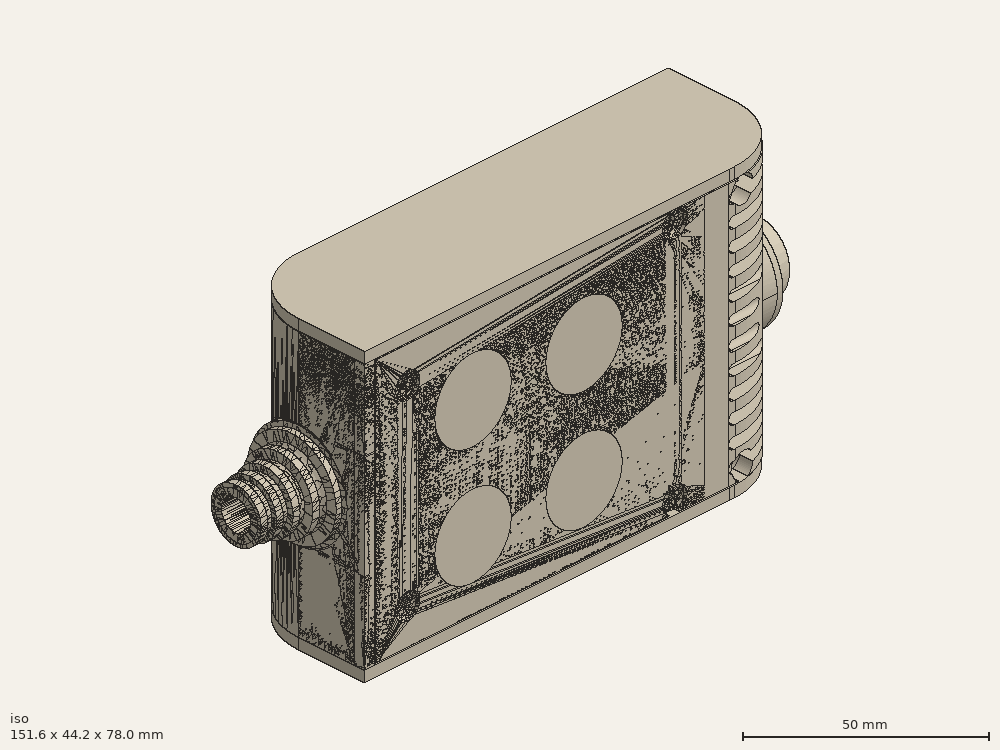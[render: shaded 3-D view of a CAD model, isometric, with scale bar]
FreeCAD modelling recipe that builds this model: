
FCSTD DOCUMENT  (FreeCAD 0.19R0.19.2)
Label: enclosure_198FCStd
License: All rights reserved
LicenseURL: http://en.wikipedia.org/wiki/All_rights_reserved
objects: Part::Revolution×152, Part::MultiFuse×146, Part::Feature×146, Sketcher::SketchObject×84, Part::Cut×70, Part::Cylinder×70, Part::Extrusion×67, Part::Fillet×58, Part::Box×36, App::MeasureDistance×4, PartDesign::Body×2, Image::ImagePlane×1
note: 831 computed .brp shape members not serialized (recipe doc carries the construction recipe); baked Part::Feature solids carry a one-line shape summary decoded from their .brp

FEATURE [Sketcher::SketchObject] Sketch  label="topSketch"
  FullyConstrained = true
  sketch-geometry (20):
    g0: LineSegment StartX=5.21097e-06 StartY=3 StartZ=0 EndX=5.21097e-06 EndY=19 EndZ=0
    g1: ArcOfCircle CenterX=19 CenterY=19 CenterZ=0 NormalX=0 NormalY=0 NormalZ=1 AngleXU=0 Radius=19 StartAngle=1.5708 EndAngle=3.14159
    g2: ArcOfCircle CenterX=19 CenterY=19 CenterZ=0 NormalX=0 NormalY=0 NormalZ=1 AngleXU=0 Radius=16 StartAngle=1.5708 EndAngle=3.14159
    g3: LineSegment StartX=114 StartY=35 StartZ=0 EndX=19 EndY=35 EndZ=0
    g4: LineSegment StartX=5.21097e-06 StartY=3 StartZ=0 EndX=5.21097e-06 EndY=0 EndZ=0
    g5: LineSegment StartX=3 StartY=0 StartZ=0 EndX=5.21097e-06 EndY=0 EndZ=0
    g6: LineSegment StartX=3 StartY=19 StartZ=0 EndX=3 EndY=0 EndZ=0
    g7: LineSegment StartX=19 StartY=38 StartZ=0 EndX=124 EndY=38 EndZ=0
    g8: Circle CenterX=119 CenterY=35 CenterZ=0 NormalX=0 NormalY=0 NormalZ=1 AngleXU=0 Radius=1
    g9: Circle CenterX=121 CenterY=35 CenterZ=0 NormalX=0 NormalY=0 NormalZ=1 AngleXU=0 Radius=1
    g10: Circle CenterX=121 CenterY=33 CenterZ=0 NormalX=0 NormalY=0 NormalZ=1 AngleXU=0 Radius=1
    g11: BSplineCurve PolesCount=3 KnotsCount=2 Degree=2 IsPeriodic=0
    g12: GeomPoint X=119 Y=35 Z=0
    g13: GeomPoint X=121 Y=33 Z=0
    g14: LineSegment StartX=119 StartY=35 StartZ=0 EndX=114 EndY=35 EndZ=0
    g15: ArcOfCircle CenterX=105 CenterY=19 CenterZ=0 NormalX=0 NormalY=0 NormalZ=1 AngleXU=0 Radius=19 StartAngle=5.7297 EndAngle=6.28319
    g16: ArcOfCircle CenterX=105 CenterY=19 CenterZ=0 NormalX=0 NormalY=0 NormalZ=1 AngleXU=0 Radius=16 StartAngle=5.60905 EndAngle=6.28319
    g17: LineSegment StartX=121 StartY=33 StartZ=0 EndX=121 EndY=19 EndZ=0
    g18: LineSegment StartX=124 StartY=38 StartZ=0 EndX=124 EndY=19 EndZ=0
    g19: LineSegment StartX=117.5 StartY=9.01251 StartZ=0 EndX=121.163 EndY=9.0125 EndZ=0
  constraints (46):
    c: Vertical(g0)
    c: Block(g0)
    c: Coincident(g1,g0)
    c: Block(g1)
    c: Coincident(g2,g1)
    c: Block(g2)
    c: Coincident(g3,g2)
    c: Horizontal(g3)
    c: Tangent(g3,g2)
    c: Coincident(g4,g0)
    c: Distance(g4) = 3
    c: Vertical(g4)
    c: Coincident(g5,g4)
    c: Horizontal(g5)
    c: Coincident(g6,g2)
    c: Coincident(g6,g5)
    c: Vertical(g6)
    c: Horizontal(g7)
    c: Distance(g7) = 105
    c: Coincident(g7,g1)
    c: Block(g3)
    c: Weight(g8) = 1
    c: Equal(g8,g9)
    c: Equal(g8,g10)
    c: InternalAlignment(g8,g11)
    c: InternalAlignment(g9,g11)
    c: InternalAlignment(g10,g11)
    c: InternalAlignment(g12,g11)
    c: InternalAlignment(g13,g11)
    c: Block(g11)
    c: Coincident(g14,g11)
    c: Coincident(g14,g3)
    c: Horizontal(g14)
    c: Block(g15)
    c: Coincident(g16,g15)
    c: Block(g16)
    c: Coincident(g17,g11)
    c: Coincident(g17,g16)
    c: Vertical(g17)
    c: Distance(g17) = 14
    c: Coincident(g18,g7)
    c: Coincident(g18,g15)
    c: Vertical(g18)
    c: Distance(g18) = 19
    c: Coincident(g19,g16)
    c: Coincident(g19,g15)
FEATURE [Sketcher::SketchObject] Sketch001  label="bottomSketch"
  FullyConstrained = true
  sketch-geometry (32):
    g0: LineSegment StartX=3.3 StartY=-6.03275e-07 StartZ=0 EndX=98 EndY=-6.03275e-07 EndZ=0
    g1: ArcOfCircle CenterX=98 CenterY=19 CenterZ=0 NormalX=0 NormalY=0 NormalZ=1 AngleXU=0 Radius=19 StartAngle=4.71239 EndAngle=5.71103
    g2: LineSegment StartX=6.3 StartY=8 StartZ=0 EndX=3.3 EndY=8 EndZ=0
    g3: LineSegment StartX=3.3 StartY=8 StartZ=0 EndX=3.3 EndY=-6.03275e-07 EndZ=0
    g4: ArcOfCircle CenterX=8.3 CenterY=5 CenterZ=0 NormalX=0 NormalY=0 NormalZ=1 AngleXU=0 Radius=2 StartAngle=3.14159 EndAngle=4.71239
    g5: LineSegment StartX=6.3 StartY=8 StartZ=0 EndX=6.3 EndY=5 EndZ=0
    g6: ArcOfCircle CenterX=98 CenterY=19 CenterZ=0 NormalX=0 NormalY=0 NormalZ=1 AngleXU=0 Radius=12.7 StartAngle=4.71239 EndAngle=6.28319
    g7: LineSegment StartX=94.7 StartY=3 StartZ=0 EndX=8.3 EndY=3 EndZ=0
    g8-g12: Circle x5 (B-spline internal-alignment scaffolding for g13; pole/knot coordinates omitted)
    g13: BSplineCurve PolesCount=5 KnotsCount=3 Degree=3 IsPeriodic=0
    g14: GeomPoint X=98 Y=6.3 Z=0
    g15: GeomPoint X=96.3938 Y=4.71946 Z=0
    g16: GeomPoint X=94.7 Y=3 Z=0
    g17-g23: Circle x7 (B-spline internal-alignment scaffolding for g24; pole/knot coordinates omitted)
    g24: BSplineCurve PolesCount=7 KnotsCount=5 Degree=3 IsPeriodic=0
    g25-g29: GeomPoint x5 (B-spline internal-alignment scaffolding for g24; pole/knot coordinates omitted)
    g30: ArcOfCircle CenterX=98 CenterY=19 CenterZ=0 NormalX=0 NormalY=0 NormalZ=1 AngleXU=0 Radius=15.7 StartAngle=5.81226 EndAngle=6.28319
    g31: LineSegment StartX=110.7 StartY=19 StartZ=0 EndX=113.7 EndY=19 EndZ=0
  constraints (41):
    c: Horizontal(g0)
    c: Coincident(g1,g0)
    c: Block(g1)
    c: Horizontal(g2)
    c: Distance(g2) = 3
    c: Coincident(g3,g2)
    c: Vertical(g3)
    c: Coincident(g3,g0)
    c: Block(g4)
    c: Block(g2)
    c: Coincident(g5,g2)
    c: Coincident(g5,g4)
    c: Vertical(g5)
    c: Coincident(g6,g1)
    c: Block(g6)
    c: Coincident(g7,g4)
    c: Horizontal(g7)
    c: Block(g0)
    c: Block(g7)
    c: Block(g3)
    c: Coincident(g13,g6)
    c: Weight(g8) = 1
    c: Equal(g8, g9-g12) x4
    c: Coincident(g13,g7)
    c: InternalAlignment(g8-g12 -> g13) x5
    c: InternalAlignment(g14,g13)
    c: InternalAlignment(g15,g13)
    c: InternalAlignment(g16,g13)
    c: Block(g13)
    c: Weight(g17) = 1
    c: Equal(g17, g18-g23) x6
    c: Coincident(g24,g1)
    c: InternalAlignment(g17-g23 -> g24) x7
    c: InternalAlignment(g25-g29 -> g24) x5
    c: Block(g24)
    c: Coincident(g30,g24)
    c: Coincident(g31,g6)
    c: Coincident(g31,g30)
    c: Horizontal(g31)
    c: Block(g31)
    c: Block(g30)
FEATURE [Part::Extrusion] Extrude  label="top"
  Base = -> Sketch
  Dir = (0,0,1)
  DirMode = 2
  FaceMakerClass = Part::FaceMakerBullseye
  LengthFwd = 72
  LengthRev = 0
  Solid = true
  Symmetric = false
FEATURE [Part::Extrusion] Extrude001  label="bottom"
  Base = -> Sketch001
  Dir = (0,0,1)
  DirMode = 2
  FaceMakerClass = Part::FaceMakerBullseye
  LengthFwd = 71.4
  LengthRev = 0
  Placement = pos=(0,0,0.3) rot=(0,0,1;0rad)
  Solid = true
  Symmetric = false
FEATURE [Sketcher::SketchObject] Sketch002  label="topSketch001"
  FullyConstrained = true
  sketch-geometry (8):
    g0: ArcOfCircle CenterX=19 CenterY=19.0975 CenterZ=0 NormalX=0 NormalY=0 NormalZ=1 AngleXU=0 Radius=18.9025 StartAngle=1.5708 EndAngle=3.14674
    g1: LineSegment StartX=0.0977805 StartY=19.0003 StartZ=0 EndX=0.0977805 EndY=0.000251602 EndZ=0
    g2: LineSegment StartX=19 StartY=38 StartZ=0 EndX=124 EndY=38 EndZ=0
    g3: LineSegment StartX=0.0977805 StartY=0.000251602 StartZ=0 EndX=105.098 EndY=0.000251602 EndZ=0
    g4: LineSegment StartX=124 StartY=38 StartZ=0 EndX=125.616 EndY=38 EndZ=0
    g5: LineSegment StartX=105.098 StartY=0.000251602 StartZ=0 EndX=106.713 EndY=0.000251602 EndZ=0
    g6: ArcOfCircle CenterX=106.616 CenterY=19 CenterZ=0 NormalX=0 NormalY=0 NormalZ=1 AngleXU=0 Radius=19 StartAngle=4.71754 EndAngle=6.28319
    g7: LineSegment StartX=125.616 StartY=38 StartZ=0 EndX=125.616 EndY=19 EndZ=0
  constraints (21):
    c: Block(g0)
    c: Coincident(g1,g0)
    c: Vertical(g1)
    c: Horizontal(g2)
    c: Distance(g2) = 105
    c: Coincident(g2,g0)
    c: Distance(g1) = 19
    c: Coincident(g3,g1)
    c: Horizontal(g3)
    c: Distance(g3) = 105
    c: Coincident(g4,g2)
    c: Horizontal(g4)
    c: Distance(g4) = 1.61553
    c: Horizontal(g5)
    c: Equal(g4,g5) = 1.61553
    c: Coincident(g5,g3)
    c: Block(g6)
    c: Coincident(g6,g5)
    c: Coincident(g7,g4)
    c: Coincident(g7,g6)
    c: Vertical(g7)
FEATURE [Part::Extrusion] Extrude002  label="sideA"
  Base = -> Sketch002
  Dir = (0,0,1)
  DirMode = 2
  FaceMakerClass = Part::FaceMakerBullseye
  LengthFwd = 3
  LengthRev = 0
  Placement = pos=(0,0,-3) rot=(0,0,1;0rad)
  Solid = true
  Symmetric = false
FEATURE [Sketcher::SketchObject] Sketch003  label="topSketch002"
  FullyConstrained = true
  sketch-geometry (6):
    g0: LineSegment StartX=19 StartY=38 StartZ=0 EndX=117 EndY=38 EndZ=0
    g1: ArcOfCircle CenterX=19 CenterY=19 CenterZ=0 NormalX=0 NormalY=0 NormalZ=1 AngleXU=0 Radius=19 StartAngle=1.5708 EndAngle=3.14159
    g2: LineSegment StartX=117 StartY=38 StartZ=0 EndX=117 EndY=19 EndZ=0
    g3: LineSegment StartX=98 StartY=1.0161e-12 StartZ=0 EndX=5.22862e-06 EndY=1.0161e-12 EndZ=0
    g4: LineSegment StartX=5.22862e-06 StartY=19 StartZ=0 EndX=5.22862e-06 EndY=1.0161e-12 EndZ=0
    g5: ArcOfCircle CenterX=98 CenterY=19 CenterZ=0 NormalX=0 NormalY=0 NormalZ=1 AngleXU=0 Radius=19 StartAngle=4.71239 EndAngle=6.28319
  constraints (16):
    c: Horizontal(g0)
    c: Distance(g0) = 98
    c: Coincident(g1,g0)
    c: Block(g1)
    c: Coincident(g2,g0)
    c: Vertical(g2)
    c: Distance(g2) = 19
    c: Horizontal(g3)
    c: Coincident(g4,g1)
    c: Vertical(g4)
    c: Coincident(g3,g4)
    c: Block(g3)
    c: Coincident(g5,g2)
    c: Coincident(g5,g3)
    c: Block(g0)
    c: Block(g5)
FEATURE [Sketcher::SketchObject] Sketch004
  FullyConstrained = true
  MapMode = 3
  Placement = pos=(0,0,0) rot=(1,0,0;1.5708rad)
  Support = -> [Extrude]
  sketch-geometry (8):
    g0: Circle CenterX=80.351 CenterY=-67.6202 CenterZ=0 NormalX=0 NormalY=0 NormalZ=1 AngleXU=0 Radius=2
    g1: Circle CenterX=80.351 CenterY=-67.6202 CenterZ=0 NormalX=0 NormalY=0 NormalZ=1 AngleXU=0 Radius=3
    g2: Circle CenterX=80.351 CenterY=-4.92017 CenterZ=0 NormalX=0 NormalY=0 NormalZ=1 AngleXU=0 Radius=2
    g3: Circle CenterX=80.351 CenterY=-4.92017 CenterZ=0 NormalX=0 NormalY=0 NormalZ=1 AngleXU=0 Radius=3
    g4: Circle CenterX=23.851 CenterY=-4.92017 CenterZ=0 NormalX=0 NormalY=0 NormalZ=1 AngleXU=0 Radius=2
    g5: Circle CenterX=23.851 CenterY=-4.92017 CenterZ=0 NormalX=0 NormalY=0 NormalZ=1 AngleXU=0 Radius=3
    g6: Circle CenterX=23.851 CenterY=-67.6202 CenterZ=0 NormalX=0 NormalY=0 NormalZ=1 AngleXU=0 Radius=2
    g7: Circle CenterX=23.851 CenterY=-67.6202 CenterZ=0 NormalX=0 NormalY=0 NormalZ=1 AngleXU=0 Radius=3
  constraints (8):
    c: Block(g3)
    c: Block(g2)
    c: Block(g1)
    c: Block(g0)
    c: Block(g6)
    c: Block(g7)
    c: Block(g4)
    c: Block(g5)
FEATURE [Part::Extrusion] Extrude004
  Base = -> Sketch004
  Dir = (0,-1,2e-16)
  DirMode = 2
  FaceMakerClass = Part::FaceMakerBullseye
  LengthFwd = 6
  LengthRev = 0
  Placement = pos=(0,9,0) rot=(0,0,1;0rad)
  Solid = true
  Symmetric = false
FEATURE [Sketcher::SketchObject] Sketch005
  FullyConstrained = true
  MapMode = 3
  Placement = pos=(0,0,0) rot=(1,0,0;1.5708rad)
  Support = -> [Extrude]
  sketch-geometry (8):
    g0: Circle CenterX=80.351 CenterY=-67.6202 CenterZ=0 NormalX=0 NormalY=0 NormalZ=1 AngleXU=0 Radius=3
    g1: Circle CenterX=80.351 CenterY=-4.92017 CenterZ=0 NormalX=0 NormalY=0 NormalZ=1 AngleXU=0 Radius=3
    g2: Circle CenterX=23.851 CenterY=-4.92017 CenterZ=0 NormalX=0 NormalY=0 NormalZ=1 AngleXU=0 Radius=3
    g3: Circle CenterX=23.851 CenterY=-67.6202 CenterZ=0 NormalX=0 NormalY=0 NormalZ=1 AngleXU=0 Radius=3
    g4: Circle CenterX=23.851 CenterY=-67.6202 CenterZ=0 NormalX=0 NormalY=0 NormalZ=1 AngleXU=0 Radius=5
    g5: Circle CenterX=80.351 CenterY=-67.6202 CenterZ=0 NormalX=0 NormalY=0 NormalZ=1 AngleXU=0 Radius=5
    g6: Circle CenterX=23.851 CenterY=-4.92017 CenterZ=0 NormalX=0 NormalY=0 NormalZ=1 AngleXU=0 Radius=5
    g7: Circle CenterX=80.351 CenterY=-4.92017 CenterZ=0 NormalX=0 NormalY=0 NormalZ=1 AngleXU=0 Radius=5
  constraints (8):
    c: Block(g1)
    c: Block(g0)
    c: Block(g3)
    c: Block(g2)
    c: Block(g5)
    c: Block(g4)
    c: Block(g6)
    c: Block(g7)
FEATURE [Part::Extrusion] Extrude005
  Base = -> Sketch005
  Dir = (0,-1,2e-16)
  DirMode = 2
  FaceMakerClass = Part::FaceMakerBullseye
  LengthFwd = 2
  LengthRev = 0
  Solid = true
  Symmetric = false
FEATURE [Sketcher::SketchObject] Sketch006
  FullyConstrained = true
  MapMode = 3
  Placement = pos=(0,0,0) rot=(1,0,0;1.5708rad)
  sketch-geometry (8):
    g0: Circle CenterX=80.351 CenterY=-67.6202 CenterZ=0 NormalX=0 NormalY=0 NormalZ=1 AngleXU=0 Radius=3
    g1: Circle CenterX=80.351 CenterY=-4.92017 CenterZ=0 NormalX=0 NormalY=0 NormalZ=1 AngleXU=0 Radius=3
    g2: Circle CenterX=23.851 CenterY=-4.92017 CenterZ=0 NormalX=0 NormalY=0 NormalZ=1 AngleXU=0 Radius=3
    g3: Circle CenterX=23.851 CenterY=-67.6202 CenterZ=0 NormalX=0 NormalY=0 NormalZ=1 AngleXU=0 Radius=3
    g4: Circle CenterX=23.851 CenterY=-67.6202 CenterZ=0 NormalX=0 NormalY=0 NormalZ=1 AngleXU=0 Radius=5
    g5: Circle CenterX=80.351 CenterY=-67.6202 CenterZ=0 NormalX=0 NormalY=0 NormalZ=1 AngleXU=0 Radius=5
    g6: Circle CenterX=23.851 CenterY=-4.92017 CenterZ=0 NormalX=0 NormalY=0 NormalZ=1 AngleXU=0 Radius=5
    g7: Circle CenterX=80.351 CenterY=-4.92017 CenterZ=0 NormalX=0 NormalY=0 NormalZ=1 AngleXU=0 Radius=5
  constraints (8):
    c: Block(g1)
    c: Block(g0)
    c: Block(g3)
    c: Block(g2)
    c: Block(g5)
    c: Block(g4)
    c: Block(g6)
    c: Block(g7)
FEATURE [Part::Extrusion] Extrude007
  Base = -> Sketch006
  Dir = (0,-1,2e-16)
  DirMode = 2
  FaceMakerClass = Part::FaceMakerBullseye
  LengthFwd = 2
  LengthRev = 0
  Solid = true
  Symmetric = false
FEATURE [Part::Fillet] Fillet
  Base = -> Extrude007
  Edges = 4 edges r=1.99: [Edge6,Edge12,Edge18,Edge24]
FEATURE [Part::Cut] Cut
  Base = -> Extrude005
  Placement = pos=(0,5,0) rot=(0,0,1;0rad)
  Tool = -> Fillet
FEATURE [Part::MultiFuse] Fusion  label="pCBScrews"
  Placement = pos=(-2.5,0,72.3) rot=(0,0,1;0rad)
  Shapes = -> [Extrude004,Cut]
FEATURE [App::MeasureDistance] Distance  label="Distance: 0.69 mm"
  Distance = 0.685967
  P1 = (24.0138,2.9647,0.3)
  P2 = (23.8901,3,-0.373787)
FEATURE [App::MeasureDistance] Distance001  label="Distance: 0.53 mm"
  Distance = 0.533607
  P1 = (80.2939,3,72.2334)
  P2 = (80.281,2.99661,71.7)
FEATURE [Part::Fillet] Fillet001
  Base = -> Extrude001
  Edges = 1 edges r=2.4: [Edge17]
FEATURE [Part::Fillet] Fillet002  label="bottom001"
  Base = -> Fillet001
  Edges = 1 edges r=2.4: [Edge36]
FEATURE [Part::Fillet] Fillet003  label="top001"
  Base = -> Extrude
  Edges = 1 edges r=2: [Edge1]
FEATURE [Sketcher::SketchObject] Sketch007
  FullyConstrained = true
  sketch-geometry (16):
    g0: LineSegment StartX=4 StartY=0 StartZ=0 EndX=4 EndY=2.4 EndZ=0
    g1: LineSegment StartX=4 StartY=2.4 StartZ=0 EndX=7 EndY=2.4 EndZ=0
    g2: LineSegment StartX=4 StartY=0 StartZ=0 EndX=5.7 EndY=0 EndZ=0
    g3: LineSegment StartX=5.7 StartY=0 StartZ=0 EndX=5.7 EndY=-5.6 EndZ=0
    g4-g8: Circle x5 (B-spline internal-alignment scaffolding for g9; pole/knot coordinates omitted)
    g9: BSplineCurve PolesCount=5 KnotsCount=3 Degree=3 IsPeriodic=0
    g10: GeomPoint X=7 Y=2.4 Z=0
    g11: GeomPoint X=10.4582 Y=-1.55472 Z=0
    g12: GeomPoint X=14 Y=-5.6 Z=0
    g13: LineSegment StartX=14 StartY=-5.6 StartZ=0 EndX=14 EndY=-14.1 EndZ=0
    g14: LineSegment StartX=14 StartY=-14.1 StartZ=0 EndX=6.5 EndY=-14.1 EndZ=0
    g15: LineSegment StartX=5.7 StartY=-5.6 StartZ=0 EndX=6.5 EndY=-14.1 EndZ=0
  constraints (28):
    c: Distance(g0) = 2.4
    c: Vertical(g0)
    c: Block(g0)
    c: Coincident(g1,g0)
    c: Horizontal(g1)
    c: Distance(g1) = 3
    c: Coincident(g2,g0)
    c: Horizontal(g2)
    c: Distance(g2) = 1.7
    c: Coincident(g3,g2)
    c: Vertical(g3)
    c: Distance(g3) = 5.6
    c: Coincident(g9,g1)
    c: Weight(g4) = 1
    c: Equal(g4, g5-g8) x4
    c: InternalAlignment(g4-g8 -> g9) x5
    c: InternalAlignment(g10,g9)
    c: InternalAlignment(g11,g9)
    c: InternalAlignment(g12,g9)
    c: Block(g9)
    c: Coincident(g13,g9)
    c: Vertical(g13)
    c: Distance(g13) = 8.5
    c: Coincident(g14,g13)
    c: Horizontal(g14)
    c: Distance(g14) = 7.5
    c: Coincident(g15,g3)
    c: Coincident(g15,g14)
FEATURE [Part::Feature] Face
  shape: bbox 10 x 16.5 x 2e-07 mm, 1 faces, 0 solids (baked)
FEATURE [Part::Revolution] Revolve  label="plugHousing"
  Angle = 360
  Axis = (0,1,0)
  Base = (0,0,0)
  FaceMakerClass = Part::FaceMakerBullseye
  Placement = pos=(0,0,36.15) rot=(0,0,1;0rad)
  Solid = false
  Source = -> Face
  Symmetric = false
FEATURE [Part::Feature] Face001
  shape: bbox 10 x 16.5 x 2e-07 mm, 1 faces, 0 solids (baked)
FEATURE [Part::Revolution] Revolve001  label="plugHousing001"
  Angle = 360
  Axis = (0,1,0)
  Base = (0,0,0)
  FaceMakerClass = Part::FaceMakerBullseye
  Placement = pos=(0,0,36.15) rot=(0,0,1;0rad)
  Solid = false
  Source = -> Face001
  Symmetric = false
FEATURE [Part::MultiFuse] Fusion001  label="plugHousing002"
  Placement = pos=(0,0,0) rot=(0,0,1;1.5708rad)
  Shapes = -> [Revolve001,Revolve]
FEATURE [Part::Feature] Face002
  shape: bbox 10 x 16.5 x 2e-07 mm, 1 faces, 0 solids (baked)
FEATURE [Part::Revolution] Revolve003  label="plugHousing005"
  Angle = 360
  Axis = (0,1,0)
  Base = (0,0,0)
  FaceMakerClass = Part::FaceMakerBullseye
  Placement = pos=(0,0,36.15) rot=(0,0,1;0rad)
  Solid = false
  Source = -> Face002
  Symmetric = false
FEATURE [Part::Feature] Face003
  shape: bbox 10 x 16.5 x 2e-07 mm, 1 faces, 0 solids (baked)
FEATURE [Part::Revolution] Revolve002  label="plugHousing003"
  Angle = 360
  Axis = (0,1,0)
  Base = (0,0,0)
  FaceMakerClass = Part::FaceMakerBullseye
  Placement = pos=(0,0,36.15) rot=(0,0,1;0rad)
  Solid = false
  Source = -> Face003
  Symmetric = false
FEATURE [Part::MultiFuse] Fusion002  label="plugHousing004"
  Placement = pos=(0,0,0) rot=(0,0,1;1.5708rad)
  Shapes = -> [Revolve002,Revolve003]
FEATURE [Part::MultiFuse] Fusion003  label="plugHousing006"
  Placement = pos=(0,19,0) rot=(0,0,1;3.14159rad)
  Shapes = -> [Fusion002,Fusion001]
FEATURE [Part::Feature] Face004
  shape: bbox 10 x 16.5 x 2e-07 mm, 1 faces, 0 solids (baked)
FEATURE [Part::Revolution] Revolve006  label="plugHousing010"
  Angle = 360
  Axis = (0,1,0)
  Base = (0,0,0)
  FaceMakerClass = Part::FaceMakerBullseye
  Placement = pos=(0,0,36.15) rot=(0,0,1;0rad)
  Solid = false
  Source = -> Face004
  Symmetric = false
FEATURE [Part::Feature] Face005
  shape: bbox 10 x 16.5 x 2e-07 mm, 1 faces, 0 solids (baked)
FEATURE [Part::Revolution] Revolve007  label="plugHousing011"
  Angle = 360
  Axis = (0,1,0)
  Base = (0,0,0)
  FaceMakerClass = Part::FaceMakerBullseye
  Placement = pos=(0,0,36.15) rot=(0,0,1;0rad)
  Solid = false
  Source = -> Face005
  Symmetric = false
FEATURE [Part::Feature] Face006
  shape: bbox 10 x 16.5 x 2e-07 mm, 1 faces, 0 solids (baked)
FEATURE [Part::Revolution] Revolve004  label="plugHousing007"
  Angle = 360
  Axis = (0,1,0)
  Base = (0,0,0)
  FaceMakerClass = Part::FaceMakerBullseye
  Placement = pos=(0,0,36.15) rot=(0,0,1;0rad)
  Solid = false
  Source = -> Face006
  Symmetric = false
FEATURE [Part::MultiFuse] Fusion004  label="plugHousing009"
  Placement = pos=(0,0,0) rot=(0,0,1;1.5708rad)
  Shapes = -> [Revolve004,Revolve007]
FEATURE [Part::Feature] Face007
  shape: bbox 10 x 16.5 x 2e-07 mm, 1 faces, 0 solids (baked)
FEATURE [Part::Revolution] Revolve005  label="plugHousing008"
  Angle = 360
  Axis = (0,1,0)
  Base = (0,0,0)
  FaceMakerClass = Part::FaceMakerBullseye
  Placement = pos=(0,0,36.15) rot=(0,0,1;0rad)
  Solid = false
  Source = -> Face007
  Symmetric = false
FEATURE [Part::MultiFuse] Fusion005  label="plugHousing012"
  Placement = pos=(0,0,0) rot=(0,0,1;1.5708rad)
  Shapes = -> [Revolve006,Revolve005]
FEATURE [Part::MultiFuse] Fusion006  label="plugHousing013"
  Placement = pos=(0,19,0) rot=(0,0,1;3.14159rad)
  Shapes = -> [Fusion005,Fusion004]
FEATURE [Part::MultiFuse] Fusion007  label="plugHousing014"
  Placement = pos=(122.621,0,-0.15) rot=(0,0,1;0rad)
  Shapes = -> [Fusion003,Fusion006]
FEATURE [Part::Cylinder] Cylinder002
  Angle = 360
  AttacherType = Attacher::AttachEngine3D
  Height = 20
  Placement = pos=(0,0,36.15) rot=(0,0,1;0rad)
  Radius = 4
FEATURE [Part::Cylinder] Cylinder003
  Angle = 360
  AttacherType = Attacher::AttachEngine3D
  Height = 10
  Placement = pos=(0,0,36.15) rot=(0,0,1;0rad)
  Radius = 4
FEATURE [Part::MultiFuse] Fusion009  label="removeToCreateHoleForPlugHousing"
  Placement = pos=(70,19,36.15) rot=(0,1,0;1.5708rad)
  Shapes = -> [Cylinder002,Cylinder003]
FEATURE [Part::Cylinder] Cylinder004
  Angle = 360
  AttacherType = Attacher::AttachEngine3D
  Height = 20
  Placement = pos=(0,0,36.15) rot=(0,0,1;0rad)
  Radius = 4
FEATURE [Part::Cylinder] Cylinder005
  Angle = 360
  AttacherType = Attacher::AttachEngine3D
  Height = 10
  Placement = pos=(0,0,36.15) rot=(0,0,1;0rad)
  Radius = 4
FEATURE [Part::MultiFuse] Fusion010  label="removeToCreateHoleForPlugHousing001"
  Placement = pos=(70,19,36.15) rot=(0,1,0;1.5708rad)
  Shapes = -> [Cylinder004,Cylinder005]
FEATURE [Part::Cut] Cut001
  Base = -> Fillet003
  Tool = -> Fusion010
FEATURE [Part::Cut] Cut002  label="Bottom"
  Base = -> Fillet002
  Tool = -> Fusion009
FEATURE [Part::Feature] Face008
  shape: bbox 10 x 16.5 x 2e-07 mm, 1 faces, 0 solids (baked)
FEATURE [Part::Revolution] Revolve011  label="plugHousing021"
  Angle = 360
  Axis = (0,1,0)
  Base = (0,0,0)
  FaceMakerClass = Part::FaceMakerBullseye
  Placement = pos=(0,0,36.15) rot=(0,0,1;0rad)
  Solid = false
  Source = -> Face008
  Symmetric = false
FEATURE [Part::Feature] Face009
  shape: bbox 10 x 16.5 x 2e-07 mm, 1 faces, 0 solids (baked)
FEATURE [Part::Revolution] Revolve012  label="plugHousing022"
  Angle = 360
  Axis = (0,1,0)
  Base = (0,0,0)
  FaceMakerClass = Part::FaceMakerBullseye
  Placement = pos=(0,0,36.15) rot=(0,0,1;0rad)
  Solid = false
  Source = -> Face009
  Symmetric = false
FEATURE [Part::Feature] Face010 .. Face013  x4 (patterned run collapsed; names and placements below)
  shape: bbox 10 x 16.5 x 2e-07 mm, 1 faces, 0 solids (baked)
FEATURE [Part::Revolution] Revolve015  label="plugHousing027"
  Angle = 360
  Axis = (0,1,0)
  Base = (0,0,0)
  FaceMakerClass = Part::FaceMakerBullseye
  Placement = pos=(0,0,36.15) rot=(0,0,1;0rad)
  Solid = false
  Source = -> Face013
  Symmetric = false
FEATURE [Part::Feature] Face014
  shape: bbox 10 x 16.5 x 2e-07 mm, 1 faces, 0 solids (baked)
FEATURE [Part::Feature] Face015
  shape: bbox 10 x 16.5 x 2e-07 mm, 1 faces, 0 solids (baked)
FEATURE [Part::Feature] Face016
  shape: bbox 10 x 16.5 x 2e-07 mm, 1 faces, 0 solids (baked)
FEATURE [Part::Revolution] Revolve019  label="plugHousing033"
  Angle = 360
  Axis = (0,1,0)
  Base = (0,0,0)
  FaceMakerClass = Part::FaceMakerBullseye
  Placement = pos=(0,0,36.15) rot=(0,0,1;0rad)
  Solid = false
  Source = -> Face016
  Symmetric = false
FEATURE [Part::Feature] Face017
  shape: bbox 10 x 16.5 x 2e-07 mm, 1 faces, 0 solids (baked)
FEATURE [Part::Revolution] Revolve020  label="plugHousing034"
  Angle = 360
  Axis = (0,1,0)
  Base = (0,0,0)
  FaceMakerClass = Part::FaceMakerBullseye
  Placement = pos=(0,0,36.15) rot=(0,0,1;0rad)
  Solid = false
  Source = -> Face017
  Symmetric = false
FEATURE [Part::Feature] Face018
  shape: bbox 10 x 16.5 x 2e-07 mm, 1 faces, 0 solids (baked)
FEATURE [Part::Revolution] Revolve016  label="plugHousing030"
  Angle = 360
  Axis = (0,1,0)
  Base = (0,0,0)
  FaceMakerClass = Part::FaceMakerBullseye
  Placement = pos=(0,0,36.15) rot=(0,0,1;0rad)
  Solid = false
  Source = -> Face018
  Symmetric = false
FEATURE [Part::MultiFuse] Fusion020  label="plugHousing038"
  Placement = pos=(0,0,0) rot=(0,0,1;1.5708rad)
  Shapes = -> [Revolve016,Revolve020]
FEATURE [Part::Feature] Face019
  shape: bbox 10 x 16.5 x 2e-07 mm, 1 faces, 0 solids (baked)
FEATURE [Part::Feature] Face020
  shape: bbox 10 x 16.5 x 2e-07 mm, 1 faces, 0 solids (baked)
FEATURE [Part::Revolution] Revolve017  label="plugHousing031"
  Angle = 360
  Axis = (0,1,0)
  Base = (0,0,0)
  FaceMakerClass = Part::FaceMakerBullseye
  Placement = pos=(0,0,36.15) rot=(0,0,1;0rad)
  Solid = false
  Source = -> Face020
  Symmetric = false
FEATURE [Part::MultiFuse] Fusion021  label="plugHousing039"
  Placement = pos=(0,0,0) rot=(0,0,1;1.5708rad)
  Shapes = -> [Revolve019,Revolve017]
FEATURE [Part::MultiFuse] Fusion023  label="plugHousing041"
  Placement = pos=(0,19,0) rot=(0,0,1;3.14159rad)
  Shapes = -> [Fusion021,Fusion020]
FEATURE [Part::Revolution] Revolve022  label="plugHousing043"
  Angle = 360
  Axis = (0,1,0)
  Base = (0,0,0)
  FaceMakerClass = Part::FaceMakerBullseye
  Placement = pos=(0,0,36.15) rot=(0,0,1;0rad)
  Solid = false
  Source = -> Face019
  Symmetric = false
FEATURE [Part::Feature] Face021
  shape: bbox 10 x 16.5 x 2e-07 mm, 1 faces, 0 solids (baked)
FEATURE [Part::Revolution] Revolve023  label="plugHousing044"
  Angle = 360
  Axis = (0,1,0)
  Base = (0,0,0)
  FaceMakerClass = Part::FaceMakerBullseye
  Placement = pos=(0,0,36.15) rot=(0,0,1;0rad)
  Solid = false
  Source = -> Face021
  Symmetric = false
FEATURE [Part::Feature] Face022
  shape: bbox 10 x 16.5 x 2e-07 mm, 1 faces, 0 solids (baked)
FEATURE [Part::Revolution] Revolve018  label="plugHousing032"
  Angle = 360
  Axis = (0,1,0)
  Base = (0,0,0)
  FaceMakerClass = Part::FaceMakerBullseye
  Placement = pos=(0,0,36.15) rot=(0,0,1;0rad)
  Solid = false
  Source = -> Face022
  Symmetric = false
FEATURE [Part::MultiFuse] Fusion022  label="plugHousing040"
  Placement = pos=(0,0,0) rot=(0,0,1;1.5708rad)
  Shapes = -> [Revolve018,Revolve023]
FEATURE [Part::Feature] Face023
  shape: bbox 10 x 16.5 x 2e-07 mm, 1 faces, 0 solids (baked)
FEATURE [Part::Revolution] Revolve021  label="plugHousing035"
  Angle = 360
  Axis = (0,1,0)
  Base = (0,0,0)
  FaceMakerClass = Part::FaceMakerBullseye
  Placement = pos=(0,0,36.15) rot=(0,0,1;0rad)
  Solid = false
  Source = -> Face023
  Symmetric = false
FEATURE [Part::MultiFuse] Fusion018  label="plugHousing036"
  Placement = pos=(0,0,0) rot=(0,0,1;1.5708rad)
  Shapes = -> [Revolve022,Revolve021]
FEATURE [Part::MultiFuse] Fusion019  label="plugHousing037"
  Placement = pos=(0,19,0) rot=(0,0,1;3.14159rad)
  Shapes = -> [Fusion018,Fusion022]
FEATURE [Part::MultiFuse] Fusion024  label="plugHousing042"
  Placement = pos=(122.621,0,-0.15) rot=(0,0,1;0rad)
  Shapes = -> [Fusion023,Fusion019]
FEATURE [Part::Cylinder] Cylinder006
  Angle = 360
  AttacherType = Attacher::AttachEngine3D
  Height = 20
  Placement = pos=(0,0,36.15) rot=(0,0,1;0rad)
  Radius = 14.3
FEATURE [Part::Cylinder] Cylinder007
  Angle = 360
  AttacherType = Attacher::AttachEngine3D
  Height = 10
  Placement = pos=(0,0,36.15) rot=(0,0,1;0rad)
  Radius = 4
FEATURE [Part::MultiFuse] Fusion026  label="removeToCreteHoleForPlugHousing"
  Placement = pos=(70,19,36) rot=(0,1,0;1.5708rad)
  Shapes = -> [Cylinder006,Cylinder007]
FEATURE [Part::Box] Box001  label="Cube001"
  AttacherType = Attacher::AttachEngine3D
  Height = 28
  Length = 3
  Placement = pos=(110.7,19,22) rot=(0,0,1;0rad)
  Width = 15.7
FEATURE [Part::Cut] Cut003  label="top002"
  Base = -> Cut001
  Tool = -> Fusion007
FEATURE [Part::Revolution] Revolve008  label="plugHousing015"
  Angle = 360
  Axis = (0,1,0)
  Base = (0,0,0)
  FaceMakerClass = Part::FaceMakerBullseye
  Placement = pos=(0,0,36.15) rot=(0,0,1;0rad)
  Solid = false
  Source = -> Face010
  Symmetric = false
FEATURE [Part::MultiFuse] Fusion013  label="plugHousing020"
  Placement = pos=(0,0,0) rot=(0,0,1;1.5708rad)
  Shapes = -> [Revolve008,Revolve012]
FEATURE [Part::Cut] Cut004  label="top003"
  Base = -> Cut003
  Placement = pos=(1,0,0) rot=(0,0,1;0rad)
  Tool = -> Fusion026
FEATURE [Part::Cylinder] Cylinder008
  Angle = 360
  AttacherType = Attacher::AttachEngine3D
  Height = 20
  Placement = pos=(0,0,36.15) rot=(0,0,1;0rad)
  Radius = 10.3
FEATURE [Part::Cylinder] Cylinder009
  Angle = 360
  AttacherType = Attacher::AttachEngine3D
  Height = 10
  Placement = pos=(0,0,36.15) rot=(0,0,1;0rad)
  Radius = 4
FEATURE [Part::MultiFuse] Fusion027  label="removeToCreteHoleForPlugHousing001"
  Placement = pos=(70,19,36) rot=(0,1,0;1.5708rad)
  Shapes = -> [Cylinder008,Cylinder009]
FEATURE [Part::Cut] Cut005  label="plugHousingTab"
  Base = -> Box001
  Tool = -> Fusion027
FEATURE [Part::MultiFuse] Fusion028  label="plugHousing045"
  Shapes = -> [Fusion024,Cut005]
FEATURE [Part::Box] Box002  label="Cube002"
  AttacherType = Attacher::AttachEngine3D
  Height = 28.8
  Length = 3
  Placement = pos=(107.3,28,21.6) rot=(0,0,1;0rad)
  Width = 7
FEATURE [Part::Box] Box003  label="Cube003"
  AttacherType = Attacher::AttachEngine3D
  Height = 3
  Length = 6.4
  Placement = pos=(107.3,28,18.6) rot=(0,0,1;0rad)
  Width = 7
FEATURE [Part::Box] Box004  label="Cube004"
  AttacherType = Attacher::AttachEngine3D
  Height = 3
  Length = 6.4
  Placement = pos=(107.3,28,50.4) rot=(0,0,1;0rad)
  Width = 7
FEATURE [Part::MultiFuse] Fusion029  label="plugHousingBracketHolder"
  Shapes = -> [Box004,Box002,Box003]
FEATURE [Part::Cylinder] Cylinder010
  Angle = 360
  AttacherType = Attacher::AttachEngine3D
  Height = 20
  Placement = pos=(0,0,36.15) rot=(0,0,1;0rad)
  Radius = 14.3
FEATURE [Part::Cylinder] Cylinder011
  Angle = 360
  AttacherType = Attacher::AttachEngine3D
  Height = 10
  Placement = pos=(0,0,36.15) rot=(0,0,1;0rad)
  Radius = 4
FEATURE [Part::MultiFuse] Fusion030  label="removeToCreteHoleForPlugHousing002"
  Placement = pos=(70,19,36) rot=(0,1,0;1.5708rad)
  Shapes = -> [Cylinder010,Cylinder011]
FEATURE [Part::Cut] Cut006  label="plugHousingBracketHolder001"
  Base = -> Fusion029
  Tool = -> Fusion030
FEATURE [Part::Cylinder] Cylinder012
  Angle = 360
  AttacherType = Attacher::AttachEngine3D
  Height = 20
  Placement = pos=(0,0,36.15) rot=(0,0,1;0rad)
  Radius = 7
FEATURE [Part::Cylinder] Cylinder013
  Angle = 360
  AttacherType = Attacher::AttachEngine3D
  Height = 10
  Placement = pos=(0,0,36.15) rot=(0,0,1;0rad)
  Radius = 4
FEATURE [Part::MultiFuse] Fusion032  label="removeToCreteHoleForPlugHousing003"
  Placement = pos=(70,19,36) rot=(0,1,0;1.5708rad)
  Shapes = -> [Cylinder012,Cylinder013]
FEATURE [Part::Cut] Cut007  label="bottom002"
  Base = -> Cut002
  Tool = -> Fusion032
FEATURE [Sketcher::SketchObject] Sketch008
  FullyConstrained = true
  sketch-geometry (54):
    g0: LineSegment StartX=-4.2 StartY=0 StartZ=0 EndX=-6.2 EndY=0 EndZ=0
    g1: LineSegment StartX=-14 StartY=-18 StartZ=0 EndX=-14 EndY=-26.5 EndZ=0
    g2: LineSegment StartX=-4.2 StartY=0 StartZ=0 EndX=-4.2 EndY=-13.4877 EndZ=0
    g3: Circle CenterX=-4.2 CenterY=-13.4877 CenterZ=0 NormalX=0 NormalY=0 NormalZ=1 AngleXU=0 Radius=1
    g4: Circle CenterX=-4.2 CenterY=-26.5 CenterZ=0 NormalX=0 NormalY=0 NormalZ=1 AngleXU=0 Radius=1
    g5: Circle CenterX=-8.2 CenterY=-26.5 CenterZ=0 NormalX=0 NormalY=0 NormalZ=1 AngleXU=0 Radius=1
    g6: BSplineCurve PolesCount=3 KnotsCount=2 Degree=2 IsPeriodic=0
    g7: GeomPoint X=-4.2 Y=-13.4877 Z=0
    g8: GeomPoint X=-8.2 Y=-26.5 Z=0
    g9: LineSegment StartX=-14 StartY=-26.5 StartZ=0 EndX=-8.2 EndY=-26.5 EndZ=0
    g10: LineSegment StartX=-10.15 StartY=-12 StartZ=0 EndX=-10.15 EndY=-14 EndZ=0
    g11: LineSegment StartX=-12.8401 StartY=-16 StartZ=0 EndX=-10.1571 EndY=-16 EndZ=0
    g12: LineSegment StartX=-10.15 StartY=-14 StartZ=0 EndX=-8.70761 EndY=-14 EndZ=0
    g13: LineSegment StartX=-12.8401 StartY=-16 StartZ=0 EndX=-12.8401 EndY=-17.6958 EndZ=0
    g14: LineSegment StartX=-10.15 StartY=-12 StartZ=0 EndX=-7.79258 EndY=-12 EndZ=0
    g15: Circle CenterX=-6.2215 CenterY=-2 CenterZ=0 NormalX=0 NormalY=0 NormalZ=1 AngleXU=0 Radius=1
    g16: Circle CenterX=-6.22762 CenterY=-2.58724 CenterZ=0 NormalX=0 NormalY=0 NormalZ=1 AngleXU=0 Radius=1
    g17: Circle CenterX=-6.32538 CenterY=-4 CenterZ=0 NormalX=0 NormalY=0 NormalZ=1 AngleXU=0 Radius=1
    g18: BSplineCurve PolesCount=3 KnotsCount=2 Degree=2 IsPeriodic=0
    g19: GeomPoint X=-6.2215 Y=-2 Z=0
    g20: GeomPoint X=-6.32538 Y=-4 Z=0
    g21: Circle CenterX=-6.48644 CenterY=-5.99526 CenterZ=0 NormalX=0 NormalY=0 NormalZ=1 AngleXU=0 Radius=1
    g22: Circle CenterX=-6.58486 CenterY=-6.99526 CenterZ=0 NormalX=0 NormalY=0 NormalZ=1 AngleXU=0 Radius=1
    g23: Circle CenterX=-6.77343 CenterY=-8 CenterZ=0 NormalX=0 NormalY=0 NormalZ=1 AngleXU=0 Radius=1
    g24: BSplineCurve PolesCount=3 KnotsCount=2 Degree=2 IsPeriodic=0
    g25: GeomPoint X=-6.48644 Y=-5.99526 Z=0
    g26: GeomPoint X=-6.77343 Y=-8 Z=0
    g27: Circle CenterX=-7.19003 CenterY=-10 CenterZ=0 NormalX=0 NormalY=0 NormalZ=1 AngleXU=0 Radius=1
    g28: Circle CenterX=-7.44407 CenterY=-11.0915 CenterZ=0 NormalX=0 NormalY=0 NormalZ=1 AngleXU=0 Radius=1
    g29: Circle CenterX=-7.79258 CenterY=-12 CenterZ=0 NormalX=0 NormalY=0 NormalZ=1 AngleXU=0 Radius=1
    g30: BSplineCurve PolesCount=3 KnotsCount=2 Degree=2 IsPeriodic=0
    g31: GeomPoint X=-7.19003 Y=-10 Z=0
    g32: GeomPoint X=-7.79258 Y=-12 Z=0
    g33: Circle CenterX=-8.70761 CenterY=-14 CenterZ=0 NormalX=0 NormalY=0 NormalZ=1 AngleXU=0 Radius=1
    g34: Circle CenterX=-9.33087 CenterY=-15.1837 CenterZ=0 NormalX=0 NormalY=0 NormalZ=1 AngleXU=0 Radius=1
    g35: Circle CenterX=-10.1571 CenterY=-16 CenterZ=0 NormalX=0 NormalY=0 NormalZ=1 AngleXU=0 Radius=1
    g36: BSplineCurve PolesCount=3 KnotsCount=2 Degree=2 IsPeriodic=0
    g37: GeomPoint X=-8.70761 Y=-14 Z=0
    g38: GeomPoint X=-10.1571 Y=-16 Z=0
    g39: Circle CenterX=-12.8401 CenterY=-17.6958 CenterZ=0 NormalX=0 NormalY=0 NormalZ=1 AngleXU=0 Radius=1
    g40: Circle CenterX=-13.3521 CenterY=-17.9027 CenterZ=0 NormalX=0 NormalY=0 NormalZ=1 AngleXU=0 Radius=1
    g41: Circle CenterX=-14 CenterY=-18 CenterZ=0 NormalX=0 NormalY=0 NormalZ=1 AngleXU=0 Radius=1
    g42: BSplineCurve PolesCount=3 KnotsCount=2 Degree=2 IsPeriodic=0
    g43: GeomPoint X=-12.8401 Y=-17.6958 Z=0
    g44: GeomPoint X=-14 Y=-18 Z=0
    g45: LineSegment StartX=-6.2 StartY=0 StartZ=0 EndX=-7.2 EndY=0 EndZ=0
    g46: LineSegment StartX=-7.2 StartY=0 StartZ=0 EndX=-7.2 EndY=-2 EndZ=0
    g47: LineSegment StartX=-7.2 StartY=-2 StartZ=0 EndX=-6.2215 EndY=-2 EndZ=0
    g48: LineSegment StartX=-6.32538 StartY=-4 StartZ=0 EndX=-7.65538 EndY=-4 EndZ=0
    g49: LineSegment StartX=-7.65538 StartY=-4 StartZ=0 EndX=-7.65538 EndY=-5.99526 EndZ=0
    g50: LineSegment StartX=-7.65538 StartY=-5.99526 StartZ=0 EndX=-6.48644 EndY=-5.99526 EndZ=0
    g51: LineSegment StartX=-6.77343 StartY=-8 StartZ=0 EndX=-8.43343 EndY=-8 EndZ=0
    g52: LineSegment StartX=-8.43343 StartY=-8 StartZ=0 EndX=-8.43343 EndY=-10 EndZ=0
    g53: LineSegment StartX=-8.43343 StartY=-10 StartZ=0 EndX=-7.19003 EndY=-10 EndZ=0
  constraints (112):
    c: Horizontal(g0)
    c: Distance(g0) = 2
    c: Block(g0)
    c: Vertical(g1)
    c: Coincident(g2,g0)
    c: Vertical(g2)
    c: Block(g2)
    c: Coincident(g6,g2)
    c: Weight(g3) = 1
    c: Equal(g3,g4)
    c: Equal(g3,g5)
    c: InternalAlignment(g3,g6)
    c: InternalAlignment(g4,g6)
    c: InternalAlignment(g5,g6)
    c: InternalAlignment(g7,g6)
    c: InternalAlignment(g8,g6)
    c: Block(g6)
    c: Coincident(g9,g1)
    c: Coincident(g9,g6)
    c: Horizontal(g9)
    c: Vertical(g10)
    c: Block(g10)
    c: Horizontal(g11)
    c: Block(g11)
    c: Coincident(g12,g10)
    c: Horizontal(g12)
    c: Block(g12)
    c: Coincident(g13,g11)
    c: Vertical(g13)
    c: Block(g13)
    c: Coincident(g14,g10)
    c: Horizontal(g14)
    c: Block(g14)
    c: Block(g9)
    c: Block(g1)
    c: Weight(g15) = 1
    c: Equal(g15,g16)
    c: Equal(g15,g17)
    c: InternalAlignment(g15,g18)
    c: InternalAlignment(g16,g18)
    c: InternalAlignment(g17,g18)
    c: InternalAlignment(g19,g18)
    c: InternalAlignment(g20,g18)
    c: Weight(g21) = 1
    c: Equal(g21,g22)
    c: Equal(g21,g23)
    c: InternalAlignment(g21,g24)
    c: InternalAlignment(g22,g24)
    c: InternalAlignment(g23,g24)
    c: InternalAlignment(g25,g24)
    c: InternalAlignment(g26,g24)
    c: Weight(g27) = 1
    c: Equal(g27,g28)
    c: Equal(g27,g29)
    c: Coincident(g30,g14)
    c: InternalAlignment(g27,g30)
    c: InternalAlignment(g28,g30)
    c: InternalAlignment(g29,g30)
    c: InternalAlignment(g31,g30)
    c: InternalAlignment(g32,g30)
    c: Coincident(g36,g12)
    c: Weight(g33) = 1
    c: Equal(g33,g34)
    c: Equal(g33,g35)
    c: Coincident(g36,g11)
    c: InternalAlignment(g33,g36)
    c: InternalAlignment(g34,g36)
    c: InternalAlignment(g35,g36)
    c: InternalAlignment(g37,g36)
    c: InternalAlignment(g38,g36)
    c: Coincident(g42,g13)
    c: Weight(g39) = 1
    c: Equal(g39,g40)
    c: Equal(g39,g41)
    c: Coincident(g42,g1)
    c: InternalAlignment(g39,g42)
    c: InternalAlignment(g40,g42)
    c: InternalAlignment(g41,g42)
    c: InternalAlignment(g43,g42)
    c: InternalAlignment(g44,g42)
    c: Block(g18)
    c: Block(g24)
    c: Block(g30)
    c: Block(g36)
    c: Block(g42)
    c: Horizontal(g45)
    c: Coincident(g45,g0)
    c: Vertical(g46)
    c: Coincident(g46,g45)
    c: Coincident(g47,g46)
    c: Coincident(g47,g18)
    c: Horizontal(g47)
    c: Block(g46)
    c: Coincident(g48,g18)
    c: Horizontal(g48)
    c: Distance(g48) = 1.33
    c: Vertical(g49)
    c: Coincident(g49,g48)
    c: Coincident(g50,g49)
    c: Coincident(g50,g24)
    c: Horizontal(g50)
    c: Tangent(g50,g22)
    c: Horizontal(g51)
    c: Coincident(g51,g24)
    c: Block(g51)
    c: Vertical(g52)
    c: Block(g52)
    c: Coincident(g52,g51)
    c: Coincident(g53,g52)
    c: Coincident(g53,g30)
    c: Horizontal(g53)
    c: Distance(g1) = 8.5
FEATURE [Part::Feature] Face024
  shape: bbox 9.8 x 26.5 x 2e-07 mm, 1 faces, 0 solids (baked)
FEATURE [Part::Revolution] Revolve024
  Angle = 360
  Axis = (0,1,0)
  Base = (0,0,0)
  FaceMakerClass = Part::FaceMakerBullseye
  Placement = pos=(0,0,0) rot=(0,0,1;1.5708rad)
  Solid = false
  Source = -> Face024
  Symmetric = false
FEATURE [Part::Feature] Face025
  shape: bbox 9.8 x 26.5 x 2e-07 mm, 1 faces, 0 solids (baked)
FEATURE [Part::Revolution] Revolve025
  Angle = 360
  Axis = (0,1,0)
  Base = (0,0,0)
  FaceMakerClass = Part::FaceMakerBullseye
  Placement = pos=(0,0,0) rot=(0,0,1;1.5708rad)
  Solid = false
  Source = -> Face025
  Symmetric = false
FEATURE [Part::MultiFuse] Fusion033
  Placement = pos=(-18,19,36) rot=(0,0,1;0rad)
  Shapes = -> [Revolve025,Revolve024]
FEATURE [Part::Cylinder] Cylinder014
  Angle = 360
  AttacherType = Attacher::AttachEngine3D
  Height = 20
  Placement = pos=(0,0,36.15) rot=(0,0,1;0rad)
  Radius = 14.3
FEATURE [Part::Cylinder] Cylinder015
  Angle = 360
  AttacherType = Attacher::AttachEngine3D
  Height = 10
  Placement = pos=(0,0,36.15) rot=(0,0,1;0rad)
  Radius = 4
FEATURE [Part::MultiFuse] Fusion034  label="removeToCreteHoleForPlugHousing004"
  Placement = pos=(-42,19,36) rot=(0,1,0;1.5708rad)
  Shapes = -> [Cylinder014,Cylinder015]
FEATURE [Part::Cut] Cut008  label="top004"
  Base = -> Cut004
  Placement = pos=(-1,0,0) rot=(0,0,1;0rad)
  Tool = -> Fusion034
FEATURE [Part::Box] Box005  label="Cube005"
  AttacherType = Attacher::AttachEngine3D
  Height = 28
  Length = 3
  Placement = pos=(110.7,19,22) rot=(0,0,1;0rad)
  Width = 15.7
FEATURE [Part::Cylinder] Cylinder016
  Angle = 360
  AttacherType = Attacher::AttachEngine3D
  Height = 10
  Placement = pos=(0,0,36.15) rot=(0,0,1;0rad)
  Radius = 4
FEATURE [Part::Cylinder] Cylinder017
  Angle = 360
  AttacherType = Attacher::AttachEngine3D
  Height = 20
  Placement = pos=(0,0,36.15) rot=(0,0,1;0rad)
  Radius = 10.3
FEATURE [Part::MultiFuse] Fusion035  label="removeToCreteHoleForPlugHousing005"
  Placement = pos=(70,19,36) rot=(0,1,0;1.5708rad)
  Shapes = -> [Cylinder017,Cylinder016]
FEATURE [Part::Cut] Cut009  label="plugHousingTab001"
  Base = -> Box005
  Placement = pos=(-107.4,-14,0) rot=(0,0,1;0rad)
  Tool = -> Fusion035
FEATURE [Part::Box] Box006  label="Cube006"
  AttacherType = Attacher::AttachEngine3D
  Height = 28
  Length = 3
  Placement = pos=(110.7,19,22) rot=(0,0,1;0rad)
  Width = 15.7
FEATURE [Part::Cylinder] Cylinder018
  Angle = 360
  AttacherType = Attacher::AttachEngine3D
  Height = 10
  Placement = pos=(0,0,36.15) rot=(0,0,1;0rad)
  Radius = 4
FEATURE [Part::Cylinder] Cylinder019
  Angle = 360
  AttacherType = Attacher::AttachEngine3D
  Height = 20
  Placement = pos=(0,0,36.15) rot=(0,0,1;0rad)
  Radius = 10.3
FEATURE [Part::MultiFuse] Fusion036  label="removeToCreteHoleForPlugHousing006"
  Placement = pos=(70,19,36) rot=(0,1,0;1.5708rad)
  Shapes = -> [Cylinder019,Cylinder018]
FEATURE [Part::Cut] Cut010  label="plugHousingTab002"
  Base = -> Box006
  Placement = pos=(-107.4,-14,0) rot=(0,0,1;0rad)
  Tool = -> Fusion036
FEATURE [Part::MultiFuse] Fusion037
  Placement = pos=(9.6,23,0) rot=(0,0,1;3.14159rad)
  Shapes = -> [Cut009,Cut010]
FEATURE [Part::Box] Box  label="Cube"
  AttacherType = Attacher::AttachEngine3D
  Height = 10
  Length = 3
  Placement = pos=(3.3,4,12) rot=(0,0,1;0rad)
  Width = 10
FEATURE [Part::Fillet] Fillet004
  Base = -> Fusion028
  Edges = 1 edges r=2: [Edge25]
FEATURE [Part::Fillet] Fillet005  label="plugHousing046"
  Base = -> Fillet004
  Edges = 1 edges r=2: [Edge8]
FEATURE [Part::Fillet] Fillet006
  Base = -> Box
  Edges = 1 edges r=2: [Edge11]
FEATURE [Part::Box] Box007  label="Cube007"
  AttacherType = Attacher::AttachEngine3D
  Height = 10
  Length = 3
  Placement = pos=(3.3,4,50) rot=(0,0,1;0rad)
  Width = 10
FEATURE [Part::Fillet] Fillet007
  Base = -> Box007
  Edges = 1 edges r=2: [Edge12]
FEATURE [Part::Box] Box008  label="Cube008"
  AttacherType = Attacher::AttachEngine3D
  Height = 28
  Length = 4
  Placement = pos=(5,0,22) rot=(0,0,1;0rad)
  Width = 10
FEATURE [Part::Fillet] Fillet008
  Base = -> Box008
  Edges = 1 edges r=1: [Edge7]
FEATURE [Part::Fillet] Fillet009
  Base = -> Fillet008
  Edges = 1 edges r=2: [Edge5]
FEATURE [Part::Fillet] Fillet010
  Base = -> Fillet009
  Edges = 1 edges r=2: [Edge2]
FEATURE [Sketcher::SketchObject] Sketch009  label="topSketch003"
  FullyConstrained = true
  sketch-geometry (4):
    g0: LineSegment StartX=16.8446 StartY=31.512 StartZ=0 EndX=16.3251 EndY=34.4666 EndZ=0
    g1: ArcOfCircle CenterX=19 CenterY=19.2524 CenterZ=0 NormalX=0 NormalY=0 NormalZ=1 AngleXU=0 Radius=15.4476 StartAngle=1.74483 EndAngle=2.72717
    g2: ArcOfCircle CenterX=19 CenterY=19.2524 CenterZ=0 NormalX=0 NormalY=0 NormalZ=1 AngleXU=0 Radius=12.4476 StartAngle=1.74483 EndAngle=2.73189
    g3: LineSegment StartX=4.86004 StartY=25.4725 StartZ=0 EndX=7.58253 EndY=24.2107 EndZ=0
  constraints (7):
    c: Block(g0)
    c: Coincident(g1,g0)
    c: Coincident(g2,g0)
    c: Coincident(g3,g1)
    c: Coincident(g3,g2)
    c: Block(g1)
    c: Block(g2)
FEATURE [Part::Extrusion] Extrude008
  Base = -> Sketch009
  Dir = (0,0,1)
  DirMode = 2
  FaceMakerClass = Part::FaceMakerBullseye
  LengthFwd = 10
  LengthRev = 0
  Placement = pos=(0,0,31) rot=(0,0,1;0rad)
  Solid = true
  Symmetric = false
FEATURE [Part::Cylinder] Cylinder020
  Angle = 360
  AttacherType = Attacher::AttachEngine3D
  Height = 20
  Placement = pos=(0,0,36.15) rot=(0,0,1;0rad)
  Radius = 8.2
FEATURE [Part::Cylinder] Cylinder021
  Angle = 360
  AttacherType = Attacher::AttachEngine3D
  Height = 10
  Placement = pos=(0,0,36.15) rot=(0,0,1;0rad)
  Radius = 4
FEATURE [Part::MultiFuse] Fusion038  label="removeToCreteHoleForPlugHousing007"
  Placement = pos=(-42,19,36) rot=(0,1,0;1.5708rad)
  Shapes = -> [Cylinder020,Cylinder021]
FEATURE [Part::Cut] Cut011
  Base = -> Extrude008
  Tool = -> Fusion038
FEATURE [Part::Fillet] Fillet011
  Base = -> Cut011
  Edges = 1 edges r=2: [Edge1]
FEATURE [Part::Fillet] Fillet012
  Base = -> Fillet011
  Edges = 1 edges r=2.5: [Edge1]
FEATURE [Part::Fillet] Fillet013
  Base = -> Fillet012
  Edges = 1 edges r=2.5: [Edge2]
FEATURE [Part::Box] Box010  label="Cube010"
  AttacherType = Attacher::AttachEngine3D
  Height = 16
  Length = 8
  Placement = pos=(12.7,31.52,28) rot=(0,0,1;0rad)
  Width = 4
FEATURE [Sketcher::SketchObject] Sketch010  label="topSketch004"
  FullyConstrained = true
  sketch-geometry (4):
    g0: LineSegment StartX=16.8446 StartY=31.512 StartZ=0 EndX=16.3251 EndY=34.4666 EndZ=0
    g1: ArcOfCircle CenterX=19 CenterY=19.2524 CenterZ=0 NormalX=0 NormalY=0 NormalZ=1 AngleXU=0 Radius=15.4476 StartAngle=1.74483 EndAngle=2.72717
    g2: ArcOfCircle CenterX=19 CenterY=19.2524 CenterZ=0 NormalX=0 NormalY=0 NormalZ=1 AngleXU=0 Radius=12.4476 StartAngle=1.74483 EndAngle=2.73189
    g3: LineSegment StartX=4.86004 StartY=25.4725 StartZ=0 EndX=7.58253 EndY=24.2107 EndZ=0
  constraints (7):
    c: Block(g0)
    c: Coincident(g1,g0)
    c: Coincident(g2,g0)
    c: Coincident(g3,g1)
    c: Coincident(g3,g2)
    c: Block(g1)
    c: Block(g2)
FEATURE [Part::Cylinder] Cylinder022
  Angle = 360
  AttacherType = Attacher::AttachEngine3D
  Height = 10
  Placement = pos=(0,0,36.15) rot=(0,0,1;0rad)
  Radius = 4
FEATURE [Sketcher::SketchObject] Sketch011  label="topSketch005"
  FullyConstrained = true
  sketch-geometry (4):
    g0: LineSegment StartX=16.8446 StartY=31.512 StartZ=0 EndX=16.3251 EndY=34.4666 EndZ=0
    g1: ArcOfCircle CenterX=19 CenterY=19.2524 CenterZ=0 NormalX=0 NormalY=0 NormalZ=1 AngleXU=0 Radius=15.4476 StartAngle=1.74483 EndAngle=2.72717
    g2: ArcOfCircle CenterX=19 CenterY=19.2524 CenterZ=0 NormalX=0 NormalY=0 NormalZ=1 AngleXU=0 Radius=12.4476 StartAngle=1.74483 EndAngle=2.73189
    g3: LineSegment StartX=4.86004 StartY=25.4725 StartZ=0 EndX=7.58253 EndY=24.2107 EndZ=0
  constraints (7):
    c: Block(g0)
    c: Coincident(g1,g0)
    c: Coincident(g2,g0)
    c: Coincident(g3,g1)
    c: Coincident(g3,g2)
    c: Block(g1)
    c: Block(g2)
FEATURE [Part::Extrusion] Extrude010
  Base = -> Sketch011
  Dir = (0,0,1)
  DirMode = 2
  FaceMakerClass = Part::FaceMakerBullseye
  LengthFwd = 10.6
  LengthRev = 0
  Placement = pos=(0,0,31) rot=(0,0,1;0rad)
  Solid = true
  Symmetric = false
FEATURE [Part::Cylinder] Cylinder023
  Angle = 360
  AttacherType = Attacher::AttachEngine3D
  Height = 20
  Placement = pos=(0,0,36.15) rot=(0,0,1;0rad)
  Radius = 8.2
FEATURE [Part::MultiFuse] Fusion039  label="removeToCreteHoleForPlugHousing008"
  Placement = pos=(-42,19,36) rot=(0,1,0;1.5708rad)
  Shapes = -> [Cylinder023,Cylinder022]
FEATURE [Part::Cut] Cut012
  Base = -> Extrude010
  Placement = pos=(0,0,-0.3) rot=(0,0,1;0rad)
  Tool = -> Fusion039
FEATURE [Part::Cut] Cut013
  Base = -> Box010
  Tool = -> Cut012
FEATURE [Part::Fillet] Fillet014
  Base = -> Cut013
  Edges = 1 edges r=0.7: [Edge13]
FEATURE [Part::Fillet] Fillet015
  Base = -> Fillet014
  Edges = 1 edges r=0.7: [Edge13]
FEATURE [Part::Fillet] Fillet016
  Base = -> Fillet015
  Edges = 1 edges r=0.7: [Edge16]
FEATURE [Part::Fillet] Fillet017
  Base = -> Fillet016
  Edges = 1 edges r=0.7: [Edge11]
FEATURE [Part::Fillet] Fillet018
  Base = -> Fillet017
  Edges = 1 edges r=0.7: [Edge10]
FEATURE [Part::Fillet] Fillet019
  Base = -> Fillet018
  Edges = 1 edges r=1.2: [Edge5]
FEATURE [Part::Fillet] Fillet020
  Base = -> Fillet019
  Edges = 1 edges r=1.2: [Edge12]
FEATURE [Part::Fillet] Fillet021
  Base = -> Fillet020
  Edges = 1 edges r=2: [Edge1]
  Placement = pos=(0.3,0,0) rot=(0,0,1;0rad)
FEATURE [Part::MultiFuse] Fusion040  label="top005"
  Shapes = -> [Cut008,Fillet021]
FEATURE [Part::MultiFuse] Fusion041  label="wireHolder"
  Shapes = -> [Fusion033,Fillet013]
FEATURE [Part::MultiFuse] Fusion042
  Shapes = -> [Fillet007,Fusion041]
FEATURE [Part::MultiFuse] Fusion043  label="wireHolder001"
  Shapes = -> [Fusion042,Fillet010]
FEATURE [Part::MultiFuse] Fusion044  label="wireHolder002"
  Shapes = -> [Fillet006,Fusion037,Fusion043]
FEATURE [Part::Feature] Face026
  shape: bbox 11 x 6 x 2e-07 mm, 1 faces, 0 solids (baked)
FEATURE [Part::Revolution] Revolve026
  Angle = 360
  Axis = (0,1,0)
  Base = (0,0,0)
  FaceMakerClass = Part::FaceMakerBullseye
  Placement = pos=(30.3,-1,19.7) rot=(0,0,1;0rad)
  Solid = false
  Source = -> Face026
  Symmetric = false
FEATURE [Sketcher::SketchObject] Sketch013  label="topSketch006"
  FullyConstrained = true
  sketch-geometry (13):
    g0: LineSegment StartX=117 StartY=19 StartZ=0 EndX=117 EndY=38 EndZ=0
    g1: ArcOfCircle CenterX=98 CenterY=19 CenterZ=0 NormalX=0 NormalY=0 NormalZ=1 AngleXU=0 Radius=19 StartAngle=5.7297 EndAngle=6.28319
    g2: LineSegment StartX=0 StartY=3 StartZ=0 EndX=0 EndY=19 EndZ=0
    g3: LineSegment StartX=19 StartY=38 StartZ=0 EndX=117 EndY=38 EndZ=0
    g4: ArcOfCircle CenterX=19 CenterY=19 CenterZ=0 NormalX=0 NormalY=0 NormalZ=1 AngleXU=0 Radius=19 StartAngle=1.5708 EndAngle=3.14159
    g5: ArcOfCircle CenterX=19 CenterY=19 CenterZ=0 NormalX=0 NormalY=0 NormalZ=1 AngleXU=0 Radius=16 StartAngle=1.5708 EndAngle=3.14159
    g6: ArcOfCircle CenterX=98 CenterY=19 CenterZ=0 NormalX=0 NormalY=0 NormalZ=1 AngleXU=0 Radius=16 StartAngle=5.60905 EndAngle=6.28319
    g7: LineSegment StartX=114 StartY=19 StartZ=0 EndX=114 EndY=35 EndZ=0
    g8: LineSegment StartX=110.5 StartY=9.01251 StartZ=0 EndX=114.163 EndY=9.01251 EndZ=0
    g9: LineSegment StartX=114 StartY=35 StartZ=0 EndX=19 EndY=35 EndZ=0
    g10: LineSegment StartX=0 StartY=3 StartZ=0 EndX=0 EndY=0 EndZ=0
    g11: LineSegment StartX=3 StartY=0 StartZ=0 EndX=0 EndY=0 EndZ=0
    g12: LineSegment StartX=3 StartY=19 StartZ=0 EndX=3 EndY=0 EndZ=0
  constraints (33):
    c: Vertical(g0)
    c: Distance(g0) = 19
    c: Block(g0)
    c: Coincident(g1,g0)
    c: Block(g1)
    c: Vertical(g2)
    c: Block(g2)
    c: Coincident(g3,g0)
    c: Horizontal(g3)
    c: Distance(g3) = 98
    c: Coincident(g4,g3)
    c: Coincident(g4,g2)
    c: Block(g4)
    c: Coincident(g5,g4)
    c: Coincident(g6,g1)
    c: Block(g6)
    c: Block(g5)
    c: Coincident(g7,g6)
    c: Vertical(g7)
    c: Coincident(g8,g6)
    c: Coincident(g8,g1)
    c: Coincident(g9,g7)
    c: Coincident(g9,g5)
    c: Horizontal(g9)
    c: Tangent(g9,g5)
    c: Coincident(g10,g2)
    c: Distance(g10) = 3
    c: Vertical(g10)
    c: Coincident(g11,g10)
    c: Horizontal(g11)
    c: Coincident(g12,g5)
    c: Coincident(g12,g11)
    c: Vertical(g12)
FEATURE [Part::Extrusion] Extrude011  label="top006"
  Base = -> Sketch013
  Dir = (0,0,1)
  DirMode = 2
  FaceMakerClass = Part::FaceMakerBullseye
  LengthFwd = 72
  LengthRev = 0
  Solid = true
  Symmetric = false
FEATURE [Sketcher::SketchObject] Sketch014
  FullyConstrained = true
  MapMode = 3
  Placement = pos=(0,0,0) rot=(1,0,0;1.5708rad)
  Support = -> [Extrude011]
  sketch-geometry (8):
    g0: Circle CenterX=80.351 CenterY=-67.6202 CenterZ=0 NormalX=0 NormalY=0 NormalZ=1 AngleXU=0 Radius=2
    g1: Circle CenterX=80.351 CenterY=-67.6202 CenterZ=0 NormalX=0 NormalY=0 NormalZ=1 AngleXU=0 Radius=3
    g2: Circle CenterX=80.351 CenterY=-4.92017 CenterZ=0 NormalX=0 NormalY=0 NormalZ=1 AngleXU=0 Radius=2
    g3: Circle CenterX=80.351 CenterY=-4.92017 CenterZ=0 NormalX=0 NormalY=0 NormalZ=1 AngleXU=0 Radius=3
    g4: Circle CenterX=23.851 CenterY=-4.92017 CenterZ=0 NormalX=0 NormalY=0 NormalZ=1 AngleXU=0 Radius=2
    g5: Circle CenterX=23.851 CenterY=-4.92017 CenterZ=0 NormalX=0 NormalY=0 NormalZ=1 AngleXU=0 Radius=3
    g6: Circle CenterX=23.851 CenterY=-67.6202 CenterZ=0 NormalX=0 NormalY=0 NormalZ=1 AngleXU=0 Radius=2
    g7: Circle CenterX=23.851 CenterY=-67.6202 CenterZ=0 NormalX=0 NormalY=0 NormalZ=1 AngleXU=0 Radius=3
  constraints (8):
    c: Block(g3)
    c: Block(g2)
    c: Block(g1)
    c: Block(g0)
    c: Block(g6)
    c: Block(g7)
    c: Block(g4)
    c: Block(g5)
FEATURE [Part::Feature] Face027
  shape: bbox 11 x 6 x 2e-07 mm, 1 faces, 0 solids (baked)
FEATURE [Part::Revolution] Revolve027
  Angle = 360
  Axis = (0,1,0)
  Base = (0,0,0)
  FaceMakerClass = Part::FaceMakerBullseye
  Placement = pos=(30.3,-1,51.7) rot=(0,0,1;0rad)
  Solid = false
  Source = -> Face027
  Symmetric = false
FEATURE [Part::Feature] Face028
  shape: bbox 11 x 6 x 2e-07 mm, 1 faces, 0 solids (baked)
FEATURE [Part::Revolution] Revolve028
  Angle = 360
  Axis = (0,1,0)
  Base = (0,0,0)
  FaceMakerClass = Part::FaceMakerBullseye
  Placement = pos=(62.3,-1,19.7) rot=(0,0,1;0rad)
  Solid = false
  Source = -> Face028
  Symmetric = false
FEATURE [Part::Feature] Face029
  shape: bbox 11 x 6 x 2e-07 mm, 1 faces, 0 solids (baked)
FEATURE [Part::Revolution] Revolve029
  Angle = 360
  Axis = (0,1,0)
  Base = (0,0,0)
  FaceMakerClass = Part::FaceMakerBullseye
  Placement = pos=(62.3,-1,51.7) rot=(0,0,1;0rad)
  Solid = false
  Source = -> Face029
  Symmetric = false
FEATURE [Part::Feature] Wire
  shape: bbox 11 x 5.2 x 2e-07 mm, 0 faces, 0 solids (baked)
FEATURE [Part::Revolution] Revolve030
  Angle = 360
  Axis = (0,1,0)
  Base = (0,0,0)
  FaceMakerClass = Part::FaceMakerBullseye
  Placement = pos=(30.3,38,19.7) rot=(0,0,1;0rad)
  Solid = true
  Source = -> Wire
  Symmetric = false
FEATURE [Part::Feature] Wire001
  shape: bbox 11 x 5.2 x 2e-07 mm, 0 faces, 0 solids (baked)
FEATURE [Part::Revolution] Revolve031
  Angle = 360
  Axis = (0,1,0)
  Base = (0,0,0)
  FaceMakerClass = Part::FaceMakerBullseye
  Placement = pos=(30.3,38,51.7) rot=(0,0,1;0rad)
  Solid = true
  Source = -> Wire001
  Symmetric = false
FEATURE [Part::Feature] Wire002
  shape: bbox 11 x 5.2 x 2e-07 mm, 0 faces, 0 solids (baked)
FEATURE [Part::Revolution] Revolve032
  Angle = 360
  Axis = (0,1,0)
  Base = (0,0,0)
  FaceMakerClass = Part::FaceMakerBullseye
  Placement = pos=(62.3,38,51.7) rot=(0,0,1;0rad)
  Solid = true
  Source = -> Wire002
  Symmetric = false
FEATURE [Part::Feature] Wire003
  shape: bbox 11 x 5.2 x 2e-07 mm, 0 faces, 0 solids (baked)
FEATURE [Part::Revolution] Revolve033
  Angle = 360
  Axis = (0,1,0)
  Base = (0,0,0)
  FaceMakerClass = Part::FaceMakerBullseye
  Placement = pos=(62.3,38,19.7) rot=(0,0,1;0rad)
  Solid = true
  Source = -> Wire003
  Symmetric = false
FEATURE [Part::MultiFuse] Fusion045  label="altRandScrewHousing"
  Shapes = -> [Revolve029,Revolve027,Revolve028,Revolve026]
FEATURE [Part::MultiFuse] Fusion046  label="fanScrewHousing"
  Shapes = -> [Revolve033,Revolve032,Revolve031,Revolve030]
FEATURE [Sketcher::SketchObject] Sketch015
  FullyConstrained = true
  sketch-geometry (17):
    g0: Circle CenterX=-3.5 CenterY=23.5 CenterZ=0 NormalX=0 NormalY=0 NormalZ=1 AngleXU=0 Radius=1
    g1: Circle CenterX=-1 CenterY=15.25 CenterZ=0 NormalX=0 NormalY=0 NormalZ=1 AngleXU=0 Radius=1
    g2: Circle CenterX=-3.5 CenterY=7 CenterZ=0 NormalX=0 NormalY=0 NormalZ=1 AngleXU=0 Radius=1
    g3: BSplineCurve PolesCount=3 KnotsCount=2 Degree=2 IsPeriodic=0
    g4: GeomPoint X=-3.5 Y=23.5 Z=0
    g5: GeomPoint X=-3.5 Y=7 Z=0
    g6: Circle CenterX=-4.8 CenterY=30.5 CenterZ=0 NormalX=0 NormalY=0 NormalZ=1 AngleXU=0 Radius=1
    g7: Circle CenterX=-3.5 CenterY=30.5 CenterZ=0 NormalX=0 NormalY=0 NormalZ=1 AngleXU=0 Radius=1
    g8: Circle CenterX=-3.5 CenterY=29.2 CenterZ=0 NormalX=0 NormalY=0 NormalZ=1 AngleXU=0 Radius=1
    g9: BSplineCurve PolesCount=3 KnotsCount=2 Degree=2 IsPeriodic=0
    g10: GeomPoint X=-4.8 Y=30.5 Z=0
    g11: GeomPoint X=-3.5 Y=29.2 Z=0
    g12: LineSegment StartX=-3.5 StartY=29.2 StartZ=0 EndX=-3.5 EndY=23.5 EndZ=0
    g13: LineSegment StartX=-4.8 StartY=30.5 StartZ=0 EndX=0 EndY=30.5 EndZ=0
    g14: LineSegment StartX=-3.5 StartY=0.3 StartZ=0 EndX=0 EndY=0.3 EndZ=0
    g15: LineSegment StartX=-3.5 StartY=0.3 StartZ=0 EndX=-3.5 EndY=7 EndZ=0
    g16: LineSegment StartX=0 StartY=0.3 StartZ=0 EndX=0 EndY=30.5 EndZ=0
  constraints (33):
    c: Weight(g0) = 1
    c: Equal(g0,g1)
    c: Equal(g0,g2)
    c: InternalAlignment(g0,g3)
    c: InternalAlignment(g1,g3)
    c: InternalAlignment(g2,g3)
    c: InternalAlignment(g4,g3)
    c: InternalAlignment(g5,g3)
    c: Block(g3)
    c: Weight(g6) = 1
    c: Equal(g6,g7)
    c: Equal(g6,g8)
    c: InternalAlignment(g6,g9)
    c: InternalAlignment(g7,g9)
    c: InternalAlignment(g8,g9)
    c: InternalAlignment(g10,g9)
    c: InternalAlignment(g11,g9)
    c: Block(g9)
    c: Coincident(g12,g9)
    c: Coincident(g12,g3)
    c: Vertical(g12)
    c: Coincident(g13,g9)
    c: Horizontal(g13)
    c: Distance(g13) = 4.8
    c: Horizontal(g14)
    c: Block(g14)
    c: Coincident(g15,g14)
    c: Coincident(g15,g3)
    c: Vertical(g15)
    c: Coincident(g16,g14)
    c: Coincident(g16,g13)
    c: Vertical(g16)
    c: Tangent(g16,g1)
FEATURE [Sketcher::SketchObject] Sketch016
  FullyConstrained = true
  sketch-geometry (16):
    g0: Circle CenterX=-3.5 CenterY=23.5 CenterZ=0 NormalX=0 NormalY=0 NormalZ=1 AngleXU=0 Radius=1
    g1: Circle CenterX=-1 CenterY=15.25 CenterZ=0 NormalX=0 NormalY=0 NormalZ=1 AngleXU=0 Radius=1
    g2: Circle CenterX=-3.5 CenterY=7 CenterZ=0 NormalX=0 NormalY=0 NormalZ=1 AngleXU=0 Radius=1
    g3: BSplineCurve PolesCount=3 KnotsCount=2 Degree=2 IsPeriodic=0
    g4: GeomPoint X=-3.5 Y=23.5 Z=0
    g5: GeomPoint X=-3.5 Y=7 Z=0
    g6: LineSegment StartX=-3.5 StartY=28.2 StartZ=0 EndX=-3.5 EndY=23.5 EndZ=0
    g7: LineSegment StartX=0 StartY=29.5 StartZ=0 EndX=0 EndY=30 EndZ=0
    g8: LineSegment StartX=-3.5 StartY=28.2 StartZ=0 EndX=-3.5 EndY=30 EndZ=0
    g9: LineSegment StartX=0 StartY=30 StartZ=0 EndX=0 EndY=30.5 EndZ=0
    g10: LineSegment StartX=0 StartY=30.5 StartZ=0 EndX=-3.5 EndY=30.5 EndZ=0
    g11: LineSegment StartX=-3.5 StartY=30.5 StartZ=0 EndX=-3.5 EndY=30 EndZ=0
    g12: LineSegment StartX=0 StartY=29.5 StartZ=0 EndX=0 EndY=5 EndZ=0
    g13: LineSegment StartX=-3.5 StartY=0.3 StartZ=0 EndX=-3.5 EndY=7 EndZ=0
    g14: LineSegment StartX=-3.5 StartY=0.3 StartZ=0 EndX=0 EndY=0.3 EndZ=0
    g15: LineSegment StartX=0 StartY=5 StartZ=0 EndX=0 EndY=0.3 EndZ=0
  constraints (39):
    c: Weight(g0) = 1
    c: Equal(g0,g1)
    c: Equal(g0,g2)
    c: InternalAlignment(g0,g3)
    c: InternalAlignment(g1,g3)
    c: InternalAlignment(g2,g3)
    c: InternalAlignment(g4,g3)
    c: InternalAlignment(g5,g3)
    c: Block(g3)
    c: Coincident(g6,g3)
    c: Vertical(g6)
    c: Vertical(g7)
    c: Distance(g7) = 0.5
    c: Coincident(g8,g6)
    c: Vertical(g8)
    c: Block(g6)
    c: Block(g7)
    c: Vertical(g9)
    c: Equal(g7,g9) = 0.5
    c: Block(g9)
    c: Coincident(g9,g7)
    c: Horizontal(g10)
    c: Coincident(g10,g9)
    c: Coincident(g11,g10)
    c: Coincident(g11,g8)
    c: Vertical(g11)
    c: Block(g11)
    c: Coincident(g12,g7)
    c: Vertical(g12)
    c: Coincident(g13,g3)
    c: Vertical(g13)
    c: Distance(g13) = 6.7
    c: Coincident(g14,g13)
    c: Horizontal(g14)
    c: Block(g14)
    c: Coincident(g15,g12)
    c: Coincident(g15,g14)
    c: Vertical(g15)
    c: Block(g15)
FEATURE [Sketcher::SketchObject] Sketch017
  FullyConstrained = true
  sketch-geometry (11):
    g0: LineSegment StartX=-3.5 StartY=1e-16 StartZ=0 EndX=-1.6 EndY=1e-16 EndZ=0
    g1: LineSegment StartX=-1.6 StartY=1e-16 StartZ=0 EndX=-1.6 EndY=1.5 EndZ=0
    g2: LineSegment StartX=-3.5 StartY=1.5 StartZ=0 EndX=-1.6 EndY=1.5 EndZ=0
    g3: LineSegment StartX=-3.5 StartY=1e-16 StartZ=0 EndX=-4.8 EndY=1e-16 EndZ=0
    g4: Circle CenterX=-3.5 CenterY=1.3 CenterZ=0 NormalX=0 NormalY=0 NormalZ=1 AngleXU=0 Radius=1
    g5: Circle CenterX=-3.5 CenterY=1e-16 CenterZ=0 NormalX=0 NormalY=0 NormalZ=1 AngleXU=0 Radius=1
    g6: Circle CenterX=-4.8 CenterY=1e-16 CenterZ=0 NormalX=0 NormalY=0 NormalZ=1 AngleXU=0 Radius=1
    g7: BSplineCurve PolesCount=3 KnotsCount=2 Degree=2 IsPeriodic=0
    g8: GeomPoint X=-3.5 Y=1.3 Z=0
    g9: GeomPoint X=-4.8 Y=1e-16 Z=0
    g10: LineSegment StartX=-3.5 StartY=1.3 StartZ=0 EndX=-3.5 EndY=1.5 EndZ=0
  constraints (24):
    c: Horizontal(g0)
    c: Distance(g0) = 1.9
    c: Block(g0)
    c: Coincident(g1,g0)
    c: Vertical(g1)
    c: Coincident(g2,g1)
    c: Horizontal(g2)
    c: Coincident(g3,g0)
    c: Horizontal(g3)
    c: Distance(g3) = 1.3
    c: Weight(g4) = 1
    c: Equal(g4,g5)
    c: Coincident(g5,g0)
    c: Equal(g4,g6)
    c: Coincident(g7,g3)
    c: InternalAlignment(g4,g7)
    c: InternalAlignment(g5,g7)
    c: InternalAlignment(g6,g7)
    c: InternalAlignment(g8,g7)
    c: InternalAlignment(g9,g7)
    c: Coincident(g10,g7)
    c: Coincident(g10,g2)
    c: Vertical(g10)
    c: Block(g10)
FEATURE [Part::Feature] Face035
  shape: bbox 3.2 x 1.5 x 2e-07 mm, 1 faces, 0 solids (baked)
FEATURE [Part::Revolution] Revolve039  label="backCaseScrewRetainer"
  Angle = 360
  Axis = (0,1,0)
  Base = (0,0,0)
  FaceMakerClass = Part::FaceMakerBullseye
  Placement = pos=(12.5,3,62) rot=(0,0,1;0rad)
  Solid = false
  Source = -> Face035
  Symmetric = false
FEATURE [Part::Feature] Face036
  shape: bbox 3.2 x 1.5 x 2e-07 mm, 1 faces, 0 solids (baked)
FEATURE [Part::Feature] Face039
  shape: bbox 4.8 x 30.2 x 2e-07 mm, 1 faces, 0 solids (baked)
FEATURE [Part::Revolution] Revolve043  label="frontCaseScrewPost002"
  Angle = 360
  Axis = (0,1,0)
  Base = (0,0,0)
  FaceMakerClass = Part::FaceMakerBullseye
  Placement = pos=(89.5,4.5,3.5) rot=(0,0,1;0rad)
  Solid = false
  Source = -> Face039
  Symmetric = false
FEATURE [Part::Feature] Face042
  shape: bbox 4.8 x 30.2 x 2e-07 mm, 1 faces, 0 solids (baked)
FEATURE [Part::Revolution] Revolve046  label="frontCaseScrewPost003"
  Angle = 360
  Axis = (0,1,0)
  Base = (0,0,0)
  FaceMakerClass = Part::FaceMakerBullseye
  Placement = pos=(89.5,4.5,68.5) rot=(0,0,1;0rad)
  Solid = false
  Source = -> Face042
  Symmetric = false
FEATURE [Part::Feature] Face043
  shape: bbox 3.2 x 1.5 x 2e-07 mm, 1 faces, 0 solids (baked)
FEATURE [Part::Revolution] Revolve047  label="frontCaseScrewRetainer002"
  Angle = 360
  Axis = (0,1,0)
  Base = (0,0,0)
  FaceMakerClass = Part::FaceMakerBullseye
  Placement = pos=(89.5,3,68.5) rot=(0,0,1;0rad)
  Solid = false
  Source = -> Face043
  Symmetric = false
FEATURE [Part::Feature] Face044
  shape: bbox 3.2 x 1.5 x 2e-07 mm, 1 faces, 0 solids (baked)
FEATURE [Part::Revolution] Revolve048  label="frontCaseScrewRetainer003"
  Angle = 360
  Axis = (0,1,0)
  Base = (0,0,0)
  FaceMakerClass = Part::FaceMakerBullseye
  Placement = pos=(89.5,3,3.5) rot=(0,0,1;0rad)
  Solid = false
  Source = -> Face044
  Symmetric = false
FEATURE [App::MeasureDistance] Distance002  label="Distance: 1.67 mm"
  Distance = 1.66921
  P1 = (99.2361,4.7524,71.7)
  P2 = (99.2347,6.42161,71.7)
FEATURE [Sketcher::SketchObject] Sketch018
  FullyConstrained = true
  sketch-geometry (7):
    g0: LineSegment StartX=0 StartY=0 StartZ=0 EndX=0 EndY=6 EndZ=0
    g1: Circle CenterX=0 CenterY=0 CenterZ=0 NormalX=0 NormalY=0 NormalZ=1 AngleXU=0 Radius=1
    g2: Circle CenterX=8 CenterY=6 CenterZ=0 NormalX=0 NormalY=0 NormalZ=1 AngleXU=0 Radius=1
    g3: BSplineCurve PolesCount=3 KnotsCount=2 Degree=2 IsPeriodic=0
    g4: GeomPoint X=0 Y=0 Z=0
    g5: GeomPoint X=8 Y=6 Z=0
    g6: LineSegment StartX=0 StartY=6 StartZ=0 EndX=8 EndY=6 EndZ=0
  constraints (14):
    c: Coincident(g0,g-1)
    c: Distance(g0) = 6
    c: Vertical(g0)
    c: Coincident(g3,g0)
    c: Weight(g1) = 1
    c: Equal(g1,g2)
    c: InternalAlignment(g1,g3)
    c: InternalAlignment(g2,g3)
    c: InternalAlignment(g4,g3)
    c: InternalAlignment(g5,g3)
    c: Block(g3)
    c: Coincident(g6,g0)
    c: Coincident(g6,g3)
    c: Horizontal(g6)
FEATURE [Part::Extrusion] Extrude012  label="caseScrewPillarBracket"
  Base = -> Sketch018
  Dir = (0,0,1)
  DirMode = 2
  FaceMakerClass = Part::FaceMakerBullseye
  LengthFwd = 2.4
  LengthRev = 0
  Placement = pos=(15.76,29,8.8) rot=(0,1,0;0rad)
  Solid = true
  Symmetric = false
FEATURE [Sketcher::SketchObject] Sketch019
  FullyConstrained = true
  sketch-geometry (7):
    g0: LineSegment StartX=0 StartY=0 StartZ=0 EndX=0 EndY=6 EndZ=0
    g1: Circle CenterX=0 CenterY=0 CenterZ=0 NormalX=0 NormalY=0 NormalZ=1 AngleXU=0 Radius=1
    g2: Circle CenterX=8 CenterY=6 CenterZ=0 NormalX=0 NormalY=0 NormalZ=1 AngleXU=0 Radius=1
    g3: BSplineCurve PolesCount=3 KnotsCount=2 Degree=2 IsPeriodic=0
    g4: GeomPoint X=0 Y=0 Z=0
    g5: GeomPoint X=8 Y=6 Z=0
    g6: LineSegment StartX=0 StartY=6 StartZ=0 EndX=8 EndY=6 EndZ=0
  constraints (14):
    c: Coincident(g0,g-1)
    c: Distance(g0) = 6
    c: Vertical(g0)
    c: Coincident(g3,g0)
    c: Weight(g1) = 1
    c: Equal(g1,g2)
    c: InternalAlignment(g1,g3)
    c: InternalAlignment(g2,g3)
    c: InternalAlignment(g4,g3)
    c: InternalAlignment(g5,g3)
    c: Block(g3)
    c: Coincident(g6,g0)
    c: Coincident(g6,g3)
    c: Horizontal(g6)
FEATURE [Part::Extrusion] Extrude013  label="caseScrewPillarBracket001"
  Base = -> Sketch019
  Dir = (0,0,1)
  DirMode = 2
  FaceMakerClass = Part::FaceMakerBullseye
  LengthFwd = 2.4
  LengthRev = 0
  Placement = pos=(15.76,29,60.8) rot=(0,0,1;0rad)
  Solid = true
  Symmetric = false
FEATURE [Sketcher::SketchObject] Sketch020
  FullyConstrained = true
  sketch-geometry (7):
    g0: LineSegment StartX=0 StartY=0 StartZ=0 EndX=0 EndY=6 EndZ=0
    g1: Circle CenterX=0 CenterY=0 CenterZ=0 NormalX=0 NormalY=0 NormalZ=1 AngleXU=0 Radius=1
    g2: Circle CenterX=8 CenterY=6 CenterZ=0 NormalX=0 NormalY=0 NormalZ=1 AngleXU=0 Radius=1
    g3: BSplineCurve PolesCount=3 KnotsCount=2 Degree=2 IsPeriodic=0
    g4: GeomPoint X=0 Y=0 Z=0
    g5: GeomPoint X=8 Y=6 Z=0
    g6: LineSegment StartX=0 StartY=6 StartZ=0 EndX=8 EndY=6 EndZ=0
  constraints (14):
    c: Coincident(g0,g-1)
    c: Distance(g0) = 6
    c: Vertical(g0)
    c: Coincident(g3,g0)
    c: Weight(g1) = 1
    c: Equal(g1,g2)
    c: InternalAlignment(g1,g3)
    c: InternalAlignment(g2,g3)
    c: InternalAlignment(g4,g3)
    c: InternalAlignment(g5,g3)
    c: Block(g3)
    c: Coincident(g6,g0)
    c: Coincident(g6,g3)
    c: Horizontal(g6)
FEATURE [Part::Extrusion] Extrude014  label="caseScrewPillarBracket002"
  Base = -> Sketch020
  Dir = (0,0,1)
  DirMode = 2
  FaceMakerClass = Part::FaceMakerBullseye
  LengthFwd = 2.4
  LengthRev = 0
  Placement = pos=(13.7,29,13.26) rot=(0,-1,0;1.5708rad)
  Solid = true
  Symmetric = false
FEATURE [Sketcher::SketchObject] Sketch021
  FullyConstrained = true
  sketch-geometry (7):
    g0: LineSegment StartX=0 StartY=0 StartZ=0 EndX=0 EndY=6 EndZ=0
    g1: Circle CenterX=0 CenterY=0 CenterZ=0 NormalX=0 NormalY=0 NormalZ=1 AngleXU=0 Radius=1
    g2: Circle CenterX=8 CenterY=6 CenterZ=0 NormalX=0 NormalY=0 NormalZ=1 AngleXU=0 Radius=1
    g3: BSplineCurve PolesCount=3 KnotsCount=2 Degree=2 IsPeriodic=0
    g4: GeomPoint X=0 Y=0 Z=0
    g5: GeomPoint X=8 Y=6 Z=0
    g6: LineSegment StartX=0 StartY=6 StartZ=0 EndX=8 EndY=6 EndZ=0
  constraints (14):
    c: Coincident(g0,g-1)
    c: Distance(g0) = 6
    c: Vertical(g0)
    c: Coincident(g3,g0)
    c: Weight(g1) = 1
    c: Equal(g1,g2)
    c: InternalAlignment(g1,g3)
    c: InternalAlignment(g2,g3)
    c: InternalAlignment(g4,g3)
    c: InternalAlignment(g5,g3)
    c: Block(g3)
    c: Coincident(g6,g0)
    c: Coincident(g6,g3)
    c: Horizontal(g6)
FEATURE [Part::Extrusion] Extrude015  label="caseScrewPillarBracket003"
  Base = -> Sketch021
  Dir = (0,0,1)
  DirMode = 2
  FaceMakerClass = Part::FaceMakerBullseye
  LengthFwd = 2.4
  LengthRev = 0
  Placement = pos=(11.3,29,58.74) rot=(0,1,0;1.5708rad)
  Solid = true
  Symmetric = false
FEATURE [Sketcher::SketchObject] Sketch022
  FullyConstrained = true
  sketch-geometry (7):
    g0: LineSegment StartX=0 StartY=0 StartZ=0 EndX=0 EndY=6 EndZ=0
    g1: Circle CenterX=0 CenterY=0 CenterZ=0 NormalX=0 NormalY=0 NormalZ=1 AngleXU=0 Radius=1
    g2: Circle CenterX=8 CenterY=6 CenterZ=0 NormalX=0 NormalY=0 NormalZ=1 AngleXU=0 Radius=1
    g3: BSplineCurve PolesCount=3 KnotsCount=2 Degree=2 IsPeriodic=0
    g4: GeomPoint X=0 Y=0 Z=0
    g5: GeomPoint X=8 Y=6 Z=0
    g6: LineSegment StartX=0 StartY=6 StartZ=0 EndX=8 EndY=6 EndZ=0
  constraints (14):
    c: Coincident(g0,g-1)
    c: Distance(g0) = 6
    c: Vertical(g0)
    c: Coincident(g3,g0)
    c: Weight(g1) = 1
    c: Equal(g1,g2)
    c: InternalAlignment(g1,g3)
    c: InternalAlignment(g2,g3)
    c: InternalAlignment(g4,g3)
    c: InternalAlignment(g5,g3)
    c: Block(g3)
    c: Coincident(g6,g0)
    c: Coincident(g6,g3)
    c: Horizontal(g6)
FEATURE [Part::Extrusion] Extrude016  label="caseScrewPillarBracket004"
  Base = -> Sketch022
  Dir = (0,0,1)
  DirMode = 2
  FaceMakerClass = Part::FaceMakerBullseye
  LengthFwd = 2.4
  LengthRev = 0
  Placement = pos=(88.3,29,65.23) rot=(0,1,0;1.5708rad)
  Solid = true
  Symmetric = false
FEATURE [Sketcher::SketchObject] Sketch023
  FullyConstrained = true
  sketch-geometry (7):
    g0: LineSegment StartX=0 StartY=0 StartZ=0 EndX=0 EndY=6 EndZ=0
    g1: Circle CenterX=0 CenterY=0 CenterZ=0 NormalX=0 NormalY=0 NormalZ=1 AngleXU=0 Radius=1
    g2: Circle CenterX=8 CenterY=6 CenterZ=0 NormalX=0 NormalY=0 NormalZ=1 AngleXU=0 Radius=1
    g3: BSplineCurve PolesCount=3 KnotsCount=2 Degree=2 IsPeriodic=0
    g4: GeomPoint X=0 Y=0 Z=0
    g5: GeomPoint X=8 Y=6 Z=0
    g6: LineSegment StartX=0 StartY=6 StartZ=0 EndX=8 EndY=6 EndZ=0
  constraints (14):
    c: Coincident(g0,g-1)
    c: Distance(g0) = 6
    c: Vertical(g0)
    c: Coincident(g3,g0)
    c: Weight(g1) = 1
    c: Equal(g1,g2)
    c: InternalAlignment(g1,g3)
    c: InternalAlignment(g2,g3)
    c: InternalAlignment(g4,g3)
    c: InternalAlignment(g5,g3)
    c: Block(g3)
    c: Coincident(g6,g0)
    c: Coincident(g6,g3)
    c: Horizontal(g6)
FEATURE [Part::Extrusion] Extrude017  label="caseScrewPillarBracket005"
  Base = -> Sketch023
  Dir = (0,0,1)
  DirMode = 2
  FaceMakerClass = Part::FaceMakerBullseye
  LengthFwd = 2.4
  LengthRev = 0
  Placement = pos=(90.7,29,6.77) rot=(0,-1,0;1.5708rad)
  Solid = true
  Symmetric = false
FEATURE [Sketcher::SketchObject] Sketch024
  FullyConstrained = true
  sketch-geometry (7):
    g0: LineSegment StartX=0 StartY=0 StartZ=0 EndX=0 EndY=6 EndZ=0
    g1: Circle CenterX=0 CenterY=0 CenterZ=0 NormalX=0 NormalY=0 NormalZ=1 AngleXU=0 Radius=1
    g2: Circle CenterX=8 CenterY=6 CenterZ=0 NormalX=0 NormalY=0 NormalZ=1 AngleXU=0 Radius=1
    g3: BSplineCurve PolesCount=3 KnotsCount=2 Degree=2 IsPeriodic=0
    g4: GeomPoint X=0 Y=0 Z=0
    g5: GeomPoint X=8 Y=6 Z=0
    g6: LineSegment StartX=0 StartY=6 StartZ=0 EndX=8 EndY=6 EndZ=0
  constraints (14):
    c: Coincident(g0,g-1)
    c: Distance(g0) = 6
    c: Vertical(g0)
    c: Coincident(g3,g0)
    c: Weight(g1) = 1
    c: Equal(g1,g2)
    c: InternalAlignment(g1,g3)
    c: InternalAlignment(g2,g3)
    c: InternalAlignment(g4,g3)
    c: InternalAlignment(g5,g3)
    c: Block(g3)
    c: Coincident(g6,g0)
    c: Coincident(g6,g3)
    c: Horizontal(g6)
FEATURE [Part::Extrusion] Extrude018  label="caseScrewPillarBracket006"
  Base = -> Sketch024
  Dir = (0,0,1)
  DirMode = 2
  FaceMakerClass = Part::FaceMakerBullseye
  LengthFwd = 2.4
  LengthRev = 0
  Placement = pos=(103.7,29,6.77) rot=(0,-1,0;1.5708rad)
  Solid = true
  Symmetric = false
FEATURE [Sketcher::SketchObject] Sketch025
  FullyConstrained = true
  sketch-geometry (7):
    g0: LineSegment StartX=0 StartY=0 StartZ=0 EndX=0 EndY=6 EndZ=0
    g1: Circle CenterX=0 CenterY=0 CenterZ=0 NormalX=0 NormalY=0 NormalZ=1 AngleXU=0 Radius=1
    g2: Circle CenterX=8 CenterY=6 CenterZ=0 NormalX=0 NormalY=0 NormalZ=1 AngleXU=0 Radius=1
    g3: BSplineCurve PolesCount=3 KnotsCount=2 Degree=2 IsPeriodic=0
    g4: GeomPoint X=0 Y=0 Z=0
    g5: GeomPoint X=8 Y=6 Z=0
    g6: LineSegment StartX=0 StartY=6 StartZ=0 EndX=8 EndY=6 EndZ=0
  constraints (14):
    c: Coincident(g0,g-1)
    c: Distance(g0) = 6
    c: Vertical(g0)
    c: Coincident(g3,g0)
    c: Weight(g1) = 1
    c: Equal(g1,g2)
    c: InternalAlignment(g1,g3)
    c: InternalAlignment(g2,g3)
    c: InternalAlignment(g4,g3)
    c: InternalAlignment(g5,g3)
    c: Block(g3)
    c: Coincident(g6,g0)
    c: Coincident(g6,g3)
    c: Horizontal(g6)
FEATURE [Part::Extrusion] Extrude019  label="caseScrewPillarBracket007"
  Base = -> Sketch025
  Dir = (0,0,1)
  DirMode = 2
  FaceMakerClass = Part::FaceMakerBullseye
  LengthFwd = 2.4
  LengthRev = 0
  Placement = pos=(101.3,29,65.23) rot=(0,1,0;1.5708rad)
  Solid = true
  Symmetric = false
FEATURE [Part::Box] Box011  label="frontCaseScrewPillarBracket"
  AttacherType = Attacher::AttachEngine3D
  Height = 2.4
  Length = 16
  Placement = pos=(87,28,2.3) rot=(0,0,1;0rad)
  Width = 7
FEATURE [Part::Box] Box012  label="frontCaseScrewPillarBracket001"
  AttacherType = Attacher::AttachEngine3D
  Height = 2.4
  Length = 16
  Placement = pos=(87,28,67.3) rot=(0,0,1;0rad)
  Width = 7
FEATURE [Sketcher::SketchObject] Sketch026
  FullyConstrained = true
  sketch-geometry (17):
    g0: Circle CenterX=-3.5 CenterY=23.5 CenterZ=0 NormalX=0 NormalY=0 NormalZ=1 AngleXU=0 Radius=1
    g1: Circle CenterX=-1 CenterY=15.25 CenterZ=0 NormalX=0 NormalY=0 NormalZ=1 AngleXU=0 Radius=1
    g2: Circle CenterX=-3.5 CenterY=7 CenterZ=0 NormalX=0 NormalY=0 NormalZ=1 AngleXU=0 Radius=1
    g3: BSplineCurve PolesCount=3 KnotsCount=2 Degree=2 IsPeriodic=0
    g4: GeomPoint X=-3.5 Y=23.5 Z=0
    g5: GeomPoint X=-3.5 Y=7 Z=0
    g6: Circle CenterX=-4.8 CenterY=30.5 CenterZ=0 NormalX=0 NormalY=0 NormalZ=1 AngleXU=0 Radius=1
    g7: Circle CenterX=-3.5 CenterY=30.5 CenterZ=0 NormalX=0 NormalY=0 NormalZ=1 AngleXU=0 Radius=1
    g8: Circle CenterX=-3.5 CenterY=29.2 CenterZ=0 NormalX=0 NormalY=0 NormalZ=1 AngleXU=0 Radius=1
    g9: BSplineCurve PolesCount=3 KnotsCount=2 Degree=2 IsPeriodic=0
    g10: GeomPoint X=-4.8 Y=30.5 Z=0
    g11: GeomPoint X=-3.5 Y=29.2 Z=0
    g12: LineSegment StartX=-3.5 StartY=29.2 StartZ=0 EndX=-3.5 EndY=23.5 EndZ=0
    g13: LineSegment StartX=-4.8 StartY=30.5 StartZ=0 EndX=0 EndY=30.5 EndZ=0
    g14: LineSegment StartX=-3.5 StartY=5 StartZ=0 EndX=-3.5 EndY=7 EndZ=0
    g15: LineSegment StartX=0 StartY=5 StartZ=0 EndX=0 EndY=30.5 EndZ=0
    g16: LineSegment StartX=-3.5 StartY=5 StartZ=0 EndX=0 EndY=5 EndZ=0
  constraints (33):
    c: Weight(g0) = 1
    c: Equal(g0,g1)
    c: Equal(g0,g2)
    c: InternalAlignment(g0,g3)
    c: InternalAlignment(g1,g3)
    c: InternalAlignment(g2,g3)
    c: InternalAlignment(g4,g3)
    c: InternalAlignment(g5,g3)
    c: Block(g3)
    c: Weight(g6) = 1
    c: Equal(g6,g7)
    c: Equal(g6,g8)
    c: InternalAlignment(g6,g9)
    c: InternalAlignment(g7,g9)
    c: InternalAlignment(g8,g9)
    c: InternalAlignment(g10,g9)
    c: InternalAlignment(g11,g9)
    c: Block(g9)
    c: Coincident(g12,g9)
    c: Coincident(g12,g3)
    c: Vertical(g12)
    c: Coincident(g13,g9)
    c: Horizontal(g13)
    c: Distance(g13) = 4.8
    c: Coincident(g14,g3)
    c: Vertical(g14)
    c: Coincident(g15,g13)
    c: Vertical(g15)
    c: Tangent(g15,g1)
    c: Distance(g14) = 2
    c: Coincident(g16,g14)
    c: Horizontal(g16)
    c: Coincident(g15,g16)
FEATURE [Part::Feature] Face050
  shape: bbox 4.8 x 25.5 x 2e-07 mm, 1 faces, 0 solids (baked)
FEATURE [Part::Revolution] Revolve054  label="moreFrontCaseScrewPost001"
  Angle = 360
  Axis = (0,1,0)
  Base = (0,0,0)
  FaceMakerClass = Part::FaceMakerBullseye
  Placement = pos=(102.5,4.5,3.5) rot=(0,0,1;0rad)
  Solid = false
  Source = -> Face050
  Symmetric = false
FEATURE [Part::Feature] Face051
  shape: bbox 4.8 x 25.5 x 2e-07 mm, 1 faces, 0 solids (baked)
FEATURE [Part::Revolution] Revolve055  label="moreFrontCaseScrewPost002"
  Angle = 360
  Axis = (0,1,0)
  Base = (0,0,0)
  FaceMakerClass = Part::FaceMakerBullseye
  Placement = pos=(102.5,4.5,68.5) rot=(0,0,1;0rad)
  Solid = false
  Source = -> Face051
  Symmetric = false
FEATURE [Sketcher::SketchObject] Sketch027
  FullyConstrained = true
  sketch-geometry (10):
    g0: LineSegment StartX=-1.6 StartY=4.7 StartZ=0 EndX=-1.6 EndY=1.7 EndZ=0
    g1: LineSegment StartX=-3.5 StartY=4.7 StartZ=0 EndX=-1.6 EndY=4.7 EndZ=0
    g2: LineSegment StartX=-1.6 StartY=1.7 StartZ=0 EndX=-1.6 EndY=1.5 EndZ=0
    g3: LineSegment StartX=-1.6 StartY=1.5 StartZ=0 EndX=-5.2 EndY=1.5 EndZ=0
    g4: Circle CenterX=-3.5 CenterY=4.7 CenterZ=0 NormalX=0 NormalY=0 NormalZ=1 AngleXU=0 Radius=1
    g5: Circle CenterX=-3.59627 CenterY=2.99743 CenterZ=0 NormalX=0 NormalY=0 NormalZ=1 AngleXU=0 Radius=1
    g6: Circle CenterX=-5.2 CenterY=1.5 CenterZ=0 NormalX=0 NormalY=0 NormalZ=1 AngleXU=0 Radius=1
    g7: BSplineCurve PolesCount=3 KnotsCount=2 Degree=2 IsPeriodic=0
    g8: GeomPoint X=-3.5 Y=4.7 Z=0
    g9: GeomPoint X=-5.2 Y=1.5 Z=0
  constraints (23):
    c: Vertical(g0)
    c: Distance(g0) = 3
    c: Coincident(g1,g0)
    c: Horizontal(g1)
    c: Block(g0)
    c: Block(g1)
    c: Coincident(g2,g0)
    c: Vertical(g2)
    c: Distance(g2) = 0.2
    c: Coincident(g3,g2)
    c: Horizontal(g3)
    c: Block(g3)
    c: Coincident(g7,g1)
    c: Weight(g4) = 1
    c: Equal(g4,g5)
    c: Equal(g4,g6)
    c: Coincident(g7,g3)
    c: InternalAlignment(g4,g7)
    c: InternalAlignment(g5,g7)
    c: InternalAlignment(g6,g7)
    c: InternalAlignment(g8,g7)
    c: InternalAlignment(g9,g7)
    c: Block(g7)
FEATURE [Sketcher::SketchObject] Sketch028
  FullyConstrained = true
  sketch-geometry (18):
    g0: LineSegment StartX=0 StartY=3e-16 StartZ=0 EndX=0 EndY=1.7 EndZ=0
    g1: LineSegment StartX=-3.5 StartY=0 StartZ=0 EndX=-3.5 EndY=0.9 EndZ=0
    g2: Circle CenterX=-2.7 CenterY=1.7 CenterZ=0 NormalX=0 NormalY=0 NormalZ=1 AngleXU=0 Radius=1
    g3: Circle CenterX=-3.5 CenterY=1.7 CenterZ=0 NormalX=0 NormalY=0 NormalZ=1 AngleXU=0 Radius=1
    g4: Circle CenterX=-3.5 CenterY=0.9 CenterZ=0 NormalX=0 NormalY=0 NormalZ=1 AngleXU=0 Radius=1
    g5: BSplineCurve PolesCount=3 KnotsCount=2 Degree=2 IsPeriodic=0
    g6: GeomPoint X=-2.7 Y=1.7 Z=0
    g7: GeomPoint X=-3.5 Y=0.9 Z=0
    g8: LineSegment StartX=-3.5 StartY=0 StartZ=0 EndX=-3.5 EndY=-7 EndZ=0
    g9: LineSegment StartX=0 StartY=3e-16 StartZ=0 EndX=0 EndY=-7 EndZ=0
    g10: LineSegment StartX=-3.5 StartY=-7 StartZ=0 EndX=0 EndY=-7 EndZ=0
    g11: LineSegment StartX=-2.7 StartY=1.7 StartZ=0 EndX=-1.6 EndY=1.7 EndZ=0
    g12: LineSegment StartX=0 StartY=1.7 StartZ=0 EndX=0 EndY=4.5 EndZ=0
    g13: LineSegment StartX=0 StartY=4.5 StartZ=0 EndX=0 EndY=10.8 EndZ=0
    g14: LineSegment StartX=0 StartY=10.8 StartZ=0 EndX=-2 EndY=10.8 EndZ=0
    g15: LineSegment StartX=-1.6 StartY=4.7 StartZ=0 EndX=-1.6 EndY=1.7 EndZ=0
    g16: LineSegment StartX=-1.6 StartY=4.7 StartZ=0 EndX=-2 EndY=4.7 EndZ=0
    g17: LineSegment StartX=-2 StartY=4.7 StartZ=0 EndX=-2 EndY=10.8 EndZ=0
  constraints (44):
    c: Vertical(g0)
    c: Vertical(g1)
    c: Distance(g1) = 0.9
    c: Block(g0)
    c: Distance(g0) = 1.7
    c: Weight(g2) = 1
    c: Equal(g2,g3)
    c: Equal(g2,g4)
    c: Coincident(g5,g1)
    c: InternalAlignment(g2,g5)
    c: InternalAlignment(g3,g5)
    c: InternalAlignment(g4,g5)
    c: InternalAlignment(g6,g5)
    c: InternalAlignment(g7,g5)
    c: Block(g5)
    c: Coincident(g8,g1)
    c: Vertical(g8)
    c: Distance(g8) = 7
    c: Vertical(g9)
    c: Equal(g8,g9) = 7
    c: Coincident(g9,g0)
    c: Coincident(g10,g8)
    c: Coincident(g10,g9)
    c: Horizontal(g10)
    c: Coincident(g11,g5)
    c: Horizontal(g11)
    c: Coincident(g12,g0)
    c: Vertical(g12)
    c: Distance(g12) = 2.8
    c: Coincident(g13,g12)
    c: Vertical(g13)
    c: Distance(g13) = 6.3
    c: Coincident(g14,g13)
    c: Horizontal(g14)
    c: Distance(g14) = 2
    c: Vertical(g15)
    c: Distance(g15) = 3
    c: Block(g11)
    c: Coincident(g15,g11)
    c: Coincident(g16,g15)
    c: Horizontal(g16)
    c: Coincident(g17,g16)
    c: Coincident(g17,g14)
    c: Vertical(g17)
FEATURE [Part::Revolution] Revolve040  label="backCaseScrewRetainer001"
  Angle = 360
  Axis = (0,1,0)
  Base = (0,0,0)
  FaceMakerClass = Part::FaceMakerBullseye
  Placement = pos=(12.5,3,10) rot=(0,0,1;0rad)
  Solid = false
  Source = -> Face036
  Symmetric = false
FEATURE [Part::Feature] Face055
  shape: bbox 3.5 x 30.2 x 2e-07 mm, 1 faces, 0 solids (baked)
FEATURE [Part::Revolution] Revolve059  label="backCaseScrewPost"
  Angle = 360
  Axis = (0,1,0)
  Base = (0,0,0)
  FaceMakerClass = Part::FaceMakerBullseye
  Placement = pos=(12.5,4.5,10) rot=(0,0,1;0rad)
  Solid = false
  Source = -> Face055
  Symmetric = false
FEATURE [Part::Feature] Face056
  shape: bbox 3.5 x 30.2 x 2e-07 mm, 1 faces, 0 solids (baked)
FEATURE [Part::Revolution] Revolve060  label="backCaseScrewPost001"
  Angle = 360
  Axis = (0,1,0)
  Base = (0,0,0)
  FaceMakerClass = Part::FaceMakerBullseye
  Placement = pos=(12.5,4.5,62) rot=(0,0,1;0rad)
  Solid = false
  Source = -> Face056
  Symmetric = false
FEATURE [Part::Feature] Face057
  shape: bbox 3.5 x 17.8 x 2e-07 mm, 1 faces, 0 solids (baked)
FEATURE [Part::Revolution] Revolve061  label="removeToCreateScrewAndThreadedInsertHole"
  Angle = 360
  Axis = (0,1,0)
  Base = (0,0,0)
  FaceMakerClass = Part::FaceMakerBullseye
  Placement = pos=(12.5,0,10) rot=(0,0,1;0rad)
  Solid = false
  Source = -> Face057
  Symmetric = false
FEATURE [Part::Feature] Face058
  shape: bbox 3.5 x 17.8 x 2e-07 mm, 1 faces, 0 solids (baked)
FEATURE [Part::Revolution] Revolve062  label="removeToCreateScrewAndThreadedInsertHole001"
  Angle = 360
  Axis = (0,1,0)
  Base = (0,0,0)
  FaceMakerClass = Part::FaceMakerBullseye
  Placement = pos=(12.5,0,62) rot=(0,0,1;0rad)
  Solid = false
  Source = -> Face058
  Symmetric = false
FEATURE [Part::Feature] Face059
  shape: bbox 3.5 x 17.8 x 2e-07 mm, 1 faces, 0 solids (baked)
FEATURE [Part::Revolution] Revolve063  label="removeToCreateScrewAndThreadedInsertHole002"
  Angle = 360
  Axis = (0,1,0)
  Base = (0,0,0)
  FaceMakerClass = Part::FaceMakerBullseye
  Placement = pos=(89.5,0,68.5) rot=(0,0,1;0rad)
  Solid = false
  Source = -> Face059
  Symmetric = false
FEATURE [Part::Feature] Face060
  shape: bbox 3.5 x 17.8 x 2e-07 mm, 1 faces, 0 solids (baked)
FEATURE [Part::Revolution] Revolve064  label="removeToCreateScrewAndThreadedInsertHole003"
  Angle = 360
  Axis = (0,1,0)
  Base = (0,0,0)
  FaceMakerClass = Part::FaceMakerBullseye
  Placement = pos=(89.5,0,3.5) rot=(0,0,1;0rad)
  Solid = false
  Source = -> Face060
  Symmetric = false
FEATURE [Part::Feature] Face061
  shape: bbox 3.5 x 17.8 x 2e-07 mm, 1 faces, 0 solids (baked)
FEATURE [Part::Revolution] Revolve065  label="removeToCreateScrewAndThreadedInsertHole004"
  Angle = 360
  Axis = (0,1,0)
  Base = (0,0,0)
  FaceMakerClass = Part::FaceMakerBullseye
  Placement = pos=(102.5,4.7,3.5) rot=(0,0,1;0rad)
  Solid = false
  Source = -> Face061
  Symmetric = false
FEATURE [Part::Feature] Face062
  shape: bbox 3.5 x 17.8 x 2e-07 mm, 1 faces, 0 solids (baked)
FEATURE [Part::Revolution] Revolve066  label="removeToCreateScrewAndThreadedInsertHole005"
  Angle = 360
  Axis = (0,1,0)
  Base = (0,0,0)
  FaceMakerClass = Part::FaceMakerBullseye
  Placement = pos=(102.5,4.7,68.5) rot=(0,0,1;0rad)
  Solid = false
  Source = -> Face062
  Symmetric = false
FEATURE [Part::MultiFuse] Fusion047  label="makeHoles"
  Shapes = -> [Revolve066,Revolve065,Revolve064,Revolve063,Revolve062,Revolve061]
FEATURE [Part::Feature] Face063
  shape: bbox 3.6 x 3.2 x 2e-07 mm, 1 faces, 0 solids (baked)
FEATURE [Part::Revolution] Revolve067  label="moreFrontCaseScrewRetainer002"
  Angle = 360
  Axis = (0,1,0)
  Base = (0,0,0)
  FaceMakerClass = Part::FaceMakerBullseye
  Placement = pos=(102.5,4.5,68.5) rot=(0,0,1;0rad)
  Solid = false
  Source = -> Face063
  Symmetric = false
FEATURE [Part::Feature] Face064
  shape: bbox 3.6 x 3.2 x 2e-07 mm, 1 faces, 0 solids (baked)
FEATURE [Part::Revolution] Revolve068  label="moreFrontCaseScrewRetainer003"
  Angle = 360
  Axis = (0,1,0)
  Base = (0,0,0)
  FaceMakerClass = Part::FaceMakerBullseye
  Placement = pos=(102.5,4.5,3.5) rot=(0,0,1;0rad)
  Solid = false
  Source = -> Face064
  Symmetric = false
FEATURE [Part::Feature] Face065
  shape: bbox 3.5 x 17.8 x 2e-07 mm, 1 faces, 0 solids (baked)
FEATURE [Part::Revolution] Revolve069  label="removeToCreateScrewAndThreadedInsertHole006"
  Angle = 360
  Axis = (0,1,0)
  Base = (0,0,0)
  FaceMakerClass = Part::FaceMakerBullseye
  Placement = pos=(12.5,0,10) rot=(0,0,1;0rad)
  Solid = false
  Source = -> Face065
  Symmetric = false
FEATURE [Part::Feature] Face066
  shape: bbox 3.5 x 17.8 x 2e-07 mm, 1 faces, 0 solids (baked)
FEATURE [Part::Revolution] Revolve070  label="removeToCreateScrewAndThreadedInsertHole007"
  Angle = 360
  Axis = (0,1,0)
  Base = (0,0,0)
  FaceMakerClass = Part::FaceMakerBullseye
  Placement = pos=(12.5,0,62) rot=(0,0,1;0rad)
  Solid = false
  Source = -> Face066
  Symmetric = false
FEATURE [Part::Feature] Face067
  shape: bbox 3.5 x 17.8 x 2e-07 mm, 1 faces, 0 solids (baked)
FEATURE [Part::Revolution] Revolve071  label="removeToCreateScrewAndThreadedInsertHole008"
  Angle = 360
  Axis = (0,1,0)
  Base = (0,0,0)
  FaceMakerClass = Part::FaceMakerBullseye
  Placement = pos=(89.5,0,68.5) rot=(0,0,1;0rad)
  Solid = false
  Source = -> Face067
  Symmetric = false
FEATURE [Part::Feature] Face068
  shape: bbox 3.5 x 17.8 x 2e-07 mm, 1 faces, 0 solids (baked)
FEATURE [Part::Revolution] Revolve072  label="removeToCreateScrewAndThreadedInsertHole009"
  Angle = 360
  Axis = (0,1,0)
  Base = (0,0,0)
  FaceMakerClass = Part::FaceMakerBullseye
  Placement = pos=(89.5,0,3.5) rot=(0,0,1;0rad)
  Solid = false
  Source = -> Face068
  Symmetric = false
FEATURE [Part::Feature] Face069
  shape: bbox 3.5 x 17.8 x 2e-07 mm, 1 faces, 0 solids (baked)
FEATURE [Part::Feature] Face070
  shape: bbox 3.5 x 17.8 x 2e-07 mm, 1 faces, 0 solids (baked)
FEATURE [Part::Revolution] Revolve073  label="removeToCreateScrewAndThreadedInsertHole010"
  Angle = 360
  Axis = (0,1,0)
  Base = (0,0,0)
  FaceMakerClass = Part::FaceMakerBullseye
  Placement = pos=(102.5,4.7,3.5) rot=(0,0,1;0rad)
  Solid = false
  Source = -> Face069
  Symmetric = false
FEATURE [Part::Revolution] Revolve074  label="removeToCreateScrewAndThreadedInsertHole011"
  Angle = 360
  Axis = (0,1,0)
  Base = (0,0,0)
  FaceMakerClass = Part::FaceMakerBullseye
  Placement = pos=(102.5,4.7,68.5) rot=(0,0,1;0rad)
  Solid = false
  Source = -> Face070
  Symmetric = false
FEATURE [Part::MultiFuse] Fusion048  label="makeHoles001"
  Shapes = -> [Revolve074,Revolve073,Revolve072,Revolve071,Revolve070,Revolve069]
FEATURE [Part::MultiFuse] Fusion049  label="caseScrewRetainers"
  Shapes = -> [Revolve067,Revolve068,Revolve048,Revolve047,Revolve039,Revolve040]
FEATURE [Part::Cut] Cut015  label="caseScrewRetainers001"
  Base = -> Fusion049
  Tool = -> Fusion048
FEATURE [Part::MultiFuse] Fusion050  label="casePillars"
  Shapes = -> [Revolve055,Revolve054,Revolve043,Revolve046,Revolve059,Revolve060]
FEATURE [Part::Feature] Face071 .. Face076  x6 (patterned run collapsed; names and placements below)
  shape: bbox 3.5 x 17.8 x 2e-07 mm, 1 faces, 0 solids (baked)
FEATURE [Part::Revolution] Revolve075  label="removeToCreateScrewAndThreadedInsertHole012"
  Angle = 360
  Axis = (0,1,0)
  Base = (0,0,0)
  FaceMakerClass = Part::FaceMakerBullseye
  Placement = pos=(12.5,0,10) rot=(0,0,1;0rad)
  Solid = false
  Source = -> Face071
  Symmetric = false
FEATURE [Part::Revolution] Revolve076  label="removeToCreateScrewAndThreadedInsertHole013"
  Angle = 360
  Axis = (0,1,0)
  Base = (0,0,0)
  FaceMakerClass = Part::FaceMakerBullseye
  Placement = pos=(12.5,0,62) rot=(0,0,1;0rad)
  Solid = false
  Source = -> Face072
  Symmetric = false
FEATURE [Part::Revolution] Revolve077  label="removeToCreateScrewAndThreadedInsertHole014"
  Angle = 360
  Axis = (0,1,0)
  Base = (0,0,0)
  FaceMakerClass = Part::FaceMakerBullseye
  Placement = pos=(89.5,0,68.5) rot=(0,0,1;0rad)
  Solid = false
  Source = -> Face073
  Symmetric = false
FEATURE [Part::Revolution] Revolve078  label="removeToCreateScrewAndThreadedInsertHole015"
  Angle = 360
  Axis = (0,1,0)
  Base = (0,0,0)
  FaceMakerClass = Part::FaceMakerBullseye
  Placement = pos=(89.5,0,3.5) rot=(0,0,1;0rad)
  Solid = false
  Source = -> Face074
  Symmetric = false
FEATURE [Part::Revolution] Revolve079  label="removeToCreateScrewAndThreadedInsertHole016"
  Angle = 360
  Axis = (0,1,0)
  Base = (0,0,0)
  FaceMakerClass = Part::FaceMakerBullseye
  Placement = pos=(102.5,4.7,3.5) rot=(0,0,1;0rad)
  Solid = false
  Source = -> Face075
  Symmetric = false
FEATURE [Part::Revolution] Revolve080  label="removeToCreateScrewAndThreadedInsertHole017"
  Angle = 360
  Axis = (0,1,0)
  Base = (0,0,0)
  FaceMakerClass = Part::FaceMakerBullseye
  Placement = pos=(102.5,4.7,68.5) rot=(0,0,1;0rad)
  Solid = false
  Source = -> Face076
  Symmetric = false
FEATURE [Part::MultiFuse] Fusion051  label="makeHoles002"
  Shapes = -> [Revolve080,Revolve079,Revolve078,Revolve077,Revolve076,Revolve075]
FEATURE [Part::Cut] Cut016  label="caesPillars"
  Base = -> Fusion050
  Tool = -> Fusion051
FEATURE [Part::Revolution] Revolve009  label="plugHousing016"
  Angle = 360
  Axis = (0,1,0)
  Base = (0,0,0)
  FaceMakerClass = Part::FaceMakerBullseye
  Placement = pos=(0,0,36.15) rot=(0,0,1;0rad)
  Solid = false
  Source = -> Face012
  Symmetric = false
FEATURE [Part::MultiFuse] Fusion014  label="plugHousing023"
  Placement = pos=(0,0,0) rot=(0,0,1;1.5708rad)
  Shapes = -> [Revolve011,Revolve009]
FEATURE [Part::Revolution] Revolve010  label="plugHousing017"
  Angle = 360
  Axis = (0,1,0)
  Base = (0,0,0)
  FaceMakerClass = Part::FaceMakerBullseye
  Placement = pos=(0,0,36.15) rot=(0,0,1;0rad)
  Solid = false
  Source = -> Face014
  Symmetric = false
FEATURE [Part::MultiFuse] Fusion015  label="plugHousing024"
  Placement = pos=(0,0,0) rot=(0,0,1;1.5708rad)
  Shapes = -> [Revolve010,Revolve015]
FEATURE [Part::Revolution] Revolve014  label="plugHousing026"
  Angle = 360
  Axis = (0,1,0)
  Base = (0,0,0)
  FaceMakerClass = Part::FaceMakerBullseye
  Placement = pos=(0,0,36.15) rot=(0,0,1;0rad)
  Solid = false
  Source = -> Face011
  Symmetric = false
FEATURE [Part::Revolution] Revolve013  label="plugHousing025"
  Angle = 360
  Axis = (0,1,0)
  Base = (0,0,0)
  FaceMakerClass = Part::FaceMakerBullseye
  Placement = pos=(0,0,36.15) rot=(0,0,1;0rad)
  Solid = false
  Source = -> Face015
  Symmetric = false
FEATURE [Part::MultiFuse] Fusion016  label="plugHousing028"
  Placement = pos=(0,19,0) rot=(0,0,1;3.14159rad)
  Shapes = -> [Fusion014,Fusion013]
FEATURE [Part::MultiFuse] Fusion011  label="plugHousing018"
  Placement = pos=(0,0,0) rot=(0,0,1;1.5708rad)
  Shapes = -> [Revolve014,Revolve013]
FEATURE [Part::MultiFuse] Fusion012  label="plugHousing019"
  Placement = pos=(0,19,0) rot=(0,0,1;3.14159rad)
  Shapes = -> [Fusion011,Fusion015]
FEATURE [Part::MultiFuse] Fusion017  label="plugHousing029"
  Placement = pos=(122.621,0,-0.15) rot=(0,0,1;0rad)
  Shapes = -> [Fusion016,Fusion012]
FEATURE [Part::MultiFuse] Fusion052  label="casePillarRetainers"
  Shapes = -> [Extrude012,Extrude013,Extrude014,Extrude015,Extrude016,Extrude017,Extrude018,Extrude019,Box011,Box012]
FEATURE [Part::Feature] Face077
  shape: bbox 3.5 x 17.8 x 2e-07 mm, 1 faces, 0 solids (baked)
FEATURE [Part::Revolution] Revolve081  label="removeToCreateScrewAndThreadedInsertHole018"
  Angle = 360
  Axis = (0,1,0)
  Base = (0,0,0)
  FaceMakerClass = Part::FaceMakerBullseye
  Placement = pos=(62.3,30.3,19.7) rot=(0,0,1;0rad)
  Solid = false
  Source = -> Face077
  Symmetric = false
FEATURE [Part::Feature] Face078
  shape: bbox 3.5 x 17.8 x 2e-07 mm, 1 faces, 0 solids (baked)
FEATURE [Part::Revolution] Revolve082  label="removeToCreateScrewAndThreadedInsertHole019"
  Angle = 360
  Axis = (0,1,0)
  Base = (0,0,0)
  FaceMakerClass = Part::FaceMakerBullseye
  Placement = pos=(62.3,30.3,51.7) rot=(0,0,1;0rad)
  Solid = false
  Source = -> Face078
  Symmetric = false
FEATURE [Part::Feature] Face079
  shape: bbox 3.5 x 17.8 x 2e-07 mm, 1 faces, 0 solids (baked)
FEATURE [Part::Revolution] Revolve083  label="removeToCreateScrewAndThreadedInsertHole020"
  Angle = 360
  Axis = (0,1,0)
  Base = (0,0,0)
  FaceMakerClass = Part::FaceMakerBullseye
  Placement = pos=(30.3,30.3,19.7) rot=(0,0,1;0rad)
  Solid = false
  Source = -> Face079
  Symmetric = false
FEATURE [Part::Feature] Face080
  shape: bbox 3.5 x 17.8 x 2e-07 mm, 1 faces, 0 solids (baked)
FEATURE [Part::Revolution] Revolve084  label="removeToCreateScrewAndThreadedInsertHole021"
  Angle = 360
  Axis = (0,1,0)
  Base = (0,0,0)
  FaceMakerClass = Part::FaceMakerBullseye
  Placement = pos=(30.3,30.3,51.7) rot=(0,0,1;0rad)
  Solid = false
  Source = -> Face080
  Symmetric = false
FEATURE [Part::MultiFuse] Fusion053  label="createThreadedInsertHolesForFan"
  Shapes = -> [Revolve081,Revolve082,Revolve083,Revolve084]
FEATURE [Part::Cut] Cut017  label="fanScrewHousing001"
  Base = -> Fusion046
  Tool = -> Fusion053
FEATURE [Part::Feature] Face081
  shape: bbox 3.5 x 17.8 x 2e-07 mm, 1 faces, 0 solids (baked)
FEATURE [Part::Revolution] Revolve085  label="removeToCreateScrewAndThreadedInsertHole022"
  Angle = 360
  Axis = (0,1,0)
  Base = (0,0,0)
  FaceMakerClass = Part::FaceMakerBullseye
  Placement = pos=(62.3,30.3,19.7) rot=(0,0,1;0rad)
  Solid = false
  Source = -> Face081
  Symmetric = false
FEATURE [Part::Feature] Face082
  shape: bbox 3.5 x 17.8 x 2e-07 mm, 1 faces, 0 solids (baked)
FEATURE [Part::Revolution] Revolve086  label="removeToCreateScrewAndThreadedInsertHole023"
  Angle = 360
  Axis = (0,1,0)
  Base = (0,0,0)
  FaceMakerClass = Part::FaceMakerBullseye
  Placement = pos=(62.3,30.3,51.7) rot=(0,0,1;0rad)
  Solid = false
  Source = -> Face082
  Symmetric = false
FEATURE [Part::Feature] Face083
  shape: bbox 3.5 x 17.8 x 2e-07 mm, 1 faces, 0 solids (baked)
FEATURE [Part::Revolution] Revolve087  label="removeToCreateScrewAndThreadedInsertHole024"
  Angle = 360
  Axis = (0,1,0)
  Base = (0,0,0)
  FaceMakerClass = Part::FaceMakerBullseye
  Placement = pos=(30.3,30.3,19.7) rot=(0,0,1;0rad)
  Solid = false
  Source = -> Face083
  Symmetric = false
FEATURE [Part::Feature] Face084
  shape: bbox 3.5 x 17.8 x 2e-07 mm, 1 faces, 0 solids (baked)
FEATURE [Part::Revolution] Revolve088  label="removeToCreateScrewAndThreadedInsertHole025"
  Angle = 360
  Axis = (0,1,0)
  Base = (0,0,0)
  FaceMakerClass = Part::FaceMakerBullseye
  Placement = pos=(30.3,30.3,51.7) rot=(0,0,1;0rad)
  Solid = false
  Source = -> Face084
  Symmetric = false
FEATURE [Part::MultiFuse] Fusion054  label="createThreadedInsertHolesForFan001"
  Shapes = -> [Revolve085,Revolve086,Revolve087,Revolve088]
FEATURE [Part::Cut] Cut018  label="top007"
  Base = -> Fusion040
  Tool = -> Fusion054
FEATURE [Sketcher::SketchObject] Sketch029
  FullyConstrained = false
  Placement = pos=(0,0,0) rot=(1,0,0;1.5708rad)
  sketch-geometry (24):
    g0: ArcOfCircle CenterX=-4 CenterY=-10.5 CenterZ=0 NormalX=0 NormalY=0 NormalZ=1 AngleXU=0 Radius=1.5 StartAngle=6e-16 EndAngle=3.14159
    g1: ArcOfCircle CenterX=-34.2 CenterY=-10.5 CenterZ=0 NormalX=0 NormalY=0 NormalZ=1 AngleXU=0 Radius=1.5 StartAngle=0 EndAngle=3.14159
    g2: ArcOfCircle CenterX=-34.2 CenterY=-27.7 CenterZ=0 NormalX=0 NormalY=0 NormalZ=1 AngleXU=0 Radius=1.5 StartAngle=3.14159 EndAngle=6.28319
    g3: ArcOfCircle CenterX=-4 CenterY=-27.7 CenterZ=0 NormalX=0 NormalY=0 NormalZ=1 AngleXU=0 Radius=1.5 StartAngle=3.1416 EndAngle=6.28319
    g4: ArcOfCircle CenterX=-10 CenterY=-4.3 CenterZ=0 NormalX=0 NormalY=0 NormalZ=1 AngleXU=0 Radius=1.5 StartAngle=2e-16 EndAngle=3.14159
    g5: ArcOfCircle CenterX=-16.1 CenterY=-1.8 CenterZ=0 NormalX=0 NormalY=0 NormalZ=1 AngleXU=0 Radius=1.5 StartAngle=5e-16 EndAngle=3.14159
    g6: ArcOfCircle CenterX=-22.1 CenterY=-1.8 CenterZ=0 NormalX=0 NormalY=0 NormalZ=1 AngleXU=0 Radius=1.5 StartAngle=5e-16 EndAngle=3.14159
    g7: ArcOfCircle CenterX=-28.2 CenterY=-4.3 CenterZ=0 NormalX=0 NormalY=0 NormalZ=1 AngleXU=0 Radius=1.5 StartAngle=2e-16 EndAngle=3.14159
    g8: ArcOfCircle CenterX=-10 CenterY=-33.9 CenterZ=0 NormalX=0 NormalY=0 NormalZ=1 AngleXU=0 Radius=1.5 StartAngle=3.14159 EndAngle=6.28319
    g9: ArcOfCircle CenterX=-16.1 CenterY=-36.4 CenterZ=0 NormalX=0 NormalY=0 NormalZ=1 AngleXU=0 Radius=1.5 StartAngle=3.14159 EndAngle=6.28319
    g10: ArcOfCircle CenterX=-22.1 CenterY=-36.4 CenterZ=0 NormalX=0 NormalY=0 NormalZ=1 AngleXU=0 Radius=1.5 StartAngle=3.14159 EndAngle=6.28319
    g11: ArcOfCircle CenterX=-28.2 CenterY=-33.9 CenterZ=0 NormalX=0 NormalY=0 NormalZ=1 AngleXU=0 Radius=1.5 StartAngle=3.14159 EndAngle=6.28319
    g12: LineSegment StartX=-35.7 StartY=-10.5 StartZ=0 EndX=-35.7 EndY=-27.7 EndZ=0
    g13: LineSegment StartX=-32.7 StartY=-10.5 StartZ=0 EndX=-32.7 EndY=-27.7 EndZ=0
    g14: LineSegment StartX=-29.7 StartY=-33.9 StartZ=0 EndX=-29.7 EndY=-4.3 EndZ=0
    g15: LineSegment StartX=-26.7 StartY=-33.9 StartZ=0 EndX=-26.7 EndY=-4.3 EndZ=0
    g16: LineSegment StartX=-2.5 StartY=-10.5 StartZ=0 EndX=-2.5 EndY=-27.7 EndZ=0
    g17: LineSegment StartX=-8.5 StartY=-4.3 StartZ=0 EndX=-8.5 EndY=-33.9 EndZ=0
    g18: LineSegment StartX=-5.5 StartY=-10.5 StartZ=0 EndX=-5.5 EndY=-27.7 EndZ=0
    g19: LineSegment StartX=-11.5 StartY=-4.3 StartZ=0 EndX=-11.5 EndY=-33.9 EndZ=0
    g20: LineSegment StartX=-14.6 StartY=-1.8 StartZ=0 EndX=-14.6 EndY=-36.4 EndZ=0
    g21: LineSegment StartX=-17.6 StartY=-1.8 StartZ=0 EndX=-17.6 EndY=-36.4 EndZ=0
    g22: LineSegment StartX=-20.6 StartY=-36.4 StartZ=0 EndX=-20.6 EndY=-1.8 EndZ=0
    g23: LineSegment StartX=-23.6 StartY=-1.8 StartZ=0 EndX=-23.6 EndY=-36.4 EndZ=0
  constraints (48):
    c: Block(g0)
    c: Block(g1)
    c: Block(g2)
    c: Block(g3)
    c: Block(g4)
    c: Block(g5)
    c: Block(g6)
    c: Block(g7)
    c: Block(g8)
    c: Block(g9)
    c: Block(g10)
    c: Block(g11)
    c: Coincident(g12,g1)
    c: Coincident(g12,g2)
    c: Vertical(g12)
    c: Coincident(g13,g1)
    c: Coincident(g13,g2)
    c: Vertical(g13)
    c: Coincident(g14,g11)
    c: Coincident(g14,g7)
    c: Vertical(g14)
    c: Coincident(g15,g11)
    c: Coincident(g15,g7)
    c: Vertical(g15)
    c: Coincident(g16,g0)
    c: Coincident(g16,g3)
    c: Vertical(g16)
    c: Coincident(g17,g4)
    c: Coincident(g17,g8)
    c: Vertical(g17)
    c: Coincident(g18,g0)
    c: Coincident(g18,g3)
    c: Vertical(g18)
    c: Coincident(g19,g4)
    c: Coincident(g19,g8)
    c: Vertical(g19)
    c: Coincident(g20,g5)
    c: Coincident(g20,g9)
    c: Vertical(g20)
    c: Coincident(g21,g5)
    c: Coincident(g21,g9)
    c: Vertical(g21)
    c: Coincident(g22,g10)
    c: Coincident(g22,g6)
    c: Vertical(g22)
    c: Coincident(g23,g6)
    c: Coincident(g23,g10)
    c: Vertical(g23)
FEATURE [Part::Extrusion] Extrude020  label="removeToCreateFanGrillHoles"
  Base = -> Sketch029
  Dir = (0,-1,6e-16)
  DirMode = 2
  FaceMakerClass = Part::FaceMakerBullseye
  LengthFwd = 10
  LengthRev = 0
  Placement = pos=(65.4,44,54.82) rot=(0,0,1;0rad)
  Solid = true
  Symmetric = false
FEATURE [Part::MultiFuse] Fusion055  label="top008"
  Shapes = -> [Cut017,Cut018]
FEATURE [Part::Cut] Cut019  label="top009"
  Base = -> Fusion055
  Tool = -> Extrude020
FEATURE [App::MeasureDistance] Distance003  label="Distance: 71.95 mm"
  Distance = 71.9513
  P1 = (117,38,72)
  P2 = (117,38,0.0487319)
FEATURE [Sketcher::SketchObject] Sketch030
  FullyConstrained = true
  Placement = pos=(117,19,0) rot=(0.57735,0.57735,0.57735;2.0944rad)
  sketch-geometry (48):
    g0: LineSegment StartX=-49.19 StartY=69.25 StartZ=0 EndX=-49.19 EndY=66.25 EndZ=0
    g1: LineSegment StartX=-49.19 StartY=63.5 StartZ=0 EndX=-49.19 EndY=60.5 EndZ=0
    g2: LineSegment StartX=-49.19 StartY=57.75 StartZ=0 EndX=-49.19 EndY=54.75 EndZ=0
    g3: LineSegment StartX=-49.19 StartY=52 StartZ=0 EndX=-49.19 EndY=49 EndZ=0
    g4: LineSegment StartX=-49.19 StartY=46.25 StartZ=0 EndX=-49.19 EndY=43.25 EndZ=0
    g5: LineSegment StartX=-49.19 StartY=40.5 StartZ=0 EndX=-49.19 EndY=37.5 EndZ=0
    g6: LineSegment StartX=-49.19 StartY=34.5 StartZ=0 EndX=-49.19 EndY=31.5 EndZ=0
    g7: LineSegment StartX=-49.19 StartY=28.75 StartZ=0 EndX=-49.19 EndY=25.75 EndZ=0
    g8: LineSegment StartX=-49.19 StartY=23 StartZ=0 EndX=-49.19 EndY=20 EndZ=0
    g9: LineSegment StartX=-49.19 StartY=17.25 StartZ=0 EndX=-49.19 EndY=14.25 EndZ=0
    g10: LineSegment StartX=-49.19 StartY=11.5 StartZ=0 EndX=-49.19 EndY=8.5 EndZ=0
    g11: LineSegment StartX=-49.19 StartY=5.75 StartZ=0 EndX=-49.19 EndY=2.75 EndZ=0
    g12: ArcOfCircle CenterX=-1.5 CenterY=67.75 CenterZ=0 NormalX=0 NormalY=0 NormalZ=1 AngleXU=0 Radius=1.5 StartAngle=4.71239 EndAngle=7.85398
    g13: ArcOfCircle CenterX=-1.5 CenterY=62 CenterZ=0 NormalX=0 NormalY=0 NormalZ=1 AngleXU=0 Radius=1.5 StartAngle=4.71239 EndAngle=7.85398
    g14: ArcOfCircle CenterX=-1.5 CenterY=56.25 CenterZ=0 NormalX=0 NormalY=0 NormalZ=1 AngleXU=0 Radius=1.5 StartAngle=4.71239 EndAngle=7.85398
    g15: ArcOfCircle CenterX=-11.49 CenterY=50.5 CenterZ=0 NormalX=0 NormalY=0 NormalZ=1 AngleXU=0 Radius=1.5 StartAngle=4.71239 EndAngle=7.85398
    g16: ArcOfCircle CenterX=-16.28 CenterY=44.75 CenterZ=0 NormalX=0 NormalY=0 NormalZ=1 AngleXU=0 Radius=1.5 StartAngle=4.71239 EndAngle=7.85398
    g17: ArcOfCircle CenterX=-18.2337 CenterY=39 CenterZ=0 NormalX=0 NormalY=0 NormalZ=1 AngleXU=0 Radius=1.5 StartAngle=4.71485 EndAngle=7.85398
    g18: ArcOfCircle CenterX=-16.2837 CenterY=27.25 CenterZ=0 NormalX=0 NormalY=0 NormalZ=1 AngleXU=0 Radius=1.5 StartAngle=4.71485 EndAngle=7.85398
    g19: ArcOfCircle CenterX=-18.2337 CenterY=33 CenterZ=0 NormalX=0 NormalY=0 NormalZ=1 AngleXU=0 Radius=1.5 StartAngle=4.71485 EndAngle=7.85398
    g20: ArcOfCircle CenterX=-11.49 CenterY=21.5 CenterZ=0 NormalX=0 NormalY=0 NormalZ=1 AngleXU=0 Radius=1.5 StartAngle=4.71239 EndAngle=7.85398
    g21: ArcOfCircle CenterX=-1.5 CenterY=4.25 CenterZ=0 NormalX=0 NormalY=0 NormalZ=1 AngleXU=0 Radius=1.5 StartAngle=4.71239 EndAngle=7.85398
    g22: ArcOfCircle CenterX=-1.5 CenterY=10 CenterZ=0 NormalX=0 NormalY=0 NormalZ=1 AngleXU=0 Radius=1.5 StartAngle=4.71239 EndAngle=7.85398
    g23: ArcOfCircle CenterX=-1.5 CenterY=15.75 CenterZ=0 NormalX=0 NormalY=0 NormalZ=1 AngleXU=0 Radius=1.5 StartAngle=4.71239 EndAngle=7.85398
    g24: LineSegment StartX=-49.19 StartY=69.25 StartZ=0 EndX=-1.5 EndY=69.25 EndZ=0
    g25: LineSegment StartX=-49.19 StartY=66.25 StartZ=0 EndX=-1.5 EndY=66.25 EndZ=0
    g26: LineSegment StartX=-49.19 StartY=63.5 StartZ=0 EndX=-1.5 EndY=63.5 EndZ=0
    g27: LineSegment StartX=-49.19 StartY=60.5 StartZ=0 EndX=-1.5 EndY=60.5 EndZ=0
    g28: LineSegment StartX=-49.19 StartY=57.75 StartZ=0 EndX=-1.5 EndY=57.75 EndZ=0
    g29: LineSegment StartX=-49.19 StartY=54.75 StartZ=0 EndX=-1.5 EndY=54.75 EndZ=0
    g30: LineSegment StartX=-49.19 StartY=52 StartZ=0 EndX=-11.49 EndY=52 EndZ=0
    g31: LineSegment StartX=-49.19 StartY=49 StartZ=0 EndX=-11.49 EndY=49 EndZ=0
    g32: LineSegment StartX=-49.19 StartY=46.25 StartZ=0 EndX=-16.28 EndY=46.25 EndZ=0
    g33: LineSegment StartX=-49.19 StartY=43.25 StartZ=0 EndX=-16.28 EndY=43.25 EndZ=0
    g34: LineSegment StartX=-49.19 StartY=40.5 StartZ=0 EndX=-18.2337 EndY=40.5 EndZ=0
    g35: LineSegment StartX=-49.19 StartY=37.5 StartZ=0 EndX=-18.23 EndY=37.5 EndZ=0
    g36: LineSegment StartX=-49.19 StartY=34.5 StartZ=0 EndX=-18.2337 EndY=34.5 EndZ=0
    g37: LineSegment StartX=-49.19 StartY=31.5 StartZ=0 EndX=-18.23 EndY=31.5 EndZ=0
    g38: LineSegment StartX=-49.19 StartY=28.75 StartZ=0 EndX=-16.2837 EndY=28.75 EndZ=0
    g39: LineSegment StartX=-49.19 StartY=25.75 StartZ=0 EndX=-16.28 EndY=25.75 EndZ=0
    g40: LineSegment StartX=-49.19 StartY=23 StartZ=0 EndX=-11.49 EndY=23 EndZ=0
    g41: LineSegment StartX=-49.19 StartY=20 StartZ=0 EndX=-11.49 EndY=20 EndZ=0
    g42: LineSegment StartX=-49.19 StartY=17.25 StartZ=0 EndX=-1.5 EndY=17.25 EndZ=0
    g43: LineSegment StartX=-49.19 StartY=14.25 StartZ=0 EndX=-1.5 EndY=14.25 EndZ=0
    g44: LineSegment StartX=-49.19 StartY=11.5 StartZ=0 EndX=-1.5 EndY=11.5 EndZ=0
    g45: LineSegment StartX=-49.19 StartY=8.5 StartZ=0 EndX=-1.5 EndY=8.5 EndZ=0
    g46: LineSegment StartX=-49.19 StartY=5.75 StartZ=0 EndX=-1.5 EndY=5.75 EndZ=0
    g47: LineSegment StartX=-49.19 StartY=2.75 StartZ=0 EndX=-1.5 EndY=2.75 EndZ=0
  constraints (120):
    c: Vertical(g0)
    c: Distance(g0) = 3
    c: Block(g0)
    c: Vertical(g1)
    c: Distance(g1) = 3
    c: Vertical(g2)
    c: Equal(g0,g2) = 3
    c: Block(g2)
    c: Vertical(g3)
    c: Equal(g1,g3) = 3
    c: Vertical(g4)
    c: Equal(g0,g4) = 3
    c: Block(g4)
    c: Vertical(g5)
    c: Equal(g1,g5) = 3
    c: Vertical(g6)
    c: Equal(g0,g6) = 3
    c: Block(g6)
    c: Vertical(g7)
    c: Equal(g1,g7) = 3
    c: Vertical(g8)
    c: Equal(g0,g8) = 3
    c: Block(g8)
    c: Vertical(g9)
    c: Equal(g1,g9) = 3
    c: Vertical(g10)
    c: Equal(g0,g10) = 3
    c: Block(g10)
    c: Vertical(g11)
    c: Equal(g1,g11) = 3
    c: Block(g12)
    c: Block(g13)
    c: Block(g14)
    c: Block(g15)
    c: Block(g16)
    c: Block(g17)
    c: Block(g18)
    c: Block(g19)
    c: Block(g20)
    c: Block(g21)
    c: Block(g22)
    c: Block(g23)
    c: Block(g11)
    c: Block(g9)
    c: Block(g7)
    c: Block(g5)
    c: Block(g3)
    c: Block(g1)
    c: Coincident(g24,g0)
    c: Coincident(g24,g12)
    c: Horizontal(g24)
    c: Coincident(g25,g0)
    c: Coincident(g25,g12)
    c: Horizontal(g25)
    c: Coincident(g26,g1)
    c: Coincident(g26,g13)
    c: Horizontal(g26)
    c: Coincident(g27,g1)
    c: Coincident(g27,g13)
    c: Horizontal(g27)
    c: Coincident(g28,g2)
    c: Coincident(g28,g14)
    c: Horizontal(g28)
    c: Coincident(g29,g2)
    c: Coincident(g29,g14)
    c: Horizontal(g29)
    c: Coincident(g30,g3)
    c: Coincident(g30,g15)
    c: Horizontal(g30)
    c: Coincident(g31,g3)
    c: Coincident(g31,g15)
    c: Horizontal(g31)
    c: Coincident(g32,g4)
    c: Coincident(g32,g16)
    c: Horizontal(g32)
    c: Coincident(g33,g4)
    c: Coincident(g33,g16)
    c: Horizontal(g33)
    c: Coincident(g34,g5)
    c: Coincident(g34,g17)
    c: Horizontal(g34)
    c: Coincident(g35,g5)
    c: Coincident(g35,g17)
    c: Horizontal(g35)
    c: Coincident(g36,g6)
    c: Coincident(g36,g19)
    c: Horizontal(g36)
    c: Coincident(g37,g6)
    c: Coincident(g37,g19)
    c: Horizontal(g37)
    c: Coincident(g38,g7)
    c: Coincident(g38,g18)
    c: Horizontal(g38)
    c: Coincident(g39,g7)
    c: Coincident(g39,g18)
    c: Horizontal(g39)
    c: Coincident(g40,g8)
    c: Coincident(g40,g20)
    c: Horizontal(g40)
    c: Coincident(g41,g8)
    c: Coincident(g41,g20)
    c: Horizontal(g41)
    c: Coincident(g42,g9)
    c: Coincident(g42,g23)
    c: Horizontal(g42)
    c: Coincident(g43,g9)
    c: Coincident(g43,g23)
    c: Horizontal(g43)
    c: Coincident(g44,g10)
    c: Coincident(g44,g22)
    c: Horizontal(g44)
    c: Coincident(g45,g10)
    c: Coincident(g45,g22)
    c: Horizontal(g45)
    c: Coincident(g46,g11)
    c: Coincident(g46,g21)
    c: Horizontal(g46)
    c: Coincident(g47,g11)
    c: Coincident(g47,g21)
    c: Horizontal(g47)
FEATURE [Sketcher::SketchObject] Sketch031
  FullyConstrained = true
  Placement = pos=(117,19,0) rot=(0.57735,0.57735,0.57735;2.0944rad)
  sketch-geometry (24):
    g0: ArcOfCircle CenterX=-49.19 CenterY=67.75 CenterZ=0 NormalX=0 NormalY=0 NormalZ=1 AngleXU=0 Radius=1.5 StartAngle=1.5708 EndAngle=4.71239
    g1: ArcOfCircle CenterX=-49.19 CenterY=62 CenterZ=0 NormalX=0 NormalY=0 NormalZ=1 AngleXU=0 Radius=1.5 StartAngle=1.5708 EndAngle=4.71239
    g2: ArcOfCircle CenterX=-49.19 CenterY=56.25 CenterZ=0 NormalX=0 NormalY=0 NormalZ=1 AngleXU=0 Radius=1.5 StartAngle=1.5708 EndAngle=4.71239
    g3: ArcOfCircle CenterX=-49.19 CenterY=50.5 CenterZ=0 NormalX=0 NormalY=0 NormalZ=1 AngleXU=0 Radius=1.5 StartAngle=1.5708 EndAngle=4.71239
    g4: ArcOfCircle CenterX=-49.19 CenterY=44.75 CenterZ=0 NormalX=0 NormalY=0 NormalZ=1 AngleXU=0 Radius=1.5 StartAngle=1.5708 EndAngle=4.71239
    g5: ArcOfCircle CenterX=-49.19 CenterY=39 CenterZ=0 NormalX=0 NormalY=0 NormalZ=1 AngleXU=0 Radius=1.5 StartAngle=1.5708 EndAngle=4.71239
    g6: ArcOfCircle CenterX=-49.19 CenterY=33 CenterZ=0 NormalX=0 NormalY=0 NormalZ=1 AngleXU=0 Radius=1.5 StartAngle=1.5708 EndAngle=4.71239
    g7: ArcOfCircle CenterX=-49.19 CenterY=27.25 CenterZ=0 NormalX=0 NormalY=0 NormalZ=1 AngleXU=0 Radius=1.5 StartAngle=1.5708 EndAngle=4.71239
    g8: ArcOfCircle CenterX=-49.19 CenterY=21.5 CenterZ=0 NormalX=0 NormalY=0 NormalZ=1 AngleXU=0 Radius=1.5 StartAngle=1.5708 EndAngle=4.71239
    g9: ArcOfCircle CenterX=-49.19 CenterY=15.75 CenterZ=0 NormalX=0 NormalY=0 NormalZ=1 AngleXU=0 Radius=1.5 StartAngle=1.5708 EndAngle=4.71239
    g10: ArcOfCircle CenterX=-49.19 CenterY=10 CenterZ=0 NormalX=0 NormalY=0 NormalZ=1 AngleXU=0 Radius=1.5 StartAngle=1.5708 EndAngle=4.71239
    g11: ArcOfCircle CenterX=-49.19 CenterY=4.25 CenterZ=0 NormalX=0 NormalY=0 NormalZ=1 AngleXU=0 Radius=1.5 StartAngle=1.5708 EndAngle=4.71239
    g12: LineSegment StartX=-49.19 StartY=69.25 StartZ=0 EndX=-49.19 EndY=66.25 EndZ=0
    g13: LineSegment StartX=-49.19 StartY=63.5 StartZ=0 EndX=-49.19 EndY=60.5 EndZ=0
    g14: LineSegment StartX=-49.19 StartY=57.75 StartZ=0 EndX=-49.19 EndY=54.75 EndZ=0
    g15: LineSegment StartX=-49.19 StartY=52 StartZ=0 EndX=-49.19 EndY=49 EndZ=0
    g16: LineSegment StartX=-49.19 StartY=46.25 StartZ=0 EndX=-49.19 EndY=43.25 EndZ=0
    g17: LineSegment StartX=-49.19 StartY=40.5 StartZ=0 EndX=-49.19 EndY=37.5 EndZ=0
    g18: LineSegment StartX=-49.19 StartY=34.5 StartZ=0 EndX=-49.19 EndY=31.5 EndZ=0
    g19: LineSegment StartX=-49.19 StartY=28.75 StartZ=0 EndX=-49.19 EndY=25.75 EndZ=0
    g20: LineSegment StartX=-49.19 StartY=23 StartZ=0 EndX=-49.19 EndY=20 EndZ=0
    g21: LineSegment StartX=-49.19 StartY=17.25 StartZ=0 EndX=-49.19 EndY=14.25 EndZ=0
    g22: LineSegment StartX=-49.19 StartY=11.5 StartZ=0 EndX=-49.19 EndY=8.5 EndZ=0
    g23: LineSegment StartX=-49.19 StartY=5.75 StartZ=0 EndX=-49.19 EndY=2.75 EndZ=0
  constraints (48):
    c: Block(g0)
    c: Block(g1)
    c: Block(g2)
    c: Block(g3)
    c: Block(g4)
    c: Block(g5)
    c: Block(g6)
    c: Block(g7)
    c: Block(g8)
    c: Block(g9)
    c: Block(g10)
    c: Block(g11)
    c: Coincident(g12,g0)
    c: Coincident(g12,g0)
    c: Vertical(g12)
    c: Vertical(g13)
    c: Coincident(g13,g1)
    c: Vertical(g14)
    c: Coincident(g14,g2)
    c: Vertical(g15)
    c: Coincident(g15,g3)
    c: Vertical(g16)
    c: Coincident(g16,g4)
    c: Vertical(g17)
    c: Coincident(g17,g5)
    c: Vertical(g18)
    c: Coincident(g18,g6)
    c: Vertical(g19)
    c: Coincident(g19,g7)
    c: Vertical(g20)
    c: Coincident(g20,g8)
    c: Vertical(g21)
    c: Coincident(g21,g9)
    c: Vertical(g22)
    c: Coincident(g22,g10)
    c: Vertical(g23)
    c: Coincident(g23,g11)
    c: Block(g23)
    c: Block(g22)
    c: Block(g21)
    c: Block(g20)
    c: Block(g13)
    c: Block(g14)
    c: Block(g15)
    c: Block(g16)
    c: Block(g17)
    c: Block(g18)
    c: Block(g19)
FEATURE [Part::Extrusion] Extrude022
  Base = -> Sketch030
  Dir = (1,-2e-16,2e-16)
  DirMode = 2
  FaceMakerClass = Part::FaceMakerBullseye
  LengthFwd = 19
  LengthRev = 0
  Placement = pos=(-19,0,0) rot=(0,0,1;0rad)
  Solid = true
  Symmetric = false
FEATURE [Part::Fillet] Fillet022
  Base = -> Extrude022
  Edges = 24 edges r=1.49: [Edge6,Edge11,Edge18,Edge23,Edge30,Edge35,Edge42,Edge47,Edge54,Edge59,Edge66,Edge71,Edge78,Edge83,Edge90,Edge95,Edge102,Edge107,Edge114,Edge119,Edge126,Edge131,Edge138,Edge143]
FEATURE [Part::Cut] Cut020  label="top010"
  Base = -> Cut019
  Tool = -> Fillet022
FEATURE [Sketcher::SketchObject] Sketch032
  FullyConstrained = true
  Placement = pos=(117,19,0) rot=(0.57735,0.57735,0.57735;2.0944rad)
  sketch-geometry (48):
    g0: LineSegment StartX=-49.19 StartY=69.25 StartZ=0 EndX=-49.19 EndY=66.25 EndZ=0
    g1: LineSegment StartX=-49.19 StartY=63.5 StartZ=0 EndX=-49.19 EndY=60.5 EndZ=0
    g2: LineSegment StartX=-49.19 StartY=57.75 StartZ=0 EndX=-49.19 EndY=54.75 EndZ=0
    g3: LineSegment StartX=-49.19 StartY=52 StartZ=0 EndX=-49.19 EndY=49 EndZ=0
    g4: LineSegment StartX=-49.19 StartY=46.25 StartZ=0 EndX=-49.19 EndY=43.25 EndZ=0
    g5: LineSegment StartX=-49.19 StartY=40.5 StartZ=0 EndX=-49.19 EndY=37.5 EndZ=0
    g6: LineSegment StartX=-49.19 StartY=34.5 StartZ=0 EndX=-49.19 EndY=31.5 EndZ=0
    g7: LineSegment StartX=-49.19 StartY=28.75 StartZ=0 EndX=-49.19 EndY=25.75 EndZ=0
    g8: LineSegment StartX=-49.19 StartY=23 StartZ=0 EndX=-49.19 EndY=20 EndZ=0
    g9: LineSegment StartX=-49.19 StartY=17.25 StartZ=0 EndX=-49.19 EndY=14.25 EndZ=0
    g10: LineSegment StartX=-49.19 StartY=11.5 StartZ=0 EndX=-49.19 EndY=8.5 EndZ=0
    g11: LineSegment StartX=-49.19 StartY=5.75 StartZ=0 EndX=-49.19 EndY=2.75 EndZ=0
    g12: ArcOfCircle CenterX=-1.5 CenterY=67.75 CenterZ=0 NormalX=0 NormalY=0 NormalZ=1 AngleXU=0 Radius=1.5 StartAngle=4.71239 EndAngle=7.85398
    g13: ArcOfCircle CenterX=-1.5 CenterY=62 CenterZ=0 NormalX=0 NormalY=0 NormalZ=1 AngleXU=0 Radius=1.5 StartAngle=4.71239 EndAngle=7.85398
    g14: ArcOfCircle CenterX=-1.5 CenterY=56.25 CenterZ=0 NormalX=0 NormalY=0 NormalZ=1 AngleXU=0 Radius=1.5 StartAngle=4.71239 EndAngle=7.85398
    g15: ArcOfCircle CenterX=-11.49 CenterY=50.5 CenterZ=0 NormalX=0 NormalY=0 NormalZ=1 AngleXU=0 Radius=1.5 StartAngle=4.71239 EndAngle=7.85398
    g16: ArcOfCircle CenterX=-16.28 CenterY=44.75 CenterZ=0 NormalX=0 NormalY=0 NormalZ=1 AngleXU=0 Radius=1.5 StartAngle=4.71239 EndAngle=7.85398
    g17: ArcOfCircle CenterX=-18.2337 CenterY=39 CenterZ=0 NormalX=0 NormalY=0 NormalZ=1 AngleXU=0 Radius=1.5 StartAngle=4.71485 EndAngle=7.85398
    g18: ArcOfCircle CenterX=-16.2837 CenterY=27.25 CenterZ=0 NormalX=0 NormalY=0 NormalZ=1 AngleXU=0 Radius=1.5 StartAngle=4.71485 EndAngle=7.85398
    g19: ArcOfCircle CenterX=-18.2337 CenterY=33 CenterZ=0 NormalX=0 NormalY=0 NormalZ=1 AngleXU=0 Radius=1.5 StartAngle=4.71485 EndAngle=7.85398
    g20: ArcOfCircle CenterX=-11.49 CenterY=21.5 CenterZ=0 NormalX=0 NormalY=0 NormalZ=1 AngleXU=0 Radius=1.5 StartAngle=4.71239 EndAngle=7.85398
    g21: ArcOfCircle CenterX=-1.5 CenterY=4.25 CenterZ=0 NormalX=0 NormalY=0 NormalZ=1 AngleXU=0 Radius=1.5 StartAngle=4.71239 EndAngle=7.85398
    g22: ArcOfCircle CenterX=-1.5 CenterY=10 CenterZ=0 NormalX=0 NormalY=0 NormalZ=1 AngleXU=0 Radius=1.5 StartAngle=4.71239 EndAngle=7.85398
    g23: ArcOfCircle CenterX=-1.5 CenterY=15.75 CenterZ=0 NormalX=0 NormalY=0 NormalZ=1 AngleXU=0 Radius=1.5 StartAngle=4.71239 EndAngle=7.85398
    g24: LineSegment StartX=-49.19 StartY=69.25 StartZ=0 EndX=-1.5 EndY=69.25 EndZ=0
    g25: LineSegment StartX=-49.19 StartY=66.25 StartZ=0 EndX=-1.5 EndY=66.25 EndZ=0
    g26: LineSegment StartX=-49.19 StartY=63.5 StartZ=0 EndX=-1.5 EndY=63.5 EndZ=0
    g27: LineSegment StartX=-49.19 StartY=60.5 StartZ=0 EndX=-1.5 EndY=60.5 EndZ=0
    g28: LineSegment StartX=-49.19 StartY=57.75 StartZ=0 EndX=-1.5 EndY=57.75 EndZ=0
    g29: LineSegment StartX=-49.19 StartY=54.75 StartZ=0 EndX=-1.5 EndY=54.75 EndZ=0
    g30: LineSegment StartX=-49.19 StartY=52 StartZ=0 EndX=-11.49 EndY=52 EndZ=0
    g31: LineSegment StartX=-49.19 StartY=49 StartZ=0 EndX=-11.49 EndY=49 EndZ=0
    g32: LineSegment StartX=-49.19 StartY=46.25 StartZ=0 EndX=-16.28 EndY=46.25 EndZ=0
    g33: LineSegment StartX=-49.19 StartY=43.25 StartZ=0 EndX=-16.28 EndY=43.25 EndZ=0
    g34: LineSegment StartX=-49.19 StartY=40.5 StartZ=0 EndX=-18.2337 EndY=40.5 EndZ=0
    g35: LineSegment StartX=-49.19 StartY=37.5 StartZ=0 EndX=-18.23 EndY=37.5 EndZ=0
    g36: LineSegment StartX=-49.19 StartY=34.5 StartZ=0 EndX=-18.2337 EndY=34.5 EndZ=0
    g37: LineSegment StartX=-49.19 StartY=31.5 StartZ=0 EndX=-18.23 EndY=31.5 EndZ=0
    g38: LineSegment StartX=-49.19 StartY=28.75 StartZ=0 EndX=-16.2837 EndY=28.75 EndZ=0
    g39: LineSegment StartX=-49.19 StartY=25.75 StartZ=0 EndX=-16.28 EndY=25.75 EndZ=0
    g40: LineSegment StartX=-49.19 StartY=23 StartZ=0 EndX=-11.49 EndY=23 EndZ=0
    g41: LineSegment StartX=-49.19 StartY=20 StartZ=0 EndX=-11.49 EndY=20 EndZ=0
    g42: LineSegment StartX=-49.19 StartY=17.25 StartZ=0 EndX=-1.5 EndY=17.25 EndZ=0
    g43: LineSegment StartX=-49.19 StartY=14.25 StartZ=0 EndX=-1.5 EndY=14.25 EndZ=0
    g44: LineSegment StartX=-49.19 StartY=11.5 StartZ=0 EndX=-1.5 EndY=11.5 EndZ=0
    g45: LineSegment StartX=-49.19 StartY=8.5 StartZ=0 EndX=-1.5 EndY=8.5 EndZ=0
    g46: LineSegment StartX=-49.19 StartY=5.75 StartZ=0 EndX=-1.5 EndY=5.75 EndZ=0
    g47: LineSegment StartX=-49.19 StartY=2.75 StartZ=0 EndX=-1.5 EndY=2.75 EndZ=0
  constraints (120):
    c: Vertical(g0)
    c: Distance(g0) = 3
    c: Block(g0)
    c: Vertical(g1)
    c: Distance(g1) = 3
    c: Vertical(g2)
    c: Equal(g0,g2) = 3
    c: Block(g2)
    c: Vertical(g3)
    c: Equal(g1,g3) = 3
    c: Vertical(g4)
    c: Equal(g0,g4) = 3
    c: Block(g4)
    c: Vertical(g5)
    c: Equal(g1,g5) = 3
    c: Vertical(g6)
    c: Equal(g0,g6) = 3
    c: Block(g6)
    c: Vertical(g7)
    c: Equal(g1,g7) = 3
    c: Vertical(g8)
    c: Equal(g0,g8) = 3
    c: Block(g8)
    c: Vertical(g9)
    c: Equal(g1,g9) = 3
    c: Vertical(g10)
    c: Equal(g0,g10) = 3
    c: Block(g10)
    c: Vertical(g11)
    c: Equal(g1,g11) = 3
    c: Block(g12)
    c: Block(g13)
    c: Block(g14)
    c: Block(g15)
    c: Block(g16)
    c: Block(g17)
    c: Block(g18)
    c: Block(g19)
    c: Block(g20)
    c: Block(g21)
    c: Block(g22)
    c: Block(g23)
    c: Block(g11)
    c: Block(g9)
    c: Block(g7)
    c: Block(g5)
    c: Block(g3)
    c: Block(g1)
    c: Coincident(g24,g0)
    c: Coincident(g24,g12)
    c: Horizontal(g24)
    c: Coincident(g25,g0)
    c: Coincident(g25,g12)
    c: Horizontal(g25)
    c: Coincident(g26,g1)
    c: Coincident(g26,g13)
    c: Horizontal(g26)
    c: Coincident(g27,g1)
    c: Coincident(g27,g13)
    c: Horizontal(g27)
    c: Coincident(g28,g2)
    c: Coincident(g28,g14)
    c: Horizontal(g28)
    c: Coincident(g29,g2)
    c: Coincident(g29,g14)
    c: Horizontal(g29)
    c: Coincident(g30,g3)
    c: Coincident(g30,g15)
    c: Horizontal(g30)
    c: Coincident(g31,g3)
    c: Coincident(g31,g15)
    c: Horizontal(g31)
    c: Coincident(g32,g4)
    c: Coincident(g32,g16)
    c: Horizontal(g32)
    c: Coincident(g33,g4)
    c: Coincident(g33,g16)
    c: Horizontal(g33)
    c: Coincident(g34,g5)
    c: Coincident(g34,g17)
    c: Horizontal(g34)
    c: Coincident(g35,g5)
    c: Coincident(g35,g17)
    c: Horizontal(g35)
    c: Coincident(g36,g6)
    c: Coincident(g36,g19)
    c: Horizontal(g36)
    c: Coincident(g37,g6)
    c: Coincident(g37,g19)
    c: Horizontal(g37)
    c: Coincident(g38,g7)
    c: Coincident(g38,g18)
    c: Horizontal(g38)
    c: Coincident(g39,g7)
    c: Coincident(g39,g18)
    c: Horizontal(g39)
    c: Coincident(g40,g8)
    c: Coincident(g40,g20)
    c: Horizontal(g40)
    c: Coincident(g41,g8)
    c: Coincident(g41,g20)
    c: Horizontal(g41)
    c: Coincident(g42,g9)
    c: Coincident(g42,g23)
    c: Horizontal(g42)
    c: Coincident(g43,g9)
    c: Coincident(g43,g23)
    c: Horizontal(g43)
    c: Coincident(g44,g10)
    c: Coincident(g44,g22)
    c: Horizontal(g44)
    c: Coincident(g45,g10)
    c: Coincident(g45,g22)
    c: Horizontal(g45)
    c: Coincident(g46,g11)
    c: Coincident(g46,g21)
    c: Horizontal(g46)
    c: Coincident(g47,g11)
    c: Coincident(g47,g21)
    c: Horizontal(g47)
FEATURE [Part::Extrusion] Extrude023
  Base = -> Sketch032
  Dir = (1,-2e-16,2e-16)
  DirMode = 2
  FaceMakerClass = Part::FaceMakerBullseye
  LengthFwd = 19
  LengthRev = 0
  Placement = pos=(-19,0,0) rot=(0,0,1;0rad)
  Solid = true
  Symmetric = false
FEATURE [Part::Fillet] Fillet023
  Base = -> Extrude023
  Edges = <same value as first occurrence — deduplicated (x6 in doc)>
  Placement = pos=(0,0.05,0) rot=(0,0,1;0rad)
FEATURE [Part::Cut] Cut014  label="bottom003"
  Base = -> Cut007
  Tool = -> Fusion047
FEATURE [Part::Cut] Cut021  label="bottom004"
  Base = -> Cut014
  Tool = -> Fillet023
FEATURE [Sketcher::SketchObject] Sketch033
  FullyConstrained = true
  Placement = pos=(117,19,0) rot=(0.57735,0.57735,0.57735;2.0944rad)
  sketch-geometry (8):
    g0: LineSegment StartX=-49.19 StartY=69.25 StartZ=0 EndX=-49.19 EndY=66.25 EndZ=0
    g1: LineSegment StartX=-49.19 StartY=5.75 StartZ=0 EndX=-49.19 EndY=2.75 EndZ=0
    g2: ArcOfCircle CenterX=-1.5 CenterY=67.75 CenterZ=0 NormalX=0 NormalY=0 NormalZ=1 AngleXU=0 Radius=1.5 StartAngle=4.71239 EndAngle=7.85398
    g3: ArcOfCircle CenterX=-1.5 CenterY=4.25 CenterZ=0 NormalX=0 NormalY=0 NormalZ=1 AngleXU=0 Radius=1.5 StartAngle=4.71239 EndAngle=7.85398
    g4: LineSegment StartX=-49.19 StartY=69.25 StartZ=0 EndX=-1.5 EndY=69.25 EndZ=0
    g5: LineSegment StartX=-49.19 StartY=66.25 StartZ=0 EndX=-1.5 EndY=66.25 EndZ=0
    g6: LineSegment StartX=-49.19 StartY=5.75 StartZ=0 EndX=-1.5 EndY=5.75 EndZ=0
    g7: LineSegment StartX=-49.19 StartY=2.75 StartZ=0 EndX=-1.5 EndY=2.75 EndZ=0
  constraints (19):
    c: Vertical(g0)
    c: Distance(g0) = 3
    c: Block(g0)
    c: Vertical(g1)
    c: Block(g2)
    c: Block(g3)
    c: Block(g1)
    c: Coincident(g4,g0)
    c: Coincident(g4,g2)
    c: Horizontal(g4)
    c: Coincident(g5,g0)
    c: Coincident(g5,g2)
    c: Horizontal(g5)
    c: Coincident(g6,g1)
    c: Coincident(g6,g3)
    c: Horizontal(g6)
    c: Coincident(g7,g1)
    c: Coincident(g7,g3)
    c: Horizontal(g7)
FEATURE [Sketcher::SketchObject] Sketch034
  FullyConstrained = true
  Placement = pos=(117,19,0) rot=(0.57735,0.57735,0.57735;2.0944rad)
  sketch-geometry (8):
    g0: LineSegment StartX=-49.19 StartY=63.5 StartZ=0 EndX=-49.19 EndY=60.5 EndZ=0
    g1: LineSegment StartX=-49.19 StartY=11.5 StartZ=0 EndX=-49.19 EndY=8.5 EndZ=0
    g2: ArcOfCircle CenterX=-1.5 CenterY=62 CenterZ=0 NormalX=0 NormalY=0 NormalZ=1 AngleXU=0 Radius=1.5 StartAngle=4.71239 EndAngle=7.85398
    g3: ArcOfCircle CenterX=-1.5 CenterY=10 CenterZ=0 NormalX=0 NormalY=0 NormalZ=1 AngleXU=0 Radius=1.5 StartAngle=4.71239 EndAngle=7.85398
    g4: LineSegment StartX=-49.19 StartY=63.5 StartZ=0 EndX=-1.5 EndY=63.5 EndZ=0
    g5: LineSegment StartX=-49.19 StartY=60.5 StartZ=0 EndX=-1.5 EndY=60.5 EndZ=0
    g6: LineSegment StartX=-49.19 StartY=11.5 StartZ=0 EndX=-1.5 EndY=11.5 EndZ=0
    g7: LineSegment StartX=-49.19 StartY=8.5 StartZ=0 EndX=-1.5 EndY=8.5 EndZ=0
  constraints (19):
    c: Vertical(g0)
    c: Distance(g0) = 3
    c: Vertical(g1)
    c: Block(g1)
    c: Block(g2)
    c: Block(g3)
    c: Block(g0)
    c: Coincident(g4,g0)
    c: Coincident(g4,g2)
    c: Horizontal(g4)
    c: Coincident(g5,g0)
    c: Coincident(g5,g2)
    c: Horizontal(g5)
    c: Coincident(g6,g1)
    c: Coincident(g6,g3)
    c: Horizontal(g6)
    c: Coincident(g7,g1)
    c: Coincident(g7,g3)
    c: Horizontal(g7)
FEATURE [Part::Extrusion] Extrude024
  Base = -> Sketch033
  Dir = (1,0,0)
  DirMode = 2
  FaceMakerClass = Part::FaceMakerBullseye
  LengthFwd = 10
  LengthRev = 0
  Solid = true
  Symmetric = false
FEATURE [Part::Extrusion] Extrude025
  Base = -> Sketch034
  Dir = (1,0,0)
  DirMode = 2
  FaceMakerClass = Part::FaceMakerBullseye
  LengthFwd = 10
  LengthRev = 0
  Solid = true
  Symmetric = false
FEATURE [Part::Fillet] Fillet024  label="removeFromtMoreFrontCaseScrewRetainers"
  Base = -> Extrude024
  Edges = 4 edges r=1.49: [Edge6,Edge11,Edge18,Edge23]
  Placement = pos=(-11,0,0) rot=(0,0,1;0rad)
FEATURE [Part::Fillet] Fillet025  label="removeFromtMoreFrontCaseScrewRetainers001"
  Base = -> Extrude025
  Edges = 4 edges r=1.49: [Edge6,Edge11,Edge18,Edge23]
  Placement = pos=(-19,0,0) rot=(0,0,1;0rad)
FEATURE [Part::Cut] Cut022
  Base = -> Cut015
  Tool = -> Fillet025
FEATURE [Part::Cut] Cut023  label="screwRetainers"
  Base = -> Cut022
  Tool = -> Fillet024
FEATURE [Part::MultiFuse] Fusion056  label="bottom005"
  Shapes = -> [Fusion044,Cut021]
FEATURE [Part::MultiFuse] Fusion057  label="casePillars001"
  Shapes = -> [Cut016,Fusion052]
FEATURE [Part::MultiFuse] Fusion058  label="bottom006"
  Shapes = -> [Fusion056,Cut023]
FEATURE [Part::MultiFuse] Fusion059  label="bottom007"
  Shapes = -> [Fusion058,Fillet005]
FEATURE [Part::MultiFuse] Fusion060  label="bottom008"
  Shapes = -> [Fusion059,Fusion]
FEATURE [Part::MultiFuse] Fusion061  label="top011"
  Shapes = -> [Cut006,Cut020]
FEATURE [Part::MultiFuse] Fusion062  label="top012"
  Shapes = -> [Fusion057,Fusion061]
FEATURE [Sketcher::SketchObject] Sketch035  label="topSketch007"
  FullyConstrained = true
  sketch-geometry (6):
    g0: LineSegment StartX=19 StartY=38 StartZ=0 EndX=117 EndY=38 EndZ=0
    g1: ArcOfCircle CenterX=19 CenterY=19 CenterZ=0 NormalX=0 NormalY=0 NormalZ=1 AngleXU=0 Radius=19 StartAngle=1.5708 EndAngle=3.14159
    g2: LineSegment StartX=117 StartY=38 StartZ=0 EndX=117 EndY=19 EndZ=0
    g3: LineSegment StartX=98 StartY=1.0161e-12 StartZ=0 EndX=5.22862e-06 EndY=1.0161e-12 EndZ=0
    g4: LineSegment StartX=5.22862e-06 StartY=19 StartZ=0 EndX=5.22862e-06 EndY=1.0161e-12 EndZ=0
    g5: ArcOfCircle CenterX=98 CenterY=19 CenterZ=0 NormalX=0 NormalY=0 NormalZ=1 AngleXU=0 Radius=19 StartAngle=4.71239 EndAngle=6.28319
  constraints (16):
    c: Horizontal(g0)
    c: Distance(g0) = 98
    c: Coincident(g1,g0)
    c: Block(g1)
    c: Coincident(g2,g0)
    c: Vertical(g2)
    c: Distance(g2) = 19
    c: Horizontal(g3)
    c: Coincident(g4,g1)
    c: Vertical(g4)
    c: Coincident(g3,g4)
    c: Block(g3)
    c: Coincident(g5,g2)
    c: Coincident(g5,g3)
    c: Block(g0)
    c: Block(g5)
FEATURE [Part::Extrusion] Extrude026  label="sideA001"
  Base = -> Sketch035
  Dir = (0,0,1)
  DirMode = 2
  FaceMakerClass = Part::FaceMakerBullseye
  LengthFwd = 3
  LengthRev = 0
  Placement = pos=(0,0,-2.7) rot=(0,0,1;0rad)
  Solid = true
  Symmetric = false
FEATURE [Sketcher::SketchObject] Sketch036  label="topSketch008"
  FullyConstrained = true
  sketch-geometry (6):
    g0: LineSegment StartX=19 StartY=38 StartZ=0 EndX=117 EndY=38 EndZ=0
    g1: ArcOfCircle CenterX=19 CenterY=19 CenterZ=0 NormalX=0 NormalY=0 NormalZ=1 AngleXU=0 Radius=19 StartAngle=1.5708 EndAngle=3.14159
    g2: LineSegment StartX=117 StartY=38 StartZ=0 EndX=117 EndY=19 EndZ=0
    g3: LineSegment StartX=98 StartY=1.0161e-12 StartZ=0 EndX=5.22862e-06 EndY=1.0161e-12 EndZ=0
    g4: LineSegment StartX=5.22862e-06 StartY=19 StartZ=0 EndX=5.22862e-06 EndY=1.0161e-12 EndZ=0
    g5: ArcOfCircle CenterX=98 CenterY=19 CenterZ=0 NormalX=0 NormalY=0 NormalZ=1 AngleXU=0 Radius=19 StartAngle=4.71239 EndAngle=6.28319
  constraints (16):
    c: Horizontal(g0)
    c: Distance(g0) = 98
    c: Coincident(g1,g0)
    c: Block(g1)
    c: Coincident(g2,g0)
    c: Vertical(g2)
    c: Distance(g2) = 19
    c: Horizontal(g3)
    c: Coincident(g4,g1)
    c: Vertical(g4)
    c: Coincident(g3,g4)
    c: Block(g3)
    c: Coincident(g5,g2)
    c: Coincident(g5,g3)
    c: Block(g0)
    c: Block(g5)
FEATURE [Part::Extrusion] Extrude027  label="sideB001"
  Base = -> Sketch036
  Dir = (0,0,1)
  DirMode = 2
  FaceMakerClass = Part::FaceMakerBullseye
  LengthFwd = 3
  LengthRev = 0
  Placement = pos=(0,0,71.7) rot=(0,0,1;0rad)
  Solid = true
  Symmetric = false
FEATURE [Part::MultiFuse] Fusion064  label="removeFromBottom"
  Shapes = -> [Extrude026,Extrude027]
FEATURE [Part::Cut] Cut024  label="bottom009"
  Base = -> Fusion060
  Tool = -> Fusion064
FEATURE [Sketcher::SketchObject] Sketch037  label="topSketch009"
  FullyConstrained = true
  sketch-geometry (8):
    g0: ArcOfCircle CenterX=19 CenterY=19.1201 CenterZ=0 NormalX=0 NormalY=0 NormalZ=1 AngleXU=0 Radius=18.8799 StartAngle=1.5708 EndAngle=3.14793
    g1: LineSegment StartX=0.120501 StartY=19.0004 StartZ=0 EndX=0.120501 EndY=0.000382114 EndZ=0
    g2: LineSegment StartX=19 StartY=38 StartZ=0 EndX=124 EndY=38 EndZ=0
    g3: LineSegment StartX=0.120501 StartY=0.000382114 StartZ=0 EndX=105.121 EndY=0.000382114 EndZ=0
    g4: LineSegment StartX=124 StartY=38 StartZ=0 EndX=125.616 EndY=38 EndZ=0
    g5: LineSegment StartX=105.121 StartY=0.000382114 StartZ=0 EndX=106.736 EndY=0.000382114 EndZ=0
    g6: ArcOfCircle CenterX=106.616 CenterY=19 CenterZ=0 NormalX=0 NormalY=0 NormalZ=1 AngleXU=0 Radius=19 StartAngle=4.71873 EndAngle=6.28319
    g7: LineSegment StartX=125.616 StartY=38 StartZ=0 EndX=125.616 EndY=19 EndZ=0
  constraints (21):
    c: Block(g0)
    c: Coincident(g1,g0)
    c: Vertical(g1)
    c: Horizontal(g2)
    c: Distance(g2) = 105
    c: Coincident(g2,g0)
    c: Distance(g1) = 19
    c: Coincident(g3,g1)
    c: Horizontal(g3)
    c: Distance(g3) = 105
    c: Coincident(g4,g2)
    c: Horizontal(g4)
    c: Distance(g4) = 1.61553
    c: Horizontal(g5)
    c: Equal(g4,g5) = 1.61553
    c: Coincident(g5,g3)
    c: Block(g6)
    c: Coincident(g6,g5)
    c: Coincident(g7,g4)
    c: Coincident(g7,g6)
    c: Vertical(g7)
FEATURE [Part::Extrusion] Extrude028  label="sideB"
  Base = -> Sketch037
  Dir = (0,0,1)
  DirMode = 2
  FaceMakerClass = Part::FaceMakerBullseye
  LengthFwd = 3
  LengthRev = 0
  Placement = pos=(0,0,72) rot=(0,0,1;0rad)
  Solid = true
  Symmetric = false
FEATURE [Sketcher::SketchObject] Sketch038  label="topSketch010"
  FullyConstrained = true
  sketch-geometry (22):
    g0: LineSegment StartX=5.21097e-06 StartY=3 StartZ=0 EndX=5.21097e-06 EndY=19 EndZ=0
    g1: ArcOfCircle CenterX=19 CenterY=19 CenterZ=0 NormalX=0 NormalY=0 NormalZ=1 AngleXU=0 Radius=19 StartAngle=1.5708 EndAngle=3.14159
    g2: ArcOfCircle CenterX=19 CenterY=19 CenterZ=0 NormalX=0 NormalY=0 NormalZ=1 AngleXU=0 Radius=16 StartAngle=1.5708 EndAngle=3.14159
    g3: LineSegment StartX=114 StartY=35 StartZ=0 EndX=19 EndY=35 EndZ=0
    g4: LineSegment StartX=5.21097e-06 StartY=3 StartZ=0 EndX=5.21097e-06 EndY=0 EndZ=0
    g5: LineSegment StartX=3 StartY=0 StartZ=0 EndX=5.21097e-06 EndY=0 EndZ=0
    g6: LineSegment StartX=3 StartY=19 StartZ=0 EndX=3 EndY=0 EndZ=0
    g7: LineSegment StartX=19 StartY=38 StartZ=0 EndX=124 EndY=38 EndZ=0
    g8: Circle CenterX=119 CenterY=35 CenterZ=0 NormalX=0 NormalY=0 NormalZ=1 AngleXU=0 Radius=1
    g9: Circle CenterX=121 CenterY=35 CenterZ=0 NormalX=0 NormalY=0 NormalZ=1 AngleXU=0 Radius=1
    g10: Circle CenterX=121 CenterY=33 CenterZ=0 NormalX=0 NormalY=0 NormalZ=1 AngleXU=0 Radius=1
    g11: BSplineCurve PolesCount=3 KnotsCount=2 Degree=2 IsPeriodic=0
    g12: GeomPoint X=119 Y=35 Z=0
    g13: GeomPoint X=121 Y=33 Z=0
    g14: LineSegment StartX=119 StartY=35 StartZ=0 EndX=114 EndY=35 EndZ=0
    g15: ArcOfCircle CenterX=105 CenterY=19 CenterZ=0 NormalX=0 NormalY=0 NormalZ=1 AngleXU=0 Radius=16 StartAngle=5.60905 EndAngle=6.28319
    g16: LineSegment StartX=121 StartY=33 StartZ=0 EndX=121 EndY=19 EndZ=0
    g17: LineSegment StartX=117.5 StartY=9.01251 StartZ=0 EndX=121.163 EndY=9.0125 EndZ=0
    g18: ArcOfCircle CenterX=105 CenterY=19 CenterZ=0 NormalX=0 NormalY=0 NormalZ=1 AngleXU=0 Radius=20.6155 StartAngle=5.7297 EndAngle=6.28319
    g19: LineSegment StartX=121.163 StartY=9.0125 StartZ=0 EndX=122.538 EndY=8.16329 EndZ=0
    g20: LineSegment StartX=124 StartY=38 StartZ=0 EndX=125.616 EndY=38 EndZ=0
    g21: LineSegment StartX=125.616 StartY=19 StartZ=0 EndX=125.616 EndY=38 EndZ=0
  constraints (49):
    c: Vertical(g0)
    c: Block(g0)
    c: Coincident(g1,g0)
    c: Block(g1)
    c: Coincident(g2,g1)
    c: Block(g2)
    c: Coincident(g3,g2)
    c: Horizontal(g3)
    c: Tangent(g3,g2)
    c: Coincident(g4,g0)
    c: Distance(g4) = 3
    c: Vertical(g4)
    c: Coincident(g5,g4)
    c: Horizontal(g5)
    c: Coincident(g6,g2)
    c: Coincident(g6,g5)
    c: Vertical(g6)
    c: Horizontal(g7)
    c: Distance(g7) = 105
    c: Coincident(g7,g1)
    c: Block(g3)
    c: Weight(g8) = 1
    c: Equal(g8,g9)
    c: Equal(g8,g10)
    c: InternalAlignment(g8,g11)
    c: InternalAlignment(g9,g11)
    c: InternalAlignment(g10,g11)
    c: InternalAlignment(g12,g11)
    c: InternalAlignment(g13,g11)
    c: Block(g11)
    c: Coincident(g14,g11)
    c: Coincident(g14,g3)
    c: Horizontal(g14)
    c: Block(g15)
    c: Coincident(g16,g11)
    c: Coincident(g16,g15)
    c: Vertical(g16)
    c: Distance(g16) = 14
    c: Coincident(g17,g15)
    c: Block(g18)
    c: Coincident(g19,g18)
    c: Coincident(g20,g7)
    c: Horizontal(g20)
    c: Vertical(g21)
    c: Coincident(g20,g21)
    c: Block(g20)
    c: Block(g21)
    c: Block(g19)
    c: Block(g17)
FEATURE [Part::Extrusion] Extrude029
  Base = -> Sketch038
  Dir = (0,0,1)
  DirMode = 2
  FaceMakerClass = Part::FaceMakerBullseye
  LengthFwd = 72
  LengthRev = 0
  Solid = true
  Symmetric = false
FEATURE [Part::Feature] Face085
  shape: bbox 4.8 x 25.5 x 2e-07 mm, 1 faces, 0 solids (baked)
FEATURE [Part::Revolution] Revolve089  label="moreFrontCaseScrewPost003"
  Angle = 360
  Axis = (0,1,0)
  Base = (0,0,0)
  FaceMakerClass = Part::FaceMakerBullseye
  Placement = pos=(109.5,4.5,3.5) rot=(0,0,1;0rad)
  Solid = false
  Source = -> Face085
  Symmetric = false
FEATURE [Part::Feature] Face086
  shape: bbox 4.8 x 25.5 x 2e-07 mm, 1 faces, 0 solids (baked)
FEATURE [Part::Revolution] Revolve090  label="moreFrontCaseScrewPost004"
  Angle = 360
  Axis = (0,1,0)
  Base = (0,0,0)
  FaceMakerClass = Part::FaceMakerBullseye
  Placement = pos=(109.5,4.5,68.5) rot=(0,0,1;0rad)
  Solid = false
  Source = -> Face086
  Symmetric = false
FEATURE [Part::Fillet] Fillet026  label="top013"
  Base = -> Extrude029
  Edges = 1 edges r=2: [Edge35]
FEATURE [Sketcher::SketchObject] Sketch039
  FullyConstrained = true
  sketch-geometry (7):
    g0: LineSegment StartX=0 StartY=0 StartZ=0 EndX=0 EndY=6 EndZ=0
    g1: Circle CenterX=0 CenterY=0 CenterZ=0 NormalX=0 NormalY=0 NormalZ=1 AngleXU=0 Radius=1
    g2: Circle CenterX=8 CenterY=6 CenterZ=0 NormalX=0 NormalY=0 NormalZ=1 AngleXU=0 Radius=1
    g3: BSplineCurve PolesCount=3 KnotsCount=2 Degree=2 IsPeriodic=0
    g4: GeomPoint X=0 Y=0 Z=0
    g5: GeomPoint X=8 Y=6 Z=0
    g6: LineSegment StartX=0 StartY=6 StartZ=0 EndX=8 EndY=6 EndZ=0
  constraints (14):
    c: Coincident(g0,g-1)
    c: Distance(g0) = 6
    c: Vertical(g0)
    c: Coincident(g3,g0)
    c: Weight(g1) = 1
    c: Equal(g1,g2)
    c: InternalAlignment(g1,g3)
    c: InternalAlignment(g2,g3)
    c: InternalAlignment(g4,g3)
    c: InternalAlignment(g5,g3)
    c: Block(g3)
    c: Coincident(g6,g0)
    c: Coincident(g6,g3)
    c: Horizontal(g6)
FEATURE [Sketcher::SketchObject] Sketch040
  FullyConstrained = true
  sketch-geometry (7):
    g0: LineSegment StartX=0 StartY=0 StartZ=0 EndX=0 EndY=6 EndZ=0
    g1: Circle CenterX=0 CenterY=0 CenterZ=0 NormalX=0 NormalY=0 NormalZ=1 AngleXU=0 Radius=1
    g2: Circle CenterX=8 CenterY=6 CenterZ=0 NormalX=0 NormalY=0 NormalZ=1 AngleXU=0 Radius=1
    g3: BSplineCurve PolesCount=3 KnotsCount=2 Degree=2 IsPeriodic=0
    g4: GeomPoint X=0 Y=0 Z=0
    g5: GeomPoint X=8 Y=6 Z=0
    g6: LineSegment StartX=0 StartY=6 StartZ=0 EndX=8 EndY=6 EndZ=0
  constraints (14):
    c: Coincident(g0,g-1)
    c: Distance(g0) = 6
    c: Vertical(g0)
    c: Coincident(g3,g0)
    c: Weight(g1) = 1
    c: Equal(g1,g2)
    c: InternalAlignment(g1,g3)
    c: InternalAlignment(g2,g3)
    c: InternalAlignment(g4,g3)
    c: InternalAlignment(g5,g3)
    c: Block(g3)
    c: Coincident(g6,g0)
    c: Coincident(g6,g3)
    c: Horizontal(g6)
FEATURE [Sketcher::SketchObject] Sketch041
  FullyConstrained = true
  sketch-geometry (7):
    g0: LineSegment StartX=0 StartY=0 StartZ=0 EndX=0 EndY=6 EndZ=0
    g1: Circle CenterX=0 CenterY=0 CenterZ=0 NormalX=0 NormalY=0 NormalZ=1 AngleXU=0 Radius=1
    g2: Circle CenterX=8 CenterY=6 CenterZ=0 NormalX=0 NormalY=0 NormalZ=1 AngleXU=0 Radius=1
    g3: BSplineCurve PolesCount=3 KnotsCount=2 Degree=2 IsPeriodic=0
    g4: GeomPoint X=0 Y=0 Z=0
    g5: GeomPoint X=8 Y=6 Z=0
    g6: LineSegment StartX=0 StartY=6 StartZ=0 EndX=8 EndY=6 EndZ=0
  constraints (14):
    c: Coincident(g0,g-1)
    c: Distance(g0) = 6
    c: Vertical(g0)
    c: Coincident(g3,g0)
    c: Weight(g1) = 1
    c: Equal(g1,g2)
    c: InternalAlignment(g1,g3)
    c: InternalAlignment(g2,g3)
    c: InternalAlignment(g4,g3)
    c: InternalAlignment(g5,g3)
    c: Block(g3)
    c: Coincident(g6,g0)
    c: Coincident(g6,g3)
    c: Horizontal(g6)
FEATURE [Sketcher::SketchObject] Sketch042
  FullyConstrained = true
  sketch-geometry (7):
    g0: LineSegment StartX=0 StartY=0 StartZ=0 EndX=0 EndY=6 EndZ=0
    g1: Circle CenterX=0 CenterY=0 CenterZ=0 NormalX=0 NormalY=0 NormalZ=1 AngleXU=0 Radius=1
    g2: Circle CenterX=8 CenterY=6 CenterZ=0 NormalX=0 NormalY=0 NormalZ=1 AngleXU=0 Radius=1
    g3: BSplineCurve PolesCount=3 KnotsCount=2 Degree=2 IsPeriodic=0
    g4: GeomPoint X=0 Y=0 Z=0
    g5: GeomPoint X=8 Y=6 Z=0
    g6: LineSegment StartX=0 StartY=6 StartZ=0 EndX=8 EndY=6 EndZ=0
  constraints (14):
    c: Coincident(g0,g-1)
    c: Distance(g0) = 6
    c: Vertical(g0)
    c: Coincident(g3,g0)
    c: Weight(g1) = 1
    c: Equal(g1,g2)
    c: InternalAlignment(g1,g3)
    c: InternalAlignment(g2,g3)
    c: InternalAlignment(g4,g3)
    c: InternalAlignment(g5,g3)
    c: Block(g3)
    c: Coincident(g6,g0)
    c: Coincident(g6,g3)
    c: Horizontal(g6)
FEATURE [Part::Extrusion] Extrude030  label="caseScrewPillarBracket008"
  Base = -> Sketch039
  Dir = (0,0,1)
  DirMode = 2
  FaceMakerClass = Part::FaceMakerBullseye
  LengthFwd = 2.4
  LengthRev = 0
  Placement = pos=(15.76,29,8.8) rot=(0,1,0;0rad)
  Solid = true
  Symmetric = false
FEATURE [Part::Extrusion] Extrude031  label="caseScrewPillarBracket009"
  Base = -> Sketch040
  Dir = (0,0,1)
  DirMode = 2
  FaceMakerClass = Part::FaceMakerBullseye
  LengthFwd = 2.4
  LengthRev = 0
  Placement = pos=(15.76,29,60.8) rot=(0,0,1;0rad)
  Solid = true
  Symmetric = false
FEATURE [Part::Extrusion] Extrude032  label="caseScrewPillarBracket010"
  Base = -> Sketch041
  Dir = (0,0,1)
  DirMode = 2
  FaceMakerClass = Part::FaceMakerBullseye
  LengthFwd = 2.4
  LengthRev = 0
  Placement = pos=(13.7,29,13.26) rot=(0,-1,0;1.5708rad)
  Solid = true
  Symmetric = false
FEATURE [Part::Extrusion] Extrude033  label="caseScrewPillarBracket011"
  Base = -> Sketch042
  Dir = (0,0,1)
  DirMode = 2
  FaceMakerClass = Part::FaceMakerBullseye
  LengthFwd = 2.4
  LengthRev = 0
  Placement = pos=(11.3,29,58.74) rot=(0,1,0;1.5708rad)
  Solid = true
  Symmetric = false
FEATURE [Sketcher::SketchObject] Sketch043
  FullyConstrained = true
  sketch-geometry (7):
    g0: LineSegment StartX=0 StartY=0 StartZ=0 EndX=0 EndY=6 EndZ=0
    g1: Circle CenterX=0 CenterY=0 CenterZ=0 NormalX=0 NormalY=0 NormalZ=1 AngleXU=0 Radius=1
    g2: Circle CenterX=8 CenterY=6 CenterZ=0 NormalX=0 NormalY=0 NormalZ=1 AngleXU=0 Radius=1
    g3: BSplineCurve PolesCount=3 KnotsCount=2 Degree=2 IsPeriodic=0
    g4: GeomPoint X=0 Y=0 Z=0
    g5: GeomPoint X=8 Y=6 Z=0
    g6: LineSegment StartX=0 StartY=6 StartZ=0 EndX=8 EndY=6 EndZ=0
  constraints (14):
    c: Coincident(g0,g-1)
    c: Distance(g0) = 6
    c: Vertical(g0)
    c: Coincident(g3,g0)
    c: Weight(g1) = 1
    c: Equal(g1,g2)
    c: InternalAlignment(g1,g3)
    c: InternalAlignment(g2,g3)
    c: InternalAlignment(g4,g3)
    c: InternalAlignment(g5,g3)
    c: Block(g3)
    c: Coincident(g6,g0)
    c: Coincident(g6,g3)
    c: Horizontal(g6)
FEATURE [Part::Extrusion] Extrude034  label="caseScrewPillarBracket012"
  Base = -> Sketch043
  Dir = (0,0,1)
  DirMode = 2
  FaceMakerClass = Part::FaceMakerBullseye
  LengthFwd = 2.4
  LengthRev = 0
  Placement = pos=(88.3,29,65.23) rot=(0,1,0;1.5708rad)
  Solid = true
  Symmetric = false
FEATURE [Sketcher::SketchObject] Sketch044
  FullyConstrained = true
  sketch-geometry (7):
    g0: LineSegment StartX=0 StartY=0 StartZ=0 EndX=0 EndY=6 EndZ=0
    g1: Circle CenterX=0 CenterY=0 CenterZ=0 NormalX=0 NormalY=0 NormalZ=1 AngleXU=0 Radius=1
    g2: Circle CenterX=8 CenterY=6 CenterZ=0 NormalX=0 NormalY=0 NormalZ=1 AngleXU=0 Radius=1
    g3: BSplineCurve PolesCount=3 KnotsCount=2 Degree=2 IsPeriodic=0
    g4: GeomPoint X=0 Y=0 Z=0
    g5: GeomPoint X=8 Y=6 Z=0
    g6: LineSegment StartX=0 StartY=6 StartZ=0 EndX=8 EndY=6 EndZ=0
  constraints (14):
    c: Coincident(g0,g-1)
    c: Distance(g0) = 6
    c: Vertical(g0)
    c: Coincident(g3,g0)
    c: Weight(g1) = 1
    c: Equal(g1,g2)
    c: InternalAlignment(g1,g3)
    c: InternalAlignment(g2,g3)
    c: InternalAlignment(g4,g3)
    c: InternalAlignment(g5,g3)
    c: Block(g3)
    c: Coincident(g6,g0)
    c: Coincident(g6,g3)
    c: Horizontal(g6)
FEATURE [Part::Extrusion] Extrude035  label="caseScrewPillarBracket013"
  Base = -> Sketch044
  Dir = (0,0,1)
  DirMode = 2
  FaceMakerClass = Part::FaceMakerBullseye
  LengthFwd = 2.4
  LengthRev = 0
  Placement = pos=(90.7,29,6.77) rot=(0,-1,0;1.5708rad)
  Solid = true
  Symmetric = false
FEATURE [Sketcher::SketchObject] Sketch045
  FullyConstrained = true
  sketch-geometry (7):
    g0: LineSegment StartX=0 StartY=0 StartZ=0 EndX=0 EndY=6 EndZ=0
    g1: Circle CenterX=0 CenterY=0 CenterZ=0 NormalX=0 NormalY=0 NormalZ=1 AngleXU=0 Radius=1
    g2: Circle CenterX=8 CenterY=6 CenterZ=0 NormalX=0 NormalY=0 NormalZ=1 AngleXU=0 Radius=1
    g3: BSplineCurve PolesCount=3 KnotsCount=2 Degree=2 IsPeriodic=0
    g4: GeomPoint X=0 Y=0 Z=0
    g5: GeomPoint X=8 Y=6 Z=0
    g6: LineSegment StartX=0 StartY=6 StartZ=0 EndX=8 EndY=6 EndZ=0
  constraints (14):
    c: Coincident(g0,g-1)
    c: Distance(g0) = 6
    c: Vertical(g0)
    c: Coincident(g3,g0)
    c: Weight(g1) = 1
    c: Equal(g1,g2)
    c: InternalAlignment(g1,g3)
    c: InternalAlignment(g2,g3)
    c: InternalAlignment(g4,g3)
    c: InternalAlignment(g5,g3)
    c: Block(g3)
    c: Coincident(g6,g0)
    c: Coincident(g6,g3)
    c: Horizontal(g6)
FEATURE [Sketcher::SketchObject] Sketch046
  FullyConstrained = true
  sketch-geometry (7):
    g0: LineSegment StartX=0 StartY=0 StartZ=0 EndX=0 EndY=6 EndZ=0
    g1: Circle CenterX=0 CenterY=0 CenterZ=0 NormalX=0 NormalY=0 NormalZ=1 AngleXU=0 Radius=1
    g2: Circle CenterX=8 CenterY=6 CenterZ=0 NormalX=0 NormalY=0 NormalZ=1 AngleXU=0 Radius=1
    g3: BSplineCurve PolesCount=3 KnotsCount=2 Degree=2 IsPeriodic=0
    g4: GeomPoint X=0 Y=0 Z=0
    g5: GeomPoint X=8 Y=6 Z=0
    g6: LineSegment StartX=0 StartY=6 StartZ=0 EndX=8 EndY=6 EndZ=0
  constraints (14):
    c: Coincident(g0,g-1)
    c: Distance(g0) = 6
    c: Vertical(g0)
    c: Coincident(g3,g0)
    c: Weight(g1) = 1
    c: Equal(g1,g2)
    c: InternalAlignment(g1,g3)
    c: InternalAlignment(g2,g3)
    c: InternalAlignment(g4,g3)
    c: InternalAlignment(g5,g3)
    c: Block(g3)
    c: Coincident(g6,g0)
    c: Coincident(g6,g3)
    c: Horizontal(g6)
FEATURE [Part::Extrusion] Extrude036  label="caseScrewPillarBracket014"
  Base = -> Sketch045
  Dir = (0,0,1)
  DirMode = 2
  FaceMakerClass = Part::FaceMakerBullseye
  LengthFwd = 2.4
  LengthRev = 0
  Placement = pos=(110.7,29,6.77) rot=(0,-1,0;1.5708rad)
  Solid = true
  Symmetric = false
FEATURE [Part::Extrusion] Extrude037  label="caseScrewPillarBracket015"
  Base = -> Sketch046
  Dir = (0,0,1)
  DirMode = 2
  FaceMakerClass = Part::FaceMakerBullseye
  LengthFwd = 2.4
  LengthRev = 0
  Placement = pos=(108.3,29,65.23) rot=(0,1,0;1.5708rad)
  Solid = true
  Symmetric = false
FEATURE [Part::Box] Box013  label="frontCaseScrewPillarBracket002"
  AttacherType = Attacher::AttachEngine3D
  Height = 2.4
  Length = 22
  Placement = pos=(87,28,2.3) rot=(0,0,1;0rad)
  Width = 7
FEATURE [Part::Box] Box014  label="frontCaseScrewPillarBracket003"
  AttacherType = Attacher::AttachEngine3D
  Height = 2.4
  Length = 22
  Placement = pos=(87,28,67.3) rot=(0,0,1;0rad)
  Width = 7
FEATURE [Part::Feature] Face087
  shape: bbox 4.8 x 30.2 x 2e-07 mm, 1 faces, 0 solids (baked)
FEATURE [Part::Revolution] Revolve091  label="frontCaseScrewPost004"
  Angle = 360
  Axis = (0,1,0)
  Base = (0,0,0)
  FaceMakerClass = Part::FaceMakerBullseye
  Placement = pos=(89.5,4.5,3.5) rot=(0,0,1;0rad)
  Solid = false
  Source = -> Face087
  Symmetric = false
FEATURE [Part::Feature] Face088
  shape: bbox 4.8 x 30.2 x 2e-07 mm, 1 faces, 0 solids (baked)
FEATURE [Part::Revolution] Revolve092  label="frontCaseScrewPost005"
  Angle = 360
  Axis = (0,1,0)
  Base = (0,0,0)
  FaceMakerClass = Part::FaceMakerBullseye
  Placement = pos=(89.5,4.5,68.5) rot=(0,0,1;0rad)
  Solid = false
  Source = -> Face088
  Symmetric = false
FEATURE [Part::Feature] Face089
  shape: bbox 3.5 x 30.2 x 2e-07 mm, 1 faces, 0 solids (baked)
FEATURE [Part::Revolution] Revolve093  label="backCaseScrewPost002"
  Angle = 360
  Axis = (0,1,0)
  Base = (0,0,0)
  FaceMakerClass = Part::FaceMakerBullseye
  Placement = pos=(12.5,4.5,10) rot=(0,0,1;0rad)
  Solid = false
  Source = -> Face089
  Symmetric = false
FEATURE [Part::Feature] Face090
  shape: bbox 3.5 x 30.2 x 2e-07 mm, 1 faces, 0 solids (baked)
FEATURE [Part::Revolution] Revolve094  label="backCaseScrewPost003"
  Angle = 360
  Axis = (0,1,0)
  Base = (0,0,0)
  FaceMakerClass = Part::FaceMakerBullseye
  Placement = pos=(12.5,4.5,62) rot=(0,0,1;0rad)
  Solid = false
  Source = -> Face090
  Symmetric = false
FEATURE [Part::Box] Box015  label="Cube011"
  AttacherType = Attacher::AttachEngine3D
  Height = 28.8
  Length = 3
  Placement = pos=(107.3,28,21.6) rot=(0,0,1;0rad)
  Width = 7
FEATURE [Part::Box] Box016  label="Cube012"
  AttacherType = Attacher::AttachEngine3D
  Height = 3
  Length = 7.4
  Placement = pos=(107.3,28,18.6) rot=(0,0,1;0rad)
  Width = 7
FEATURE [Part::Box] Box017  label="Cube013"
  AttacherType = Attacher::AttachEngine3D
  Height = 3
  Length = 7.4
  Placement = pos=(107.3,28,50.4) rot=(0,0,1;0rad)
  Width = 7
FEATURE [Part::Cylinder] Cylinder024
  Angle = 360
  AttacherType = Attacher::AttachEngine3D
  Height = 20
  Placement = pos=(0,0,36.15) rot=(0,0,1;0rad)
  Radius = 14.3
FEATURE [Part::Cylinder] Cylinder025
  Angle = 360
  AttacherType = Attacher::AttachEngine3D
  Height = 10
  Placement = pos=(0,0,36.15) rot=(0,0,1;0rad)
  Radius = 4
FEATURE [Part::MultiFuse] Fusion066  label="removeToCreteHoleForPlugHousing009"
  Placement = pos=(70,19,36) rot=(0,1,0;1.5708rad)
  Shapes = -> [Cylinder024,Cylinder025]
FEATURE [Part::MultiFuse] Fusion065  label="plugHousingBracketHolder002"
  Shapes = -> [Box017,Box015,Box016]
FEATURE [Part::Cut] Cut025  label="plugHousingBracketHolder003"
  Base = -> Fusion065
  Placement = pos=(7,0,0) rot=(0,0,1;0rad)
  Tool = -> Fusion066
FEATURE [Sketcher::SketchObject] Sketch047
  FullyConstrained = false
  Placement = pos=(0,0,0) rot=(1,0,0;1.5708rad)
  sketch-geometry (24):
    g0: ArcOfCircle CenterX=-4 CenterY=-10.5 CenterZ=0 NormalX=0 NormalY=0 NormalZ=1 AngleXU=0 Radius=1.5 StartAngle=6e-16 EndAngle=3.14159
    g1: ArcOfCircle CenterX=-34.2 CenterY=-10.5 CenterZ=0 NormalX=0 NormalY=0 NormalZ=1 AngleXU=0 Radius=1.5 StartAngle=0 EndAngle=3.14159
    g2: ArcOfCircle CenterX=-34.2 CenterY=-27.7 CenterZ=0 NormalX=0 NormalY=0 NormalZ=1 AngleXU=0 Radius=1.5 StartAngle=3.14159 EndAngle=6.28319
    g3: ArcOfCircle CenterX=-4 CenterY=-27.7 CenterZ=0 NormalX=0 NormalY=0 NormalZ=1 AngleXU=0 Radius=1.5 StartAngle=3.1416 EndAngle=6.28319
    g4: ArcOfCircle CenterX=-10 CenterY=-4.3 CenterZ=0 NormalX=0 NormalY=0 NormalZ=1 AngleXU=0 Radius=1.5 StartAngle=2e-16 EndAngle=3.14159
    g5: ArcOfCircle CenterX=-16.1 CenterY=-1.8 CenterZ=0 NormalX=0 NormalY=0 NormalZ=1 AngleXU=0 Radius=1.5 StartAngle=5e-16 EndAngle=3.14159
    g6: ArcOfCircle CenterX=-22.1 CenterY=-1.8 CenterZ=0 NormalX=0 NormalY=0 NormalZ=1 AngleXU=0 Radius=1.5 StartAngle=5e-16 EndAngle=3.14159
    g7: ArcOfCircle CenterX=-28.2 CenterY=-4.3 CenterZ=0 NormalX=0 NormalY=0 NormalZ=1 AngleXU=0 Radius=1.5 StartAngle=2e-16 EndAngle=3.14159
    g8: ArcOfCircle CenterX=-10 CenterY=-33.9 CenterZ=0 NormalX=0 NormalY=0 NormalZ=1 AngleXU=0 Radius=1.5 StartAngle=3.14159 EndAngle=6.28319
    g9: ArcOfCircle CenterX=-16.1 CenterY=-36.4 CenterZ=0 NormalX=0 NormalY=0 NormalZ=1 AngleXU=0 Radius=1.5 StartAngle=3.14159 EndAngle=6.28319
    g10: ArcOfCircle CenterX=-22.1 CenterY=-36.4 CenterZ=0 NormalX=0 NormalY=0 NormalZ=1 AngleXU=0 Radius=1.5 StartAngle=3.14159 EndAngle=6.28319
    g11: ArcOfCircle CenterX=-28.2 CenterY=-33.9 CenterZ=0 NormalX=0 NormalY=0 NormalZ=1 AngleXU=0 Radius=1.5 StartAngle=3.14159 EndAngle=6.28319
    g12: LineSegment StartX=-35.7 StartY=-10.5 StartZ=0 EndX=-35.7 EndY=-27.7 EndZ=0
    g13: LineSegment StartX=-32.7 StartY=-10.5 StartZ=0 EndX=-32.7 EndY=-27.7 EndZ=0
    g14: LineSegment StartX=-29.7 StartY=-33.9 StartZ=0 EndX=-29.7 EndY=-4.3 EndZ=0
    g15: LineSegment StartX=-26.7 StartY=-33.9 StartZ=0 EndX=-26.7 EndY=-4.3 EndZ=0
    g16: LineSegment StartX=-2.5 StartY=-10.5 StartZ=0 EndX=-2.5 EndY=-27.7 EndZ=0
    g17: LineSegment StartX=-8.5 StartY=-4.3 StartZ=0 EndX=-8.5 EndY=-33.9 EndZ=0
    g18: LineSegment StartX=-5.5 StartY=-10.5 StartZ=0 EndX=-5.5 EndY=-27.7 EndZ=0
    g19: LineSegment StartX=-11.5 StartY=-4.3 StartZ=0 EndX=-11.5 EndY=-33.9 EndZ=0
    g20: LineSegment StartX=-14.6 StartY=-1.8 StartZ=0 EndX=-14.6 EndY=-36.4 EndZ=0
    g21: LineSegment StartX=-17.6 StartY=-1.8 StartZ=0 EndX=-17.6 EndY=-36.4 EndZ=0
    g22: LineSegment StartX=-20.6 StartY=-36.4 StartZ=0 EndX=-20.6 EndY=-1.8 EndZ=0
    g23: LineSegment StartX=-23.6 StartY=-1.8 StartZ=0 EndX=-23.6 EndY=-36.4 EndZ=0
  constraints (48):
    c: Block(g0)
    c: Block(g1)
    c: Block(g2)
    c: Block(g3)
    c: Block(g4)
    c: Block(g5)
    c: Block(g6)
    c: Block(g7)
    c: Block(g8)
    c: Block(g9)
    c: Block(g10)
    c: Block(g11)
    c: Coincident(g12,g1)
    c: Coincident(g12,g2)
    c: Vertical(g12)
    c: Coincident(g13,g1)
    c: Coincident(g13,g2)
    c: Vertical(g13)
    c: Coincident(g14,g11)
    c: Coincident(g14,g7)
    c: Vertical(g14)
    c: Coincident(g15,g11)
    c: Coincident(g15,g7)
    c: Vertical(g15)
    c: Coincident(g16,g0)
    c: Coincident(g16,g3)
    c: Vertical(g16)
    c: Coincident(g17,g4)
    c: Coincident(g17,g8)
    c: Vertical(g17)
    c: Coincident(g18,g0)
    c: Coincident(g18,g3)
    c: Vertical(g18)
    c: Coincident(g19,g4)
    c: Coincident(g19,g8)
    c: Vertical(g19)
    c: Coincident(g20,g5)
    c: Coincident(g20,g9)
    c: Vertical(g20)
    c: Coincident(g21,g5)
    c: Coincident(g21,g9)
    c: Vertical(g21)
    c: Coincident(g22,g10)
    c: Coincident(g22,g6)
    c: Vertical(g22)
    c: Coincident(g23,g6)
    c: Coincident(g23,g10)
    c: Vertical(g23)
FEATURE [Part::Extrusion] Extrude038  label="removeToCreateFanGrillHoles001"
  Base = -> Sketch047
  Dir = (0,-1,6e-16)
  DirMode = 2
  FaceMakerClass = Part::FaceMakerBullseye
  LengthFwd = 10
  LengthRev = 0
  Placement = pos=(65.4,44,54.82) rot=(0,0,1;0rad)
  Solid = true
  Symmetric = false
FEATURE [Part::Feature] Wire004
  shape: bbox 11 x 5.2 x 2e-07 mm, 0 faces, 0 solids (baked)
FEATURE [Part::Revolution] Revolve095
  Angle = 360
  Axis = (0,1,0)
  Base = (0,0,0)
  FaceMakerClass = Part::FaceMakerBullseye
  Placement = pos=(30.3,38,19.7) rot=(0,0,1;0rad)
  Solid = true
  Source = -> Wire004
  Symmetric = false
FEATURE [Part::Feature] Wire005
  shape: bbox 11 x 5.2 x 2e-07 mm, 0 faces, 0 solids (baked)
FEATURE [Part::Revolution] Revolve096
  Angle = 360
  Axis = (0,1,0)
  Base = (0,0,0)
  FaceMakerClass = Part::FaceMakerBullseye
  Placement = pos=(30.3,38,51.7) rot=(0,0,1;0rad)
  Solid = true
  Source = -> Wire005
  Symmetric = false
FEATURE [Part::Feature] Wire006
  shape: bbox 11 x 5.2 x 2e-07 mm, 0 faces, 0 solids (baked)
FEATURE [Part::Revolution] Revolve097
  Angle = 360
  Axis = (0,1,0)
  Base = (0,0,0)
  FaceMakerClass = Part::FaceMakerBullseye
  Placement = pos=(62.3,38,51.7) rot=(0,0,1;0rad)
  Solid = true
  Source = -> Wire006
  Symmetric = false
FEATURE [Part::Feature] Wire007
  shape: bbox 11 x 5.2 x 2e-07 mm, 0 faces, 0 solids (baked)
FEATURE [Part::Revolution] Revolve098
  Angle = 360
  Axis = (0,1,0)
  Base = (0,0,0)
  FaceMakerClass = Part::FaceMakerBullseye
  Placement = pos=(62.3,38,19.7) rot=(0,0,1;0rad)
  Solid = true
  Source = -> Wire007
  Symmetric = false
FEATURE [Part::MultiFuse] Fusion067  label="fanScrewHousing002"
  Shapes = -> [Revolve098,Revolve097,Revolve096,Revolve095]
FEATURE [Part::Feature] Face091 .. Face094  x4 (patterned run collapsed; names and placements below)
  shape: bbox 3.5 x 17.8 x 2e-07 mm, 1 faces, 0 solids (baked)
FEATURE [Part::Revolution] Revolve099  label="removeToCreateScrewAndThreadedInsertHole026"
  Angle = 360
  Axis = (0,1,0)
  Base = (0,0,0)
  FaceMakerClass = Part::FaceMakerBullseye
  Placement = pos=(62.3,30.3,19.7) rot=(0,0,1;0rad)
  Solid = false
  Source = -> Face091
  Symmetric = false
FEATURE [Part::Revolution] Revolve100  label="removeToCreateScrewAndThreadedInsertHole027"
  Angle = 360
  Axis = (0,1,0)
  Base = (0,0,0)
  FaceMakerClass = Part::FaceMakerBullseye
  Placement = pos=(62.3,30.3,51.7) rot=(0,0,1;0rad)
  Solid = false
  Source = -> Face092
  Symmetric = false
FEATURE [Part::Revolution] Revolve101  label="removeToCreateScrewAndThreadedInsertHole028"
  Angle = 360
  Axis = (0,1,0)
  Base = (0,0,0)
  FaceMakerClass = Part::FaceMakerBullseye
  Placement = pos=(30.3,30.3,19.7) rot=(0,0,1;0rad)
  Solid = false
  Source = -> Face093
  Symmetric = false
FEATURE [Part::Revolution] Revolve102  label="removeToCreateScrewAndThreadedInsertHole029"
  Angle = 360
  Axis = (0,1,0)
  Base = (0,0,0)
  FaceMakerClass = Part::FaceMakerBullseye
  Placement = pos=(30.3,30.3,51.7) rot=(0,0,1;0rad)
  Solid = false
  Source = -> Face094
  Symmetric = false
FEATURE [Part::MultiFuse] Fusion068  label="createThreadedInsertHolesForFan002"
  Shapes = -> [Revolve099,Revolve100,Revolve101,Revolve102]
FEATURE [Part::Cut] Cut026  label="fanScrewHousing003"
  Base = -> Fusion067
  Tool = -> Fusion068
FEATURE [Sketcher::SketchObject] Sketch048
  FullyConstrained = false
  Placement = pos=(0,0,0) rot=(1,0,0;1.5708rad)
  sketch-geometry (24):
    g0: ArcOfCircle CenterX=-4 CenterY=-10.5 CenterZ=0 NormalX=0 NormalY=0 NormalZ=1 AngleXU=0 Radius=1.5 StartAngle=6e-16 EndAngle=3.14159
    g1: ArcOfCircle CenterX=-34.2 CenterY=-10.5 CenterZ=0 NormalX=0 NormalY=0 NormalZ=1 AngleXU=0 Radius=1.5 StartAngle=0 EndAngle=3.14159
    g2: ArcOfCircle CenterX=-34.2 CenterY=-27.7 CenterZ=0 NormalX=0 NormalY=0 NormalZ=1 AngleXU=0 Radius=1.5 StartAngle=3.14159 EndAngle=6.28319
    g3: ArcOfCircle CenterX=-4 CenterY=-27.7 CenterZ=0 NormalX=0 NormalY=0 NormalZ=1 AngleXU=0 Radius=1.5 StartAngle=3.1416 EndAngle=6.28319
    g4: ArcOfCircle CenterX=-10 CenterY=-4.3 CenterZ=0 NormalX=0 NormalY=0 NormalZ=1 AngleXU=0 Radius=1.5 StartAngle=2e-16 EndAngle=3.14159
    g5: ArcOfCircle CenterX=-16.1 CenterY=-1.8 CenterZ=0 NormalX=0 NormalY=0 NormalZ=1 AngleXU=0 Radius=1.5 StartAngle=5e-16 EndAngle=3.14159
    g6: ArcOfCircle CenterX=-22.1 CenterY=-1.8 CenterZ=0 NormalX=0 NormalY=0 NormalZ=1 AngleXU=0 Radius=1.5 StartAngle=5e-16 EndAngle=3.14159
    g7: ArcOfCircle CenterX=-28.2 CenterY=-4.3 CenterZ=0 NormalX=0 NormalY=0 NormalZ=1 AngleXU=0 Radius=1.5 StartAngle=2e-16 EndAngle=3.14159
    g8: ArcOfCircle CenterX=-10 CenterY=-33.9 CenterZ=0 NormalX=0 NormalY=0 NormalZ=1 AngleXU=0 Radius=1.5 StartAngle=3.14159 EndAngle=6.28319
    g9: ArcOfCircle CenterX=-16.1 CenterY=-36.4 CenterZ=0 NormalX=0 NormalY=0 NormalZ=1 AngleXU=0 Radius=1.5 StartAngle=3.14159 EndAngle=6.28319
    g10: ArcOfCircle CenterX=-22.1 CenterY=-36.4 CenterZ=0 NormalX=0 NormalY=0 NormalZ=1 AngleXU=0 Radius=1.5 StartAngle=3.14159 EndAngle=6.28319
    g11: ArcOfCircle CenterX=-28.2 CenterY=-33.9 CenterZ=0 NormalX=0 NormalY=0 NormalZ=1 AngleXU=0 Radius=1.5 StartAngle=3.14159 EndAngle=6.28319
    g12: LineSegment StartX=-35.7 StartY=-10.5 StartZ=0 EndX=-35.7 EndY=-27.7 EndZ=0
    g13: LineSegment StartX=-32.7 StartY=-10.5 StartZ=0 EndX=-32.7 EndY=-27.7 EndZ=0
    g14: LineSegment StartX=-29.7 StartY=-33.9 StartZ=0 EndX=-29.7 EndY=-4.3 EndZ=0
    g15: LineSegment StartX=-26.7 StartY=-33.9 StartZ=0 EndX=-26.7 EndY=-4.3 EndZ=0
    g16: LineSegment StartX=-2.5 StartY=-10.5 StartZ=0 EndX=-2.5 EndY=-27.7 EndZ=0
    g17: LineSegment StartX=-8.5 StartY=-4.3 StartZ=0 EndX=-8.5 EndY=-33.9 EndZ=0
    g18: LineSegment StartX=-5.5 StartY=-10.5 StartZ=0 EndX=-5.5 EndY=-27.7 EndZ=0
    g19: LineSegment StartX=-11.5 StartY=-4.3 StartZ=0 EndX=-11.5 EndY=-33.9 EndZ=0
    g20: LineSegment StartX=-14.6 StartY=-1.8 StartZ=0 EndX=-14.6 EndY=-36.4 EndZ=0
    g21: LineSegment StartX=-17.6 StartY=-1.8 StartZ=0 EndX=-17.6 EndY=-36.4 EndZ=0
    g22: LineSegment StartX=-20.6 StartY=-36.4 StartZ=0 EndX=-20.6 EndY=-1.8 EndZ=0
    g23: LineSegment StartX=-23.6 StartY=-1.8 StartZ=0 EndX=-23.6 EndY=-36.4 EndZ=0
  constraints (48):
    c: Block(g0)
    c: Block(g1)
    c: Block(g2)
    c: Block(g3)
    c: Block(g4)
    c: Block(g5)
    c: Block(g6)
    c: Block(g7)
    c: Block(g8)
    c: Block(g9)
    c: Block(g10)
    c: Block(g11)
    c: Coincident(g12,g1)
    c: Coincident(g12,g2)
    c: Vertical(g12)
    c: Coincident(g13,g1)
    c: Coincident(g13,g2)
    c: Vertical(g13)
    c: Coincident(g14,g11)
    c: Coincident(g14,g7)
    c: Vertical(g14)
    c: Coincident(g15,g11)
    c: Coincident(g15,g7)
    c: Vertical(g15)
    c: Coincident(g16,g0)
    c: Coincident(g16,g3)
    c: Vertical(g16)
    c: Coincident(g17,g4)
    c: Coincident(g17,g8)
    c: Vertical(g17)
    c: Coincident(g18,g0)
    c: Coincident(g18,g3)
    c: Vertical(g18)
    c: Coincident(g19,g4)
    c: Coincident(g19,g8)
    c: Vertical(g19)
    c: Coincident(g20,g5)
    c: Coincident(g20,g9)
    c: Vertical(g20)
    c: Coincident(g21,g5)
    c: Coincident(g21,g9)
    c: Vertical(g21)
    c: Coincident(g22,g10)
    c: Coincident(g22,g6)
    c: Vertical(g22)
    c: Coincident(g23,g6)
    c: Coincident(g23,g10)
    c: Vertical(g23)
FEATURE [Part::Extrusion] Extrude039  label="removeToCreateFanGrillHoles002"
  Base = -> Sketch048
  Dir = (0,-1,6e-16)
  DirMode = 2
  FaceMakerClass = Part::FaceMakerBullseye
  LengthFwd = 10
  LengthRev = 0
  Placement = pos=(65.4,44,54.82) rot=(0,0,1;0rad)
  Solid = true
  Symmetric = false
FEATURE [Part::Cut] Cut027  label="fanScrewHousing004"
  Base = -> Cut026
  Tool = -> Extrude038
FEATURE [Part::Cut] Cut028  label="top014"
  Base = -> Fillet026
  Tool = -> Extrude039
FEATURE [Part::Feature] Face095 .. Face098  x4 (patterned run collapsed; names and placements below)
  shape: bbox 3.5 x 17.8 x 2e-07 mm, 1 faces, 0 solids (baked)
FEATURE [Part::Revolution] Revolve103  label="removeToCreateScrewAndThreadedInsertHole030"
  Angle = 360
  Axis = (0,1,0)
  Base = (0,0,0)
  FaceMakerClass = Part::FaceMakerBullseye
  Placement = pos=(62.3,30.3,19.7) rot=(0,0,1;0rad)
  Solid = false
  Source = -> Face095
  Symmetric = false
FEATURE [Part::Revolution] Revolve104  label="removeToCreateScrewAndThreadedInsertHole031"
  Angle = 360
  Axis = (0,1,0)
  Base = (0,0,0)
  FaceMakerClass = Part::FaceMakerBullseye
  Placement = pos=(62.3,30.3,51.7) rot=(0,0,1;0rad)
  Solid = false
  Source = -> Face096
  Symmetric = false
FEATURE [Part::Revolution] Revolve105  label="removeToCreateScrewAndThreadedInsertHole032"
  Angle = 360
  Axis = (0,1,0)
  Base = (0,0,0)
  FaceMakerClass = Part::FaceMakerBullseye
  Placement = pos=(30.3,30.3,19.7) rot=(0,0,1;0rad)
  Solid = false
  Source = -> Face097
  Symmetric = false
FEATURE [Part::Revolution] Revolve106  label="removeToCreateScrewAndThreadedInsertHole033"
  Angle = 360
  Axis = (0,1,0)
  Base = (0,0,0)
  FaceMakerClass = Part::FaceMakerBullseye
  Placement = pos=(30.3,30.3,51.7) rot=(0,0,1;0rad)
  Solid = false
  Source = -> Face098
  Symmetric = false
FEATURE [Part::MultiFuse] Fusion069  label="createThreadedInsertHolesForFan003"
  Shapes = -> [Revolve103,Revolve104,Revolve105,Revolve106]
FEATURE [Part::Cut] Cut029  label="top015"
  Base = -> Cut028
  Tool = -> Fusion054
FEATURE [Part::Cut] Cut030  label="fanScrewHousing005"
  Base = -> Cut027
  Tool = -> Fusion069
FEATURE [Part::Cylinder] Cylinder026  label="removeToCreteHoleForPlugHousing010"
  Angle = 360
  AttacherType = Attacher::AttachEngine3D
  Height = 20
  Placement = pos=(-2,19,36) rot=(0,1,0;1.5708rad)
  Radius = 14.3
FEATURE [Part::Box] Box018  label="removeToCreteHoleForPlugHousing011"
  AttacherType = Attacher::AttachEngine3D
  Height = 28.6
  Length = 10
  Placement = pos=(-2,0,21.7) rot=(0,0,1;0rad)
  Width = 19
FEATURE [Part::Box] Box019  label="wireHolderBottomCaseBit"
  AttacherType = Attacher::AttachEngine3D
  Height = 28
  Length = 3
  Placement = pos=(0,0,22) rot=(0,0,1;0rad)
  Width = 21
FEATURE [Part::Cylinder] Cylinder027  label="removeToCreteHoleForPlugHousing012"
  Angle = 360
  AttacherType = Attacher::AttachEngine3D
  Height = 20
  Placement = pos=(-2,19,36) rot=(0,1,0;1.5708rad)
  Radius = 14.3
FEATURE [Part::Cut] Cut031  label="wireHolderBottomCaseBit001"
  Base = -> Box019
  Tool = -> Cylinder027
FEATURE [Part::MultiFuse] Fusion070  label="removeToCreteHoleForPlugHousing013"
  Shapes = -> [Box018,Cylinder026]
FEATURE [Part::Cut] Cut032  label="top016"
  Base = -> Cut029
  Tool = -> Fusion070
FEATURE [Part::Cylinder] Cylinder028
  Angle = 360
  AttacherType = Attacher::AttachEngine3D
  Height = 20
  Placement = pos=(0,0,36.15) rot=(0,0,1;0rad)
  Radius = 14.3
FEATURE [Part::Cylinder] Cylinder029
  Angle = 360
  AttacherType = Attacher::AttachEngine3D
  Height = 10
  Placement = pos=(0,0,36.15) rot=(0,0,1;0rad)
  Radius = 4
FEATURE [Part::MultiFuse] Fusion071  label="removeToCreteHoleForPlugHousing014"
  Placement = pos=(70,19,36) rot=(0,1,0;1.5708rad)
  Shapes = -> [Cylinder028,Cylinder029]
FEATURE [Sketcher::SketchObject] Sketch049  label="topSketch011"
  FullyConstrained = true
  sketch-geometry (4):
    g0: ArcOfCircle CenterX=105 CenterY=19 CenterZ=0 NormalX=0 NormalY=0 NormalZ=1 AngleXU=0 Radius=20.6155 StartAngle=5.54125 EndAngle=6.28319
    g1: ArcOfCircle CenterX=105 CenterY=19 CenterZ=0 NormalX=0 NormalY=0 NormalZ=1 AngleXU=0 Radius=13 StartAngle=5.54125 EndAngle=6.28319
    g2: LineSegment StartX=118 StartY=19 StartZ=0 EndX=125.616 EndY=19 EndZ=0
    g3: LineSegment StartX=114.583 StartY=10.2157 StartZ=0 EndX=120.197 EndY=5.06982 EndZ=0
  constraints (7):
    c: Block(g0)
    c: Block(g1)
    c: Coincident(g2,g1)
    c: Coincident(g2,g0)
    c: Horizontal(g2)
    c: Coincident(g3,g1)
    c: Coincident(g3,g0)
FEATURE [Part::Box] Box020  label="removeToCreteHoleForPlugHousing015"
  AttacherType = Attacher::AttachEngine3D
  Height = 28.6
  Length = 20
  Placement = pos=(106.15,0,21.7) rot=(0,0,1;0rad)
  Width = 19
FEATURE [Part::MultiFuse] Fusion072  label="removeToCreteHoleForPlugHousing016"
  Shapes = -> [Box020,Fusion071]
FEATURE [Part::Cut] Cut033  label="removeToCreteHoleForPlugHousing017"
  Base = -> Cut032
  Tool = -> Fusion072
FEATURE [Part::Cylinder] Cylinder030
  Angle = 360
  AttacherType = Attacher::AttachEngine3D
  Height = 20
  Placement = pos=(0,0,36.15) rot=(0,0,1;0rad)
  Radius = 14.3
FEATURE [Part::Cylinder] Cylinder031
  Angle = 360
  AttacherType = Attacher::AttachEngine3D
  Height = 10
  Placement = pos=(0,0,36.15) rot=(0,0,1;0rad)
  Radius = 4
FEATURE [Part::Box] Box021  label="removeToCreteHoleForPlugHousing019"
  AttacherType = Attacher::AttachEngine3D
  Height = 28.6
  Length = 20
  Placement = pos=(106.15,0,21.7) rot=(0,0,1;0rad)
  Width = 19
FEATURE [Part::MultiFuse] Fusion074  label="removeToCreteHoleForPlugHousing020"
  Placement = pos=(70,19,36) rot=(0,1,0;1.5708rad)
  Shapes = -> [Cylinder030,Cylinder031]
FEATURE [Part::MultiFuse] Fusion073  label="removeToCreteHoleForPlugHousing018"
  Placement = pos=(0,0,28.3) rot=(0,0,1;0rad)
  Shapes = -> [Box021,Fusion074]
FEATURE [Part::Cylinder] Cylinder032
  Angle = 360
  AttacherType = Attacher::AttachEngine3D
  Height = 20
  Placement = pos=(0,0,36.15) rot=(0,0,1;0rad)
  Radius = 14.3
FEATURE [Part::Cylinder] Cylinder033
  Angle = 360
  AttacherType = Attacher::AttachEngine3D
  Height = 10
  Placement = pos=(0,0,36.15) rot=(0,0,1;0rad)
  Radius = 4
FEATURE [Part::Box] Box022  label="removeToCreteHoleForPlugHousing021"
  AttacherType = Attacher::AttachEngine3D
  Height = 28.6
  Length = 20
  Placement = pos=(106.15,0,21.7) rot=(0,0,1;0rad)
  Width = 19
FEATURE [Part::MultiFuse] Fusion076  label="removeToCreteHoleForPlugHousing023"
  Placement = pos=(70,19,36) rot=(0,1,0;1.5708rad)
  Shapes = -> [Cylinder032,Cylinder033]
FEATURE [Part::MultiFuse] Fusion075  label="removeToCreteHoleForPlugHousing022"
  Placement = pos=(0,0,-28.3) rot=(0,0,1;0rad)
  Shapes = -> [Box022,Fusion076]
FEATURE [Part::MultiFuse] Fusion077  label="removeToCreatePlugHousingBottomBit"
  Shapes = -> [Fusion075,Fusion073]
FEATURE [Part::Cylinder] Cylinder034
  Angle = 360
  AttacherType = Attacher::AttachEngine3D
  Height = 20
  Placement = pos=(0,0,36.15) rot=(0,0,1;0rad)
  Radius = 14
FEATURE [Part::Cylinder] Cylinder035
  Angle = 360
  AttacherType = Attacher::AttachEngine3D
  Height = 10
  Placement = pos=(0,0,36.15) rot=(0,0,1;0rad)
  Radius = 4
FEATURE [Part::MultiFuse] Fusion078  label="removeToCreteHoleForPlugHousing024"
  Placement = pos=(70,19,36) rot=(0,1,0;1.5708rad)
  Shapes = -> [Cylinder034,Cylinder035]
FEATURE [Part::MultiFuse] Fusion079  label="removeToCreatePlugHousingBottomBit001"
  Shapes = -> [Fusion078,Fusion077]
FEATURE [Part::Extrusion] Extrude040  label="bottomPlugHousingBit"
  Base = -> Sketch049
  Dir = (0,0,1)
  DirMode = 2
  FaceMakerClass = Part::FaceMakerBullseye
  LengthFwd = 72
  LengthRev = 0
  Solid = true
  Symmetric = false
FEATURE [Part::Cut] Cut034  label="bottomPlugHousingBit001"
  Base = -> Extrude040
  Placement = pos=(-0.09,0,0) rot=(0,0,1;0rad)
  Tool = -> Fusion079
FEATURE [Part::Box] Box023  label="Cube014"
  AttacherType = Attacher::AttachEngine3D
  Height = 16
  Length = 8
  Placement = pos=(12.7,31.52,28) rot=(0,0,1;0rad)
  Width = 4
FEATURE [Part::Cylinder] Cylinder036
  Angle = 360
  AttacherType = Attacher::AttachEngine3D
  Height = 10
  Placement = pos=(0,0,36.15) rot=(0,0,1;0rad)
  Radius = 4
FEATURE [Part::Cylinder] Cylinder037
  Angle = 360
  AttacherType = Attacher::AttachEngine3D
  Height = 20
  Placement = pos=(0,0,36.15) rot=(0,0,1;0rad)
  Radius = 8.2
FEATURE [Part::MultiFuse] Fusion080  label="removeToCreteHoleForPlugHousing025"
  Placement = pos=(-42,19,36) rot=(0,1,0;1.5708rad)
  Shapes = -> [Cylinder037,Cylinder036]
FEATURE [Sketcher::SketchObject] Sketch050  label="topSketch012"
  FullyConstrained = true
  sketch-geometry (4):
    g0: LineSegment StartX=16.8446 StartY=31.512 StartZ=0 EndX=16.3251 EndY=34.4666 EndZ=0
    g1: ArcOfCircle CenterX=19 CenterY=19.2524 CenterZ=0 NormalX=0 NormalY=0 NormalZ=1 AngleXU=0 Radius=15.4476 StartAngle=1.74483 EndAngle=2.72717
    g2: ArcOfCircle CenterX=19 CenterY=19.2524 CenterZ=0 NormalX=0 NormalY=0 NormalZ=1 AngleXU=0 Radius=12.4476 StartAngle=1.74483 EndAngle=2.73189
    g3: LineSegment StartX=4.86004 StartY=25.4725 StartZ=0 EndX=7.58253 EndY=24.2107 EndZ=0
  constraints (7):
    c: Block(g0)
    c: Coincident(g1,g0)
    c: Coincident(g2,g0)
    c: Coincident(g3,g1)
    c: Coincident(g3,g2)
    c: Block(g1)
    c: Block(g2)
FEATURE [Part::Extrusion] Extrude041
  Base = -> Sketch050
  Dir = (0,0,1)
  DirMode = 2
  FaceMakerClass = Part::FaceMakerBullseye
  LengthFwd = 10.6
  LengthRev = 0
  Placement = pos=(0,0,31) rot=(0,0,1;0rad)
  Solid = true
  Symmetric = false
FEATURE [Part::Cut] Cut035
  Base = -> Extrude041
  Placement = pos=(0,0,-0.3) rot=(0,0,1;0rad)
  Tool = -> Fusion080
FEATURE [Part::Cut] Cut036
  Base = -> Box023
  Tool = -> Cut035
FEATURE [Part::Fillet] Fillet027
  Base = -> Cut036
  Edges = 1 edges r=0.7: [Edge13]
FEATURE [Part::Fillet] Fillet028
  Base = -> Fillet027
  Edges = 1 edges r=0.7: [Edge13]
FEATURE [Part::Fillet] Fillet029
  Base = -> Fillet028
  Edges = 1 edges r=0.7: [Edge16]
FEATURE [Part::Fillet] Fillet030
  Base = -> Fillet029
  Edges = 1 edges r=0.7: [Edge11]
FEATURE [Part::Fillet] Fillet031
  Base = -> Fillet030
  Edges = 1 edges r=0.7: [Edge10]
FEATURE [Part::Fillet] Fillet032
  Base = -> Fillet031
  Edges = 1 edges r=1.2: [Edge5]
FEATURE [Part::Fillet] Fillet033
  Base = -> Fillet032
  Edges = 1 edges r=1.2: [Edge12]
FEATURE [Part::Fillet] Fillet034  label="wireHousingRetainer"
  Base = -> Fillet033
  Edges = 1 edges r=2: [Edge1]
  Placement = pos=(0.3,0,0) rot=(0,0,1;0rad)
FEATURE [Part::Feature] Face099
  shape: bbox 3.5 x 17.8 x 2e-07 mm, 1 faces, 0 solids (baked)
FEATURE [Part::Revolution] Revolve107  label="removeToCreateScrewAndThreadedInsertHole034"
  Angle = 360
  Axis = (0,1,0)
  Base = (0,0,0)
  FaceMakerClass = Part::FaceMakerBullseye
  Placement = pos=(12.5,0,10) rot=(0,0,1;0rad)
  Solid = false
  Source = -> Face099
  Symmetric = false
FEATURE [Part::Feature] Face100
  shape: bbox 3.5 x 17.8 x 2e-07 mm, 1 faces, 0 solids (baked)
FEATURE [Part::Revolution] Revolve108  label="removeToCreateScrewAndThreadedInsertHole035"
  Angle = 360
  Axis = (0,1,0)
  Base = (0,0,0)
  FaceMakerClass = Part::FaceMakerBullseye
  Placement = pos=(12.5,0,62) rot=(0,0,1;0rad)
  Solid = false
  Source = -> Face100
  Symmetric = false
FEATURE [Part::Feature] Face101
  shape: bbox 3.5 x 17.8 x 2e-07 mm, 1 faces, 0 solids (baked)
FEATURE [Part::Revolution] Revolve109  label="removeToCreateScrewAndThreadedInsertHole036"
  Angle = 360
  Axis = (0,1,0)
  Base = (0,0,0)
  FaceMakerClass = Part::FaceMakerBullseye
  Placement = pos=(89.5,0,68.5) rot=(0,0,1;0rad)
  Solid = false
  Source = -> Face101
  Symmetric = false
FEATURE [Part::Feature] Face102
  shape: bbox 3.5 x 17.8 x 2e-07 mm, 1 faces, 0 solids (baked)
FEATURE [Part::Revolution] Revolve110  label="removeToCreateScrewAndThreadedInsertHole037"
  Angle = 360
  Axis = (0,1,0)
  Base = (0,0,0)
  FaceMakerClass = Part::FaceMakerBullseye
  Placement = pos=(89.5,0,3.5) rot=(0,0,1;0rad)
  Solid = false
  Source = -> Face102
  Symmetric = false
FEATURE [Part::Feature] Face103
  shape: bbox 3.5 x 17.8 x 2e-07 mm, 1 faces, 0 solids (baked)
FEATURE [Part::Revolution] Revolve111  label="removeToCreateScrewAndThreadedInsertHole038"
  Angle = 360
  Axis = (0,1,0)
  Base = (0,0,0)
  FaceMakerClass = Part::FaceMakerBullseye
  Placement = pos=(109.5,4.7,3.5) rot=(0,0,1;0rad)
  Solid = false
  Source = -> Face103
  Symmetric = false
FEATURE [Part::Feature] Face104
  shape: bbox 3.5 x 17.8 x 2e-07 mm, 1 faces, 0 solids (baked)
FEATURE [Part::Revolution] Revolve112  label="removeToCreateScrewAndThreadedInsertHole039"
  Angle = 360
  Axis = (0,1,0)
  Base = (0,0,0)
  FaceMakerClass = Part::FaceMakerBullseye
  Placement = pos=(109.5,4.7,68.5) rot=(0,0,1;0rad)
  Solid = false
  Source = -> Face104
  Symmetric = false
FEATURE [Part::MultiFuse] Fusion081  label="removeToCreateScrewAndThreadedInsertHole040"
  Shapes = -> [Revolve107,Revolve108,Revolve109,Revolve110,Revolve111,Revolve112]
FEATURE [Part::MultiFuse] Fusion082  label="casePillars002"
  Shapes = -> [Revolve094,Revolve092,Revolve090,Revolve089,Revolve091,Revolve093]
FEATURE [Part::Cut] Cut037  label="casePillars003"
  Base = -> Fusion082
  Tool = -> Fusion081
FEATURE [Sketcher::SketchObject] Sketch051
  FullyConstrained = true
  Placement = pos=(117,19,0) rot=(0.57735,0.57735,0.57735;2.0944rad)
  sketch-geometry (48):
    g0: LineSegment StartX=-49.19 StartY=69.25 StartZ=0 EndX=-49.19 EndY=66.25 EndZ=0
    g1: LineSegment StartX=-49.19 StartY=63.5 StartZ=0 EndX=-49.19 EndY=60.5 EndZ=0
    g2: LineSegment StartX=-49.19 StartY=57.75 StartZ=0 EndX=-49.19 EndY=54.75 EndZ=0
    g3: LineSegment StartX=-49.19 StartY=52 StartZ=0 EndX=-49.19 EndY=49 EndZ=0
    g4: LineSegment StartX=-49.19 StartY=46.25 StartZ=0 EndX=-49.19 EndY=43.25 EndZ=0
    g5: LineSegment StartX=-49.19 StartY=40.5 StartZ=0 EndX=-49.19 EndY=37.5 EndZ=0
    g6: LineSegment StartX=-49.19 StartY=34.5 StartZ=0 EndX=-49.19 EndY=31.5 EndZ=0
    g7: LineSegment StartX=-49.19 StartY=28.75 StartZ=0 EndX=-49.19 EndY=25.75 EndZ=0
    g8: LineSegment StartX=-49.19 StartY=23 StartZ=0 EndX=-49.19 EndY=20 EndZ=0
    g9: LineSegment StartX=-49.19 StartY=17.25 StartZ=0 EndX=-49.19 EndY=14.25 EndZ=0
    g10: LineSegment StartX=-49.19 StartY=11.5 StartZ=0 EndX=-49.19 EndY=8.5 EndZ=0
    g11: LineSegment StartX=-49.19 StartY=5.75 StartZ=0 EndX=-49.19 EndY=2.75 EndZ=0
    g12: ArcOfCircle CenterX=-1.5 CenterY=67.75 CenterZ=0 NormalX=0 NormalY=0 NormalZ=1 AngleXU=0 Radius=1.5 StartAngle=4.71239 EndAngle=7.85398
    g13: ArcOfCircle CenterX=-1.5 CenterY=62 CenterZ=0 NormalX=0 NormalY=0 NormalZ=1 AngleXU=0 Radius=1.5 StartAngle=4.71239 EndAngle=7.85398
    g14: ArcOfCircle CenterX=-1.5 CenterY=56.25 CenterZ=0 NormalX=0 NormalY=0 NormalZ=1 AngleXU=0 Radius=1.5 StartAngle=4.71239 EndAngle=7.85398
    g15: ArcOfCircle CenterX=-11.49 CenterY=50.5 CenterZ=0 NormalX=0 NormalY=0 NormalZ=1 AngleXU=0 Radius=1.5 StartAngle=4.71239 EndAngle=7.85398
    g16: ArcOfCircle CenterX=-16.28 CenterY=44.75 CenterZ=0 NormalX=0 NormalY=0 NormalZ=1 AngleXU=0 Radius=1.5 StartAngle=4.71239 EndAngle=7.85398
    g17: ArcOfCircle CenterX=-18.2337 CenterY=39 CenterZ=0 NormalX=0 NormalY=0 NormalZ=1 AngleXU=0 Radius=1.5 StartAngle=4.71485 EndAngle=7.85398
    g18: ArcOfCircle CenterX=-16.2837 CenterY=27.25 CenterZ=0 NormalX=0 NormalY=0 NormalZ=1 AngleXU=0 Radius=1.5 StartAngle=4.71485 EndAngle=7.85398
    g19: ArcOfCircle CenterX=-18.2337 CenterY=33 CenterZ=0 NormalX=0 NormalY=0 NormalZ=1 AngleXU=0 Radius=1.5 StartAngle=4.71485 EndAngle=7.85398
    g20: ArcOfCircle CenterX=-11.49 CenterY=21.5 CenterZ=0 NormalX=0 NormalY=0 NormalZ=1 AngleXU=0 Radius=1.5 StartAngle=4.71239 EndAngle=7.85398
    g21: ArcOfCircle CenterX=-1.5 CenterY=4.25 CenterZ=0 NormalX=0 NormalY=0 NormalZ=1 AngleXU=0 Radius=1.5 StartAngle=4.71239 EndAngle=7.85398
    g22: ArcOfCircle CenterX=-1.5 CenterY=10 CenterZ=0 NormalX=0 NormalY=0 NormalZ=1 AngleXU=0 Radius=1.5 StartAngle=4.71239 EndAngle=7.85398
    g23: ArcOfCircle CenterX=-1.5 CenterY=15.75 CenterZ=0 NormalX=0 NormalY=0 NormalZ=1 AngleXU=0 Radius=1.5 StartAngle=4.71239 EndAngle=7.85398
    g24: LineSegment StartX=-49.19 StartY=69.25 StartZ=0 EndX=-1.5 EndY=69.25 EndZ=0
    g25: LineSegment StartX=-49.19 StartY=66.25 StartZ=0 EndX=-1.5 EndY=66.25 EndZ=0
    g26: LineSegment StartX=-49.19 StartY=63.5 StartZ=0 EndX=-1.5 EndY=63.5 EndZ=0
    g27: LineSegment StartX=-49.19 StartY=60.5 StartZ=0 EndX=-1.5 EndY=60.5 EndZ=0
    g28: LineSegment StartX=-49.19 StartY=57.75 StartZ=0 EndX=-1.5 EndY=57.75 EndZ=0
    g29: LineSegment StartX=-49.19 StartY=54.75 StartZ=0 EndX=-1.5 EndY=54.75 EndZ=0
    g30: LineSegment StartX=-49.19 StartY=52 StartZ=0 EndX=-11.49 EndY=52 EndZ=0
    g31: LineSegment StartX=-49.19 StartY=49 StartZ=0 EndX=-11.49 EndY=49 EndZ=0
    g32: LineSegment StartX=-49.19 StartY=46.25 StartZ=0 EndX=-16.28 EndY=46.25 EndZ=0
    g33: LineSegment StartX=-49.19 StartY=43.25 StartZ=0 EndX=-16.28 EndY=43.25 EndZ=0
    g34: LineSegment StartX=-49.19 StartY=40.5 StartZ=0 EndX=-18.2337 EndY=40.5 EndZ=0
    g35: LineSegment StartX=-49.19 StartY=37.5 StartZ=0 EndX=-18.23 EndY=37.5 EndZ=0
    g36: LineSegment StartX=-49.19 StartY=34.5 StartZ=0 EndX=-18.2337 EndY=34.5 EndZ=0
    g37: LineSegment StartX=-49.19 StartY=31.5 StartZ=0 EndX=-18.23 EndY=31.5 EndZ=0
    g38: LineSegment StartX=-49.19 StartY=28.75 StartZ=0 EndX=-16.2837 EndY=28.75 EndZ=0
    g39: LineSegment StartX=-49.19 StartY=25.75 StartZ=0 EndX=-16.28 EndY=25.75 EndZ=0
    g40: LineSegment StartX=-49.19 StartY=23 StartZ=0 EndX=-11.49 EndY=23 EndZ=0
    g41: LineSegment StartX=-49.19 StartY=20 StartZ=0 EndX=-11.49 EndY=20 EndZ=0
    g42: LineSegment StartX=-49.19 StartY=17.25 StartZ=0 EndX=-1.5 EndY=17.25 EndZ=0
    g43: LineSegment StartX=-49.19 StartY=14.25 StartZ=0 EndX=-1.5 EndY=14.25 EndZ=0
    g44: LineSegment StartX=-49.19 StartY=11.5 StartZ=0 EndX=-1.5 EndY=11.5 EndZ=0
    g45: LineSegment StartX=-49.19 StartY=8.5 StartZ=0 EndX=-1.5 EndY=8.5 EndZ=0
    g46: LineSegment StartX=-49.19 StartY=5.75 StartZ=0 EndX=-1.5 EndY=5.75 EndZ=0
    g47: LineSegment StartX=-49.19 StartY=2.75 StartZ=0 EndX=-1.5 EndY=2.75 EndZ=0
  constraints (120):
    c: Vertical(g0)
    c: Distance(g0) = 3
    c: Block(g0)
    c: Vertical(g1)
    c: Distance(g1) = 3
    c: Vertical(g2)
    c: Equal(g0,g2) = 3
    c: Block(g2)
    c: Vertical(g3)
    c: Equal(g1,g3) = 3
    c: Vertical(g4)
    c: Equal(g0,g4) = 3
    c: Block(g4)
    c: Vertical(g5)
    c: Equal(g1,g5) = 3
    c: Vertical(g6)
    c: Equal(g0,g6) = 3
    c: Block(g6)
    c: Vertical(g7)
    c: Equal(g1,g7) = 3
    c: Vertical(g8)
    c: Equal(g0,g8) = 3
    c: Block(g8)
    c: Vertical(g9)
    c: Equal(g1,g9) = 3
    c: Vertical(g10)
    c: Equal(g0,g10) = 3
    c: Block(g10)
    c: Vertical(g11)
    c: Equal(g1,g11) = 3
    c: Block(g12)
    c: Block(g13)
    c: Block(g14)
    c: Block(g15)
    c: Block(g16)
    c: Block(g17)
    c: Block(g18)
    c: Block(g19)
    c: Block(g20)
    c: Block(g21)
    c: Block(g22)
    c: Block(g23)
    c: Block(g11)
    c: Block(g9)
    c: Block(g7)
    c: Block(g5)
    c: Block(g3)
    c: Block(g1)
    c: Coincident(g24,g0)
    c: Coincident(g24,g12)
    c: Horizontal(g24)
    c: Coincident(g25,g0)
    c: Coincident(g25,g12)
    c: Horizontal(g25)
    c: Coincident(g26,g1)
    c: Coincident(g26,g13)
    c: Horizontal(g26)
    c: Coincident(g27,g1)
    c: Coincident(g27,g13)
    c: Horizontal(g27)
    c: Coincident(g28,g2)
    c: Coincident(g28,g14)
    c: Horizontal(g28)
    c: Coincident(g29,g2)
    c: Coincident(g29,g14)
    c: Horizontal(g29)
    c: Coincident(g30,g3)
    c: Coincident(g30,g15)
    c: Horizontal(g30)
    c: Coincident(g31,g3)
    c: Coincident(g31,g15)
    c: Horizontal(g31)
    c: Coincident(g32,g4)
    c: Coincident(g32,g16)
    c: Horizontal(g32)
    c: Coincident(g33,g4)
    c: Coincident(g33,g16)
    c: Horizontal(g33)
    c: Coincident(g34,g5)
    c: Coincident(g34,g17)
    c: Horizontal(g34)
    c: Coincident(g35,g5)
    c: Coincident(g35,g17)
    c: Horizontal(g35)
    c: Coincident(g36,g6)
    c: Coincident(g36,g19)
    c: Horizontal(g36)
    c: Coincident(g37,g6)
    c: Coincident(g37,g19)
    c: Horizontal(g37)
    c: Coincident(g38,g7)
    c: Coincident(g38,g18)
    c: Horizontal(g38)
    c: Coincident(g39,g7)
    c: Coincident(g39,g18)
    c: Horizontal(g39)
    c: Coincident(g40,g8)
    c: Coincident(g40,g20)
    c: Horizontal(g40)
    c: Coincident(g41,g8)
    c: Coincident(g41,g20)
    c: Horizontal(g41)
    c: Coincident(g42,g9)
    c: Coincident(g42,g23)
    c: Horizontal(g42)
    c: Coincident(g43,g9)
    c: Coincident(g43,g23)
    c: Horizontal(g43)
    c: Coincident(g44,g10)
    c: Coincident(g44,g22)
    c: Horizontal(g44)
    c: Coincident(g45,g10)
    c: Coincident(g45,g22)
    c: Horizontal(g45)
    c: Coincident(g46,g11)
    c: Coincident(g46,g21)
    c: Horizontal(g46)
    c: Coincident(g47,g11)
    c: Coincident(g47,g21)
    c: Horizontal(g47)
FEATURE [Part::Extrusion] Extrude042
  Base = -> Sketch051
  Dir = (1,-2e-16,2e-16)
  DirMode = 2
  FaceMakerClass = Part::FaceMakerBullseye
  LengthFwd = 19
  LengthRev = 0
  Placement = pos=(-19,0,0) rot=(0,0,1;0rad)
  Solid = true
  Symmetric = false
FEATURE [Part::Fillet] Fillet035  label="removeToCreateVentalationHoles"
  Base = -> Extrude042
  Edges = <same value as first occurrence — deduplicated (x6 in doc)>
  Placement = pos=(7,0,0) rot=(0,0,1;0rad)
FEATURE [Part::Cut] Cut038  label="top017"
  Base = -> Cut033
  Tool = -> Fillet035
FEATURE [Sketcher::SketchObject] Sketch052  label="bottomSketch001"
  FullyConstrained = true
  sketch-geometry (45):
    g0: LineSegment StartX=6.29999 StartY=8 StartZ=0 EndX=3.29999 EndY=8 EndZ=0
    g1: LineSegment StartX=3.29999 StartY=8 StartZ=0 EndX=3.29999 EndY=-6.03275e-07 EndZ=0
    g2: ArcOfCircle CenterX=8.29999 CenterY=5 CenterZ=0 NormalX=0 NormalY=0 NormalZ=1 AngleXU=0 Radius=2 StartAngle=3.14159 EndAngle=4.71239
    g3: LineSegment StartX=6.29999 StartY=8 StartZ=0 EndX=6.29999 EndY=5 EndZ=0
    g4: ArcOfCircle CenterX=105 CenterY=19 CenterZ=0 NormalX=0 NormalY=0 NormalZ=1 AngleXU=0 Radius=12.7 StartAngle=4.71239 EndAngle=5.94289
    g5-g11: Circle x7 (B-spline internal-alignment scaffolding for g12; pole/knot coordinates omitted)
    g12: BSplineCurve PolesCount=7 KnotsCount=5 Degree=3 IsPeriodic=0
    g13-g17: GeomPoint x5 (B-spline internal-alignment scaffolding for g12; pole/knot coordinates omitted)
    g18: ArcOfCircle CenterX=105 CenterY=19 CenterZ=0 NormalX=0 NormalY=0 NormalZ=1 AngleXU=0 Radius=15.7 StartAngle=5.81226 EndAngle=6.28319
    g19: BSplineCurve PolesCount=5 KnotsCount=3 Degree=3 IsPeriodic=0
    g20: LineSegment StartX=8.29999 StartY=3 StartZ=0 EndX=101.7 EndY=3 EndZ=0
    g21: LineSegment StartX=3.29999 StartY=-6.03275e-07 StartZ=0 EndX=105 EndY=-6.03275e-07 EndZ=0
    g22: LineSegment StartX=120.974 StartY=8.71251 StartZ=0 EndX=122.332 EndY=7.83778 EndZ=0
    g23: LineSegment StartX=105 StartY=-6.03274e-07 StartZ=0 EndX=113 EndY=-6.03274e-07 EndZ=0
    g24: ArcOfCircle CenterX=105 CenterY=19 CenterZ=0 NormalX=0 NormalY=0 NormalZ=1 AngleXU=0 Radius=20.6155 StartAngle=5.11091 EndAngle=5.71103
    g25: ArcOfCircle CenterX=117.7 CenterY=19 CenterZ=0 NormalX=0 NormalY=0 NormalZ=1 AngleXU=0 Radius=3 StartAngle=1.2e-15 EndAngle=2.10468
    g26: Circle CenterX=116.345 CenterY=16.3232 CenterZ=0 NormalX=0 NormalY=0 NormalZ=1 AngleXU=0 Radius=1
    g27: Circle CenterX=117.24 CenterY=15.7584 CenterZ=0 NormalX=0 NormalY=0 NormalZ=1 AngleXU=0 Radius=1
    g28: Circle CenterX=116.972 CenterY=14.7612 CenterZ=0 NormalX=0 NormalY=0 NormalZ=1 AngleXU=0 Radius=1
    g29: BSplineCurve PolesCount=3 KnotsCount=2 Degree=2 IsPeriodic=0
    g30: GeomPoint X=116.345 Y=16.3232 Z=0
    g31: GeomPoint X=116.972 Y=14.7612 Z=0
    g32: Circle CenterX=115.828 CenterY=17.157 CenterZ=0 NormalX=0 NormalY=0 NormalZ=1 AngleXU=0 Radius=1
    g33: Circle CenterX=115.841 CenterY=16.639 CenterZ=0 NormalX=0 NormalY=0 NormalZ=1 AngleXU=0 Radius=1
    g34: Circle CenterX=116.345 CenterY=16.3232 CenterZ=0 NormalX=0 NormalY=0 NormalZ=1 AngleXU=0 Radius=1
    g35: BSplineCurve PolesCount=3 KnotsCount=2 Degree=2 IsPeriodic=0
    g36: GeomPoint X=115.828 Y=17.157 Z=0
    g37: GeomPoint X=116.345 Y=16.3232 Z=0
    g38: LineSegment StartX=115.828 StartY=17.157 StartZ=0 EndX=115.828 EndY=20.8307 EndZ=0
    g39: Circle CenterX=115.828 CenterY=20.8307 CenterZ=0 NormalX=0 NormalY=0 NormalZ=1 AngleXU=0 Radius=1
    g40: Circle CenterX=115.831 CenterY=21.3396 CenterZ=0 NormalX=0 NormalY=0 NormalZ=1 AngleXU=0 Radius=1
    g41: Circle CenterX=116.173 CenterY=21.5825 CenterZ=0 NormalX=0 NormalY=0 NormalZ=1 AngleXU=0 Radius=1
    g42: BSplineCurve PolesCount=3 KnotsCount=2 Degree=2 IsPeriodic=0
    g43: GeomPoint X=115.828 Y=20.8307 Z=0
    g44: GeomPoint X=116.173 Y=21.5825 Z=0
  constraints (70):
    c: Horizontal(g0)
    c: Distance(g0) = 3
    c: Coincident(g1,g0)
    c: Vertical(g1)
    c: Block(g2)
    c: Block(g0)
    c: Coincident(g3,g0)
    c: Coincident(g3,g2)
    c: Vertical(g3)
    c: Block(g1)
    c: Block(g4)
    c: Coincident(g19,g4)
    c: Block(g19)
    c: Equal(g5, g6-g11) x6
    c: InternalAlignment(g5-g11 -> g12) x7
    c: InternalAlignment(g13-g17 -> g12) x5
    c: Block(g12)
    c: Coincident(g18,g12)
    c: Block(g18)
    c: Coincident(g20,g2)
    c: Coincident(g20,g19)
    c: Horizontal(g20)
    c: Distance(g20) = 93.4
    c: Coincident(g21,g1)
    c: Horizontal(g21)
    c: Distance(g21) = 101.7
    c: Horizontal(g23)
    c: Distance(g23) = 8
    c: Coincident(g24,g23)
    c: Block(g23)
    c: Coincident(g22,g24)
    c: Block(g24)
    c: Block(g22)
    c: Distance(g22) = 1.61553
    c: Coincident(g25,g18)
    c: Block(g25)
    c: Weight(g26) = 1
    c: Equal(g26,g27)
    c: Equal(g26,g28)
    c: Coincident(g29,g4)
    c: InternalAlignment(g26,g29)
    c: InternalAlignment(g27,g29)
    c: InternalAlignment(g28,g29)
    c: InternalAlignment(g30,g29)
    c: InternalAlignment(g31,g29)
    c: Block(g29)
    c: Weight(g32) = 1
    c: Equal(g32,g33)
    c: Equal(g32,g34)
    c: Coincident(g35,g29)
    c: InternalAlignment(g32,g35)
    c: InternalAlignment(g33,g35)
    c: InternalAlignment(g34,g35)
    c: InternalAlignment(g36,g35)
    c: InternalAlignment(g37,g35)
    c: Block(g35)
    c: Coincident(g38,g35)
    c: Vertical(g38)
    c: Block(g38)
    c: Coincident(g42,g38)
    c: Weight(g39) = 1
    c: Equal(g39,g40)
    c: Equal(g39,g41)
    c: Coincident(g42,g25)
    c: InternalAlignment(g39,g42)
    c: InternalAlignment(g40,g42)
    c: InternalAlignment(g41,g42)
    c: InternalAlignment(g43,g42)
    c: InternalAlignment(g44,g42)
    c: Block(g42)
FEATURE [Part::Extrusion] Extrude043  label="bottom010"
  Base = -> Sketch052
  Dir = (0,0,1)
  DirMode = 2
  FaceMakerClass = Part::FaceMakerBullseye
  LengthFwd = 71.4
  LengthRev = 0
  Placement = pos=(0,0,0.3) rot=(0,0,1;0rad)
  Solid = true
  Symmetric = false
FEATURE [Sketcher::SketchObject] Sketch053  label="topSketch013"
  FullyConstrained = true
  sketch-geometry (22):
    g0: LineSegment StartX=5.21097e-06 StartY=3 StartZ=0 EndX=5.21097e-06 EndY=19 EndZ=0
    g1: ArcOfCircle CenterX=19 CenterY=19 CenterZ=0 NormalX=0 NormalY=0 NormalZ=1 AngleXU=0 Radius=19 StartAngle=1.5708 EndAngle=3.14159
    g2: ArcOfCircle CenterX=19 CenterY=19 CenterZ=0 NormalX=0 NormalY=0 NormalZ=1 AngleXU=0 Radius=16 StartAngle=1.5708 EndAngle=3.14159
    g3: LineSegment StartX=114 StartY=35 StartZ=0 EndX=19 EndY=35 EndZ=0
    g4: LineSegment StartX=5.21097e-06 StartY=3 StartZ=0 EndX=5.21097e-06 EndY=0 EndZ=0
    g5: LineSegment StartX=3 StartY=0 StartZ=0 EndX=5.21097e-06 EndY=0 EndZ=0
    g6: LineSegment StartX=3 StartY=19 StartZ=0 EndX=3 EndY=0 EndZ=0
    g7: LineSegment StartX=19 StartY=38 StartZ=0 EndX=124 EndY=38 EndZ=0
    g8: Circle CenterX=119 CenterY=35 CenterZ=0 NormalX=0 NormalY=0 NormalZ=1 AngleXU=0 Radius=1
    g9: Circle CenterX=121 CenterY=35 CenterZ=0 NormalX=0 NormalY=0 NormalZ=1 AngleXU=0 Radius=1
    g10: Circle CenterX=121 CenterY=33 CenterZ=0 NormalX=0 NormalY=0 NormalZ=1 AngleXU=0 Radius=1
    g11: BSplineCurve PolesCount=3 KnotsCount=2 Degree=2 IsPeriodic=0
    g12: GeomPoint X=119 Y=35 Z=0
    g13: GeomPoint X=121 Y=33 Z=0
    g14: LineSegment StartX=119 StartY=35 StartZ=0 EndX=114 EndY=35 EndZ=0
    g15: ArcOfCircle CenterX=105 CenterY=19 CenterZ=0 NormalX=0 NormalY=0 NormalZ=1 AngleXU=0 Radius=16 StartAngle=5.60905 EndAngle=6.28319
    g16: LineSegment StartX=121 StartY=33 StartZ=0 EndX=121 EndY=19 EndZ=0
    g17: LineSegment StartX=117.5 StartY=9.01251 StartZ=0 EndX=121.163 EndY=9.0125 EndZ=0
    g18: ArcOfCircle CenterX=105 CenterY=19 CenterZ=0 NormalX=0 NormalY=0 NormalZ=1 AngleXU=0 Radius=20.6155 StartAngle=5.7297 EndAngle=6.28319
    g19: LineSegment StartX=121.163 StartY=9.0125 StartZ=0 EndX=122.538 EndY=8.16329 EndZ=0
    g20: LineSegment StartX=124 StartY=38 StartZ=0 EndX=125.616 EndY=38 EndZ=0
    g21: LineSegment StartX=125.616 StartY=19 StartZ=0 EndX=125.616 EndY=38 EndZ=0
  constraints (50):
    c: Vertical(g0)
    c: Block(g0)
    c: Coincident(g1,g0)
    c: Block(g1)
    c: Coincident(g2,g1)
    c: Block(g2)
    c: Coincident(g3,g2)
    c: Horizontal(g3)
    c: Tangent(g3,g2)
    c: Coincident(g4,g0)
    c: Distance(g4) = 3
    c: Vertical(g4)
    c: Coincident(g5,g4)
    c: Horizontal(g5)
    c: Coincident(g6,g2)
    c: Coincident(g6,g5)
    c: Vertical(g6)
    c: Horizontal(g7)
    c: Distance(g7) = 105
    c: Coincident(g7,g1)
    c: Block(g3)
    c: Weight(g8) = 1
    c: Equal(g8,g9)
    c: Equal(g8,g10)
    c: InternalAlignment(g8,g11)
    c: InternalAlignment(g9,g11)
    c: InternalAlignment(g10,g11)
    c: InternalAlignment(g12,g11)
    c: InternalAlignment(g13,g11)
    c: Block(g11)
    c: Coincident(g14,g11)
    c: Coincident(g14,g3)
    c: Horizontal(g14)
    c: Block(g15)
    c: Coincident(g16,g11)
    c: Coincident(g16,g15)
    c: Vertical(g16)
    c: Distance(g16) = 14
    c: Coincident(g17,g15)
    c: Block(g18)
    c: Coincident(g19,g18)
    c: Coincident(g20,g7)
    c: Horizontal(g20)
    c: Vertical(g21)
    c: Coincident(g20,g21)
    c: Block(g20)
    c: Block(g21)
    c: Block(g19)
    c: Block(g17)
    c: Distance(g20) = 1.61553
FEATURE [Part::Extrusion] Extrude044
  Base = -> Sketch053
  Dir = (0,0,1)
  DirMode = 2
  FaceMakerClass = Part::FaceMakerBullseye
  LengthFwd = 72
  LengthRev = 0
  Solid = true
  Symmetric = false
FEATURE [Part::Fillet] Fillet036  label="top018"
  Base = -> Extrude044
  Edges = 1 edges r=2: [Edge41]
FEATURE [Sketcher::SketchObject] Sketch054
  FullyConstrained = false
  Placement = pos=(0,0,0) rot=(1,0,0;1.5708rad)
  sketch-geometry (24):
    g0: ArcOfCircle CenterX=-4 CenterY=-10.5 CenterZ=0 NormalX=0 NormalY=0 NormalZ=1 AngleXU=0 Radius=1.5 StartAngle=6e-16 EndAngle=3.14159
    g1: ArcOfCircle CenterX=-34.2 CenterY=-10.5 CenterZ=0 NormalX=0 NormalY=0 NormalZ=1 AngleXU=0 Radius=1.5 StartAngle=0 EndAngle=3.14159
    g2: ArcOfCircle CenterX=-34.2 CenterY=-27.7 CenterZ=0 NormalX=0 NormalY=0 NormalZ=1 AngleXU=0 Radius=1.5 StartAngle=3.14159 EndAngle=6.28319
    g3: ArcOfCircle CenterX=-4 CenterY=-27.7 CenterZ=0 NormalX=0 NormalY=0 NormalZ=1 AngleXU=0 Radius=1.5 StartAngle=3.1416 EndAngle=6.28319
    g4: ArcOfCircle CenterX=-10 CenterY=-4.3 CenterZ=0 NormalX=0 NormalY=0 NormalZ=1 AngleXU=0 Radius=1.5 StartAngle=2e-16 EndAngle=3.14159
    g5: ArcOfCircle CenterX=-16.1 CenterY=-1.8 CenterZ=0 NormalX=0 NormalY=0 NormalZ=1 AngleXU=0 Radius=1.5 StartAngle=5e-16 EndAngle=3.14159
    g6: ArcOfCircle CenterX=-22.1 CenterY=-1.8 CenterZ=0 NormalX=0 NormalY=0 NormalZ=1 AngleXU=0 Radius=1.5 StartAngle=5e-16 EndAngle=3.14159
    g7: ArcOfCircle CenterX=-28.2 CenterY=-4.3 CenterZ=0 NormalX=0 NormalY=0 NormalZ=1 AngleXU=0 Radius=1.5 StartAngle=2e-16 EndAngle=3.14159
    g8: ArcOfCircle CenterX=-10 CenterY=-33.9 CenterZ=0 NormalX=0 NormalY=0 NormalZ=1 AngleXU=0 Radius=1.5 StartAngle=3.14159 EndAngle=6.28319
    g9: ArcOfCircle CenterX=-16.1 CenterY=-36.4 CenterZ=0 NormalX=0 NormalY=0 NormalZ=1 AngleXU=0 Radius=1.5 StartAngle=3.14159 EndAngle=6.28319
    g10: ArcOfCircle CenterX=-22.1 CenterY=-36.4 CenterZ=0 NormalX=0 NormalY=0 NormalZ=1 AngleXU=0 Radius=1.5 StartAngle=3.14159 EndAngle=6.28319
    g11: ArcOfCircle CenterX=-28.2 CenterY=-33.9 CenterZ=0 NormalX=0 NormalY=0 NormalZ=1 AngleXU=0 Radius=1.5 StartAngle=3.14159 EndAngle=6.28319
    g12: LineSegment StartX=-35.7 StartY=-10.5 StartZ=0 EndX=-35.7 EndY=-27.7 EndZ=0
    g13: LineSegment StartX=-32.7 StartY=-10.5 StartZ=0 EndX=-32.7 EndY=-27.7 EndZ=0
    g14: LineSegment StartX=-29.7 StartY=-33.9 StartZ=0 EndX=-29.7 EndY=-4.3 EndZ=0
    g15: LineSegment StartX=-26.7 StartY=-33.9 StartZ=0 EndX=-26.7 EndY=-4.3 EndZ=0
    g16: LineSegment StartX=-2.5 StartY=-10.5 StartZ=0 EndX=-2.5 EndY=-27.7 EndZ=0
    g17: LineSegment StartX=-8.5 StartY=-4.3 StartZ=0 EndX=-8.5 EndY=-33.9 EndZ=0
    g18: LineSegment StartX=-5.5 StartY=-10.5 StartZ=0 EndX=-5.5 EndY=-27.7 EndZ=0
    g19: LineSegment StartX=-11.5 StartY=-4.3 StartZ=0 EndX=-11.5 EndY=-33.9 EndZ=0
    g20: LineSegment StartX=-14.6 StartY=-1.8 StartZ=0 EndX=-14.6 EndY=-36.4 EndZ=0
    g21: LineSegment StartX=-17.6 StartY=-1.8 StartZ=0 EndX=-17.6 EndY=-36.4 EndZ=0
    g22: LineSegment StartX=-20.6 StartY=-36.4 StartZ=0 EndX=-20.6 EndY=-1.8 EndZ=0
    g23: LineSegment StartX=-23.6 StartY=-1.8 StartZ=0 EndX=-23.6 EndY=-36.4 EndZ=0
  constraints (48):
    c: Block(g0)
    c: Block(g1)
    c: Block(g2)
    c: Block(g3)
    c: Block(g4)
    c: Block(g5)
    c: Block(g6)
    c: Block(g7)
    c: Block(g8)
    c: Block(g9)
    c: Block(g10)
    c: Block(g11)
    c: Coincident(g12,g1)
    c: Coincident(g12,g2)
    c: Vertical(g12)
    c: Coincident(g13,g1)
    c: Coincident(g13,g2)
    c: Vertical(g13)
    c: Coincident(g14,g11)
    c: Coincident(g14,g7)
    c: Vertical(g14)
    c: Coincident(g15,g11)
    c: Coincident(g15,g7)
    c: Vertical(g15)
    c: Coincident(g16,g0)
    c: Coincident(g16,g3)
    c: Vertical(g16)
    c: Coincident(g17,g4)
    c: Coincident(g17,g8)
    c: Vertical(g17)
    c: Coincident(g18,g0)
    c: Coincident(g18,g3)
    c: Vertical(g18)
    c: Coincident(g19,g4)
    c: Coincident(g19,g8)
    c: Vertical(g19)
    c: Coincident(g20,g5)
    c: Coincident(g20,g9)
    c: Vertical(g20)
    c: Coincident(g21,g5)
    c: Coincident(g21,g9)
    c: Vertical(g21)
    c: Coincident(g22,g10)
    c: Coincident(g22,g6)
    c: Vertical(g22)
    c: Coincident(g23,g6)
    c: Coincident(g23,g10)
    c: Vertical(g23)
FEATURE [Part::Extrusion] Extrude045  label="removeToCreateFanGrillHoles003"
  Base = -> Sketch054
  Dir = (0,-1,6e-16)
  DirMode = 2
  FaceMakerClass = Part::FaceMakerBullseye
  LengthFwd = 10
  LengthRev = 0
  Placement = pos=(65.4,44,54.82) rot=(0,0,1;0rad)
  Solid = true
  Symmetric = false
FEATURE [Part::Feature] Face105 .. Face108  x4 (patterned run collapsed; names and placements below)
  shape: bbox 3.5 x 17.8 x 2e-07 mm, 1 faces, 0 solids (baked)
FEATURE [Part::Revolution] Revolve113  label="removeToCreateScrewAndThreadedInsertHole041"
  Angle = 360
  Axis = (0,1,0)
  Base = (0,0,0)
  FaceMakerClass = Part::FaceMakerBullseye
  Placement = pos=(62.3,30.3,19.7) rot=(0,0,1;0rad)
  Solid = false
  Source = -> Face105
  Symmetric = false
FEATURE [Part::Revolution] Revolve114  label="removeToCreateScrewAndThreadedInsertHole042"
  Angle = 360
  Axis = (0,1,0)
  Base = (0,0,0)
  FaceMakerClass = Part::FaceMakerBullseye
  Placement = pos=(62.3,30.3,51.7) rot=(0,0,1;0rad)
  Solid = false
  Source = -> Face106
  Symmetric = false
FEATURE [Part::Revolution] Revolve115  label="removeToCreateScrewAndThreadedInsertHole043"
  Angle = 360
  Axis = (0,1,0)
  Base = (0,0,0)
  FaceMakerClass = Part::FaceMakerBullseye
  Placement = pos=(30.3,30.3,19.7) rot=(0,0,1;0rad)
  Solid = false
  Source = -> Face107
  Symmetric = false
FEATURE [Part::Revolution] Revolve116  label="removeToCreateScrewAndThreadedInsertHole044"
  Angle = 360
  Axis = (0,1,0)
  Base = (0,0,0)
  FaceMakerClass = Part::FaceMakerBullseye
  Placement = pos=(30.3,30.3,51.7) rot=(0,0,1;0rad)
  Solid = false
  Source = -> Face108
  Symmetric = false
FEATURE [Part::MultiFuse] Fusion083  label="createThreadedInsertHolesForFan004"
  Shapes = -> [Revolve113,Revolve114,Revolve115,Revolve116]
FEATURE [Part::Box] Box024  label="removeToCreteHoleForPlugHousing026"
  AttacherType = Attacher::AttachEngine3D
  Height = 28.6
  Length = 10
  Placement = pos=(-2,0,21.7) rot=(0,0,1;0rad)
  Width = 19
FEATURE [Part::Cylinder] Cylinder038  label="removeToCreteHoleForPlugHousing027"
  Angle = 360
  AttacherType = Attacher::AttachEngine3D
  Height = 20
  Placement = pos=(-2,19,36) rot=(0,1,0;1.5708rad)
  Radius = 14.3
FEATURE [Part::MultiFuse] Fusion084  label="removeToCreteHoleForPlugHousing028"
  Shapes = -> [Box024,Cylinder038]
FEATURE [Part::Cylinder] Cylinder039
  Angle = 360
  AttacherType = Attacher::AttachEngine3D
  Height = 20
  Placement = pos=(0,0,36.15) rot=(0,0,1;0rad)
  Radius = 14.3
FEATURE [Part::Cylinder] Cylinder040
  Angle = 360
  AttacherType = Attacher::AttachEngine3D
  Height = 10
  Placement = pos=(0,0,36.15) rot=(0,0,1;0rad)
  Radius = 4
FEATURE [Part::Box] Box025  label="removeToCreteHoleForPlugHousing030"
  AttacherType = Attacher::AttachEngine3D
  Height = 28.6
  Length = 20
  Placement = pos=(106.15,0,21.7) rot=(0,0,1;0rad)
  Width = 19
FEATURE [Part::MultiFuse] Fusion086  label="removeToCreteHoleForPlugHousing031"
  Placement = pos=(70,19,36) rot=(0,1,0;1.5708rad)
  Shapes = -> [Cylinder039,Cylinder040]
FEATURE [Part::MultiFuse] Fusion085  label="removeToCreteHoleForPlugHousing029"
  Shapes = -> [Box025,Fusion086]
FEATURE [Sketcher::SketchObject] Sketch055
  FullyConstrained = true
  Placement = pos=(117,19,0) rot=(0.57735,0.57735,0.57735;2.0944rad)
  sketch-geometry (48):
    g0: LineSegment StartX=-49.19 StartY=69.25 StartZ=0 EndX=-49.19 EndY=66.25 EndZ=0
    g1: LineSegment StartX=-49.19 StartY=63.5 StartZ=0 EndX=-49.19 EndY=60.5 EndZ=0
    g2: LineSegment StartX=-49.19 StartY=57.75 StartZ=0 EndX=-49.19 EndY=54.75 EndZ=0
    g3: LineSegment StartX=-49.19 StartY=52 StartZ=0 EndX=-49.19 EndY=49 EndZ=0
    g4: LineSegment StartX=-49.19 StartY=46.25 StartZ=0 EndX=-49.19 EndY=43.25 EndZ=0
    g5: LineSegment StartX=-49.19 StartY=40.5 StartZ=0 EndX=-49.19 EndY=37.5 EndZ=0
    g6: LineSegment StartX=-49.19 StartY=34.5 StartZ=0 EndX=-49.19 EndY=31.5 EndZ=0
    g7: LineSegment StartX=-49.19 StartY=28.75 StartZ=0 EndX=-49.19 EndY=25.75 EndZ=0
    g8: LineSegment StartX=-49.19 StartY=23 StartZ=0 EndX=-49.19 EndY=20 EndZ=0
    g9: LineSegment StartX=-49.19 StartY=17.25 StartZ=0 EndX=-49.19 EndY=14.25 EndZ=0
    g10: LineSegment StartX=-49.19 StartY=11.5 StartZ=0 EndX=-49.19 EndY=8.5 EndZ=0
    g11: LineSegment StartX=-49.19 StartY=5.75 StartZ=0 EndX=-49.19 EndY=2.75 EndZ=0
    g12: ArcOfCircle CenterX=-1.5 CenterY=67.75 CenterZ=0 NormalX=0 NormalY=0 NormalZ=1 AngleXU=0 Radius=1.5 StartAngle=4.71239 EndAngle=7.85398
    g13: ArcOfCircle CenterX=-1.5 CenterY=62 CenterZ=0 NormalX=0 NormalY=0 NormalZ=1 AngleXU=0 Radius=1.5 StartAngle=4.71239 EndAngle=7.85398
    g14: ArcOfCircle CenterX=-1.5 CenterY=56.25 CenterZ=0 NormalX=0 NormalY=0 NormalZ=1 AngleXU=0 Radius=1.5 StartAngle=4.71239 EndAngle=7.85398
    g15: ArcOfCircle CenterX=-11.49 CenterY=50.5 CenterZ=0 NormalX=0 NormalY=0 NormalZ=1 AngleXU=0 Radius=1.5 StartAngle=4.71239 EndAngle=7.85398
    g16: ArcOfCircle CenterX=-16.28 CenterY=44.75 CenterZ=0 NormalX=0 NormalY=0 NormalZ=1 AngleXU=0 Radius=1.5 StartAngle=4.71239 EndAngle=7.85398
    g17: ArcOfCircle CenterX=-18.2337 CenterY=39 CenterZ=0 NormalX=0 NormalY=0 NormalZ=1 AngleXU=0 Radius=1.5 StartAngle=4.71485 EndAngle=7.85398
    g18: ArcOfCircle CenterX=-16.2837 CenterY=27.25 CenterZ=0 NormalX=0 NormalY=0 NormalZ=1 AngleXU=0 Radius=1.5 StartAngle=4.71485 EndAngle=7.85398
    g19: ArcOfCircle CenterX=-18.2337 CenterY=33 CenterZ=0 NormalX=0 NormalY=0 NormalZ=1 AngleXU=0 Radius=1.5 StartAngle=4.71485 EndAngle=7.85398
    g20: ArcOfCircle CenterX=-11.49 CenterY=21.5 CenterZ=0 NormalX=0 NormalY=0 NormalZ=1 AngleXU=0 Radius=1.5 StartAngle=4.71239 EndAngle=7.85398
    g21: ArcOfCircle CenterX=-1.5 CenterY=4.25 CenterZ=0 NormalX=0 NormalY=0 NormalZ=1 AngleXU=0 Radius=1.5 StartAngle=4.71239 EndAngle=7.85398
    g22: ArcOfCircle CenterX=-1.5 CenterY=10 CenterZ=0 NormalX=0 NormalY=0 NormalZ=1 AngleXU=0 Radius=1.5 StartAngle=4.71239 EndAngle=7.85398
    g23: ArcOfCircle CenterX=-1.5 CenterY=15.75 CenterZ=0 NormalX=0 NormalY=0 NormalZ=1 AngleXU=0 Radius=1.5 StartAngle=4.71239 EndAngle=7.85398
    g24: LineSegment StartX=-49.19 StartY=69.25 StartZ=0 EndX=-1.5 EndY=69.25 EndZ=0
    g25: LineSegment StartX=-49.19 StartY=66.25 StartZ=0 EndX=-1.5 EndY=66.25 EndZ=0
    g26: LineSegment StartX=-49.19 StartY=63.5 StartZ=0 EndX=-1.5 EndY=63.5 EndZ=0
    g27: LineSegment StartX=-49.19 StartY=60.5 StartZ=0 EndX=-1.5 EndY=60.5 EndZ=0
    g28: LineSegment StartX=-49.19 StartY=57.75 StartZ=0 EndX=-1.5 EndY=57.75 EndZ=0
    g29: LineSegment StartX=-49.19 StartY=54.75 StartZ=0 EndX=-1.5 EndY=54.75 EndZ=0
    g30: LineSegment StartX=-49.19 StartY=52 StartZ=0 EndX=-11.49 EndY=52 EndZ=0
    g31: LineSegment StartX=-49.19 StartY=49 StartZ=0 EndX=-11.49 EndY=49 EndZ=0
    g32: LineSegment StartX=-49.19 StartY=46.25 StartZ=0 EndX=-16.28 EndY=46.25 EndZ=0
    g33: LineSegment StartX=-49.19 StartY=43.25 StartZ=0 EndX=-16.28 EndY=43.25 EndZ=0
    g34: LineSegment StartX=-49.19 StartY=40.5 StartZ=0 EndX=-18.2337 EndY=40.5 EndZ=0
    g35: LineSegment StartX=-49.19 StartY=37.5 StartZ=0 EndX=-18.23 EndY=37.5 EndZ=0
    g36: LineSegment StartX=-49.19 StartY=34.5 StartZ=0 EndX=-18.2337 EndY=34.5 EndZ=0
    g37: LineSegment StartX=-49.19 StartY=31.5 StartZ=0 EndX=-18.23 EndY=31.5 EndZ=0
    g38: LineSegment StartX=-49.19 StartY=28.75 StartZ=0 EndX=-16.2837 EndY=28.75 EndZ=0
    g39: LineSegment StartX=-49.19 StartY=25.75 StartZ=0 EndX=-16.28 EndY=25.75 EndZ=0
    g40: LineSegment StartX=-49.19 StartY=23 StartZ=0 EndX=-11.49 EndY=23 EndZ=0
    g41: LineSegment StartX=-49.19 StartY=20 StartZ=0 EndX=-11.49 EndY=20 EndZ=0
    g42: LineSegment StartX=-49.19 StartY=17.25 StartZ=0 EndX=-1.5 EndY=17.25 EndZ=0
    g43: LineSegment StartX=-49.19 StartY=14.25 StartZ=0 EndX=-1.5 EndY=14.25 EndZ=0
    g44: LineSegment StartX=-49.19 StartY=11.5 StartZ=0 EndX=-1.5 EndY=11.5 EndZ=0
    g45: LineSegment StartX=-49.19 StartY=8.5 StartZ=0 EndX=-1.5 EndY=8.5 EndZ=0
    g46: LineSegment StartX=-49.19 StartY=5.75 StartZ=0 EndX=-1.5 EndY=5.75 EndZ=0
    g47: LineSegment StartX=-49.19 StartY=2.75 StartZ=0 EndX=-1.5 EndY=2.75 EndZ=0
  constraints (120):
    c: Vertical(g0)
    c: Distance(g0) = 3
    c: Block(g0)
    c: Vertical(g1)
    c: Distance(g1) = 3
    c: Vertical(g2)
    c: Equal(g0,g2) = 3
    c: Block(g2)
    c: Vertical(g3)
    c: Equal(g1,g3) = 3
    c: Vertical(g4)
    c: Equal(g0,g4) = 3
    c: Block(g4)
    c: Vertical(g5)
    c: Equal(g1,g5) = 3
    c: Vertical(g6)
    c: Equal(g0,g6) = 3
    c: Block(g6)
    c: Vertical(g7)
    c: Equal(g1,g7) = 3
    c: Vertical(g8)
    c: Equal(g0,g8) = 3
    c: Block(g8)
    c: Vertical(g9)
    c: Equal(g1,g9) = 3
    c: Vertical(g10)
    c: Equal(g0,g10) = 3
    c: Block(g10)
    c: Vertical(g11)
    c: Equal(g1,g11) = 3
    c: Block(g12)
    c: Block(g13)
    c: Block(g14)
    c: Block(g15)
    c: Block(g16)
    c: Block(g17)
    c: Block(g18)
    c: Block(g19)
    c: Block(g20)
    c: Block(g21)
    c: Block(g22)
    c: Block(g23)
    c: Block(g11)
    c: Block(g9)
    c: Block(g7)
    c: Block(g5)
    c: Block(g3)
    c: Block(g1)
    c: Coincident(g24,g0)
    c: Coincident(g24,g12)
    c: Horizontal(g24)
    c: Coincident(g25,g0)
    c: Coincident(g25,g12)
    c: Horizontal(g25)
    c: Coincident(g26,g1)
    c: Coincident(g26,g13)
    c: Horizontal(g26)
    c: Coincident(g27,g1)
    c: Coincident(g27,g13)
    c: Horizontal(g27)
    c: Coincident(g28,g2)
    c: Coincident(g28,g14)
    c: Horizontal(g28)
    c: Coincident(g29,g2)
    c: Coincident(g29,g14)
    c: Horizontal(g29)
    c: Coincident(g30,g3)
    c: Coincident(g30,g15)
    c: Horizontal(g30)
    c: Coincident(g31,g3)
    c: Coincident(g31,g15)
    c: Horizontal(g31)
    c: Coincident(g32,g4)
    c: Coincident(g32,g16)
    c: Horizontal(g32)
    c: Coincident(g33,g4)
    c: Coincident(g33,g16)
    c: Horizontal(g33)
    c: Coincident(g34,g5)
    c: Coincident(g34,g17)
    c: Horizontal(g34)
    c: Coincident(g35,g5)
    c: Coincident(g35,g17)
    c: Horizontal(g35)
    c: Coincident(g36,g6)
    c: Coincident(g36,g19)
    c: Horizontal(g36)
    c: Coincident(g37,g6)
    c: Coincident(g37,g19)
    c: Horizontal(g37)
    c: Coincident(g38,g7)
    c: Coincident(g38,g18)
    c: Horizontal(g38)
    c: Coincident(g39,g7)
    c: Coincident(g39,g18)
    c: Horizontal(g39)
    c: Coincident(g40,g8)
    c: Coincident(g40,g20)
    c: Horizontal(g40)
    c: Coincident(g41,g8)
    c: Coincident(g41,g20)
    c: Horizontal(g41)
    c: Coincident(g42,g9)
    c: Coincident(g42,g23)
    c: Horizontal(g42)
    c: Coincident(g43,g9)
    c: Coincident(g43,g23)
    c: Horizontal(g43)
    c: Coincident(g44,g10)
    c: Coincident(g44,g22)
    c: Horizontal(g44)
    c: Coincident(g45,g10)
    c: Coincident(g45,g22)
    c: Horizontal(g45)
    c: Coincident(g46,g11)
    c: Coincident(g46,g21)
    c: Horizontal(g46)
    c: Coincident(g47,g11)
    c: Coincident(g47,g21)
    c: Horizontal(g47)
FEATURE [Part::Extrusion] Extrude046
  Base = -> Sketch055
  Dir = (1,0,0)
  DirMode = 2
  FaceMakerClass = Part::FaceMakerBullseye
  LengthFwd = 23
  LengthRev = 0
  Placement = pos=(-19,0,0) rot=(0,0,1;0rad)
  Solid = true
  Symmetric = false
FEATURE [Part::Fillet] Fillet038  label="removeToCreateVentalationHoles001"
  Base = -> Extrude046
  Edges = <same value as first occurrence — deduplicated (x6 in doc)>
  Placement = pos=(7,0,0) rot=(0,0,1;0rad)
FEATURE [Sketcher::SketchObject] Sketch056  label="topSketch014"
  FullyConstrained = true
  sketch-geometry (22):
    g0: LineSegment StartX=5.21097e-06 StartY=3 StartZ=0 EndX=5.21097e-06 EndY=19 EndZ=0
    g1: ArcOfCircle CenterX=19 CenterY=19 CenterZ=0 NormalX=0 NormalY=0 NormalZ=1 AngleXU=0 Radius=19 StartAngle=1.5708 EndAngle=3.14159
    g2: ArcOfCircle CenterX=19 CenterY=19 CenterZ=0 NormalX=0 NormalY=0 NormalZ=1 AngleXU=0 Radius=16 StartAngle=1.5708 EndAngle=3.14159
    g3: LineSegment StartX=114 StartY=35 StartZ=0 EndX=19 EndY=35 EndZ=0
    g4: LineSegment StartX=5.21097e-06 StartY=3 StartZ=0 EndX=5.21097e-06 EndY=0 EndZ=0
    g5: LineSegment StartX=3 StartY=0 StartZ=0 EndX=5.21097e-06 EndY=0 EndZ=0
    g6: LineSegment StartX=3 StartY=19 StartZ=0 EndX=3 EndY=0 EndZ=0
    g7: LineSegment StartX=19 StartY=38 StartZ=0 EndX=124 EndY=38 EndZ=0
    g8: Circle CenterX=119 CenterY=35 CenterZ=0 NormalX=0 NormalY=0 NormalZ=1 AngleXU=0 Radius=1
    g9: Circle CenterX=121 CenterY=35 CenterZ=0 NormalX=0 NormalY=0 NormalZ=1 AngleXU=0 Radius=1
    g10: Circle CenterX=121 CenterY=33 CenterZ=0 NormalX=0 NormalY=0 NormalZ=1 AngleXU=0 Radius=1
    g11: BSplineCurve PolesCount=3 KnotsCount=2 Degree=2 IsPeriodic=0
    g12: GeomPoint X=119 Y=35 Z=0
    g13: GeomPoint X=121 Y=33 Z=0
    g14: LineSegment StartX=119 StartY=35 StartZ=0 EndX=114 EndY=35 EndZ=0
    g15: ArcOfCircle CenterX=105 CenterY=19 CenterZ=0 NormalX=0 NormalY=0 NormalZ=1 AngleXU=0 Radius=16 StartAngle=5.60905 EndAngle=6.28319
    g16: LineSegment StartX=121 StartY=33 StartZ=0 EndX=121 EndY=19 EndZ=0
    g17: LineSegment StartX=117.5 StartY=9.01251 StartZ=0 EndX=121.163 EndY=9.0125 EndZ=0
    g18: ArcOfCircle CenterX=105 CenterY=19 CenterZ=0 NormalX=0 NormalY=0 NormalZ=1 AngleXU=0 Radius=20.6155 StartAngle=5.7297 EndAngle=6.28319
    g19: LineSegment StartX=121.163 StartY=9.0125 StartZ=0 EndX=122.538 EndY=8.16329 EndZ=0
    g20: LineSegment StartX=124 StartY=38 StartZ=0 EndX=125.616 EndY=38 EndZ=0
    g21: LineSegment StartX=125.616 StartY=19 StartZ=0 EndX=125.616 EndY=38 EndZ=0
  constraints (49):
    c: Vertical(g0)
    c: Block(g0)
    c: Coincident(g1,g0)
    c: Block(g1)
    c: Coincident(g2,g1)
    c: Block(g2)
    c: Coincident(g3,g2)
    c: Horizontal(g3)
    c: Tangent(g3,g2)
    c: Coincident(g4,g0)
    c: Distance(g4) = 3
    c: Vertical(g4)
    c: Coincident(g5,g4)
    c: Horizontal(g5)
    c: Coincident(g6,g2)
    c: Coincident(g6,g5)
    c: Vertical(g6)
    c: Horizontal(g7)
    c: Distance(g7) = 105
    c: Coincident(g7,g1)
    c: Block(g3)
    c: Weight(g8) = 1
    c: Equal(g8,g9)
    c: Equal(g8,g10)
    c: InternalAlignment(g8,g11)
    c: InternalAlignment(g9,g11)
    c: InternalAlignment(g10,g11)
    c: InternalAlignment(g12,g11)
    c: InternalAlignment(g13,g11)
    c: Block(g11)
    c: Coincident(g14,g11)
    c: Coincident(g14,g3)
    c: Horizontal(g14)
    c: Block(g15)
    c: Coincident(g16,g11)
    c: Coincident(g16,g15)
    c: Vertical(g16)
    c: Distance(g16) = 14
    c: Coincident(g17,g15)
    c: Block(g18)
    c: Coincident(g19,g18)
    c: Coincident(g20,g7)
    c: Horizontal(g20)
    c: Vertical(g21)
    c: Coincident(g20,g21)
    c: Block(g20)
    c: Block(g21)
    c: Block(g19)
    c: Block(g17)
FEATURE [Part::Box] Box026  label="removeToCreteHoleForPlugHousing032"
  AttacherType = Attacher::AttachEngine3D
  Height = 28.6
  Length = 10
  Placement = pos=(-2,0,21.7) rot=(0,0,1;0rad)
  Width = 19
FEATURE [Part::Feature] Face109 .. Face112  x4 (patterned run collapsed; names and placements below)
  shape: bbox 3.5 x 17.8 x 2e-07 mm, 1 faces, 0 solids (baked)
FEATURE [Part::Revolution] Revolve117  label="removeToCreateScrewAndThreadedInsertHole045"
  Angle = 360
  Axis = (0,1,0)
  Base = (0,0,0)
  FaceMakerClass = Part::FaceMakerBullseye
  Placement = pos=(62.3,30.3,19.7) rot=(0,0,1;0rad)
  Solid = false
  Source = -> Face109
  Symmetric = false
FEATURE [Part::Revolution] Revolve118  label="removeToCreateScrewAndThreadedInsertHole046"
  Angle = 360
  Axis = (0,1,0)
  Base = (0,0,0)
  FaceMakerClass = Part::FaceMakerBullseye
  Placement = pos=(62.3,30.3,51.7) rot=(0,0,1;0rad)
  Solid = false
  Source = -> Face110
  Symmetric = false
FEATURE [Part::Revolution] Revolve119  label="removeToCreateScrewAndThreadedInsertHole047"
  Angle = 360
  Axis = (0,1,0)
  Base = (0,0,0)
  FaceMakerClass = Part::FaceMakerBullseye
  Placement = pos=(30.3,30.3,19.7) rot=(0,0,1;0rad)
  Solid = false
  Source = -> Face111
  Symmetric = false
FEATURE [Part::Revolution] Revolve120  label="removeToCreateScrewAndThreadedInsertHole048"
  Angle = 360
  Axis = (0,1,0)
  Base = (0,0,0)
  FaceMakerClass = Part::FaceMakerBullseye
  Placement = pos=(30.3,30.3,51.7) rot=(0,0,1;0rad)
  Solid = false
  Source = -> Face112
  Symmetric = false
FEATURE [Part::MultiFuse] Fusion087  label="createThreadedInsertHolesForFan005"
  Shapes = -> [Revolve117,Revolve118,Revolve119,Revolve120]
FEATURE [Part::Extrusion] Extrude047
  Base = -> Sketch056
  Dir = (0,0,1)
  DirMode = 2
  FaceMakerClass = Part::FaceMakerBullseye
  LengthFwd = 72
  LengthRev = 0
  Solid = true
  Symmetric = false
FEATURE [Part::Fillet] Fillet039  label="top019"
  Base = -> Extrude047
  Edges = 1 edges r=2: [Edge35]
FEATURE [Sketcher::SketchObject] Sketch057
  FullyConstrained = false
  Placement = pos=(0,0,0) rot=(1,0,0;1.5708rad)
  sketch-geometry (24):
    g0: ArcOfCircle CenterX=-4 CenterY=-10.5 CenterZ=0 NormalX=0 NormalY=0 NormalZ=1 AngleXU=0 Radius=1.5 StartAngle=6e-16 EndAngle=3.14159
    g1: ArcOfCircle CenterX=-34.2 CenterY=-10.5 CenterZ=0 NormalX=0 NormalY=0 NormalZ=1 AngleXU=0 Radius=1.5 StartAngle=0 EndAngle=3.14159
    g2: ArcOfCircle CenterX=-34.2 CenterY=-27.7 CenterZ=0 NormalX=0 NormalY=0 NormalZ=1 AngleXU=0 Radius=1.5 StartAngle=3.14159 EndAngle=6.28319
    g3: ArcOfCircle CenterX=-4 CenterY=-27.7 CenterZ=0 NormalX=0 NormalY=0 NormalZ=1 AngleXU=0 Radius=1.5 StartAngle=3.1416 EndAngle=6.28319
    g4: ArcOfCircle CenterX=-10 CenterY=-4.3 CenterZ=0 NormalX=0 NormalY=0 NormalZ=1 AngleXU=0 Radius=1.5 StartAngle=2e-16 EndAngle=3.14159
    g5: ArcOfCircle CenterX=-16.1 CenterY=-1.8 CenterZ=0 NormalX=0 NormalY=0 NormalZ=1 AngleXU=0 Radius=1.5 StartAngle=5e-16 EndAngle=3.14159
    g6: ArcOfCircle CenterX=-22.1 CenterY=-1.8 CenterZ=0 NormalX=0 NormalY=0 NormalZ=1 AngleXU=0 Radius=1.5 StartAngle=5e-16 EndAngle=3.14159
    g7: ArcOfCircle CenterX=-28.2 CenterY=-4.3 CenterZ=0 NormalX=0 NormalY=0 NormalZ=1 AngleXU=0 Radius=1.5 StartAngle=2e-16 EndAngle=3.14159
    g8: ArcOfCircle CenterX=-10 CenterY=-33.9 CenterZ=0 NormalX=0 NormalY=0 NormalZ=1 AngleXU=0 Radius=1.5 StartAngle=3.14159 EndAngle=6.28319
    g9: ArcOfCircle CenterX=-16.1 CenterY=-36.4 CenterZ=0 NormalX=0 NormalY=0 NormalZ=1 AngleXU=0 Radius=1.5 StartAngle=3.14159 EndAngle=6.28319
    g10: ArcOfCircle CenterX=-22.1 CenterY=-36.4 CenterZ=0 NormalX=0 NormalY=0 NormalZ=1 AngleXU=0 Radius=1.5 StartAngle=3.14159 EndAngle=6.28319
    g11: ArcOfCircle CenterX=-28.2 CenterY=-33.9 CenterZ=0 NormalX=0 NormalY=0 NormalZ=1 AngleXU=0 Radius=1.5 StartAngle=3.14159 EndAngle=6.28319
    g12: LineSegment StartX=-35.7 StartY=-10.5 StartZ=0 EndX=-35.7 EndY=-27.7 EndZ=0
    g13: LineSegment StartX=-32.7 StartY=-10.5 StartZ=0 EndX=-32.7 EndY=-27.7 EndZ=0
    g14: LineSegment StartX=-29.7 StartY=-33.9 StartZ=0 EndX=-29.7 EndY=-4.3 EndZ=0
    g15: LineSegment StartX=-26.7 StartY=-33.9 StartZ=0 EndX=-26.7 EndY=-4.3 EndZ=0
    g16: LineSegment StartX=-2.5 StartY=-10.5 StartZ=0 EndX=-2.5 EndY=-27.7 EndZ=0
    g17: LineSegment StartX=-8.5 StartY=-4.3 StartZ=0 EndX=-8.5 EndY=-33.9 EndZ=0
    g18: LineSegment StartX=-5.5 StartY=-10.5 StartZ=0 EndX=-5.5 EndY=-27.7 EndZ=0
    g19: LineSegment StartX=-11.5 StartY=-4.3 StartZ=0 EndX=-11.5 EndY=-33.9 EndZ=0
    g20: LineSegment StartX=-14.6 StartY=-1.8 StartZ=0 EndX=-14.6 EndY=-36.4 EndZ=0
    g21: LineSegment StartX=-17.6 StartY=-1.8 StartZ=0 EndX=-17.6 EndY=-36.4 EndZ=0
    g22: LineSegment StartX=-20.6 StartY=-36.4 StartZ=0 EndX=-20.6 EndY=-1.8 EndZ=0
    g23: LineSegment StartX=-23.6 StartY=-1.8 StartZ=0 EndX=-23.6 EndY=-36.4 EndZ=0
  constraints (48):
    c: Block(g0)
    c: Block(g1)
    c: Block(g2)
    c: Block(g3)
    c: Block(g4)
    c: Block(g5)
    c: Block(g6)
    c: Block(g7)
    c: Block(g8)
    c: Block(g9)
    c: Block(g10)
    c: Block(g11)
    c: Coincident(g12,g1)
    c: Coincident(g12,g2)
    c: Vertical(g12)
    c: Coincident(g13,g1)
    c: Coincident(g13,g2)
    c: Vertical(g13)
    c: Coincident(g14,g11)
    c: Coincident(g14,g7)
    c: Vertical(g14)
    c: Coincident(g15,g11)
    c: Coincident(g15,g7)
    c: Vertical(g15)
    c: Coincident(g16,g0)
    c: Coincident(g16,g3)
    c: Vertical(g16)
    c: Coincident(g17,g4)
    c: Coincident(g17,g8)
    c: Vertical(g17)
    c: Coincident(g18,g0)
    c: Coincident(g18,g3)
    c: Vertical(g18)
    c: Coincident(g19,g4)
    c: Coincident(g19,g8)
    c: Vertical(g19)
    c: Coincident(g20,g5)
    c: Coincident(g20,g9)
    c: Vertical(g20)
    c: Coincident(g21,g5)
    c: Coincident(g21,g9)
    c: Vertical(g21)
    c: Coincident(g22,g10)
    c: Coincident(g22,g6)
    c: Vertical(g22)
    c: Coincident(g23,g6)
    c: Coincident(g23,g10)
    c: Vertical(g23)
FEATURE [Part::Extrusion] Extrude048  label="removeToCreateFanGrillHoles004"
  Base = -> Sketch057
  Dir = (0,-1,6e-16)
  DirMode = 2
  FaceMakerClass = Part::FaceMakerBullseye
  LengthFwd = 10
  LengthRev = 0
  Placement = pos=(65.4,44,54.82) rot=(0,0,1;0rad)
  Solid = true
  Symmetric = false
FEATURE [Part::Cut] Cut040  label="top021"
  Base = -> Fillet039
  Tool = -> Extrude048
FEATURE [Part::Cylinder] Cylinder041  label="removeToCreteHoleForPlugHousing034"
  Angle = 360
  AttacherType = Attacher::AttachEngine3D
  Height = 20
  Placement = pos=(-2,19,36) rot=(0,1,0;1.5708rad)
  Radius = 14.3
FEATURE [Part::MultiFuse] Fusion089  label="removeToCreteHoleForPlugHousing035"
  Shapes = -> [Box026,Cylinder041]
FEATURE [Part::Cylinder] Cylinder042
  Angle = 360
  AttacherType = Attacher::AttachEngine3D
  Height = 20
  Placement = pos=(0,0,36.15) rot=(0,0,1;0rad)
  Radius = 14.3
FEATURE [Part::Cylinder] Cylinder043
  Angle = 360
  AttacherType = Attacher::AttachEngine3D
  Height = 10
  Placement = pos=(0,0,36.15) rot=(0,0,1;0rad)
  Radius = 4
FEATURE [Part::Box] Box027  label="removeToCreteHoleForPlugHousing036"
  AttacherType = Attacher::AttachEngine3D
  Height = 28.6
  Length = 20
  Placement = pos=(106.15,0,21.7) rot=(0,0,1;0rad)
  Width = 19
FEATURE [Part::Cut] Cut041  label="top022"
  Base = -> Cut040
  Tool = -> Fusion087
FEATURE [Part::Cut] Cut039  label="top020"
  Base = -> Cut041
  Tool = -> Fusion089
FEATURE [Part::MultiFuse] Fusion090  label="removeToCreteHoleForPlugHousing037"
  Placement = pos=(70,19,36) rot=(0,1,0;1.5708rad)
  Shapes = -> [Cylinder042,Cylinder043]
FEATURE [Part::MultiFuse] Fusion088  label="removeToCreteHoleForPlugHousing033"
  Shapes = -> [Box027,Fusion090]
FEATURE [Part::Cut] Cut042  label="removeToCreteHoleForPlugHousing038"
  Base = -> Cut039
  Tool = -> Fusion088
FEATURE [Part::MultiFuse] Fusion091  label="removeFromTop"
  Shapes = -> [Fillet038,Fusion085,Fusion084,Fusion083,Extrude045]
FEATURE [Part::Cut] Cut043  label="REAL TOP ====="
  Base = -> Fillet036
  Tool = -> Fusion091
FEATURE [Part::MultiFuse] Fusion092  label="caseScrewPillarBracket016"
  Shapes = -> [Extrude030,Extrude031,Extrude032,Extrude033,Extrude034,Extrude035,Extrude036,Extrude037,Box013,Box014]
FEATURE [Sketcher::SketchObject] Sketch058  label="topSketch015"
  FullyConstrained = true
  sketch-geometry (20):
    g0: LineSegment StartX=5.21097e-06 StartY=3 StartZ=0 EndX=5.21097e-06 EndY=19 EndZ=0
    g1: ArcOfCircle CenterX=19 CenterY=19 CenterZ=0 NormalX=0 NormalY=0 NormalZ=1 AngleXU=0 Radius=19 StartAngle=1.5708 EndAngle=3.14159
    g2: ArcOfCircle CenterX=19 CenterY=19 CenterZ=0 NormalX=0 NormalY=0 NormalZ=1 AngleXU=0 Radius=16 StartAngle=1.5708 EndAngle=3.14159
    g3: LineSegment StartX=114 StartY=35 StartZ=0 EndX=19 EndY=35 EndZ=0
    g4: LineSegment StartX=5.21097e-06 StartY=3 StartZ=0 EndX=5.21097e-06 EndY=0 EndZ=0
    g5: LineSegment StartX=3 StartY=0 StartZ=0 EndX=5.21097e-06 EndY=0 EndZ=0
    g6: LineSegment StartX=3 StartY=19 StartZ=0 EndX=3 EndY=0 EndZ=0
    g7: LineSegment StartX=19 StartY=38 StartZ=0 EndX=124 EndY=38 EndZ=0
    g8: Circle CenterX=119 CenterY=35 CenterZ=0 NormalX=0 NormalY=0 NormalZ=1 AngleXU=0 Radius=1
    g9: Circle CenterX=121 CenterY=35 CenterZ=0 NormalX=0 NormalY=0 NormalZ=1 AngleXU=0 Radius=1
    g10: Circle CenterX=121 CenterY=33 CenterZ=0 NormalX=0 NormalY=0 NormalZ=1 AngleXU=0 Radius=1
    g11: BSplineCurve PolesCount=3 KnotsCount=2 Degree=2 IsPeriodic=0
    g12: GeomPoint X=119 Y=35 Z=0
    g13: GeomPoint X=121 Y=33 Z=0
    g14: LineSegment StartX=119 StartY=35 StartZ=0 EndX=114 EndY=35 EndZ=0
    g15: ArcOfCircle CenterX=105 CenterY=19 CenterZ=0 NormalX=0 NormalY=0 NormalZ=1 AngleXU=0 Radius=19 StartAngle=5.7297 EndAngle=6.28319
    g16: ArcOfCircle CenterX=105 CenterY=19 CenterZ=0 NormalX=0 NormalY=0 NormalZ=1 AngleXU=0 Radius=16 StartAngle=5.60905 EndAngle=6.28319
    g17: LineSegment StartX=121 StartY=33 StartZ=0 EndX=121 EndY=19 EndZ=0
    g18: LineSegment StartX=124 StartY=38 StartZ=0 EndX=124 EndY=19 EndZ=0
    g19: LineSegment StartX=117.5 StartY=9.01251 StartZ=0 EndX=121.163 EndY=9.0125 EndZ=0
  constraints (46):
    c: Vertical(g0)
    c: Block(g0)
    c: Coincident(g1,g0)
    c: Block(g1)
    c: Coincident(g2,g1)
    c: Block(g2)
    c: Coincident(g3,g2)
    c: Horizontal(g3)
    c: Tangent(g3,g2)
    c: Coincident(g4,g0)
    c: Distance(g4) = 3
    c: Vertical(g4)
    c: Coincident(g5,g4)
    c: Horizontal(g5)
    c: Coincident(g6,g2)
    c: Coincident(g6,g5)
    c: Vertical(g6)
    c: Horizontal(g7)
    c: Distance(g7) = 105
    c: Coincident(g7,g1)
    c: Block(g3)
    c: Weight(g8) = 1
    c: Equal(g8,g9)
    c: Equal(g8,g10)
    c: InternalAlignment(g8,g11)
    c: InternalAlignment(g9,g11)
    c: InternalAlignment(g10,g11)
    c: InternalAlignment(g12,g11)
    c: InternalAlignment(g13,g11)
    c: Block(g11)
    c: Coincident(g14,g11)
    c: Coincident(g14,g3)
    c: Horizontal(g14)
    c: Block(g15)
    c: Coincident(g16,g15)
    c: Block(g16)
    c: Coincident(g17,g11)
    c: Coincident(g17,g16)
    c: Vertical(g17)
    c: Distance(g17) = 14
    c: Coincident(g18,g7)
    c: Coincident(g18,g15)
    c: Vertical(g18)
    c: Distance(g18) = 19
    c: Coincident(g19,g16)
    c: Coincident(g19,g15)
FEATURE [Part::Extrusion] Extrude049  label="top023"
  Base = -> Sketch058
  Dir = (0,0,1)
  DirMode = 2
  FaceMakerClass = Part::FaceMakerBullseye
  LengthFwd = 72
  LengthRev = 0
  Solid = true
  Symmetric = false
FEATURE [Sketcher::SketchObject] Sketch059
  FullyConstrained = true
  MapMode = 3
  Placement = pos=(0,0,0) rot=(1,0,0;1.5708rad)
  Support = -> [Extrude049]
  sketch-geometry (8):
    g0: Circle CenterX=80.351 CenterY=-67.6202 CenterZ=0 NormalX=0 NormalY=0 NormalZ=1 AngleXU=0 Radius=2
    g1: Circle CenterX=80.351 CenterY=-67.6202 CenterZ=0 NormalX=0 NormalY=0 NormalZ=1 AngleXU=0 Radius=3
    g2: Circle CenterX=80.351 CenterY=-4.92017 CenterZ=0 NormalX=0 NormalY=0 NormalZ=1 AngleXU=0 Radius=2
    g3: Circle CenterX=80.351 CenterY=-4.92017 CenterZ=0 NormalX=0 NormalY=0 NormalZ=1 AngleXU=0 Radius=3
    g4: Circle CenterX=23.851 CenterY=-4.92017 CenterZ=0 NormalX=0 NormalY=0 NormalZ=1 AngleXU=0 Radius=2
    g5: Circle CenterX=23.851 CenterY=-4.92017 CenterZ=0 NormalX=0 NormalY=0 NormalZ=1 AngleXU=0 Radius=3
    g6: Circle CenterX=23.851 CenterY=-67.6202 CenterZ=0 NormalX=0 NormalY=0 NormalZ=1 AngleXU=0 Radius=2
    g7: Circle CenterX=23.851 CenterY=-67.6202 CenterZ=0 NormalX=0 NormalY=0 NormalZ=1 AngleXU=0 Radius=3
  constraints (8):
    c: Block(g3)
    c: Block(g2)
    c: Block(g1)
    c: Block(g0)
    c: Block(g6)
    c: Block(g7)
    c: Block(g4)
    c: Block(g5)
FEATURE [Sketcher::SketchObject] Sketch060
  FullyConstrained = true
  MapMode = 3
  Placement = pos=(0,0,0) rot=(1,0,0;1.5708rad)
  Support = -> [Extrude049]
  sketch-geometry (8):
    g0: Circle CenterX=80.351 CenterY=-67.6202 CenterZ=0 NormalX=0 NormalY=0 NormalZ=1 AngleXU=0 Radius=3
    g1: Circle CenterX=80.351 CenterY=-4.92017 CenterZ=0 NormalX=0 NormalY=0 NormalZ=1 AngleXU=0 Radius=3
    g2: Circle CenterX=23.851 CenterY=-4.92017 CenterZ=0 NormalX=0 NormalY=0 NormalZ=1 AngleXU=0 Radius=3
    g3: Circle CenterX=23.851 CenterY=-67.6202 CenterZ=0 NormalX=0 NormalY=0 NormalZ=1 AngleXU=0 Radius=3
    g4: Circle CenterX=23.851 CenterY=-67.6202 CenterZ=0 NormalX=0 NormalY=0 NormalZ=1 AngleXU=0 Radius=5
    g5: Circle CenterX=80.351 CenterY=-67.6202 CenterZ=0 NormalX=0 NormalY=0 NormalZ=1 AngleXU=0 Radius=5
    g6: Circle CenterX=23.851 CenterY=-4.92017 CenterZ=0 NormalX=0 NormalY=0 NormalZ=1 AngleXU=0 Radius=5
    g7: Circle CenterX=80.351 CenterY=-4.92017 CenterZ=0 NormalX=0 NormalY=0 NormalZ=1 AngleXU=0 Radius=5
  constraints (8):
    c: Block(g1)
    c: Block(g0)
    c: Block(g3)
    c: Block(g2)
    c: Block(g5)
    c: Block(g4)
    c: Block(g6)
    c: Block(g7)
FEATURE [Sketcher::SketchObject] Sketch061
  FullyConstrained = true
  MapMode = 3
  Placement = pos=(0,0,0) rot=(1,0,0;1.5708rad)
  sketch-geometry (8):
    g0: Circle CenterX=80.351 CenterY=-67.6202 CenterZ=0 NormalX=0 NormalY=0 NormalZ=1 AngleXU=0 Radius=3
    g1: Circle CenterX=80.351 CenterY=-4.92017 CenterZ=0 NormalX=0 NormalY=0 NormalZ=1 AngleXU=0 Radius=3
    g2: Circle CenterX=23.851 CenterY=-4.92017 CenterZ=0 NormalX=0 NormalY=0 NormalZ=1 AngleXU=0 Radius=3
    g3: Circle CenterX=23.851 CenterY=-67.6202 CenterZ=0 NormalX=0 NormalY=0 NormalZ=1 AngleXU=0 Radius=3
    g4: Circle CenterX=23.851 CenterY=-67.6202 CenterZ=0 NormalX=0 NormalY=0 NormalZ=1 AngleXU=0 Radius=5
    g5: Circle CenterX=80.351 CenterY=-67.6202 CenterZ=0 NormalX=0 NormalY=0 NormalZ=1 AngleXU=0 Radius=5
    g6: Circle CenterX=23.851 CenterY=-4.92017 CenterZ=0 NormalX=0 NormalY=0 NormalZ=1 AngleXU=0 Radius=5
    g7: Circle CenterX=80.351 CenterY=-4.92017 CenterZ=0 NormalX=0 NormalY=0 NormalZ=1 AngleXU=0 Radius=5
  constraints (8):
    c: Block(g1)
    c: Block(g0)
    c: Block(g3)
    c: Block(g2)
    c: Block(g5)
    c: Block(g4)
    c: Block(g6)
    c: Block(g7)
FEATURE [Sketcher::SketchObject] Sketch062  label="topSketch016"
  FullyConstrained = true
  sketch-geometry (20):
    g0: LineSegment StartX=5.21097e-06 StartY=3 StartZ=0 EndX=5.21097e-06 EndY=19 EndZ=0
    g1: ArcOfCircle CenterX=19 CenterY=19 CenterZ=0 NormalX=0 NormalY=0 NormalZ=1 AngleXU=0 Radius=19 StartAngle=1.5708 EndAngle=3.14159
    g2: ArcOfCircle CenterX=19 CenterY=19 CenterZ=0 NormalX=0 NormalY=0 NormalZ=1 AngleXU=0 Radius=16 StartAngle=1.5708 EndAngle=3.14159
    g3: LineSegment StartX=114 StartY=35 StartZ=0 EndX=19 EndY=35 EndZ=0
    g4: LineSegment StartX=5.21097e-06 StartY=3 StartZ=0 EndX=5.21097e-06 EndY=0 EndZ=0
    g5: LineSegment StartX=3 StartY=0 StartZ=0 EndX=5.21097e-06 EndY=0 EndZ=0
    g6: LineSegment StartX=3 StartY=19 StartZ=0 EndX=3 EndY=0 EndZ=0
    g7: LineSegment StartX=19 StartY=38 StartZ=0 EndX=124 EndY=38 EndZ=0
    g8: Circle CenterX=119 CenterY=35 CenterZ=0 NormalX=0 NormalY=0 NormalZ=1 AngleXU=0 Radius=1
    g9: Circle CenterX=121 CenterY=35 CenterZ=0 NormalX=0 NormalY=0 NormalZ=1 AngleXU=0 Radius=1
    g10: Circle CenterX=121 CenterY=33 CenterZ=0 NormalX=0 NormalY=0 NormalZ=1 AngleXU=0 Radius=1
    g11: BSplineCurve PolesCount=3 KnotsCount=2 Degree=2 IsPeriodic=0
    g12: GeomPoint X=119 Y=35 Z=0
    g13: GeomPoint X=121 Y=33 Z=0
    g14: LineSegment StartX=119 StartY=35 StartZ=0 EndX=114 EndY=35 EndZ=0
    g15: ArcOfCircle CenterX=105 CenterY=19 CenterZ=0 NormalX=0 NormalY=0 NormalZ=1 AngleXU=0 Radius=19 StartAngle=5.7297 EndAngle=6.28319
    g16: ArcOfCircle CenterX=105 CenterY=19 CenterZ=0 NormalX=0 NormalY=0 NormalZ=1 AngleXU=0 Radius=16 StartAngle=5.60905 EndAngle=6.28319
    g17: LineSegment StartX=121 StartY=33 StartZ=0 EndX=121 EndY=19 EndZ=0
    g18: LineSegment StartX=124 StartY=38 StartZ=0 EndX=124 EndY=19 EndZ=0
    g19: LineSegment StartX=117.5 StartY=9.01251 StartZ=0 EndX=121.163 EndY=9.0125 EndZ=0
  constraints (46):
    c: Vertical(g0)
    c: Block(g0)
    c: Coincident(g1,g0)
    c: Block(g1)
    c: Coincident(g2,g1)
    c: Block(g2)
    c: Coincident(g3,g2)
    c: Horizontal(g3)
    c: Tangent(g3,g2)
    c: Coincident(g4,g0)
    c: Distance(g4) = 3
    c: Vertical(g4)
    c: Coincident(g5,g4)
    c: Horizontal(g5)
    c: Coincident(g6,g2)
    c: Coincident(g6,g5)
    c: Vertical(g6)
    c: Horizontal(g7)
    c: Distance(g7) = 105
    c: Coincident(g7,g1)
    c: Block(g3)
    c: Weight(g8) = 1
    c: Equal(g8,g9)
    c: Equal(g8,g10)
    c: InternalAlignment(g8,g11)
    c: InternalAlignment(g9,g11)
    c: InternalAlignment(g10,g11)
    c: InternalAlignment(g12,g11)
    c: InternalAlignment(g13,g11)
    c: Block(g11)
    c: Coincident(g14,g11)
    c: Coincident(g14,g3)
    c: Horizontal(g14)
    c: Block(g15)
    c: Coincident(g16,g15)
    c: Block(g16)
    c: Coincident(g17,g11)
    c: Coincident(g17,g16)
    c: Vertical(g17)
    c: Distance(g17) = 14
    c: Coincident(g18,g7)
    c: Coincident(g18,g15)
    c: Vertical(g18)
    c: Distance(g18) = 19
    c: Coincident(g19,g16)
    c: Coincident(g19,g15)
FEATURE [Part::Extrusion] Extrude053  label="top024"
  Base = -> Sketch062
  Dir = (0,0,1)
  DirMode = 2
  FaceMakerClass = Part::FaceMakerBullseye
  LengthFwd = 72
  LengthRev = 0
  Solid = true
  Symmetric = false
FEATURE [Sketcher::SketchObject] Sketch063
  FullyConstrained = true
  MapMode = 3
  Placement = pos=(0,0,0) rot=(1,0,0;1.5708rad)
  Support = -> [Extrude053]
  sketch-geometry (8):
    g0: Circle CenterX=80.351 CenterY=-67.6202 CenterZ=0 NormalX=0 NormalY=0 NormalZ=1 AngleXU=0 Radius=2
    g1: Circle CenterX=80.351 CenterY=-67.6202 CenterZ=0 NormalX=0 NormalY=0 NormalZ=1 AngleXU=0 Radius=3
    g2: Circle CenterX=80.351 CenterY=-4.92017 CenterZ=0 NormalX=0 NormalY=0 NormalZ=1 AngleXU=0 Radius=2
    g3: Circle CenterX=80.351 CenterY=-4.92017 CenterZ=0 NormalX=0 NormalY=0 NormalZ=1 AngleXU=0 Radius=3
    g4: Circle CenterX=23.851 CenterY=-4.92017 CenterZ=0 NormalX=0 NormalY=0 NormalZ=1 AngleXU=0 Radius=2
    g5: Circle CenterX=23.851 CenterY=-4.92017 CenterZ=0 NormalX=0 NormalY=0 NormalZ=1 AngleXU=0 Radius=3
    g6: Circle CenterX=23.851 CenterY=-67.6202 CenterZ=0 NormalX=0 NormalY=0 NormalZ=1 AngleXU=0 Radius=2
    g7: Circle CenterX=23.851 CenterY=-67.6202 CenterZ=0 NormalX=0 NormalY=0 NormalZ=1 AngleXU=0 Radius=3
  constraints (8):
    c: Block(g3)
    c: Block(g2)
    c: Block(g1)
    c: Block(g0)
    c: Block(g6)
    c: Block(g7)
    c: Block(g4)
    c: Block(g5)
FEATURE [Part::Extrusion] Extrude054
  Base = -> Sketch063
  Dir = (0,-1,2e-16)
  DirMode = 2
  FaceMakerClass = Part::FaceMakerBullseye
  LengthFwd = 6
  LengthRev = 0
  Placement = pos=(0,9,0) rot=(0,0,1;0rad)
  Solid = true
  Symmetric = false
FEATURE [Sketcher::SketchObject] Sketch064  label="topSketch017"
  FullyConstrained = true
  sketch-geometry (20):
    g0: LineSegment StartX=5.21097e-06 StartY=3 StartZ=0 EndX=5.21097e-06 EndY=19 EndZ=0
    g1: ArcOfCircle CenterX=19 CenterY=19 CenterZ=0 NormalX=0 NormalY=0 NormalZ=1 AngleXU=0 Radius=19 StartAngle=1.5708 EndAngle=3.14159
    g2: ArcOfCircle CenterX=19 CenterY=19 CenterZ=0 NormalX=0 NormalY=0 NormalZ=1 AngleXU=0 Radius=16 StartAngle=1.5708 EndAngle=3.14159
    g3: LineSegment StartX=114 StartY=35 StartZ=0 EndX=19 EndY=35 EndZ=0
    g4: LineSegment StartX=5.21097e-06 StartY=3 StartZ=0 EndX=5.21097e-06 EndY=0 EndZ=0
    g5: LineSegment StartX=3 StartY=0 StartZ=0 EndX=5.21097e-06 EndY=0 EndZ=0
    g6: LineSegment StartX=3 StartY=19 StartZ=0 EndX=3 EndY=0 EndZ=0
    g7: LineSegment StartX=19 StartY=38 StartZ=0 EndX=124 EndY=38 EndZ=0
    g8: Circle CenterX=119 CenterY=35 CenterZ=0 NormalX=0 NormalY=0 NormalZ=1 AngleXU=0 Radius=1
    g9: Circle CenterX=121 CenterY=35 CenterZ=0 NormalX=0 NormalY=0 NormalZ=1 AngleXU=0 Radius=1
    g10: Circle CenterX=121 CenterY=33 CenterZ=0 NormalX=0 NormalY=0 NormalZ=1 AngleXU=0 Radius=1
    g11: BSplineCurve PolesCount=3 KnotsCount=2 Degree=2 IsPeriodic=0
    g12: GeomPoint X=119 Y=35 Z=0
    g13: GeomPoint X=121 Y=33 Z=0
    g14: LineSegment StartX=119 StartY=35 StartZ=0 EndX=114 EndY=35 EndZ=0
    g15: ArcOfCircle CenterX=105 CenterY=19 CenterZ=0 NormalX=0 NormalY=0 NormalZ=1 AngleXU=0 Radius=19 StartAngle=5.7297 EndAngle=6.28319
    g16: ArcOfCircle CenterX=105 CenterY=19 CenterZ=0 NormalX=0 NormalY=0 NormalZ=1 AngleXU=0 Radius=16 StartAngle=5.60905 EndAngle=6.28319
    g17: LineSegment StartX=121 StartY=33 StartZ=0 EndX=121 EndY=19 EndZ=0
    g18: LineSegment StartX=124 StartY=38 StartZ=0 EndX=124 EndY=19 EndZ=0
    g19: LineSegment StartX=117.5 StartY=9.01251 StartZ=0 EndX=121.163 EndY=9.0125 EndZ=0
  constraints (46):
    c: Vertical(g0)
    c: Block(g0)
    c: Coincident(g1,g0)
    c: Block(g1)
    c: Coincident(g2,g1)
    c: Block(g2)
    c: Coincident(g3,g2)
    c: Horizontal(g3)
    c: Tangent(g3,g2)
    c: Coincident(g4,g0)
    c: Distance(g4) = 3
    c: Vertical(g4)
    c: Coincident(g5,g4)
    c: Horizontal(g5)
    c: Coincident(g6,g2)
    c: Coincident(g6,g5)
    c: Vertical(g6)
    c: Horizontal(g7)
    c: Distance(g7) = 105
    c: Coincident(g7,g1)
    c: Block(g3)
    c: Weight(g8) = 1
    c: Equal(g8,g9)
    c: Equal(g8,g10)
    c: InternalAlignment(g8,g11)
    c: InternalAlignment(g9,g11)
    c: InternalAlignment(g10,g11)
    c: InternalAlignment(g12,g11)
    c: InternalAlignment(g13,g11)
    c: Block(g11)
    c: Coincident(g14,g11)
    c: Coincident(g14,g3)
    c: Horizontal(g14)
    c: Block(g15)
    c: Coincident(g16,g15)
    c: Block(g16)
    c: Coincident(g17,g11)
    c: Coincident(g17,g16)
    c: Vertical(g17)
    c: Distance(g17) = 14
    c: Coincident(g18,g7)
    c: Coincident(g18,g15)
    c: Vertical(g18)
    c: Distance(g18) = 19
    c: Coincident(g19,g16)
    c: Coincident(g19,g15)
FEATURE [Sketcher::SketchObject] Sketch065
  FullyConstrained = true
  MapMode = 3
  Placement = pos=(0,0,0) rot=(1,0,0;1.5708rad)
  sketch-geometry (8):
    g0: Circle CenterX=80.351 CenterY=-67.6202 CenterZ=0 NormalX=0 NormalY=0 NormalZ=1 AngleXU=0 Radius=3
    g1: Circle CenterX=80.351 CenterY=-4.92017 CenterZ=0 NormalX=0 NormalY=0 NormalZ=1 AngleXU=0 Radius=3
    g2: Circle CenterX=23.851 CenterY=-4.92017 CenterZ=0 NormalX=0 NormalY=0 NormalZ=1 AngleXU=0 Radius=3
    g3: Circle CenterX=23.851 CenterY=-67.6202 CenterZ=0 NormalX=0 NormalY=0 NormalZ=1 AngleXU=0 Radius=3
    g4: Circle CenterX=23.851 CenterY=-67.6202 CenterZ=0 NormalX=0 NormalY=0 NormalZ=1 AngleXU=0 Radius=5
    g5: Circle CenterX=80.351 CenterY=-67.6202 CenterZ=0 NormalX=0 NormalY=0 NormalZ=1 AngleXU=0 Radius=5
    g6: Circle CenterX=23.851 CenterY=-4.92017 CenterZ=0 NormalX=0 NormalY=0 NormalZ=1 AngleXU=0 Radius=5
    g7: Circle CenterX=80.351 CenterY=-4.92017 CenterZ=0 NormalX=0 NormalY=0 NormalZ=1 AngleXU=0 Radius=5
  constraints (8):
    c: Block(g1)
    c: Block(g0)
    c: Block(g3)
    c: Block(g2)
    c: Block(g5)
    c: Block(g4)
    c: Block(g6)
    c: Block(g7)
FEATURE [Part::Extrusion] Extrude056
  Base = -> Sketch065
  Dir = (0,-1,2e-16)
  DirMode = 2
  FaceMakerClass = Part::FaceMakerBullseye
  LengthFwd = 2
  LengthRev = 0
  Solid = true
  Symmetric = false
FEATURE [Part::Extrusion] Extrude057  label="top025"
  Base = -> Sketch064
  Dir = (0,0,1)
  DirMode = 2
  FaceMakerClass = Part::FaceMakerBullseye
  LengthFwd = 72
  LengthRev = 0
  Solid = true
  Symmetric = false
FEATURE [Sketcher::SketchObject] Sketch066
  FullyConstrained = true
  MapMode = 3
  Placement = pos=(0,0,0) rot=(1,0,0;1.5708rad)
  Support = -> [Extrude057]
  sketch-geometry (8):
    g0: Circle CenterX=80.351 CenterY=-67.6202 CenterZ=0 NormalX=0 NormalY=0 NormalZ=1 AngleXU=0 Radius=3
    g1: Circle CenterX=80.351 CenterY=-4.92017 CenterZ=0 NormalX=0 NormalY=0 NormalZ=1 AngleXU=0 Radius=3
    g2: Circle CenterX=23.851 CenterY=-4.92017 CenterZ=0 NormalX=0 NormalY=0 NormalZ=1 AngleXU=0 Radius=3
    g3: Circle CenterX=23.851 CenterY=-67.6202 CenterZ=0 NormalX=0 NormalY=0 NormalZ=1 AngleXU=0 Radius=3
    g4: Circle CenterX=23.851 CenterY=-67.6202 CenterZ=0 NormalX=0 NormalY=0 NormalZ=1 AngleXU=0 Radius=5
    g5: Circle CenterX=80.351 CenterY=-67.6202 CenterZ=0 NormalX=0 NormalY=0 NormalZ=1 AngleXU=0 Radius=5
    g6: Circle CenterX=23.851 CenterY=-4.92017 CenterZ=0 NormalX=0 NormalY=0 NormalZ=1 AngleXU=0 Radius=5
    g7: Circle CenterX=80.351 CenterY=-4.92017 CenterZ=0 NormalX=0 NormalY=0 NormalZ=1 AngleXU=0 Radius=5
  constraints (8):
    c: Block(g1)
    c: Block(g0)
    c: Block(g3)
    c: Block(g2)
    c: Block(g5)
    c: Block(g4)
    c: Block(g6)
    c: Block(g7)
FEATURE [Part::Extrusion] Extrude055
  Base = -> Sketch066
  Dir = (0,-1,2e-16)
  DirMode = 2
  FaceMakerClass = Part::FaceMakerBullseye
  LengthFwd = 2
  LengthRev = 0
  Solid = true
  Symmetric = false
FEATURE [Part::Fillet] Fillet041
  Base = -> Extrude056
  Edges = 4 edges r=1.99: [Edge6,Edge12,Edge18,Edge24]
FEATURE [Part::Cut] Cut045
  Base = -> Extrude055
  Placement = pos=(0,6,0) rot=(0,0,1;0rad)
  Tool = -> Fillet041
FEATURE [Part::MultiFuse] Fusion095  label="pcbScrewPillars"
  Placement = pos=(-3.2,-1,72.3) rot=(0,0,1;0rad)
  Shapes = -> [Cut045,Extrude054]
FEATURE [Part::Feature] Face113
  shape: bbox 3.2 x 1.5 x 2e-07 mm, 1 faces, 0 solids (baked)
FEATURE [Part::Revolution] Revolve121  label="backCaseScrewRetainer002"
  Angle = 360
  Axis = (0,1,0)
  Base = (0,0,0)
  FaceMakerClass = Part::FaceMakerBullseye
  Placement = pos=(12.5,3,62) rot=(0,0,1;0rad)
  Solid = false
  Source = -> Face113
  Symmetric = false
FEATURE [Part::Feature] Face114
  shape: bbox 3.2 x 1.5 x 2e-07 mm, 1 faces, 0 solids (baked)
FEATURE [Part::Feature] Face115
  shape: bbox 3.2 x 1.5 x 2e-07 mm, 1 faces, 0 solids (baked)
FEATURE [Part::Feature] Face116
  shape: bbox 3.2 x 1.5 x 2e-07 mm, 1 faces, 0 solids (baked)
FEATURE [Part::Revolution] Revolve122  label="frontCaseScrewRetainer004"
  Angle = 360
  Axis = (0,1,0)
  Base = (0,0,0)
  FaceMakerClass = Part::FaceMakerBullseye
  Placement = pos=(89.5,3,68.5) rot=(0,0,1;0rad)
  Solid = false
  Source = -> Face115
  Symmetric = false
FEATURE [Part::Revolution] Revolve123  label="frontCaseScrewRetainer005"
  Angle = 360
  Axis = (0,1,0)
  Base = (0,0,0)
  FaceMakerClass = Part::FaceMakerBullseye
  Placement = pos=(89.5,3,3.5) rot=(0,0,1;0rad)
  Solid = false
  Source = -> Face116
  Symmetric = false
FEATURE [Part::Revolution] Revolve124  label="backCaseScrewRetainer003"
  Angle = 360
  Axis = (0,1,0)
  Base = (0,0,0)
  FaceMakerClass = Part::FaceMakerBullseye
  Placement = pos=(12.5,3,10) rot=(0,0,1;0rad)
  Solid = false
  Source = -> Face114
  Symmetric = false
FEATURE [Part::Feature] Face117
  shape: bbox 3.6 x 3.2 x 2e-07 mm, 1 faces, 0 solids (baked)
FEATURE [Part::Revolution] Revolve125  label="moreFrontCaseScrewRetainer004"
  Angle = 360
  Axis = (0,1,0)
  Base = (0,0,0)
  FaceMakerClass = Part::FaceMakerBullseye
  Placement = pos=(109.5,4.5,68.5) rot=(0,0,1;0rad)
  Solid = false
  Source = -> Face117
  Symmetric = false
FEATURE [Part::Feature] Face118
  shape: bbox 3.6 x 3.2 x 2e-07 mm, 1 faces, 0 solids (baked)
FEATURE [Part::Revolution] Revolve126  label="moreFrontCaseScrewRetainer005"
  Angle = 360
  Axis = (0,1,0)
  Base = (0,0,0)
  FaceMakerClass = Part::FaceMakerBullseye
  Placement = pos=(109.5,4.5,3.5) rot=(0,0,1;0rad)
  Solid = false
  Source = -> Face118
  Symmetric = false
FEATURE [Part::MultiFuse] Fusion096  label="screwRetainers001"
  Shapes = -> [Revolve126,Revolve125,Revolve124,Revolve123,Revolve122,Revolve121]
FEATURE [Part::Feature] Face119
  shape: bbox 10 x 16.5 x 2e-07 mm, 1 faces, 0 solids (baked)
FEATURE [Part::Revolution] Revolve130  label="plugHousing050"
  Angle = 360
  Axis = (0,1,0)
  Base = (0,0,0)
  FaceMakerClass = Part::FaceMakerBullseye
  Placement = pos=(0,0,36.15) rot=(0,0,1;0rad)
  Solid = false
  Source = -> Face119
  Symmetric = false
FEATURE [Part::Feature] Face120
  shape: bbox 10 x 16.5 x 2e-07 mm, 1 faces, 0 solids (baked)
FEATURE [Part::Feature] Face121
  shape: bbox 10 x 16.5 x 2e-07 mm, 1 faces, 0 solids (baked)
FEATURE [Part::Revolution] Revolve127  label="plugHousing047"
  Angle = 360
  Axis = (0,1,0)
  Base = (0,0,0)
  FaceMakerClass = Part::FaceMakerBullseye
  Placement = pos=(0,0,36.15) rot=(0,0,1;0rad)
  Solid = false
  Source = -> Face121
  Symmetric = false
FEATURE [Part::Feature] Face122
  shape: bbox 10 x 16.5 x 2e-07 mm, 1 faces, 0 solids (baked)
FEATURE [Part::Feature] Face123
  shape: bbox 10 x 16.5 x 2e-07 mm, 1 faces, 0 solids (baked)
FEATURE [Part::Revolution] Revolve128  label="plugHousing048"
  Angle = 360
  Axis = (0,1,0)
  Base = (0,0,0)
  FaceMakerClass = Part::FaceMakerBullseye
  Placement = pos=(0,0,36.15) rot=(0,0,1;0rad)
  Solid = false
  Source = -> Face123
  Symmetric = false
FEATURE [Part::MultiFuse] Fusion100  label="plugHousing054"
  Placement = pos=(0,0,0) rot=(0,0,1;1.5708rad)
  Shapes = -> [Revolve130,Revolve128]
FEATURE [Part::Feature] Face124
  shape: bbox 10 x 16.5 x 2e-07 mm, 1 faces, 0 solids (baked)
FEATURE [Part::Feature] Face125
  shape: bbox 10 x 16.5 x 2e-07 mm, 1 faces, 0 solids (baked)
FEATURE [Part::Revolution] Revolve129  label="plugHousing049"
  Angle = 360
  Axis = (0,1,0)
  Base = (0,0,0)
  FaceMakerClass = Part::FaceMakerBullseye
  Placement = pos=(0,0,36.15) rot=(0,0,1;0rad)
  Solid = false
  Source = -> Face125
  Symmetric = false
FEATURE [Part::Feature] Face126
  shape: bbox 10 x 16.5 x 2e-07 mm, 1 faces, 0 solids (baked)
FEATURE [Part::Revolution] Revolve131  label="plugHousing058"
  Angle = 360
  Axis = (0,1,0)
  Base = (0,0,0)
  FaceMakerClass = Part::FaceMakerBullseye
  Placement = pos=(0,0,36.15) rot=(0,0,1;0rad)
  Solid = false
  Source = -> Face120
  Symmetric = false
FEATURE [Part::MultiFuse] Fusion099  label="plugHousing053"
  Placement = pos=(0,0,0) rot=(0,0,1;1.5708rad)
  Shapes = -> [Revolve127,Revolve131]
FEATURE [Part::MultiFuse] Fusion102  label="plugHousing056"
  Placement = pos=(0,19,0) rot=(0,0,1;3.14159rad)
  Shapes = -> [Fusion100,Fusion099]
FEATURE [Part::Revolution] Revolve132  label="plugHousing059"
  Angle = 360
  Axis = (0,1,0)
  Base = (0,0,0)
  FaceMakerClass = Part::FaceMakerBullseye
  Placement = pos=(0,0,36.15) rot=(0,0,1;0rad)
  Solid = false
  Source = -> Face126
  Symmetric = false
FEATURE [Part::Revolution] Revolve133  label="plugHousing060"
  Angle = 360
  Axis = (0,1,0)
  Base = (0,0,0)
  FaceMakerClass = Part::FaceMakerBullseye
  Placement = pos=(0,0,36.15) rot=(0,0,1;0rad)
  Solid = false
  Source = -> Face122
  Symmetric = false
FEATURE [Part::MultiFuse] Fusion097  label="plugHousing051"
  Placement = pos=(0,0,0) rot=(0,0,1;1.5708rad)
  Shapes = -> [Revolve133,Revolve132]
FEATURE [Part::Revolution] Revolve134  label="plugHousing061"
  Angle = 360
  Axis = (0,1,0)
  Base = (0,0,0)
  FaceMakerClass = Part::FaceMakerBullseye
  Placement = pos=(0,0,36.15) rot=(0,0,1;0rad)
  Solid = false
  Source = -> Face124
  Symmetric = false
FEATURE [Part::MultiFuse] Fusion101  label="plugHousing055"
  Placement = pos=(0,0,0) rot=(0,0,1;1.5708rad)
  Shapes = -> [Revolve129,Revolve134]
FEATURE [Part::MultiFuse] Fusion098  label="plugHousing052"
  Placement = pos=(0,19,0) rot=(0,0,1;3.14159rad)
  Shapes = -> [Fusion097,Fusion101]
FEATURE [Part::MultiFuse] Fusion103  label="plugHousing057"
  Placement = pos=(122.621,0,-0.15) rot=(0,0,1;0rad)
  Shapes = -> [Fusion102,Fusion098]
FEATURE [Part::Box] Box028  label="Cube015"
  AttacherType = Attacher::AttachEngine3D
  Height = 28
  Length = 3
  Placement = pos=(110.7,19,22) rot=(0,0,1;0rad)
  Width = 15.7
FEATURE [Part::Cylinder] Cylinder044
  Angle = 360
  AttacherType = Attacher::AttachEngine3D
  Height = 20
  Placement = pos=(0,0,36.15) rot=(0,0,1;0rad)
  Radius = 10.3
FEATURE [Part::Cylinder] Cylinder045
  Angle = 360
  AttacherType = Attacher::AttachEngine3D
  Height = 10
  Placement = pos=(0,0,36.15) rot=(0,0,1;0rad)
  Radius = 4
FEATURE [Part::MultiFuse] Fusion104  label="removeToCreteHoleForPlugHousing040"
  Placement = pos=(70,19,36) rot=(0,1,0;1.5708rad)
  Shapes = -> [Cylinder044,Cylinder045]
FEATURE [Part::Cut] Cut046  label="plugHousingTab003"
  Base = -> Box028
  Tool = -> Fusion104
FEATURE [Part::MultiFuse] Fusion105  label="plugHousing062"
  Shapes = -> [Fusion103,Cut046]
FEATURE [Part::Fillet] Fillet042
  Base = -> Fusion105
  Edges = 1 edges r=2: [Edge25]
FEATURE [Part::Fillet] Fillet043  label="plugHousing063"
  Base = -> Fillet042
  Edges = 1 edges r=2: [Edge8]
  Placement = pos=(7,0,0) rot=(0,0,1;0rad)
FEATURE [Part::Feature] Face127
  shape: bbox 10 x 16.5 x 2e-07 mm, 1 faces, 0 solids (baked)
FEATURE [Part::Feature] Face128
  shape: bbox 10 x 16.5 x 2e-07 mm, 1 faces, 0 solids (baked)
FEATURE [Part::Revolution] Revolve137  label="plugHousing070"
  Angle = 360
  Axis = (0,1,0)
  Base = (0,0,0)
  FaceMakerClass = Part::FaceMakerBullseye
  Placement = pos=(0,0,36.15) rot=(0,0,1;0rad)
  Solid = false
  Source = -> Face127
  Symmetric = false
FEATURE [Part::Revolution] Revolve140  label="plugHousing073"
  Angle = 360
  Axis = (0,1,0)
  Base = (0,0,0)
  FaceMakerClass = Part::FaceMakerBullseye
  Placement = pos=(0,0,36.15) rot=(0,0,1;0rad)
  Solid = false
  Source = -> Face128
  Symmetric = false
FEATURE [Part::Feature] Face129
  shape: bbox 10 x 16.5 x 2e-07 mm, 1 faces, 0 solids (baked)
FEATURE [Part::Revolution] Revolve138  label="plugHousing071"
  Angle = 360
  Axis = (0,1,0)
  Base = (0,0,0)
  FaceMakerClass = Part::FaceMakerBullseye
  Placement = pos=(0,0,36.15) rot=(0,0,1;0rad)
  Solid = false
  Source = -> Face129
  Symmetric = false
FEATURE [Part::Feature] Face130
  shape: bbox 10 x 16.5 x 2e-07 mm, 1 faces, 0 solids (baked)
FEATURE [Part::Revolution] Revolve139  label="plugHousing072"
  Angle = 360
  Axis = (0,1,0)
  Base = (0,0,0)
  FaceMakerClass = Part::FaceMakerBullseye
  Placement = pos=(0,0,36.15) rot=(0,0,1;0rad)
  Solid = false
  Source = -> Face130
  Symmetric = false
FEATURE [Part::Feature] Face131
  shape: bbox 10 x 16.5 x 2e-07 mm, 1 faces, 0 solids (baked)
FEATURE [Part::Revolution] Revolve135  label="plugHousing068"
  Angle = 360
  Axis = (0,1,0)
  Base = (0,0,0)
  FaceMakerClass = Part::FaceMakerBullseye
  Placement = pos=(0,0,36.15) rot=(0,0,1;0rad)
  Solid = false
  Source = -> Face131
  Symmetric = false
FEATURE [Part::MultiFuse] Fusion112  label="plugHousing078"
  Placement = pos=(0,0,0) rot=(0,0,1;1.5708rad)
  Shapes = -> [Revolve135,Revolve139]
FEATURE [Part::Feature] Face132
  shape: bbox 10 x 16.5 x 2e-07 mm, 1 faces, 0 solids (baked)
FEATURE [Part::Revolution] Revolve141  label="plugHousing074"
  Angle = 360
  Axis = (0,1,0)
  Base = (0,0,0)
  FaceMakerClass = Part::FaceMakerBullseye
  Placement = pos=(0,0,36.15) rot=(0,0,1;0rad)
  Solid = false
  Source = -> Face132
  Symmetric = false
FEATURE [Part::MultiFuse] Fusion110  label="plugHousing076"
  Placement = pos=(0,0,0) rot=(0,0,1;1.5708rad)
  Shapes = -> [Revolve141,Revolve140]
FEATURE [Part::Feature] Face133
  shape: bbox 10 x 16.5 x 2e-07 mm, 1 faces, 0 solids (baked)
FEATURE [Part::Revolution] Revolve136  label="plugHousing069"
  Angle = 360
  Axis = (0,1,0)
  Base = (0,0,0)
  FaceMakerClass = Part::FaceMakerBullseye
  Placement = pos=(0,0,36.15) rot=(0,0,1;0rad)
  Solid = false
  Source = -> Face133
  Symmetric = false
FEATURE [Part::MultiFuse] Fusion106  label="plugHousing064"
  Placement = pos=(0,0,0) rot=(0,0,1;1.5708rad)
  Shapes = -> [Revolve138,Revolve136]
FEATURE [Part::MultiFuse] Fusion108  label="plugHousing066"
  Placement = pos=(0,19,0) rot=(0,0,1;3.14159rad)
  Shapes = -> [Fusion106,Fusion112]
FEATURE [Part::Feature] Face134
  shape: bbox 10 x 16.5 x 2e-07 mm, 1 faces, 0 solids (baked)
FEATURE [Part::Revolution] Revolve142  label="plugHousing075"
  Angle = 360
  Axis = (0,1,0)
  Base = (0,0,0)
  FaceMakerClass = Part::FaceMakerBullseye
  Placement = pos=(0,0,36.15) rot=(0,0,1;0rad)
  Solid = false
  Source = -> Face134
  Symmetric = false
FEATURE [Part::MultiFuse] Fusion107  label="plugHousing065"
  Placement = pos=(0,0,0) rot=(0,0,1;1.5708rad)
  Shapes = -> [Revolve137,Revolve142]
FEATURE [Part::MultiFuse] Fusion111  label="plugHousing077"
  Placement = pos=(0,19,0) rot=(0,0,1;3.14159rad)
  Shapes = -> [Fusion110,Fusion107]
FEATURE [Part::MultiFuse] Fusion109  label="plugHousing067"
  Placement = pos=(131.236,0,-0.15) rot=(0,0,1;0rad)
  Shapes = -> [Fusion108,Fusion111]
FEATURE [Part::MultiFuse] Fusion113  label="plugHousing079"
  Shapes = -> [Fillet043,Fusion109]
FEATURE [Part::Feature] Face135
  shape: bbox 3.5 x 17.8 x 2e-07 mm, 1 faces, 0 solids (baked)
FEATURE [Part::Revolution] Revolve143  label="removeToCreateScrewAndThreadedInsertHole049"
  Angle = 360
  Axis = (0,1,0)
  Base = (0,0,0)
  FaceMakerClass = Part::FaceMakerBullseye
  Placement = pos=(12.5,0,10) rot=(0,0,1;0rad)
  Solid = false
  Source = -> Face135
  Symmetric = false
FEATURE [Part::Feature] Face136
  shape: bbox 3.5 x 17.8 x 2e-07 mm, 1 faces, 0 solids (baked)
FEATURE [Part::Revolution] Revolve144  label="removeToCreateScrewAndThreadedInsertHole050"
  Angle = 360
  Axis = (0,1,0)
  Base = (0,0,0)
  FaceMakerClass = Part::FaceMakerBullseye
  Placement = pos=(12.5,0,62) rot=(0,0,1;0rad)
  Solid = false
  Source = -> Face136
  Symmetric = false
FEATURE [Part::Feature] Face137
  shape: bbox 3.5 x 17.8 x 2e-07 mm, 1 faces, 0 solids (baked)
FEATURE [Part::Revolution] Revolve145  label="removeToCreateScrewAndThreadedInsertHole051"
  Angle = 360
  Axis = (0,1,0)
  Base = (0,0,0)
  FaceMakerClass = Part::FaceMakerBullseye
  Placement = pos=(89.5,0,68.5) rot=(0,0,1;0rad)
  Solid = false
  Source = -> Face137
  Symmetric = false
FEATURE [Part::Feature] Face138
  shape: bbox 3.5 x 17.8 x 2e-07 mm, 1 faces, 0 solids (baked)
FEATURE [Part::Revolution] Revolve146  label="removeToCreateScrewAndThreadedInsertHole052"
  Angle = 360
  Axis = (0,1,0)
  Base = (0,0,0)
  FaceMakerClass = Part::FaceMakerBullseye
  Placement = pos=(89.5,0,3.5) rot=(0,0,1;0rad)
  Solid = false
  Source = -> Face138
  Symmetric = false
FEATURE [Part::Feature] Face139
  shape: bbox 3.5 x 17.8 x 2e-07 mm, 1 faces, 0 solids (baked)
FEATURE [Part::Revolution] Revolve147  label="removeToCreateScrewAndThreadedInsertHole053"
  Angle = 360
  Axis = (0,1,0)
  Base = (0,0,0)
  FaceMakerClass = Part::FaceMakerBullseye
  Placement = pos=(109.5,4.7,3.5) rot=(0,0,1;0rad)
  Solid = false
  Source = -> Face139
  Symmetric = false
FEATURE [Part::Feature] Face140
  shape: bbox 3.5 x 17.8 x 2e-07 mm, 1 faces, 0 solids (baked)
FEATURE [Part::Revolution] Revolve148  label="removeToCreateScrewAndThreadedInsertHole054"
  Angle = 360
  Axis = (0,1,0)
  Base = (0,0,0)
  FaceMakerClass = Part::FaceMakerBullseye
  Placement = pos=(109.5,4.7,68.5) rot=(0,0,1;0rad)
  Solid = false
  Source = -> Face140
  Symmetric = false
FEATURE [Part::MultiFuse] Fusion114  label="removeToCreateScrewAndThreadedInsertHole055"
  Shapes = -> [Revolve148,Revolve147,Revolve146,Revolve145,Revolve144,Revolve143]
FEATURE [Part::Cut] Cut047  label="casePillars004"
  Base = -> Cut037
  Tool = -> Fusion114
FEATURE [Part::Feature] Face141
  shape: bbox 3.5 x 17.8 x 2e-07 mm, 1 faces, 0 solids (baked)
FEATURE [Part::Feature] Face142
  shape: bbox 3.5 x 17.8 x 2e-07 mm, 1 faces, 0 solids (baked)
FEATURE [Part::Feature] Face143
  shape: bbox 3.5 x 17.8 x 2e-07 mm, 1 faces, 0 solids (baked)
FEATURE [Part::Revolution] Revolve149  label="removeToCreateScrewAndThreadedInsertHole057"
  Angle = 360
  Axis = (0,1,0)
  Base = (0,0,0)
  FaceMakerClass = Part::FaceMakerBullseye
  Placement = pos=(12.5,0,10) rot=(0,0,1;0rad)
  Solid = false
  Source = -> Face141
  Symmetric = false
FEATURE [Part::Feature] Face144
  shape: bbox 3.5 x 17.8 x 2e-07 mm, 1 faces, 0 solids (baked)
FEATURE [Part::Feature] Face145
  shape: bbox 3.5 x 17.8 x 2e-07 mm, 1 faces, 0 solids (baked)
FEATURE [Part::Feature] Face146
  shape: bbox 3.5 x 17.8 x 2e-07 mm, 1 faces, 0 solids (baked)
FEATURE [Part::Revolution] Revolve150  label="removeToCreateScrewAndThreadedInsertHole058"
  Angle = 360
  Axis = (0,1,0)
  Base = (0,0,0)
  FaceMakerClass = Part::FaceMakerBullseye
  Placement = pos=(12.5,0,62) rot=(0,0,1;0rad)
  Solid = false
  Source = -> Face146
  Symmetric = false
FEATURE [Part::Revolution] Revolve151  label="removeToCreateScrewAndThreadedInsertHole059"
  Angle = 360
  Axis = (0,1,0)
  Base = (0,0,0)
  FaceMakerClass = Part::FaceMakerBullseye
  Placement = pos=(89.5,0,68.5) rot=(0,0,1;0rad)
  Solid = false
  Source = -> Face143
  Symmetric = false
FEATURE [Part::Revolution] Revolve152  label="removeToCreateScrewAndThreadedInsertHole060"
  Angle = 360
  Axis = (0,1,0)
  Base = (0,0,0)
  FaceMakerClass = Part::FaceMakerBullseye
  Placement = pos=(89.5,0,3.5) rot=(0,0,1;0rad)
  Solid = false
  Source = -> Face142
  Symmetric = false
FEATURE [Part::Revolution] Revolve153  label="removeToCreateScrewAndThreadedInsertHole061"
  Angle = 360
  Axis = (0,1,0)
  Base = (0,0,0)
  FaceMakerClass = Part::FaceMakerBullseye
  Placement = pos=(109.5,4.7,3.5) rot=(0,0,1;0rad)
  Solid = false
  Source = -> Face145
  Symmetric = false
FEATURE [Part::Revolution] Revolve154  label="removeToCreateScrewAndThreadedInsertHole062"
  Angle = 360
  Axis = (0,1,0)
  Base = (0,0,0)
  FaceMakerClass = Part::FaceMakerBullseye
  Placement = pos=(109.5,4.7,68.5) rot=(0,0,1;0rad)
  Solid = false
  Source = -> Face144
  Symmetric = false
FEATURE [Part::MultiFuse] Fusion115  label="removeToCreateScrewAndThreadedInsertHole056"
  Shapes = -> [Revolve154,Revolve153,Revolve152,Revolve151,Revolve150,Revolve149]
FEATURE [Part::Feature] Face147
  shape: bbox 9.8 x 26.5 x 2e-07 mm, 1 faces, 0 solids (baked)
FEATURE [Part::Revolution] Revolve155
  Angle = 360
  Axis = (0,1,0)
  Base = (0,0,0)
  FaceMakerClass = Part::FaceMakerBullseye
  Placement = pos=(0,0,0) rot=(0,0,1;1.5708rad)
  Solid = false
  Source = -> Face147
  Symmetric = false
FEATURE [Part::Feature] Face148
  shape: bbox 9.8 x 26.5 x 2e-07 mm, 1 faces, 0 solids (baked)
FEATURE [Part::Revolution] Revolve156
  Angle = 360
  Axis = (0,1,0)
  Base = (0,0,0)
  FaceMakerClass = Part::FaceMakerBullseye
  Placement = pos=(0,0,0) rot=(0,0,1;1.5708rad)
  Solid = false
  Source = -> Face148
  Symmetric = false
FEATURE [Part::MultiFuse] Fusion116
  Placement = pos=(-18,19,36) rot=(0,0,1;0rad)
  Shapes = -> [Revolve156,Revolve155]
FEATURE [Part::Box] Box029  label="Cube016"
  AttacherType = Attacher::AttachEngine3D
  Height = 28
  Length = 3
  Placement = pos=(110.7,19,22) rot=(0,0,1;0rad)
  Width = 15.7
FEATURE [Part::Cylinder] Cylinder046
  Angle = 360
  AttacherType = Attacher::AttachEngine3D
  Height = 10
  Placement = pos=(0,0,36.15) rot=(0,0,1;0rad)
  Radius = 4
FEATURE [Part::Cylinder] Cylinder047
  Angle = 360
  AttacherType = Attacher::AttachEngine3D
  Height = 20
  Placement = pos=(0,0,36.15) rot=(0,0,1;0rad)
  Radius = 10.3
FEATURE [Part::MultiFuse] Fusion117  label="removeToCreteHoleForPlugHousing041"
  Placement = pos=(70,19,36) rot=(0,1,0;1.5708rad)
  Shapes = -> [Cylinder047,Cylinder046]
FEATURE [Part::Cut] Cut049  label="plugHousingTab004"
  Base = -> Box029
  Placement = pos=(-107.4,-14,0) rot=(0,0,1;0rad)
  Tool = -> Fusion117
FEATURE [Part::Box] Box030  label="Cube017"
  AttacherType = Attacher::AttachEngine3D
  Height = 28
  Length = 3
  Placement = pos=(110.7,19,22) rot=(0,0,1;0rad)
  Width = 15.7
FEATURE [Part::Cylinder] Cylinder048
  Angle = 360
  AttacherType = Attacher::AttachEngine3D
  Height = 10
  Placement = pos=(0,0,36.15) rot=(0,0,1;0rad)
  Radius = 4
FEATURE [Part::Cylinder] Cylinder049
  Angle = 360
  AttacherType = Attacher::AttachEngine3D
  Height = 20
  Placement = pos=(0,0,36.15) rot=(0,0,1;0rad)
  Radius = 10.3
FEATURE [Part::MultiFuse] Fusion118  label="removeToCreteHoleForPlugHousing042"
  Placement = pos=(70,19,36) rot=(0,1,0;1.5708rad)
  Shapes = -> [Cylinder049,Cylinder048]
FEATURE [Part::Cut] Cut050  label="plugHousingTab005"
  Base = -> Box030
  Placement = pos=(-107.4,-14,0) rot=(0,0,1;0rad)
  Tool = -> Fusion118
FEATURE [Part::MultiFuse] Fusion119
  Placement = pos=(9.6,23,0) rot=(0,0,1;3.14159rad)
  Shapes = -> [Cut049,Cut050]
FEATURE [Part::Box] Box031  label="Cube018"
  AttacherType = Attacher::AttachEngine3D
  Height = 10
  Length = 3
  Placement = pos=(3.3,4,12) rot=(0,0,1;0rad)
  Width = 10
FEATURE [Part::Fillet] Fillet044
  Base = -> Box031
  Edges = 1 edges r=2: [Edge11]
FEATURE [Part::Box] Box032  label="Cube019"
  AttacherType = Attacher::AttachEngine3D
  Height = 10
  Length = 3
  Placement = pos=(3.3,4,50) rot=(0,0,1;0rad)
  Width = 10
FEATURE [Part::Fillet] Fillet045
  Base = -> Box032
  Edges = 1 edges r=2: [Edge12]
FEATURE [Part::Box] Box033  label="Cube020"
  AttacherType = Attacher::AttachEngine3D
  Height = 28
  Length = 4
  Placement = pos=(5,0,22) rot=(0,0,1;0rad)
  Width = 10
FEATURE [Part::Fillet] Fillet046
  Base = -> Box033
  Edges = 1 edges r=1: [Edge7]
FEATURE [Part::Fillet] Fillet047
  Base = -> Fillet046
  Edges = 1 edges r=2: [Edge5]
FEATURE [Part::Fillet] Fillet048
  Base = -> Fillet047
  Edges = 1 edges r=2: [Edge2]
FEATURE [Part::Cylinder] Cylinder050
  Angle = 360
  AttacherType = Attacher::AttachEngine3D
  Height = 20
  Placement = pos=(0,0,36.15) rot=(0,0,1;0rad)
  Radius = 8.2
FEATURE [Part::Cylinder] Cylinder051
  Angle = 360
  AttacherType = Attacher::AttachEngine3D
  Height = 10
  Placement = pos=(0,0,36.15) rot=(0,0,1;0rad)
  Radius = 4
FEATURE [Part::MultiFuse] Fusion120  label="removeToCreteHoleForPlugHousing043"
  Placement = pos=(-42,19,36) rot=(0,1,0;1.5708rad)
  Shapes = -> [Cylinder050,Cylinder051]
FEATURE [Sketcher::SketchObject] Sketch067  label="topSketch018"
  FullyConstrained = true
  sketch-geometry (4):
    g0: LineSegment StartX=16.8446 StartY=31.512 StartZ=0 EndX=16.3251 EndY=34.4666 EndZ=0
    g1: ArcOfCircle CenterX=19 CenterY=19.2524 CenterZ=0 NormalX=0 NormalY=0 NormalZ=1 AngleXU=0 Radius=15.4476 StartAngle=1.74483 EndAngle=2.72717
    g2: ArcOfCircle CenterX=19 CenterY=19.2524 CenterZ=0 NormalX=0 NormalY=0 NormalZ=1 AngleXU=0 Radius=12.4476 StartAngle=1.74483 EndAngle=2.73189
    g3: LineSegment StartX=4.86004 StartY=25.4725 StartZ=0 EndX=7.58253 EndY=24.2107 EndZ=0
  constraints (7):
    c: Block(g0)
    c: Coincident(g1,g0)
    c: Coincident(g2,g0)
    c: Coincident(g3,g1)
    c: Coincident(g3,g2)
    c: Block(g1)
    c: Block(g2)
FEATURE [Part::Extrusion] Extrude058
  Base = -> Sketch067
  Dir = (0,0,1)
  DirMode = 2
  FaceMakerClass = Part::FaceMakerBullseye
  LengthFwd = 10
  LengthRev = 0
  Placement = pos=(0,0,31) rot=(0,0,1;0rad)
  Solid = true
  Symmetric = false
FEATURE [Part::Cut] Cut051
  Base = -> Extrude058
  Tool = -> Fusion120
FEATURE [Part::Fillet] Fillet049
  Base = -> Cut051
  Edges = 1 edges r=2: [Edge1]
FEATURE [Part::Fillet] Fillet050
  Base = -> Fillet049
  Edges = 1 edges r=2.5: [Edge1]
FEATURE [Part::Fillet] Fillet051
  Base = -> Fillet050
  Edges = 1 edges r=2.5: [Edge2]
FEATURE [Part::MultiFuse] Fusion121  label="wireHolder003"
  Shapes = -> [Fusion116,Fillet051]
FEATURE [Part::MultiFuse] Fusion122
  Shapes = -> [Fillet045,Fusion121]
FEATURE [Part::MultiFuse] Fusion123  label="wireHolder004"
  Shapes = -> [Fusion122,Fillet048]
FEATURE [Part::MultiFuse] Fusion124  label="wireHolder005"
  Shapes = -> [Fillet044,Fusion119,Fusion123]
FEATURE [Sketcher::SketchObject] Sketch068  label="topSketch019"
  FullyConstrained = true
  sketch-geometry (6):
    g0: LineSegment StartX=19 StartY=38 StartZ=0 EndX=117 EndY=38 EndZ=0
    g1: ArcOfCircle CenterX=19 CenterY=19 CenterZ=0 NormalX=0 NormalY=0 NormalZ=1 AngleXU=0 Radius=19 StartAngle=1.5708 EndAngle=3.14159
    g2: LineSegment StartX=117 StartY=38 StartZ=0 EndX=117 EndY=19 EndZ=0
    g3: LineSegment StartX=98 StartY=1.0161e-12 StartZ=0 EndX=5.22862e-06 EndY=1.0161e-12 EndZ=0
    g4: LineSegment StartX=5.22862e-06 StartY=19 StartZ=0 EndX=5.22862e-06 EndY=1.0161e-12 EndZ=0
    g5: ArcOfCircle CenterX=98 CenterY=19 CenterZ=0 NormalX=0 NormalY=0 NormalZ=1 AngleXU=0 Radius=19 StartAngle=4.71239 EndAngle=6.28319
  constraints (16):
    c: Horizontal(g0)
    c: Distance(g0) = 98
    c: Coincident(g1,g0)
    c: Block(g1)
    c: Coincident(g2,g0)
    c: Vertical(g2)
    c: Distance(g2) = 19
    c: Horizontal(g3)
    c: Coincident(g4,g1)
    c: Vertical(g4)
    c: Coincident(g3,g4)
    c: Block(g3)
    c: Coincident(g5,g2)
    c: Coincident(g5,g3)
    c: Block(g0)
    c: Block(g5)
FEATURE [Part::Extrusion] Extrude059  label="sideA002"
  Base = -> Sketch068
  Dir = (0,0,1)
  DirMode = 2
  FaceMakerClass = Part::FaceMakerBullseye
  LengthFwd = 3
  LengthRev = 0
  Placement = pos=(0,0,-2.7) rot=(0,0,1;0rad)
  Solid = true
  Symmetric = false
FEATURE [Sketcher::SketchObject] Sketch069  label="topSketch020"
  FullyConstrained = true
  sketch-geometry (6):
    g0: LineSegment StartX=19 StartY=38 StartZ=0 EndX=117 EndY=38 EndZ=0
    g1: ArcOfCircle CenterX=19 CenterY=19 CenterZ=0 NormalX=0 NormalY=0 NormalZ=1 AngleXU=0 Radius=19 StartAngle=1.5708 EndAngle=3.14159
    g2: LineSegment StartX=117 StartY=38 StartZ=0 EndX=117 EndY=19 EndZ=0
    g3: LineSegment StartX=98 StartY=1.0161e-12 StartZ=0 EndX=5.22862e-06 EndY=1.0161e-12 EndZ=0
    g4: LineSegment StartX=5.22862e-06 StartY=19 StartZ=0 EndX=5.22862e-06 EndY=1.0161e-12 EndZ=0
    g5: ArcOfCircle CenterX=98 CenterY=19 CenterZ=0 NormalX=0 NormalY=0 NormalZ=1 AngleXU=0 Radius=19 StartAngle=4.71239 EndAngle=6.28319
  constraints (16):
    c: Horizontal(g0)
    c: Distance(g0) = 98
    c: Coincident(g1,g0)
    c: Block(g1)
    c: Coincident(g2,g0)
    c: Vertical(g2)
    c: Distance(g2) = 19
    c: Horizontal(g3)
    c: Coincident(g4,g1)
    c: Vertical(g4)
    c: Coincident(g3,g4)
    c: Block(g3)
    c: Coincident(g5,g2)
    c: Coincident(g5,g3)
    c: Block(g0)
    c: Block(g5)
FEATURE [Part::Extrusion] Extrude060  label="sideB002"
  Base = -> Sketch069
  Dir = (0,0,1)
  DirMode = 2
  FaceMakerClass = Part::FaceMakerBullseye
  LengthFwd = 3
  LengthRev = 0
  Placement = pos=(0,0,71.7) rot=(0,0,1;0rad)
  Solid = true
  Symmetric = false
FEATURE [Part::MultiFuse] Fusion127  label="removeFromBottom001"
  Placement = pos=(2,0,0) rot=(0,0,1;0rad)
  Shapes = -> [Extrude059,Extrude060]
FEATURE [Part::Cylinder] Cylinder052
  Angle = 360
  AttacherType = Attacher::AttachEngine3D
  Height = 20
  Placement = pos=(0,0,36.15) rot=(0,0,1;0rad)
  Radius = 14
FEATURE [Part::Cylinder] Cylinder053
  Angle = 360
  AttacherType = Attacher::AttachEngine3D
  Height = 10
  Placement = pos=(0,0,36.15) rot=(0,0,1;0rad)
  Radius = 4
FEATURE [Part::MultiFuse] Fusion128  label="removeToCreteHoleForPlugHousing044"
  Placement = pos=(70,19,36) rot=(0,1,0;1.5708rad)
  Shapes = -> [Cylinder052,Cylinder053]
FEATURE [Part::Cut] Cut052  label="bottom011"
  Base = -> Extrude043
  Tool = -> Fusion128
FEATURE [Part::Cut] Cut054  label="bottom012"
  Base = -> Cut052
  Tool = -> Fusion115
FEATURE [Sketcher::SketchObject] Sketch070
  FullyConstrained = true
  Placement = pos=(117,19,0) rot=(0.57735,0.57735,0.57735;2.0944rad)
  sketch-geometry (48):
    g0: LineSegment StartX=-49.19 StartY=69.25 StartZ=0 EndX=-49.19 EndY=66.25 EndZ=0
    g1: LineSegment StartX=-49.19 StartY=63.5 StartZ=0 EndX=-49.19 EndY=60.5 EndZ=0
    g2: LineSegment StartX=-49.19 StartY=57.75 StartZ=0 EndX=-49.19 EndY=54.75 EndZ=0
    g3: LineSegment StartX=-49.19 StartY=52 StartZ=0 EndX=-49.19 EndY=49 EndZ=0
    g4: LineSegment StartX=-49.19 StartY=46.25 StartZ=0 EndX=-49.19 EndY=43.25 EndZ=0
    g5: LineSegment StartX=-49.19 StartY=40.5 StartZ=0 EndX=-49.19 EndY=37.5 EndZ=0
    g6: LineSegment StartX=-49.19 StartY=34.5 StartZ=0 EndX=-49.19 EndY=31.5 EndZ=0
    g7: LineSegment StartX=-49.19 StartY=28.75 StartZ=0 EndX=-49.19 EndY=25.75 EndZ=0
    g8: LineSegment StartX=-49.19 StartY=23 StartZ=0 EndX=-49.19 EndY=20 EndZ=0
    g9: LineSegment StartX=-49.19 StartY=17.25 StartZ=0 EndX=-49.19 EndY=14.25 EndZ=0
    g10: LineSegment StartX=-49.19 StartY=11.5 StartZ=0 EndX=-49.19 EndY=8.5 EndZ=0
    g11: LineSegment StartX=-49.19 StartY=5.75 StartZ=0 EndX=-49.19 EndY=2.75 EndZ=0
    g12: ArcOfCircle CenterX=-1.5 CenterY=67.75 CenterZ=0 NormalX=0 NormalY=0 NormalZ=1 AngleXU=0 Radius=1.5 StartAngle=4.71239 EndAngle=7.85398
    g13: ArcOfCircle CenterX=-1.5 CenterY=62 CenterZ=0 NormalX=0 NormalY=0 NormalZ=1 AngleXU=0 Radius=1.5 StartAngle=4.71239 EndAngle=7.85398
    g14: ArcOfCircle CenterX=-1.5 CenterY=56.25 CenterZ=0 NormalX=0 NormalY=0 NormalZ=1 AngleXU=0 Radius=1.5 StartAngle=4.71239 EndAngle=7.85398
    g15: ArcOfCircle CenterX=-11.49 CenterY=50.5 CenterZ=0 NormalX=0 NormalY=0 NormalZ=1 AngleXU=0 Radius=1.5 StartAngle=4.71239 EndAngle=7.85398
    g16: ArcOfCircle CenterX=-16.28 CenterY=44.75 CenterZ=0 NormalX=0 NormalY=0 NormalZ=1 AngleXU=0 Radius=1.5 StartAngle=4.71239 EndAngle=7.85398
    g17: ArcOfCircle CenterX=-18.2337 CenterY=39 CenterZ=0 NormalX=0 NormalY=0 NormalZ=1 AngleXU=0 Radius=1.5 StartAngle=4.71485 EndAngle=7.85398
    g18: ArcOfCircle CenterX=-16.2837 CenterY=27.25 CenterZ=0 NormalX=0 NormalY=0 NormalZ=1 AngleXU=0 Radius=1.5 StartAngle=4.71485 EndAngle=7.85398
    g19: ArcOfCircle CenterX=-18.2337 CenterY=33 CenterZ=0 NormalX=0 NormalY=0 NormalZ=1 AngleXU=0 Radius=1.5 StartAngle=4.71485 EndAngle=7.85398
    g20: ArcOfCircle CenterX=-11.49 CenterY=21.5 CenterZ=0 NormalX=0 NormalY=0 NormalZ=1 AngleXU=0 Radius=1.5 StartAngle=4.71239 EndAngle=7.85398
    g21: ArcOfCircle CenterX=-1.5 CenterY=4.25 CenterZ=0 NormalX=0 NormalY=0 NormalZ=1 AngleXU=0 Radius=1.5 StartAngle=4.71239 EndAngle=7.85398
    g22: ArcOfCircle CenterX=-1.5 CenterY=10 CenterZ=0 NormalX=0 NormalY=0 NormalZ=1 AngleXU=0 Radius=1.5 StartAngle=4.71239 EndAngle=7.85398
    g23: ArcOfCircle CenterX=-1.5 CenterY=15.75 CenterZ=0 NormalX=0 NormalY=0 NormalZ=1 AngleXU=0 Radius=1.5 StartAngle=4.71239 EndAngle=7.85398
    g24: LineSegment StartX=-49.19 StartY=69.25 StartZ=0 EndX=-1.5 EndY=69.25 EndZ=0
    g25: LineSegment StartX=-49.19 StartY=66.25 StartZ=0 EndX=-1.5 EndY=66.25 EndZ=0
    g26: LineSegment StartX=-49.19 StartY=63.5 StartZ=0 EndX=-1.5 EndY=63.5 EndZ=0
    g27: LineSegment StartX=-49.19 StartY=60.5 StartZ=0 EndX=-1.5 EndY=60.5 EndZ=0
    g28: LineSegment StartX=-49.19 StartY=57.75 StartZ=0 EndX=-1.5 EndY=57.75 EndZ=0
    g29: LineSegment StartX=-49.19 StartY=54.75 StartZ=0 EndX=-1.5 EndY=54.75 EndZ=0
    g30: LineSegment StartX=-49.19 StartY=52 StartZ=0 EndX=-11.49 EndY=52 EndZ=0
    g31: LineSegment StartX=-49.19 StartY=49 StartZ=0 EndX=-11.49 EndY=49 EndZ=0
    g32: LineSegment StartX=-49.19 StartY=46.25 StartZ=0 EndX=-16.28 EndY=46.25 EndZ=0
    g33: LineSegment StartX=-49.19 StartY=43.25 StartZ=0 EndX=-16.28 EndY=43.25 EndZ=0
    g34: LineSegment StartX=-49.19 StartY=40.5 StartZ=0 EndX=-18.2337 EndY=40.5 EndZ=0
    g35: LineSegment StartX=-49.19 StartY=37.5 StartZ=0 EndX=-18.23 EndY=37.5 EndZ=0
    g36: LineSegment StartX=-49.19 StartY=34.5 StartZ=0 EndX=-18.2337 EndY=34.5 EndZ=0
    g37: LineSegment StartX=-49.19 StartY=31.5 StartZ=0 EndX=-18.23 EndY=31.5 EndZ=0
    g38: LineSegment StartX=-49.19 StartY=28.75 StartZ=0 EndX=-16.2837 EndY=28.75 EndZ=0
    g39: LineSegment StartX=-49.19 StartY=25.75 StartZ=0 EndX=-16.28 EndY=25.75 EndZ=0
    g40: LineSegment StartX=-49.19 StartY=23 StartZ=0 EndX=-11.49 EndY=23 EndZ=0
    g41: LineSegment StartX=-49.19 StartY=20 StartZ=0 EndX=-11.49 EndY=20 EndZ=0
    g42: LineSegment StartX=-49.19 StartY=17.25 StartZ=0 EndX=-1.5 EndY=17.25 EndZ=0
    g43: LineSegment StartX=-49.19 StartY=14.25 StartZ=0 EndX=-1.5 EndY=14.25 EndZ=0
    g44: LineSegment StartX=-49.19 StartY=11.5 StartZ=0 EndX=-1.5 EndY=11.5 EndZ=0
    g45: LineSegment StartX=-49.19 StartY=8.5 StartZ=0 EndX=-1.5 EndY=8.5 EndZ=0
    g46: LineSegment StartX=-49.19 StartY=5.75 StartZ=0 EndX=-1.5 EndY=5.75 EndZ=0
    g47: LineSegment StartX=-49.19 StartY=2.75 StartZ=0 EndX=-1.5 EndY=2.75 EndZ=0
  constraints (120):
    c: Vertical(g0)
    c: Distance(g0) = 3
    c: Block(g0)
    c: Vertical(g1)
    c: Distance(g1) = 3
    c: Vertical(g2)
    c: Equal(g0,g2) = 3
    c: Block(g2)
    c: Vertical(g3)
    c: Equal(g1,g3) = 3
    c: Vertical(g4)
    c: Equal(g0,g4) = 3
    c: Block(g4)
    c: Vertical(g5)
    c: Equal(g1,g5) = 3
    c: Vertical(g6)
    c: Equal(g0,g6) = 3
    c: Block(g6)
    c: Vertical(g7)
    c: Equal(g1,g7) = 3
    c: Vertical(g8)
    c: Equal(g0,g8) = 3
    c: Block(g8)
    c: Vertical(g9)
    c: Equal(g1,g9) = 3
    c: Vertical(g10)
    c: Equal(g0,g10) = 3
    c: Block(g10)
    c: Vertical(g11)
    c: Equal(g1,g11) = 3
    c: Block(g12)
    c: Block(g13)
    c: Block(g14)
    c: Block(g15)
    c: Block(g16)
    c: Block(g17)
    c: Block(g18)
    c: Block(g19)
    c: Block(g20)
    c: Block(g21)
    c: Block(g22)
    c: Block(g23)
    c: Block(g11)
    c: Block(g9)
    c: Block(g7)
    c: Block(g5)
    c: Block(g3)
    c: Block(g1)
    c: Coincident(g24,g0)
    c: Coincident(g24,g12)
    c: Horizontal(g24)
    c: Coincident(g25,g0)
    c: Coincident(g25,g12)
    c: Horizontal(g25)
    c: Coincident(g26,g1)
    c: Coincident(g26,g13)
    c: Horizontal(g26)
    c: Coincident(g27,g1)
    c: Coincident(g27,g13)
    c: Horizontal(g27)
    c: Coincident(g28,g2)
    c: Coincident(g28,g14)
    c: Horizontal(g28)
    c: Coincident(g29,g2)
    c: Coincident(g29,g14)
    c: Horizontal(g29)
    c: Coincident(g30,g3)
    c: Coincident(g30,g15)
    c: Horizontal(g30)
    c: Coincident(g31,g3)
    c: Coincident(g31,g15)
    c: Horizontal(g31)
    c: Coincident(g32,g4)
    c: Coincident(g32,g16)
    c: Horizontal(g32)
    c: Coincident(g33,g4)
    c: Coincident(g33,g16)
    c: Horizontal(g33)
    c: Coincident(g34,g5)
    c: Coincident(g34,g17)
    c: Horizontal(g34)
    c: Coincident(g35,g5)
    c: Coincident(g35,g17)
    c: Horizontal(g35)
    c: Coincident(g36,g6)
    c: Coincident(g36,g19)
    c: Horizontal(g36)
    c: Coincident(g37,g6)
    c: Coincident(g37,g19)
    c: Horizontal(g37)
    c: Coincident(g38,g7)
    c: Coincident(g38,g18)
    c: Horizontal(g38)
    c: Coincident(g39,g7)
    c: Coincident(g39,g18)
    c: Horizontal(g39)
    c: Coincident(g40,g8)
    c: Coincident(g40,g20)
    c: Horizontal(g40)
    c: Coincident(g41,g8)
    c: Coincident(g41,g20)
    c: Horizontal(g41)
    c: Coincident(g42,g9)
    c: Coincident(g42,g23)
    c: Horizontal(g42)
    c: Coincident(g43,g9)
    c: Coincident(g43,g23)
    c: Horizontal(g43)
    c: Coincident(g44,g10)
    c: Coincident(g44,g22)
    c: Horizontal(g44)
    c: Coincident(g45,g10)
    c: Coincident(g45,g22)
    c: Horizontal(g45)
    c: Coincident(g46,g11)
    c: Coincident(g46,g21)
    c: Horizontal(g46)
    c: Coincident(g47,g11)
    c: Coincident(g47,g21)
    c: Horizontal(g47)
FEATURE [Part::Extrusion] Extrude061
  Base = -> Sketch070
  Dir = (1,0,0)
  DirMode = 2
  FaceMakerClass = Part::FaceMakerBullseye
  LengthFwd = 23
  LengthRev = 0
  Placement = pos=(-19,0,0) rot=(0,0,1;0rad)
  Solid = true
  Symmetric = false
FEATURE [Part::Fillet] Fillet052  label="removeToCreateVentalationHoles002"
  Base = -> Extrude061
  Edges = <same value as first occurrence — deduplicated (x6 in doc)>
  Placement = pos=(7,0.02,0) rot=(0,0,1;0rad)
FEATURE [Part::MultiFuse] Fusion130  label="bottom013"
  Shapes = -> [Cut054,Cut034]
FEATURE [Part::Cut] Cut055
  Base = -> Fusion130
  Tool = -> Fillet052
FEATURE [Part::Cylinder] Cylinder054
  Angle = 360
  AttacherType = Attacher::AttachEngine3D
  Height = 20
  Placement = pos=(0,0,36.15) rot=(0,0,1;0rad)
  Radius = 4
FEATURE [Sketcher::SketchObject] Sketch071  label="bottomSketch002"
  FullyConstrained = true
  sketch-geometry (32):
    g0: LineSegment StartX=3.3 StartY=-6.03275e-07 StartZ=0 EndX=98 EndY=-6.03275e-07 EndZ=0
    g1: ArcOfCircle CenterX=98 CenterY=19 CenterZ=0 NormalX=0 NormalY=0 NormalZ=1 AngleXU=0 Radius=19 StartAngle=4.71239 EndAngle=5.71103
    g2: LineSegment StartX=6.3 StartY=8 StartZ=0 EndX=3.3 EndY=8 EndZ=0
    g3: LineSegment StartX=3.3 StartY=8 StartZ=0 EndX=3.3 EndY=-6.03275e-07 EndZ=0
    g4: ArcOfCircle CenterX=8.3 CenterY=5 CenterZ=0 NormalX=0 NormalY=0 NormalZ=1 AngleXU=0 Radius=2 StartAngle=3.14159 EndAngle=4.71239
    g5: LineSegment StartX=6.3 StartY=8 StartZ=0 EndX=6.3 EndY=5 EndZ=0
    g6: ArcOfCircle CenterX=98 CenterY=19 CenterZ=0 NormalX=0 NormalY=0 NormalZ=1 AngleXU=0 Radius=12.7 StartAngle=4.71239 EndAngle=6.28319
    g7: LineSegment StartX=94.7 StartY=3 StartZ=0 EndX=8.3 EndY=3 EndZ=0
    g8-g12: Circle x5 (B-spline internal-alignment scaffolding for g13; pole/knot coordinates omitted)
    g13: BSplineCurve PolesCount=5 KnotsCount=3 Degree=3 IsPeriodic=0
    g14: GeomPoint X=98 Y=6.3 Z=0
    g15: GeomPoint X=96.3938 Y=4.71946 Z=0
    g16: GeomPoint X=94.7 Y=3 Z=0
    g17-g23: Circle x7 (B-spline internal-alignment scaffolding for g24; pole/knot coordinates omitted)
    g24: BSplineCurve PolesCount=7 KnotsCount=5 Degree=3 IsPeriodic=0
    g25-g29: GeomPoint x5 (B-spline internal-alignment scaffolding for g24; pole/knot coordinates omitted)
    g30: ArcOfCircle CenterX=98 CenterY=19 CenterZ=0 NormalX=0 NormalY=0 NormalZ=1 AngleXU=0 Radius=15.7 StartAngle=5.81226 EndAngle=6.28319
    g31: LineSegment StartX=110.7 StartY=19 StartZ=0 EndX=113.7 EndY=19 EndZ=0
  constraints (41):
    c: Horizontal(g0)
    c: Coincident(g1,g0)
    c: Block(g1)
    c: Horizontal(g2)
    c: Distance(g2) = 3
    c: Coincident(g3,g2)
    c: Vertical(g3)
    c: Coincident(g3,g0)
    c: Block(g4)
    c: Block(g2)
    c: Coincident(g5,g2)
    c: Coincident(g5,g4)
    c: Vertical(g5)
    c: Coincident(g6,g1)
    c: Block(g6)
    c: Coincident(g7,g4)
    c: Horizontal(g7)
    c: Block(g0)
    c: Block(g7)
    c: Block(g3)
    c: Coincident(g13,g6)
    c: Weight(g8) = 1
    c: Equal(g8, g9-g12) x4
    c: Coincident(g13,g7)
    c: InternalAlignment(g8-g12 -> g13) x5
    c: InternalAlignment(g14,g13)
    c: InternalAlignment(g15,g13)
    c: InternalAlignment(g16,g13)
    c: Block(g13)
    c: Weight(g17) = 1
    c: Equal(g17, g18-g23) x6
    c: Coincident(g24,g1)
    c: InternalAlignment(g17-g23 -> g24) x7
    c: InternalAlignment(g25-g29 -> g24) x5
    c: Block(g24)
    c: Coincident(g30,g24)
    c: Coincident(g31,g6)
    c: Coincident(g31,g30)
    c: Horizontal(g31)
    c: Block(g31)
    c: Block(g30)
FEATURE [Part::Extrusion] Extrude062  label="bottom014"
  Base = -> Sketch071
  Dir = (0,0,1)
  DirMode = 2
  FaceMakerClass = Part::FaceMakerBullseye
  LengthFwd = 71.4
  LengthRev = 0
  Placement = pos=(0,0,0.3) rot=(0,0,1;0rad)
  Solid = true
  Symmetric = false
FEATURE [Part::Fillet] Fillet054
  Base = -> Extrude062
  Edges = 1 edges r=2.4: [Edge17]
FEATURE [Part::Fillet] Fillet055  label="bottom015"
  Base = -> Fillet054
  Edges = 1 edges r=2.4: [Edge36]
FEATURE [Part::Cylinder] Cylinder055
  Angle = 360
  AttacherType = Attacher::AttachEngine3D
  Height = 10
  Placement = pos=(0,0,36.15) rot=(0,0,1;0rad)
  Radius = 4
FEATURE [Part::MultiFuse] Fusion131  label="removeToCreateHoleForPlugHousing002"
  Placement = pos=(70,19,36.15) rot=(0,1,0;1.5708rad)
  Shapes = -> [Cylinder054,Cylinder055]
FEATURE [Part::Cut] Cut056  label="Bottom001"
  Base = -> Fillet055
  Placement = pos=(9,0,0) rot=(0,0,1;0rad)
  Tool = -> Fusion131
FEATURE [Part::Cut] Cut057
  Base = -> Cut055
  Tool = -> Cut056
FEATURE [Sketcher::SketchObject] Sketch072  label="topSketch021"
  FullyConstrained = true
  sketch-geometry (4):
    g0: ArcOfCircle CenterX=105 CenterY=19 CenterZ=0 NormalX=0 NormalY=0 NormalZ=1 AngleXU=0 Radius=20.6155 StartAngle=5.54125 EndAngle=6.28319
    g1: ArcOfCircle CenterX=105 CenterY=19 CenterZ=0 NormalX=0 NormalY=0 NormalZ=1 AngleXU=0 Radius=13 StartAngle=5.54125 EndAngle=6.28319
    g2: LineSegment StartX=118 StartY=19 StartZ=0 EndX=125.616 EndY=19 EndZ=0
    g3: LineSegment StartX=114.583 StartY=10.2157 StartZ=0 EndX=120.197 EndY=5.06982 EndZ=0
  constraints (7):
    c: Block(g0)
    c: Block(g1)
    c: Coincident(g2,g1)
    c: Coincident(g2,g0)
    c: Horizontal(g2)
    c: Coincident(g3,g1)
    c: Coincident(g3,g0)
FEATURE [Part::Extrusion] Extrude063  label="bottomPlugHousingBit003"
  Base = -> Sketch072
  Dir = (0,0,1)
  DirMode = 2
  FaceMakerClass = Part::FaceMakerBullseye
  LengthFwd = 72
  LengthRev = 0
  Solid = true
  Symmetric = false
FEATURE [Part::Cylinder] Cylinder056
  Angle = 360
  AttacherType = Attacher::AttachEngine3D
  Height = 20
  Placement = pos=(0,0,36.15) rot=(0,0,1;0rad)
  Radius = 14.3
FEATURE [Part::Cylinder] Cylinder057
  Angle = 360
  AttacherType = Attacher::AttachEngine3D
  Height = 10
  Placement = pos=(0,0,36.15) rot=(0,0,1;0rad)
  Radius = 4
FEATURE [Part::Box] Box034  label="removeToCreteHoleForPlugHousing047"
  AttacherType = Attacher::AttachEngine3D
  Height = 28.6
  Length = 20
  Placement = pos=(106.15,0,21.7) rot=(0,0,1;0rad)
  Width = 19
FEATURE [Part::Cylinder] Cylinder058
  Angle = 360
  AttacherType = Attacher::AttachEngine3D
  Height = 20
  Placement = pos=(0,0,36.15) rot=(0,0,1;0rad)
  Radius = 14.3
FEATURE [Part::Cylinder] Cylinder059
  Angle = 360
  AttacherType = Attacher::AttachEngine3D
  Height = 10
  Placement = pos=(0,0,36.15) rot=(0,0,1;0rad)
  Radius = 4
FEATURE [Part::MultiFuse] Fusion134  label="removeToCreteHoleForPlugHousing046"
  Placement = pos=(70,19,36) rot=(0,1,0;1.5708rad)
  Shapes = -> [Cylinder058,Cylinder059]
FEATURE [Part::Cylinder] Cylinder060
  Angle = 360
  AttacherType = Attacher::AttachEngine3D
  Height = 20
  Placement = pos=(0,0,36.15) rot=(0,0,1;0rad)
  Radius = 14
FEATURE [Part::Cylinder] Cylinder061
  Angle = 360
  AttacherType = Attacher::AttachEngine3D
  Height = 10
  Placement = pos=(0,0,36.15) rot=(0,0,1;0rad)
  Radius = 4
FEATURE [Part::MultiFuse] Fusion135  label="removeToCreteHoleForPlugHousing048"
  Placement = pos=(70,19,36) rot=(0,1,0;1.5708rad)
  Shapes = -> [Cylinder060,Cylinder061]
FEATURE [Part::Box] Box035  label="removeToCreteHoleForPlugHousing049"
  AttacherType = Attacher::AttachEngine3D
  Height = 28.6
  Length = 20
  Placement = pos=(106.15,0,21.7) rot=(0,0,1;0rad)
  Width = 19
FEATURE [Part::MultiFuse] Fusion133  label="removeToCreteHoleForPlugHousing045"
  Placement = pos=(0,0,-28.3) rot=(0,0,1;0rad)
  Shapes = -> [Box035,Fusion134]
FEATURE [Part::MultiFuse] Fusion138  label="removeToCreteHoleForPlugHousing051"
  Placement = pos=(70,19,36) rot=(0,1,0;1.5708rad)
  Shapes = -> [Cylinder056,Cylinder057]
FEATURE [Part::MultiFuse] Fusion137  label="removeToCreteHoleForPlugHousing050"
  Placement = pos=(0,0,28.3) rot=(0,0,1;0rad)
  Shapes = -> [Box034,Fusion138]
FEATURE [Part::MultiFuse] Fusion132  label="removeToCreatePlugHousingBottomBit002"
  Shapes = -> [Fusion133,Fusion137]
FEATURE [Part::MultiFuse] Fusion136  label="removeToCreatePlugHousingBottomBit003"
  Shapes = -> [Fusion135,Fusion132]
FEATURE [Part::Cut] Cut058  label="bottomPlugHousingBit002"
  Base = -> Extrude063
  Placement = pos=(-0.09,0,0) rot=(0,0,1;0rad)
  Tool = -> Fusion136
FEATURE [Sketcher::SketchObject] Sketch073  label="bottomSketch003"
  FullyConstrained = true
  sketch-geometry (45):
    g0: LineSegment StartX=6.29999 StartY=8 StartZ=0 EndX=3.29999 EndY=8 EndZ=0
    g1: LineSegment StartX=3.29999 StartY=8 StartZ=0 EndX=3.29999 EndY=-6.03275e-07 EndZ=0
    g2: ArcOfCircle CenterX=8.29999 CenterY=5 CenterZ=0 NormalX=0 NormalY=0 NormalZ=1 AngleXU=0 Radius=2 StartAngle=3.14159 EndAngle=4.71239
    g3: LineSegment StartX=6.29999 StartY=8 StartZ=0 EndX=6.29999 EndY=5 EndZ=0
    g4: ArcOfCircle CenterX=105 CenterY=19 CenterZ=0 NormalX=0 NormalY=0 NormalZ=1 AngleXU=0 Radius=12.7 StartAngle=4.71239 EndAngle=5.94289
    g5-g11: Circle x7 (B-spline internal-alignment scaffolding for g12; pole/knot coordinates omitted)
    g12: BSplineCurve PolesCount=7 KnotsCount=5 Degree=3 IsPeriodic=0
    g13-g17: GeomPoint x5 (B-spline internal-alignment scaffolding for g12; pole/knot coordinates omitted)
    g18: ArcOfCircle CenterX=105 CenterY=19 CenterZ=0 NormalX=0 NormalY=0 NormalZ=1 AngleXU=0 Radius=15.7 StartAngle=5.81226 EndAngle=6.28319
    g19: BSplineCurve PolesCount=5 KnotsCount=3 Degree=3 IsPeriodic=0
    g20: LineSegment StartX=8.29999 StartY=3 StartZ=0 EndX=101.7 EndY=3 EndZ=0
    g21: LineSegment StartX=3.29999 StartY=-6.03275e-07 StartZ=0 EndX=105 EndY=-6.03275e-07 EndZ=0
    g22: LineSegment StartX=120.974 StartY=8.71251 StartZ=0 EndX=122.332 EndY=7.83778 EndZ=0
    g23: LineSegment StartX=105 StartY=-6.03274e-07 StartZ=0 EndX=113 EndY=-6.03274e-07 EndZ=0
    g24: ArcOfCircle CenterX=105 CenterY=19 CenterZ=0 NormalX=0 NormalY=0 NormalZ=1 AngleXU=0 Radius=20.6155 StartAngle=5.11091 EndAngle=5.71103
    g25: ArcOfCircle CenterX=117.7 CenterY=19 CenterZ=0 NormalX=0 NormalY=0 NormalZ=1 AngleXU=0 Radius=3 StartAngle=1.2e-15 EndAngle=2.10468
    g26: Circle CenterX=116.345 CenterY=16.3232 CenterZ=0 NormalX=0 NormalY=0 NormalZ=1 AngleXU=0 Radius=1
    g27: Circle CenterX=117.24 CenterY=15.7584 CenterZ=0 NormalX=0 NormalY=0 NormalZ=1 AngleXU=0 Radius=1
    g28: Circle CenterX=116.972 CenterY=14.7612 CenterZ=0 NormalX=0 NormalY=0 NormalZ=1 AngleXU=0 Radius=1
    g29: BSplineCurve PolesCount=3 KnotsCount=2 Degree=2 IsPeriodic=0
    g30: GeomPoint X=116.345 Y=16.3232 Z=0
    g31: GeomPoint X=116.972 Y=14.7612 Z=0
    g32: Circle CenterX=115.828 CenterY=17.157 CenterZ=0 NormalX=0 NormalY=0 NormalZ=1 AngleXU=0 Radius=1
    g33: Circle CenterX=115.841 CenterY=16.639 CenterZ=0 NormalX=0 NormalY=0 NormalZ=1 AngleXU=0 Radius=1
    g34: Circle CenterX=116.345 CenterY=16.3232 CenterZ=0 NormalX=0 NormalY=0 NormalZ=1 AngleXU=0 Radius=1
    g35: BSplineCurve PolesCount=3 KnotsCount=2 Degree=2 IsPeriodic=0
    g36: GeomPoint X=115.828 Y=17.157 Z=0
    g37: GeomPoint X=116.345 Y=16.3232 Z=0
    g38: LineSegment StartX=115.828 StartY=17.157 StartZ=0 EndX=115.828 EndY=20.8307 EndZ=0
    g39: Circle CenterX=115.828 CenterY=20.8307 CenterZ=0 NormalX=0 NormalY=0 NormalZ=1 AngleXU=0 Radius=1
    g40: Circle CenterX=115.831 CenterY=21.3396 CenterZ=0 NormalX=0 NormalY=0 NormalZ=1 AngleXU=0 Radius=1
    g41: Circle CenterX=116.173 CenterY=21.5825 CenterZ=0 NormalX=0 NormalY=0 NormalZ=1 AngleXU=0 Radius=1
    g42: BSplineCurve PolesCount=3 KnotsCount=2 Degree=2 IsPeriodic=0
    g43: GeomPoint X=115.828 Y=20.8307 Z=0
    g44: GeomPoint X=116.173 Y=21.5825 Z=0
  constraints (70):
    c: Horizontal(g0)
    c: Distance(g0) = 3
    c: Coincident(g1,g0)
    c: Vertical(g1)
    c: Block(g2)
    c: Block(g0)
    c: Coincident(g3,g0)
    c: Coincident(g3,g2)
    c: Vertical(g3)
    c: Block(g1)
    c: Block(g4)
    c: Coincident(g19,g4)
    c: Block(g19)
    c: Equal(g5, g6-g11) x6
    c: InternalAlignment(g5-g11 -> g12) x7
    c: InternalAlignment(g13-g17 -> g12) x5
    c: Block(g12)
    c: Coincident(g18,g12)
    c: Block(g18)
    c: Coincident(g20,g2)
    c: Coincident(g20,g19)
    c: Horizontal(g20)
    c: Distance(g20) = 93.4
    c: Coincident(g21,g1)
    c: Horizontal(g21)
    c: Distance(g21) = 101.7
    c: Horizontal(g23)
    c: Distance(g23) = 8
    c: Coincident(g24,g23)
    c: Block(g23)
    c: Coincident(g22,g24)
    c: Block(g24)
    c: Block(g22)
    c: Distance(g22) = 1.61553
    c: Coincident(g25,g18)
    c: Block(g25)
    c: Weight(g26) = 1
    c: Equal(g26,g27)
    c: Equal(g26,g28)
    c: Coincident(g29,g4)
    c: InternalAlignment(g26,g29)
    c: InternalAlignment(g27,g29)
    c: InternalAlignment(g28,g29)
    c: InternalAlignment(g30,g29)
    c: InternalAlignment(g31,g29)
    c: Block(g29)
    c: Weight(g32) = 1
    c: Equal(g32,g33)
    c: Equal(g32,g34)
    c: Coincident(g35,g29)
    c: InternalAlignment(g32,g35)
    c: InternalAlignment(g33,g35)
    c: InternalAlignment(g34,g35)
    c: InternalAlignment(g36,g35)
    c: InternalAlignment(g37,g35)
    c: Block(g35)
    c: Coincident(g38,g35)
    c: Vertical(g38)
    c: Block(g38)
    c: Coincident(g42,g38)
    c: Weight(g39) = 1
    c: Equal(g39,g40)
    c: Equal(g39,g41)
    c: Coincident(g42,g25)
    c: InternalAlignment(g39,g42)
    c: InternalAlignment(g40,g42)
    c: InternalAlignment(g41,g42)
    c: InternalAlignment(g43,g42)
    c: InternalAlignment(g44,g42)
    c: Block(g42)
FEATURE [Part::Extrusion] Extrude064  label="bottom016"
  Base = -> Sketch073
  Dir = (0,0,1)
  DirMode = 2
  FaceMakerClass = Part::FaceMakerBullseye
  LengthFwd = 71.4
  LengthRev = 0
  Placement = pos=(0,0,0.3) rot=(0,0,1;0rad)
  Solid = true
  Symmetric = false
FEATURE [Part::Revolution] Revolve157  label="removeToCreateScrewAndThreadedInsertHole063"
  Angle = 360
  Axis = (0,1,0)
  Base = (0,0,0)
  FaceMakerClass = Part::FaceMakerBullseye
  Placement = pos=(12.5,0,10) rot=(0,0,1;0rad)
  Solid = false
  Source = -> Face141
  Symmetric = false
FEATURE [Sketcher::SketchObject] Sketch074
  FullyConstrained = true
  Placement = pos=(117,19,0) rot=(0.57735,0.57735,0.57735;2.0944rad)
  sketch-geometry (48):
    g0: LineSegment StartX=-49.19 StartY=69.25 StartZ=0 EndX=-49.19 EndY=66.25 EndZ=0
    g1: LineSegment StartX=-49.19 StartY=63.5 StartZ=0 EndX=-49.19 EndY=60.5 EndZ=0
    g2: LineSegment StartX=-49.19 StartY=57.75 StartZ=0 EndX=-49.19 EndY=54.75 EndZ=0
    g3: LineSegment StartX=-49.19 StartY=52 StartZ=0 EndX=-49.19 EndY=49 EndZ=0
    g4: LineSegment StartX=-49.19 StartY=46.25 StartZ=0 EndX=-49.19 EndY=43.25 EndZ=0
    g5: LineSegment StartX=-49.19 StartY=40.5 StartZ=0 EndX=-49.19 EndY=37.5 EndZ=0
    g6: LineSegment StartX=-49.19 StartY=34.5 StartZ=0 EndX=-49.19 EndY=31.5 EndZ=0
    g7: LineSegment StartX=-49.19 StartY=28.75 StartZ=0 EndX=-49.19 EndY=25.75 EndZ=0
    g8: LineSegment StartX=-49.19 StartY=23 StartZ=0 EndX=-49.19 EndY=20 EndZ=0
    g9: LineSegment StartX=-49.19 StartY=17.25 StartZ=0 EndX=-49.19 EndY=14.25 EndZ=0
    g10: LineSegment StartX=-49.19 StartY=11.5 StartZ=0 EndX=-49.19 EndY=8.5 EndZ=0
    g11: LineSegment StartX=-49.19 StartY=5.75 StartZ=0 EndX=-49.19 EndY=2.75 EndZ=0
    g12: ArcOfCircle CenterX=-1.5 CenterY=67.75 CenterZ=0 NormalX=0 NormalY=0 NormalZ=1 AngleXU=0 Radius=1.5 StartAngle=4.71239 EndAngle=7.85398
    g13: ArcOfCircle CenterX=-1.5 CenterY=62 CenterZ=0 NormalX=0 NormalY=0 NormalZ=1 AngleXU=0 Radius=1.5 StartAngle=4.71239 EndAngle=7.85398
    g14: ArcOfCircle CenterX=-1.5 CenterY=56.25 CenterZ=0 NormalX=0 NormalY=0 NormalZ=1 AngleXU=0 Radius=1.5 StartAngle=4.71239 EndAngle=7.85398
    g15: ArcOfCircle CenterX=-11.49 CenterY=50.5 CenterZ=0 NormalX=0 NormalY=0 NormalZ=1 AngleXU=0 Radius=1.5 StartAngle=4.71239 EndAngle=7.85398
    g16: ArcOfCircle CenterX=-16.28 CenterY=44.75 CenterZ=0 NormalX=0 NormalY=0 NormalZ=1 AngleXU=0 Radius=1.5 StartAngle=4.71239 EndAngle=7.85398
    g17: ArcOfCircle CenterX=-18.2337 CenterY=39 CenterZ=0 NormalX=0 NormalY=0 NormalZ=1 AngleXU=0 Radius=1.5 StartAngle=4.71485 EndAngle=7.85398
    g18: ArcOfCircle CenterX=-16.2837 CenterY=27.25 CenterZ=0 NormalX=0 NormalY=0 NormalZ=1 AngleXU=0 Radius=1.5 StartAngle=4.71485 EndAngle=7.85398
    g19: ArcOfCircle CenterX=-18.2337 CenterY=33 CenterZ=0 NormalX=0 NormalY=0 NormalZ=1 AngleXU=0 Radius=1.5 StartAngle=4.71485 EndAngle=7.85398
    g20: ArcOfCircle CenterX=-11.49 CenterY=21.5 CenterZ=0 NormalX=0 NormalY=0 NormalZ=1 AngleXU=0 Radius=1.5 StartAngle=4.71239 EndAngle=7.85398
    g21: ArcOfCircle CenterX=-1.5 CenterY=4.25 CenterZ=0 NormalX=0 NormalY=0 NormalZ=1 AngleXU=0 Radius=1.5 StartAngle=4.71239 EndAngle=7.85398
    g22: ArcOfCircle CenterX=-1.5 CenterY=10 CenterZ=0 NormalX=0 NormalY=0 NormalZ=1 AngleXU=0 Radius=1.5 StartAngle=4.71239 EndAngle=7.85398
    g23: ArcOfCircle CenterX=-1.5 CenterY=15.75 CenterZ=0 NormalX=0 NormalY=0 NormalZ=1 AngleXU=0 Radius=1.5 StartAngle=4.71239 EndAngle=7.85398
    g24: LineSegment StartX=-49.19 StartY=69.25 StartZ=0 EndX=-1.5 EndY=69.25 EndZ=0
    g25: LineSegment StartX=-49.19 StartY=66.25 StartZ=0 EndX=-1.5 EndY=66.25 EndZ=0
    g26: LineSegment StartX=-49.19 StartY=63.5 StartZ=0 EndX=-1.5 EndY=63.5 EndZ=0
    g27: LineSegment StartX=-49.19 StartY=60.5 StartZ=0 EndX=-1.5 EndY=60.5 EndZ=0
    g28: LineSegment StartX=-49.19 StartY=57.75 StartZ=0 EndX=-1.5 EndY=57.75 EndZ=0
    g29: LineSegment StartX=-49.19 StartY=54.75 StartZ=0 EndX=-1.5 EndY=54.75 EndZ=0
    g30: LineSegment StartX=-49.19 StartY=52 StartZ=0 EndX=-11.49 EndY=52 EndZ=0
    g31: LineSegment StartX=-49.19 StartY=49 StartZ=0 EndX=-11.49 EndY=49 EndZ=0
    g32: LineSegment StartX=-49.19 StartY=46.25 StartZ=0 EndX=-16.28 EndY=46.25 EndZ=0
    g33: LineSegment StartX=-49.19 StartY=43.25 StartZ=0 EndX=-16.28 EndY=43.25 EndZ=0
    g34: LineSegment StartX=-49.19 StartY=40.5 StartZ=0 EndX=-18.2337 EndY=40.5 EndZ=0
    g35: LineSegment StartX=-49.19 StartY=37.5 StartZ=0 EndX=-18.23 EndY=37.5 EndZ=0
    g36: LineSegment StartX=-49.19 StartY=34.5 StartZ=0 EndX=-18.2337 EndY=34.5 EndZ=0
    g37: LineSegment StartX=-49.19 StartY=31.5 StartZ=0 EndX=-18.23 EndY=31.5 EndZ=0
    g38: LineSegment StartX=-49.19 StartY=28.75 StartZ=0 EndX=-16.2837 EndY=28.75 EndZ=0
    g39: LineSegment StartX=-49.19 StartY=25.75 StartZ=0 EndX=-16.28 EndY=25.75 EndZ=0
    g40: LineSegment StartX=-49.19 StartY=23 StartZ=0 EndX=-11.49 EndY=23 EndZ=0
    g41: LineSegment StartX=-49.19 StartY=20 StartZ=0 EndX=-11.49 EndY=20 EndZ=0
    g42: LineSegment StartX=-49.19 StartY=17.25 StartZ=0 EndX=-1.5 EndY=17.25 EndZ=0
    g43: LineSegment StartX=-49.19 StartY=14.25 StartZ=0 EndX=-1.5 EndY=14.25 EndZ=0
    g44: LineSegment StartX=-49.19 StartY=11.5 StartZ=0 EndX=-1.5 EndY=11.5 EndZ=0
    g45: LineSegment StartX=-49.19 StartY=8.5 StartZ=0 EndX=-1.5 EndY=8.5 EndZ=0
    g46: LineSegment StartX=-49.19 StartY=5.75 StartZ=0 EndX=-1.5 EndY=5.75 EndZ=0
    g47: LineSegment StartX=-49.19 StartY=2.75 StartZ=0 EndX=-1.5 EndY=2.75 EndZ=0
  constraints (120):
    c: Vertical(g0)
    c: Distance(g0) = 3
    c: Block(g0)
    c: Vertical(g1)
    c: Distance(g1) = 3
    c: Vertical(g2)
    c: Equal(g0,g2) = 3
    c: Block(g2)
    c: Vertical(g3)
    c: Equal(g1,g3) = 3
    c: Vertical(g4)
    c: Equal(g0,g4) = 3
    c: Block(g4)
    c: Vertical(g5)
    c: Equal(g1,g5) = 3
    c: Vertical(g6)
    c: Equal(g0,g6) = 3
    c: Block(g6)
    c: Vertical(g7)
    c: Equal(g1,g7) = 3
    c: Vertical(g8)
    c: Equal(g0,g8) = 3
    c: Block(g8)
    c: Vertical(g9)
    c: Equal(g1,g9) = 3
    c: Vertical(g10)
    c: Equal(g0,g10) = 3
    c: Block(g10)
    c: Vertical(g11)
    c: Equal(g1,g11) = 3
    c: Block(g12)
    c: Block(g13)
    c: Block(g14)
    c: Block(g15)
    c: Block(g16)
    c: Block(g17)
    c: Block(g18)
    c: Block(g19)
    c: Block(g20)
    c: Block(g21)
    c: Block(g22)
    c: Block(g23)
    c: Block(g11)
    c: Block(g9)
    c: Block(g7)
    c: Block(g5)
    c: Block(g3)
    c: Block(g1)
    c: Coincident(g24,g0)
    c: Coincident(g24,g12)
    c: Horizontal(g24)
    c: Coincident(g25,g0)
    c: Coincident(g25,g12)
    c: Horizontal(g25)
    c: Coincident(g26,g1)
    c: Coincident(g26,g13)
    c: Horizontal(g26)
    c: Coincident(g27,g1)
    c: Coincident(g27,g13)
    c: Horizontal(g27)
    c: Coincident(g28,g2)
    c: Coincident(g28,g14)
    c: Horizontal(g28)
    c: Coincident(g29,g2)
    c: Coincident(g29,g14)
    c: Horizontal(g29)
    c: Coincident(g30,g3)
    c: Coincident(g30,g15)
    c: Horizontal(g30)
    c: Coincident(g31,g3)
    c: Coincident(g31,g15)
    c: Horizontal(g31)
    c: Coincident(g32,g4)
    c: Coincident(g32,g16)
    c: Horizontal(g32)
    c: Coincident(g33,g4)
    c: Coincident(g33,g16)
    c: Horizontal(g33)
    c: Coincident(g34,g5)
    c: Coincident(g34,g17)
    c: Horizontal(g34)
    c: Coincident(g35,g5)
    c: Coincident(g35,g17)
    c: Horizontal(g35)
    c: Coincident(g36,g6)
    c: Coincident(g36,g19)
    c: Horizontal(g36)
    c: Coincident(g37,g6)
    c: Coincident(g37,g19)
    c: Horizontal(g37)
    c: Coincident(g38,g7)
    c: Coincident(g38,g18)
    c: Horizontal(g38)
    c: Coincident(g39,g7)
    c: Coincident(g39,g18)
    c: Horizontal(g39)
    c: Coincident(g40,g8)
    c: Coincident(g40,g20)
    c: Horizontal(g40)
    c: Coincident(g41,g8)
    c: Coincident(g41,g20)
    c: Horizontal(g41)
    c: Coincident(g42,g9)
    c: Coincident(g42,g23)
    c: Horizontal(g42)
    c: Coincident(g43,g9)
    c: Coincident(g43,g23)
    c: Horizontal(g43)
    c: Coincident(g44,g10)
    c: Coincident(g44,g22)
    c: Horizontal(g44)
    c: Coincident(g45,g10)
    c: Coincident(g45,g22)
    c: Horizontal(g45)
    c: Coincident(g46,g11)
    c: Coincident(g46,g21)
    c: Horizontal(g46)
    c: Coincident(g47,g11)
    c: Coincident(g47,g21)
    c: Horizontal(g47)
FEATURE [Part::Extrusion] Extrude065
  Base = -> Sketch074
  Dir = (1,0,0)
  DirMode = 2
  FaceMakerClass = Part::FaceMakerBullseye
  LengthFwd = 23
  LengthRev = 0
  Placement = pos=(-19,0,0) rot=(0,0,1;0rad)
  Solid = true
  Symmetric = false
FEATURE [Part::Fillet] Fillet056  label="removeToCreateVentalationHoles003"
  Base = -> Extrude065
  Edges = <same value as first occurrence — deduplicated (x6 in doc)>
  Placement = pos=(7,0.02,0) rot=(0,0,1;0rad)
FEATURE [Part::Revolution] Revolve158  label="removeToCreateScrewAndThreadedInsertHole065"
  Angle = 360
  Axis = (0,1,0)
  Base = (0,0,0)
  FaceMakerClass = Part::FaceMakerBullseye
  Placement = pos=(12.5,0,62) rot=(0,0,1;0rad)
  Solid = false
  Source = -> Face146
  Symmetric = false
FEATURE [Part::Revolution] Revolve159  label="removeToCreateScrewAndThreadedInsertHole066"
  Angle = 360
  Axis = (0,1,0)
  Base = (0,0,0)
  FaceMakerClass = Part::FaceMakerBullseye
  Placement = pos=(89.5,0,68.5) rot=(0,0,1;0rad)
  Solid = false
  Source = -> Face143
  Symmetric = false
FEATURE [Part::Revolution] Revolve160  label="removeToCreateScrewAndThreadedInsertHole067"
  Angle = 360
  Axis = (0,1,0)
  Base = (0,0,0)
  FaceMakerClass = Part::FaceMakerBullseye
  Placement = pos=(89.5,0,3.5) rot=(0,0,1;0rad)
  Solid = false
  Source = -> Face142
  Symmetric = false
FEATURE [Part::Revolution] Revolve161  label="removeToCreateScrewAndThreadedInsertHole068"
  Angle = 360
  Axis = (0,1,0)
  Base = (0,0,0)
  FaceMakerClass = Part::FaceMakerBullseye
  Placement = pos=(109.5,4.7,3.5) rot=(0,0,1;0rad)
  Solid = false
  Source = -> Face145
  Symmetric = false
FEATURE [Part::Revolution] Revolve162  label="removeToCreateScrewAndThreadedInsertHole069"
  Angle = 360
  Axis = (0,1,0)
  Base = (0,0,0)
  FaceMakerClass = Part::FaceMakerBullseye
  Placement = pos=(109.5,4.7,68.5) rot=(0,0,1;0rad)
  Solid = false
  Source = -> Face144
  Symmetric = false
FEATURE [Part::MultiFuse] Fusion141  label="removeToCreateScrewAndThreadedInsertHole064"
  Shapes = -> [Revolve162,Revolve161,Revolve160,Revolve159,Revolve158,Revolve157]
FEATURE [Part::Cylinder] Cylinder062
  Angle = 360
  AttacherType = Attacher::AttachEngine3D
  Height = 20
  Placement = pos=(0,0,36.15) rot=(0,0,1;0rad)
  Radius = 14
FEATURE [Part::Cylinder] Cylinder063
  Angle = 360
  AttacherType = Attacher::AttachEngine3D
  Height = 10
  Placement = pos=(0,0,36.15) rot=(0,0,1;0rad)
  Radius = 4
FEATURE [Part::MultiFuse] Fusion139  label="removeToCreteHoleForPlugHousing052"
  Placement = pos=(70,19,36) rot=(0,1,0;1.5708rad)
  Shapes = -> [Cylinder062,Cylinder063]
FEATURE [Part::Cut] Cut060  label="bottom017"
  Base = -> Extrude064
  Tool = -> Fusion139
FEATURE [Part::Cut] Cut061  label="bottom019"
  Base = -> Cut060
  Tool = -> Fusion141
FEATURE [Part::MultiFuse] Fusion140  label="bottom018"
  Shapes = -> [Cut061,Cut058]
FEATURE [Part::Cut] Cut059  label="bottom020"
  Base = -> Fusion140
  Tool = -> Fillet056
FEATURE [Part::Box] Box036  label="Cube021"
  AttacherType = Attacher::AttachEngine3D
  Height = 80
  Length = 26
  Placement = pos=(0,-1,-5) rot=(0,0,1;0rad)
  Width = 11
FEATURE [Part::Cut] Cut062  label="removeFromBottom002"
  Base = -> Cut057
  Tool = -> Box036
FEATURE [Part::Cut] Cut063
  Base = -> Cut059
  Tool = -> Cut062
FEATURE [Part::Cut] Cut064  label="pcbStands"
  Base = -> Fusion095
  Tool = -> Fusion127
FEATURE [Sketcher::SketchObject] Sketch075  label="topSketch022"
  FullyConstrained = true
  sketch-geometry (6):
    g0: LineSegment StartX=19 StartY=38 StartZ=0 EndX=117 EndY=38 EndZ=0
    g1: ArcOfCircle CenterX=19 CenterY=19 CenterZ=0 NormalX=0 NormalY=0 NormalZ=1 AngleXU=0 Radius=19 StartAngle=1.5708 EndAngle=3.14159
    g2: LineSegment StartX=117 StartY=38 StartZ=0 EndX=117 EndY=19 EndZ=0
    g3: LineSegment StartX=98 StartY=1.0161e-12 StartZ=0 EndX=5.22862e-06 EndY=1.0161e-12 EndZ=0
    g4: LineSegment StartX=5.22862e-06 StartY=19 StartZ=0 EndX=5.22862e-06 EndY=1.0161e-12 EndZ=0
    g5: ArcOfCircle CenterX=98 CenterY=19 CenterZ=0 NormalX=0 NormalY=0 NormalZ=1 AngleXU=0 Radius=19 StartAngle=4.71239 EndAngle=6.28319
  constraints (16):
    c: Horizontal(g0)
    c: Distance(g0) = 98
    c: Coincident(g1,g0)
    c: Block(g1)
    c: Coincident(g2,g0)
    c: Vertical(g2)
    c: Distance(g2) = 19
    c: Horizontal(g3)
    c: Coincident(g4,g1)
    c: Vertical(g4)
    c: Coincident(g3,g4)
    c: Block(g3)
    c: Coincident(g5,g2)
    c: Coincident(g5,g3)
    c: Block(g0)
    c: Block(g5)
FEATURE [Part::Extrusion] Extrude067  label="sideB003"
  Base = -> Sketch075
  Dir = (0,0,1)
  DirMode = 2
  FaceMakerClass = Part::FaceMakerBullseye
  LengthFwd = 3
  LengthRev = 0
  Placement = pos=(0,0,71.7) rot=(0,0,1;0rad)
  Solid = true
  Symmetric = false
FEATURE [Sketcher::SketchObject] Sketch076  label="topSketch023"
  FullyConstrained = true
  sketch-geometry (6):
    g0: LineSegment StartX=19 StartY=38 StartZ=0 EndX=117 EndY=38 EndZ=0
    g1: ArcOfCircle CenterX=19 CenterY=19 CenterZ=0 NormalX=0 NormalY=0 NormalZ=1 AngleXU=0 Radius=19 StartAngle=1.5708 EndAngle=3.14159
    g2: LineSegment StartX=117 StartY=38 StartZ=0 EndX=117 EndY=19 EndZ=0
    g3: LineSegment StartX=98 StartY=1.0161e-12 StartZ=0 EndX=5.22862e-06 EndY=1.0161e-12 EndZ=0
    g4: LineSegment StartX=5.22862e-06 StartY=19 StartZ=0 EndX=5.22862e-06 EndY=1.0161e-12 EndZ=0
    g5: ArcOfCircle CenterX=98 CenterY=19 CenterZ=0 NormalX=0 NormalY=0 NormalZ=1 AngleXU=0 Radius=19 StartAngle=4.71239 EndAngle=6.28319
  constraints (16):
    c: Horizontal(g0)
    c: Distance(g0) = 98
    c: Coincident(g1,g0)
    c: Block(g1)
    c: Coincident(g2,g0)
    c: Vertical(g2)
    c: Distance(g2) = 19
    c: Horizontal(g3)
    c: Coincident(g4,g1)
    c: Vertical(g4)
    c: Coincident(g3,g4)
    c: Block(g3)
    c: Coincident(g5,g2)
    c: Coincident(g5,g3)
    c: Block(g0)
    c: Block(g5)
FEATURE [Part::Extrusion] Extrude066  label="sideA003"
  Base = -> Sketch076
  Dir = (0,0,1)
  DirMode = 2
  FaceMakerClass = Part::FaceMakerBullseye
  LengthFwd = 3
  LengthRev = 0
  Placement = pos=(0,0,-2.7) rot=(0,0,1;0rad)
  Solid = true
  Symmetric = false
FEATURE [Part::MultiFuse] Fusion142  label="removeFromBottom003"
  Placement = pos=(2,0,0) rot=(0,0,1;0rad)
  Shapes = -> [Extrude066,Extrude067]
FEATURE [Part::Cut] Cut065  label="screwRetainers002"
  Base = -> Fusion096
  Tool = -> Fusion142
FEATURE [Sketcher::SketchObject] Sketch077
  FullyConstrained = true
  Placement = pos=(117,19,0) rot=(0.57735,0.57735,0.57735;2.0944rad)
  sketch-geometry (8):
    g0: LineSegment StartX=-49.19 StartY=63.5 StartZ=0 EndX=-49.19 EndY=60.5 EndZ=0
    g1: LineSegment StartX=-49.19 StartY=11.5 StartZ=0 EndX=-49.19 EndY=8.5 EndZ=0
    g2: ArcOfCircle CenterX=-1.5 CenterY=62 CenterZ=0 NormalX=0 NormalY=0 NormalZ=1 AngleXU=0 Radius=1.5 StartAngle=4.71239 EndAngle=7.85398
    g3: ArcOfCircle CenterX=-1.5 CenterY=10 CenterZ=0 NormalX=0 NormalY=0 NormalZ=1 AngleXU=0 Radius=1.5 StartAngle=4.71239 EndAngle=7.85398
    g4: LineSegment StartX=-49.19 StartY=63.5 StartZ=0 EndX=-1.5 EndY=63.5 EndZ=0
    g5: LineSegment StartX=-49.19 StartY=60.5 StartZ=0 EndX=-1.5 EndY=60.5 EndZ=0
    g6: LineSegment StartX=-49.19 StartY=11.5 StartZ=0 EndX=-1.5 EndY=11.5 EndZ=0
    g7: LineSegment StartX=-49.19 StartY=8.5 StartZ=0 EndX=-1.5 EndY=8.5 EndZ=0
  constraints (19):
    c: Vertical(g0)
    c: Distance(g0) = 3
    c: Vertical(g1)
    c: Block(g1)
    c: Block(g2)
    c: Block(g3)
    c: Block(g0)
    c: Coincident(g4,g0)
    c: Coincident(g4,g2)
    c: Horizontal(g4)
    c: Coincident(g5,g0)
    c: Coincident(g5,g2)
    c: Horizontal(g5)
    c: Coincident(g6,g1)
    c: Coincident(g6,g3)
    c: Horizontal(g6)
    c: Coincident(g7,g1)
    c: Coincident(g7,g3)
    c: Horizontal(g7)
FEATURE [Part::Extrusion] Extrude068
  Base = -> Sketch077
  Dir = (1,0,0)
  DirMode = 2
  FaceMakerClass = Part::FaceMakerBullseye
  LengthFwd = 10
  LengthRev = 0
  Solid = true
  Symmetric = false
FEATURE [Part::Fillet] Fillet057  label="removeFromtMoreFrontCaseScrewRetainers002"
  Base = -> Extrude068
  Edges = 4 edges r=1.49: [Edge6,Edge11,Edge18,Edge23]
  Placement = pos=(-12,0,0) rot=(0,0,1;0rad)
FEATURE [Sketcher::SketchObject] Sketch078
  FullyConstrained = true
  Placement = pos=(117,19,0) rot=(0.57735,0.57735,0.57735;2.0944rad)
  sketch-geometry (8):
    g0: LineSegment StartX=-49.19 StartY=69.25 StartZ=0 EndX=-49.19 EndY=66.25 EndZ=0
    g1: LineSegment StartX=-49.19 StartY=5.75 StartZ=0 EndX=-49.19 EndY=2.75 EndZ=0
    g2: ArcOfCircle CenterX=-1.5 CenterY=67.75 CenterZ=0 NormalX=0 NormalY=0 NormalZ=1 AngleXU=0 Radius=1.5 StartAngle=4.71239 EndAngle=7.85398
    g3: ArcOfCircle CenterX=-1.5 CenterY=4.25 CenterZ=0 NormalX=0 NormalY=0 NormalZ=1 AngleXU=0 Radius=1.5 StartAngle=4.71239 EndAngle=7.85398
    g4: LineSegment StartX=-49.19 StartY=69.25 StartZ=0 EndX=-1.5 EndY=69.25 EndZ=0
    g5: LineSegment StartX=-49.19 StartY=66.25 StartZ=0 EndX=-1.5 EndY=66.25 EndZ=0
    g6: LineSegment StartX=-49.19 StartY=5.75 StartZ=0 EndX=-1.5 EndY=5.75 EndZ=0
    g7: LineSegment StartX=-49.19 StartY=2.75 StartZ=0 EndX=-1.5 EndY=2.75 EndZ=0
  constraints (19):
    c: Vertical(g0)
    c: Distance(g0) = 3
    c: Block(g0)
    c: Vertical(g1)
    c: Block(g2)
    c: Block(g3)
    c: Block(g1)
    c: Coincident(g4,g0)
    c: Coincident(g4,g2)
    c: Horizontal(g4)
    c: Coincident(g5,g0)
    c: Coincident(g5,g2)
    c: Horizontal(g5)
    c: Coincident(g6,g1)
    c: Coincident(g6,g3)
    c: Horizontal(g6)
    c: Coincident(g7,g1)
    c: Coincident(g7,g3)
    c: Horizontal(g7)
FEATURE [Part::Extrusion] Extrude069
  Base = -> Sketch078
  Dir = (1,0,0)
  DirMode = 2
  FaceMakerClass = Part::FaceMakerBullseye
  LengthFwd = 10
  LengthRev = 0
  Solid = true
  Symmetric = false
FEATURE [Part::Fillet] Fillet058  label="removeFromtMoreFrontCaseScrewRetainers003"
  Base = -> Extrude069
  Edges = 4 edges r=1.49: [Edge6,Edge11,Edge18,Edge23]
  Placement = pos=(-4,0,0) rot=(0,0,1;0rad)
FEATURE [Part::Cut] Cut066
  Base = -> Cut065
  Tool = -> Fillet058
FEATURE [Part::Cut] Cut067  label="screwPillars"
  Base = -> Cut066
  Tool = -> Fillet057
FEATURE [Part::MultiFuse] Fusion143  label="bottom021"
  Shapes = -> [Cut031,Cut063]
FEATURE [Part::Cylinder] Cylinder
  Angle = 360
  AttacherType = Attacher::AttachEngine3D
  Height = 10
  Placement = pos=(20.65,12,4.68) rot=(1,0,0;1.5708rad)
  Radius = 2
FEATURE [Part::Cylinder] Cylinder064
  Angle = 360
  AttacherType = Attacher::AttachEngine3D
  Height = 10
  Placement = pos=(20.65,12,67.38) rot=(1,0,0;1.5708rad)
  Radius = 2
FEATURE [Part::Cylinder] Cylinder065
  Angle = 360
  AttacherType = Attacher::AttachEngine3D
  Height = 10
  Placement = pos=(77.15,12,67.38) rot=(1,0,0;1.5708rad)
  Radius = 2
FEATURE [Part::Cylinder] Cylinder066
  Angle = 360
  AttacherType = Attacher::AttachEngine3D
  Height = 10
  Placement = pos=(77.15,12,4.68) rot=(1,0,0;1.5708rad)
  Radius = 2
FEATURE [Part::MultiFuse] Fusion144  label="removeFromThreadedInsertHousing"
  Shapes = -> [Cylinder065,Cylinder064,Cylinder,Cylinder066]
FEATURE [Part::Cut] Cut068  label="pcbStands001"
  Base = -> Cut064
  Tool = -> Fusion144
FEATURE [Part::MultiFuse] Fusion145
  Shapes = -> [Cut068,Fusion143]
FEATURE [Part::MultiFuse] Fusion146
  Shapes = -> [Fusion145]
FEATURE [Part::MultiFuse] Fusion147  label="bottom022"
  Shapes = -> [Cut067,Fusion146]
FEATURE [Part::MultiFuse] Fusion148  label="casePillars005"
  Shapes = -> [Cut047,Fusion092]
FEATURE [Part::MultiFuse] Fusion149  label="bottom023"
  Shapes = -> [Fusion124,Fusion113,Fusion147]
FEATURE [Part::MultiFuse] Fusion150  label="topBits"
  Shapes = -> [Cut025,Fusion148,Cut030,Fillet034]
FEATURE [Part::Feature] Face149 .. Face152  x4 (patterned run collapsed; names and placements below)
  shape: bbox 3.2 x 1.5 x 2e-07 mm, 1 faces, 0 solids (baked)
FEATURE [Part::Feature] Face153
  shape: bbox 3.6 x 3.2 x 2e-07 mm, 1 faces, 0 solids (baked)
FEATURE [Part::Feature] Face154
  shape: bbox 3.6 x 3.2 x 2e-07 mm, 1 faces, 0 solids (baked)
FEATURE [Sketcher::SketchObject] Sketch079  label="topSketch024"
  FullyConstrained = true
  sketch-geometry (6):
    g0: LineSegment StartX=19 StartY=38 StartZ=0 EndX=117 EndY=38 EndZ=0
    g1: ArcOfCircle CenterX=19 CenterY=19 CenterZ=0 NormalX=0 NormalY=0 NormalZ=1 AngleXU=0 Radius=19 StartAngle=1.5708 EndAngle=3.14159
    g2: LineSegment StartX=117 StartY=38 StartZ=0 EndX=117 EndY=19 EndZ=0
    g3: LineSegment StartX=98 StartY=1.0161e-12 StartZ=0 EndX=5.22862e-06 EndY=1.0161e-12 EndZ=0
    g4: LineSegment StartX=5.22862e-06 StartY=19 StartZ=0 EndX=5.22862e-06 EndY=1.0161e-12 EndZ=0
    g5: ArcOfCircle CenterX=98 CenterY=19 CenterZ=0 NormalX=0 NormalY=0 NormalZ=1 AngleXU=0 Radius=19 StartAngle=4.71239 EndAngle=6.28319
  constraints (16):
    c: Horizontal(g0)
    c: Distance(g0) = 98
    c: Coincident(g1,g0)
    c: Block(g1)
    c: Coincident(g2,g0)
    c: Vertical(g2)
    c: Distance(g2) = 19
    c: Horizontal(g3)
    c: Coincident(g4,g1)
    c: Vertical(g4)
    c: Coincident(g3,g4)
    c: Block(g3)
    c: Coincident(g5,g2)
    c: Coincident(g5,g3)
    c: Block(g0)
    c: Block(g5)
FEATURE [Sketcher::SketchObject] Sketch080  label="topSketch025"
  FullyConstrained = true
  sketch-geometry (6):
    g0: LineSegment StartX=19 StartY=38 StartZ=0 EndX=117 EndY=38 EndZ=0
    g1: ArcOfCircle CenterX=19 CenterY=19 CenterZ=0 NormalX=0 NormalY=0 NormalZ=1 AngleXU=0 Radius=19 StartAngle=1.5708 EndAngle=3.14159
    g2: LineSegment StartX=117 StartY=38 StartZ=0 EndX=117 EndY=19 EndZ=0
    g3: LineSegment StartX=98 StartY=1.0161e-12 StartZ=0 EndX=5.22862e-06 EndY=1.0161e-12 EndZ=0
    g4: LineSegment StartX=5.22862e-06 StartY=19 StartZ=0 EndX=5.22862e-06 EndY=1.0161e-12 EndZ=0
    g5: ArcOfCircle CenterX=98 CenterY=19 CenterZ=0 NormalX=0 NormalY=0 NormalZ=1 AngleXU=0 Radius=19 StartAngle=4.71239 EndAngle=6.28319
  constraints (16):
    c: Horizontal(g0)
    c: Distance(g0) = 98
    c: Coincident(g1,g0)
    c: Block(g1)
    c: Coincident(g2,g0)
    c: Vertical(g2)
    c: Distance(g2) = 19
    c: Horizontal(g3)
    c: Coincident(g4,g1)
    c: Vertical(g4)
    c: Coincident(g3,g4)
    c: Block(g3)
    c: Coincident(g5,g2)
    c: Coincident(g5,g3)
    c: Block(g0)
    c: Block(g5)
FEATURE [Part::Extrusion] Extrude070  label="sideA004"
  Base = -> Sketch080
  Dir = (0,0,1)
  DirMode = 2
  FaceMakerClass = Part::FaceMakerBullseye
  LengthFwd = 3
  LengthRev = 0
  Placement = pos=(0,0,-2.7) rot=(0,0,1;0rad)
  Solid = true
  Symmetric = false
FEATURE [Sketcher::SketchObject] Sketch081
  FullyConstrained = true
  Placement = pos=(117,19,0) rot=(0.57735,0.57735,0.57735;2.0944rad)
  sketch-geometry (8):
    g0: LineSegment StartX=-49.19 StartY=63.5 StartZ=0 EndX=-49.19 EndY=60.5 EndZ=0
    g1: LineSegment StartX=-49.19 StartY=11.5 StartZ=0 EndX=-49.19 EndY=8.5 EndZ=0
    g2: ArcOfCircle CenterX=-1.5 CenterY=62 CenterZ=0 NormalX=0 NormalY=0 NormalZ=1 AngleXU=0 Radius=1.5 StartAngle=4.71239 EndAngle=7.85398
    g3: ArcOfCircle CenterX=-1.5 CenterY=10 CenterZ=0 NormalX=0 NormalY=0 NormalZ=1 AngleXU=0 Radius=1.5 StartAngle=4.71239 EndAngle=7.85398
    g4: LineSegment StartX=-49.19 StartY=63.5 StartZ=0 EndX=-1.5 EndY=63.5 EndZ=0
    g5: LineSegment StartX=-49.19 StartY=60.5 StartZ=0 EndX=-1.5 EndY=60.5 EndZ=0
    g6: LineSegment StartX=-49.19 StartY=11.5 StartZ=0 EndX=-1.5 EndY=11.5 EndZ=0
    g7: LineSegment StartX=-49.19 StartY=8.5 StartZ=0 EndX=-1.5 EndY=8.5 EndZ=0
  constraints (19):
    c: Vertical(g0)
    c: Distance(g0) = 3
    c: Vertical(g1)
    c: Block(g1)
    c: Block(g2)
    c: Block(g3)
    c: Block(g0)
    c: Coincident(g4,g0)
    c: Coincident(g4,g2)
    c: Horizontal(g4)
    c: Coincident(g5,g0)
    c: Coincident(g5,g2)
    c: Horizontal(g5)
    c: Coincident(g6,g1)
    c: Coincident(g6,g3)
    c: Horizontal(g6)
    c: Coincident(g7,g1)
    c: Coincident(g7,g3)
    c: Horizontal(g7)
FEATURE [Part::Extrusion] Extrude071  label="sideB004"
  Base = -> Sketch079
  Dir = (0,0,1)
  DirMode = 2
  FaceMakerClass = Part::FaceMakerBullseye
  LengthFwd = 3
  LengthRev = 0
  Placement = pos=(0,0,71.7) rot=(0,0,1;0rad)
  Solid = true
  Symmetric = false
FEATURE [Part::MultiFuse] Fusion152  label="removeFromBottom004"
  Placement = pos=(2,0,0) rot=(0,0,1;0rad)
  Shapes = -> [Extrude070,Extrude071]
FEATURE [Part::Extrusion] Extrude072
  Base = -> Sketch081
  Dir = (1,0,0)
  DirMode = 2
  FaceMakerClass = Part::FaceMakerBullseye
  LengthFwd = 10
  LengthRev = 0
  Solid = true
  Symmetric = false
FEATURE [Part::Fillet] Fillet059  label="removeFromtMoreFrontCaseScrewRetainers004"
  Base = -> Extrude072
  Edges = 4 edges r=1.49: [Edge6,Edge11,Edge18,Edge23]
  Placement = pos=(-12,0,0) rot=(0,0,1;0rad)
FEATURE [Sketcher::SketchObject] Sketch082
  FullyConstrained = true
  Placement = pos=(117,19,0) rot=(0.57735,0.57735,0.57735;2.0944rad)
  sketch-geometry (8):
    g0: LineSegment StartX=-49.19 StartY=69.25 StartZ=0 EndX=-49.19 EndY=66.25 EndZ=0
    g1: LineSegment StartX=-49.19 StartY=5.75 StartZ=0 EndX=-49.19 EndY=2.75 EndZ=0
    g2: ArcOfCircle CenterX=-1.5 CenterY=67.75 CenterZ=0 NormalX=0 NormalY=0 NormalZ=1 AngleXU=0 Radius=1.5 StartAngle=4.71239 EndAngle=7.85398
    g3: ArcOfCircle CenterX=-1.5 CenterY=4.25 CenterZ=0 NormalX=0 NormalY=0 NormalZ=1 AngleXU=0 Radius=1.5 StartAngle=4.71239 EndAngle=7.85398
    g4: LineSegment StartX=-49.19 StartY=69.25 StartZ=0 EndX=-1.5 EndY=69.25 EndZ=0
    g5: LineSegment StartX=-49.19 StartY=66.25 StartZ=0 EndX=-1.5 EndY=66.25 EndZ=0
    g6: LineSegment StartX=-49.19 StartY=5.75 StartZ=0 EndX=-1.5 EndY=5.75 EndZ=0
    g7: LineSegment StartX=-49.19 StartY=2.75 StartZ=0 EndX=-1.5 EndY=2.75 EndZ=0
  constraints (19):
    c: Vertical(g0)
    c: Distance(g0) = 3
    c: Block(g0)
    c: Vertical(g1)
    c: Block(g2)
    c: Block(g3)
    c: Block(g1)
    c: Coincident(g4,g0)
    c: Coincident(g4,g2)
    c: Horizontal(g4)
    c: Coincident(g5,g0)
    c: Coincident(g5,g2)
    c: Horizontal(g5)
    c: Coincident(g6,g1)
    c: Coincident(g6,g3)
    c: Horizontal(g6)
    c: Coincident(g7,g1)
    c: Coincident(g7,g3)
    c: Horizontal(g7)
FEATURE [Part::Extrusion] Extrude073
  Base = -> Sketch082
  Dir = (1,0,0)
  DirMode = 2
  FaceMakerClass = Part::FaceMakerBullseye
  LengthFwd = 10
  LengthRev = 0
  Solid = true
  Symmetric = false
FEATURE [Part::Fillet] Fillet060  label="removeFromtMoreFrontCaseScrewRetainers005"
  Base = -> Extrude073
  Edges = 4 edges r=1.49: [Edge6,Edge11,Edge18,Edge23]
  Placement = pos=(-4,0,0) rot=(0,0,1;0rad)
FEATURE [Part::Revolution] Revolve163  label="backCaseScrewRetainer004"
  Angle = 360
  Axis = (0,1,0)
  Base = (0,0,0)
  FaceMakerClass = Part::FaceMakerBullseye
  Placement = pos=(12.5,3,62) rot=(0,0,1;0rad)
  Solid = false
  Source = -> Face149
  Symmetric = false
FEATURE [Part::Revolution] Revolve164  label="frontCaseScrewRetainer006"
  Angle = 360
  Axis = (0,1,0)
  Base = (0,0,0)
  FaceMakerClass = Part::FaceMakerBullseye
  Placement = pos=(89.5,3,68.5) rot=(0,0,1;0rad)
  Solid = false
  Source = -> Face151
  Symmetric = false
FEATURE [Part::Revolution] Revolve165  label="frontCaseScrewRetainer007"
  Angle = 360
  Axis = (0,1,0)
  Base = (0,0,0)
  FaceMakerClass = Part::FaceMakerBullseye
  Placement = pos=(89.5,3,3.5) rot=(0,0,1;0rad)
  Solid = false
  Source = -> Face152
  Symmetric = false
FEATURE [Part::Revolution] Revolve166  label="backCaseScrewRetainer005"
  Angle = 360
  Axis = (0,1,0)
  Base = (0,0,0)
  FaceMakerClass = Part::FaceMakerBullseye
  Placement = pos=(12.5,3,10) rot=(0,0,1;0rad)
  Solid = false
  Source = -> Face150
  Symmetric = false
FEATURE [Part::Revolution] Revolve167  label="moreFrontCaseScrewRetainer006"
  Angle = 360
  Axis = (0,1,0)
  Base = (0,0,0)
  FaceMakerClass = Part::FaceMakerBullseye
  Placement = pos=(109.5,4.5,68.5) rot=(0,0,1;0rad)
  Solid = false
  Source = -> Face153
  Symmetric = false
FEATURE [Part::Revolution] Revolve168  label="moreFrontCaseScrewRetainer007"
  Angle = 360
  Axis = (0,1,0)
  Base = (0,0,0)
  FaceMakerClass = Part::FaceMakerBullseye
  Placement = pos=(109.5,4.5,3.5) rot=(0,0,1;0rad)
  Solid = false
  Source = -> Face154
  Symmetric = false
FEATURE [Part::MultiFuse] Fusion151  label="screwRetainers003"
  Shapes = -> [Revolve168,Revolve167,Revolve166,Revolve165,Revolve164,Revolve163]
FEATURE [Part::Cut] Cut069  label="screwRetainers004"
  Base = -> Fusion151
  Tool = -> Fusion152
FEATURE [Part::Cut] Cut070
  Base = -> Cut069
  Tool = -> Fillet060
FEATURE [Part::Cut] Cut071  label="screwPillars001"
  Base = -> Cut070
  Tool = -> Fillet059
FEATURE [Part::MultiFuse] Fusion153  label="bottom024"
  Shapes = -> [Fusion149,Cut071]
FEATURE [Part::Cylinder] Cylinder067
  Angle = 360
  AttacherType = Attacher::AttachEngine3D
  Height = 10
  Placement = pos=(20.65,12,4.68) rot=(1,0,0;1.5708rad)
  Radius = 2
FEATURE [Part::Cylinder] Cylinder068
  Angle = 360
  AttacherType = Attacher::AttachEngine3D
  Height = 10
  Placement = pos=(20.65,12,67.38) rot=(1,0,0;1.5708rad)
  Radius = 2
FEATURE [Part::Cylinder] Cylinder069
  Angle = 360
  AttacherType = Attacher::AttachEngine3D
  Height = 10
  Placement = pos=(77.15,12,67.38) rot=(1,0,0;1.5708rad)
  Radius = 2
FEATURE [Part::Cylinder] Cylinder070
  Angle = 360
  AttacherType = Attacher::AttachEngine3D
  Height = 10
  Placement = pos=(77.15,12,4.68) rot=(1,0,0;1.5708rad)
  Radius = 2
FEATURE [Part::MultiFuse] Fusion154  label="removeFromThreadedInsertHousing001"
  Shapes = -> [Cylinder069,Cylinder068,Cylinder067,Cylinder070]
FEATURE [Part::Cut] Cut072  label="bottom025"
  Base = -> Fusion153
  Tool = -> Fusion154
FEATURE [Image::ImagePlane] ImagePlane
  XSize = 339
  YSize = 72
FEATURE [Sketcher::SketchObject] Sketch083
  FullyConstrained = false
  MapMode = 5
  Support = -> [XY_Plane]
  sketch-geometry (247):
    g0: LineSegment StartX=-151.619 StartY=28.8932 StartZ=0 EndX=-140.819 EndY=28.8932 EndZ=0
    g1: LineSegment StartX=-151.619 StartY=24.0313 StartZ=0 EndX=-151.619 EndY=28.8932 EndZ=0
    g2: LineSegment StartX=-140.819 StartY=17.7713 StartZ=0 EndX=-151.619 EndY=17.7713 EndZ=0
    g3: LineSegment StartX=-151.619 StartY=17.7713 StartZ=0 EndX=-151.619 EndY=22.6313 EndZ=0
    g4: LineSegment StartX=-151.619 StartY=22.6313 StartZ=0 EndX=-145.128 EndY=22.6313 EndZ=0
    g5: LineSegment StartX=-145.128 StartY=24.0313 StartZ=0 EndX=-140.819 EndY=28.8932 EndZ=0
    g6: LineSegment StartX=-145.128 StartY=22.6313 StartZ=0 EndX=-140.819 EndY=17.7713 EndZ=0
    g7: ArcOfCircle CenterX=-155.157 CenterY=23.3323 CenterZ=0 NormalX=0 NormalY=0 NormalZ=1 AngleXU=0 Radius=6.92354 StartAngle=1.03434 EndAngle=5.24885
    g8: ArcOfCircle CenterX=-155.157 CenterY=23.3323 CenterZ=0 NormalX=0 NormalY=0 NormalZ=1 AngleXU=0 Radius=12.6269 StartAngle=1.28675 EndAngle=4.99643
    g9: LineSegment StartX=-151.619 StartY=35.4532 StartZ=0 EndX=-151.619 EndY=29.2832 EndZ=0
    g10: LineSegment StartX=-151.619 StartY=17.3813 StartZ=0 EndX=-151.619 EndY=11.2113 EndZ=0
    g11-g21: Circle x11 (B-spline internal-alignment scaffolding for g22; pole/knot coordinates omitted)
    g22: BSplineCurve PolesCount=11 KnotsCount=9 Degree=3 IsPeriodic=0
    g23-g31: GeomPoint x9 (B-spline internal-alignment scaffolding for g22; pole/knot coordinates omitted)
    g32-g49: Circle x18 (B-spline internal-alignment scaffolding for g50; pole/knot coordinates omitted)
    g50: BSplineCurve PolesCount=18 KnotsCount=16 Degree=3 IsPeriodic=0
    g51-g66: GeomPoint x16 (B-spline internal-alignment scaffolding for g50; pole/knot coordinates omitted)
    g67: LineSegment StartX=-117.124 StartY=30.093 StartZ=0 EndX=-117.603 EndY=26.5272 EndZ=0
    g68: LineSegment StartX=-117.603 StartY=17.8472 StartZ=0 EndX=-117.124 EndY=14.2659 EndZ=0
    g69: Ellipse CenterX=-109.671 CenterY=20.025 CenterZ=0 NormalX=0 NormalY=0 NormalZ=1 MajorRadius=3.34798 MinorRadius=2.71052 AngleXU=-1.56793
    g70: GeomPoint X=-109.666 Y=18.0598 Z=0
    g71: GeomPoint X=-109.677 Y=21.9902 Z=0
    g72: Ellipse CenterX=-109.671 CenterY=20.0123 CenterZ=0 NormalX=0 NormalY=0 NormalZ=1 MajorRadius=6.93002 MinorRadius=6.36273 AngleXU=-3.13976
    g73: GeomPoint X=-112.417 Y=20.0073 Z=0
    g74: GeomPoint X=-106.925 Y=20.0173 Z=0
    g75: Ellipse CenterX=-51.7682 CenterY=20.1463 CenterZ=0 NormalX=0 NormalY=0 NormalZ=1 MajorRadius=3.19279 MinorRadius=2.71052 AngleXU=-1.52774
    g76: GeomPoint X=-51.6955 Y=18.4606 Z=0
    g77: GeomPoint X=-51.8408 Y=21.832 Z=0
    g78: GeomPoint X=-54.5142 Y=20.1413 Z=0
    g79: GeomPoint X=-49.0221 Y=20.1513 Z=0
    g80: Ellipse CenterX=-51.7682 CenterY=20.1463 CenterZ=0 NormalX=0 NormalY=0 NormalZ=1 MajorRadius=6.93002 MinorRadius=6.36273 AngleXU=-3.13976
    g81: Ellipse CenterX=-22.8436 CenterY=20.1783 CenterZ=0 NormalX=0 NormalY=0 NormalZ=1 MajorRadius=3.31512 MinorRadius=2.71052 AngleXU=-1.60214
    g82: GeomPoint X=-22.9034 Y=18.2706 Z=0
    g83: GeomPoint X=-22.7838 Y=22.0861 Z=0
    g84: GeomPoint X=-25.5897 Y=20.1733 Z=0
    g85: GeomPoint X=-20.0976 Y=20.1833 Z=0
    g86: Ellipse CenterX=-22.8436 CenterY=20.1783 CenterZ=0 NormalX=0 NormalY=0 NormalZ=1 MajorRadius=6.93002 MinorRadius=6.36273 AngleXU=-3.13976
    g87: LineSegment StartX=-101.889 StartY=14.1107 StartZ=0 EndX=-97.7455 EndY=14.1107 EndZ=0
    g88: LineSegment StartX=-93.8155 StartY=14.1107 StartZ=0 EndX=-89.6755 EndY=14.1107 EndZ=0
    g89: LineSegment StartX=-85.7455 StartY=14.1107 StartZ=0 EndX=-81.6055 EndY=14.1107 EndZ=0
    g90: LineSegment StartX=-101.889 StartY=14.1107 StartZ=0 EndX=-101.889 EndY=25.9907 EndZ=0
    g91: LineSegment StartX=-101.889 StartY=25.9907 StartZ=0 EndX=-97.8594 EndY=25.9907 EndZ=0
    g92: LineSegment StartX=-97.8594 StartY=25.9907 StartZ=0 EndX=-97.8594 EndY=24.0907 EndZ=0
    g93: LineSegment StartX=-97.7455 StartY=14.1107 StartZ=0 EndX=-97.7455 EndY=19.9107 EndZ=0
    g94: LineSegment StartX=-89.6755 StartY=14.1107 StartZ=0 EndX=-89.6755 EndY=19.9107 EndZ=0
    g95: LineSegment StartX=-93.8155 StartY=14.1107 StartZ=0 EndX=-93.8155 EndY=21.0107 EndZ=0
    g96-g106: Circle x11 (B-spline internal-alignment scaffolding for g107; pole/knot coordinates omitted)
    g107: BSplineCurve PolesCount=11 KnotsCount=9 Degree=3 IsPeriodic=0
    g108-g116: GeomPoint x9 (B-spline internal-alignment scaffolding for g107; pole/knot coordinates omitted)
    g117: BSplineCurve PolesCount=11 KnotsCount=9 Degree=3 IsPeriodic=0
    g118-g125: Circle x8 (B-spline internal-alignment scaffolding for g126; pole/knot coordinates omitted)
    g126: BSplineCurve PolesCount=8 KnotsCount=6 Degree=3 IsPeriodic=0
    g127-g132: GeomPoint x6 (B-spline internal-alignment scaffolding for g126; pole/knot coordinates omitted)
    g133: BSplineCurve PolesCount=8 KnotsCount=6 Degree=3 IsPeriodic=0
    g134: LineSegment StartX=-85.7455 StartY=21.0107 StartZ=0 EndX=-85.7455 EndY=14.1107 EndZ=0
    g135: LineSegment StartX=-80.0879 StartY=14.1107 StartZ=0 EndX=-75.944 EndY=14.1107 EndZ=0
    g136: LineSegment StartX=-72.014 StartY=14.1107 StartZ=0 EndX=-67.874 EndY=14.1107 EndZ=0
    g137: LineSegment StartX=-63.944 StartY=14.1107 StartZ=0 EndX=-59.804 EndY=14.1107 EndZ=0
    g138: LineSegment StartX=-80.0879 StartY=14.1107 StartZ=0 EndX=-80.0879 EndY=25.9907 EndZ=0
    g139: LineSegment StartX=-80.0879 StartY=25.9907 StartZ=0 EndX=-76.0579 EndY=25.9907 EndZ=0
    g140: LineSegment StartX=-76.0579 StartY=25.9907 StartZ=0 EndX=-76.0579 EndY=24.0907 EndZ=0
    g141: LineSegment StartX=-75.944 StartY=14.1107 StartZ=0 EndX=-75.944 EndY=19.9107 EndZ=0
    g142: LineSegment StartX=-67.874 StartY=14.1107 StartZ=0 EndX=-67.874 EndY=19.9107 EndZ=0
    g143: LineSegment StartX=-72.014 StartY=14.1107 StartZ=0 EndX=-72.014 EndY=21.0107 EndZ=0
    g144-g148: Circle x5 (B-spline internal-alignment scaffolding for g149; pole/knot coordinates omitted)
    g149: BSplineCurve PolesCount=11 KnotsCount=9 Degree=3 IsPeriodic=0
    g150-g158: GeomPoint x9 (B-spline internal-alignment scaffolding for g149; pole/knot coordinates omitted)
    g159: BSplineCurve PolesCount=11 KnotsCount=9 Degree=3 IsPeriodic=0
    g160-g167: Circle x8 (B-spline internal-alignment scaffolding for g168; pole/knot coordinates omitted)
    g168: BSplineCurve PolesCount=8 KnotsCount=6 Degree=3 IsPeriodic=0
    g169-g174: GeomPoint x6 (B-spline internal-alignment scaffolding for g168; pole/knot coordinates omitted)
    g175: BSplineCurve PolesCount=8 KnotsCount=6 Degree=3 IsPeriodic=0
    g176: LineSegment StartX=-63.944 StartY=21.0107 StartZ=0 EndX=-63.944 EndY=14.1107 EndZ=0
    g177: LineSegment StartX=-59.804 StartY=14.1107 StartZ=0 EndX=-59.804 EndY=21.5868 EndZ=0
    g178: BSplineCurve PolesCount=4 KnotsCount=2 Degree=3 IsPeriodic=0
    g179: GeomPoint X=-59.804 Y=21.5868 Z=0
    g180: GeomPoint X=-60.2379 Y=24.0907 Z=0
    g181: LineSegment StartX=-81.6055 StartY=14.1107 StartZ=0 EndX=-81.6055 EndY=21.5868 EndZ=0
    g182: LineSegment StartX=-151.619 StartY=24.0313 StartZ=0 EndX=-145.128 EndY=24.0313 EndZ=0
    g183: Circle CenterX=-82.0394 CenterY=24.0907 CenterZ=0 NormalX=0 NormalY=0 NormalZ=1 AngleXU=0 Radius=1
    g184: Circle CenterX=-81.7131 CenterY=23.2736 CenterZ=0 NormalX=0 NormalY=0 NormalZ=1 AngleXU=0 Radius=1
    g185: Circle CenterX=-81.6055 CenterY=21.5868 CenterZ=0 NormalX=0 NormalY=0 NormalZ=1 AngleXU=0 Radius=1
    g186: BSplineCurve PolesCount=3 KnotsCount=2 Degree=2 IsPeriodic=0
    g187: GeomPoint X=-82.0394 Y=24.0907 Z=0
    g188: GeomPoint X=-81.6055 Y=21.5868 Z=0
    g189: Ellipse CenterX=-37.3522 CenterY=19.9515 CenterZ=0 NormalX=0 NormalY=0 NormalZ=1 MajorRadius=2.99755 MinorRadius=2.49 AngleXU=1.5708
    g190: GeomPoint X=-37.3522 Y=21.6203 Z=0
    g191: GeomPoint X=-37.3522 Y=18.2826 Z=0
    g192: ArcOfEllipse CenterX=-38.7647 CenterY=20.06 CenterZ=0 NormalX=0 NormalY=0 NormalZ=1 MajorRadius=6.30025 MinorRadius=5.3849 AngleXU=1.57276 StartAngle=5.50632 EndAngle=10.3035
    g193: GeomPoint X=-38.7711 Y=23.3304 Z=0
    g194: GeomPoint X=-38.7583 Y=16.7895 Z=0
    g195: LineSegment StartX=-34.6109 StartY=14.1107 StartZ=0 EndX=-30.8984 EndY=14.1107 EndZ=0
    g196: LineSegment StartX=-30.8984 StartY=14.1107 StartZ=0 EndX=-30.8984 EndY=31.1784 EndZ=0
    g197: LineSegment StartX=-30.8984 StartY=31.1784 StartZ=0 EndX=-34.9984 EndY=31.1784 EndZ=0
    g198: LineSegment StartX=-34.9984 StartY=24.5602 StartZ=0 EndX=-34.9984 EndY=31.1784 EndZ=0
    g199: LineSegment StartX=-34.6109 StartY=16.0476 StartZ=0 EndX=-34.6109 EndY=14.1107 EndZ=0
    g200: LineSegment StartX=-14.8781 StartY=14.1107 StartZ=0 EndX=-10.5106 EndY=14.1107 EndZ=0
    g201: LineSegment StartX=-14.8781 StartY=14.1107 StartZ=0 EndX=-14.8781 EndY=25.8504 EndZ=0
    g202: LineSegment StartX=-14.8781 StartY=25.8504 StartZ=0 EndX=-10.8534 EndY=25.8504 EndZ=0
    g203: LineSegment StartX=-10.8534 StartY=25.8504 StartZ=0 EndX=-10.8534 EndY=24.0923 EndZ=0
    g204: LineSegment StartX=-10.5106 StartY=14.1107 StartZ=0 EndX=-10.5106 EndY=19.7752 EndZ=0
    g205: LineSegment StartX=-5.96397 StartY=25.9304 StartZ=0 EndX=-5.96397 EndY=22.574 EndZ=0
    g206-g214: Circle x9 (B-spline internal-alignment scaffolding for g215; pole/knot coordinates omitted)
    g215: BSplineCurve PolesCount=9 KnotsCount=7 Degree=3 IsPeriodic=0
    g216-g222: GeomPoint x7 (B-spline internal-alignment scaffolding for g215; pole/knot coordinates omitted)
    g223-g232: Circle x10 (B-spline internal-alignment scaffolding for g233; pole/knot coordinates omitted)
    g233: BSplineCurve PolesCount=10 KnotsCount=8 Degree=3 IsPeriodic=0
    g234-g241: GeomPoint x8 (B-spline internal-alignment scaffolding for g233; pole/knot coordinates omitted)
    g242: LineSegment StartX=-1.58923 StartY=21.0696 StartZ=0 EndX=2.62034 EndY=21.0696 EndZ=0
    g243: LineSegment StartX=-1.55856 StartY=18.7342 StartZ=0 EndX=6.45946 EndY=18.7342 EndZ=0
    g244: LineSegment StartX=5.29231 StartY=17.386 StartZ=0 EndX=5.29231 EndY=14.3674 EndZ=0
    g245: LineSegment StartX=0.528324 StartY=26.3804 StartZ=0 EndX=0.528324 EndY=13.5804 EndZ=0
    g246: LineSegment StartX=4.73799 StartY=26.9223 StartZ=0 EndX=4.73799 EndY=20.5223 EndZ=0
  constraints (236):
    c: Coincident(g1,g0)
    c: Horizontal(g0)
    c: Vertical(g1)
    c: Coincident(g2,g3)
    c: Coincident(g3,g4)
    c: Horizontal(g4)
    c: Horizontal(g2)
    c: Vertical(g3)
    c: Block(g1)
    c: Distance(g3) = 4.86
    c: Block(g4)
    c: Distance(g0) = 10.8
    c: Distance(g2) = 10.8
    c: Coincident(g5,g0)
    c: Coincident(g6,g4)
    c: Coincident(g6,g2)
    c: Block(g8)
    c: Block(g7)
    c: Coincident(g9,g8)
    c: Coincident(g9,g7)
    c: Vertical(g9)
    c: Coincident(g10,g7)
    c: Coincident(g10,g8)
    c: Vertical(g10)
    c: Weight(g11) = 1
    c: Equal(g11, g12-g21) x10
    c: InternalAlignment(g11-g21 -> g22) x11
    c: InternalAlignment(g23-g31 -> g22) x9
    c: Block(g22)
    c: Weight(g32) = 1
    c: Equal(g32, g33-g49) x17
    c: InternalAlignment(g32-g49 -> g50) x18
    c: InternalAlignment(g51-g66 -> g50) x16
    c: Block(g50)
    c: Coincident(g67,g50)
    c: Coincident(g67,g22)
    c: Coincident(g68,g22)
    c: Coincident(g68,g50)
    c: InternalAlignment(g70,g69)
    c: InternalAlignment(g71,g69)
    c: Block(g69)
    c: InternalAlignment(g73,g72)
    c: InternalAlignment(g74,g72)
    c: Block(g72)
    c: InternalAlignment(g76,g75)
    c: InternalAlignment(g77,g75)
    c: InternalAlignment(g78,g80)
    c: InternalAlignment(g79,g80)
    c: Block(g80)
    c: Coincident(g75,g80)
    c: Block(g75)
    c: InternalAlignment(g82,g81)
    c: InternalAlignment(g83,g81)
    c: InternalAlignment(g84,g86)
    c: InternalAlignment(g85,g86)
    c: Block(g86)
    c: Coincident(g81,g86)
    c: Block(g81)
    c: Horizontal(g87)
    c: Block(g87)
    c: Horizontal(g88)
    c: Distance(g88) = 4.14
    c: Horizontal(g89)
    c: Equal(g88,g89) = 4.14
    c: Block(g89)
    c: Block(g88)
    c: Coincident(g90,g87)
    c: Vertical(g90)
    c: Distance(g90) = 11.88
    c: Coincident(g91,g90)
    c: Horizontal(g91)
    c: Coincident(g92,g91)
    c: Vertical(g92)
    c: Distance(g91) = 4.03
    c: Distance(g92) = 1.9
    c: Coincident(g93,g87)
    c: Vertical(g93)
    c: Vertical(g94)
    c: Coincident(g94,g88)
    c: Distance(g93) = 5.8
    c: Distance(g94) = 5.8
    c: Vertical(g95)
    c: Coincident(g95,g88)
    c: Distance(g95) = 6.9
    c: Coincident(g107,g92)
    c: Weight(g96) = 1
    c: Equal(g96, g97-g106) x10
    c: InternalAlignment(g96-g106 -> g107) x11
    c: InternalAlignment(g108-g116 -> g107) x9
    c: Block(g107)
    c: Block(g117)
    c: Coincident(g126,g93)
    c: Weight(g118) = 1
    c: Equal(g118, g119-g125) x7
    c: Coincident(g126,g95)
    c: InternalAlignment(g118-g125 -> g126) x8
    c: InternalAlignment(g127-g132 -> g126) x6
    c: Coincident(g133,g94)
    c: Block(g126)
    c: Block(g133)
    c: Coincident(g134,g133)
    c: Coincident(g134,g89)
    c: Vertical(g134)
    c: Horizontal(g135)
    c: Block(g135)
    c: Horizontal(g136)
    c: Equal(g88,g136) = 4.14
    c: Horizontal(g137)
    c: Equal(g136,g137) = 4.14
    c: Block(g137)
    c: Block(g136)
    c: Coincident(g138,g135)
    c: Vertical(g138)
    c: Equal(g90,g138) = 11.88
    c: Coincident(g139,g138)
    c: Horizontal(g139)
    c: Coincident(g140,g139)
    c: Vertical(g140)
    c: Equal(g91,g139) = 4.03
    c: Equal(g92,g140) = 1.9
    c: Coincident(g141,g135)
    c: Vertical(g141)
    c: Vertical(g142)
    c: Coincident(g142,g136)
    c: Equal(g93,g141) = 5.8
    c: Equal(g94,g142) = 5.8
    c: Vertical(g143)
    c: Coincident(g143,g136)
    c: Equal(g95,g143) = 6.9
    c: Coincident(g149,g140)
    c: Equal(g96,g144) = 1
    c: Equal(g144, g145-g148) x4
    c: InternalAlignment(g144-g148 -> g149) x5
    c: InternalAlignment(g150-g158 -> g149) x9
    c: Block(g149)
    c: Block(g159)
    c: Coincident(g168,g141)
    c: Equal(g118,g160) = 1
    c: Equal(g160, g161-g167) x7
    c: Coincident(g168,g143)
    c: InternalAlignment(g160-g167 -> g168) x8
    c: InternalAlignment(g169-g174 -> g168) x6
    c: Coincident(g175,g142)
    c: Block(g168)
    c: Block(g175)
    c: Coincident(g176,g175)
    c: Coincident(g176,g137)
    c: Vertical(g176)
    c: Coincident(g177,g137)
    c: Vertical(g177)
    c: Coincident(g178,g177)
    c: Coincident(g178,g159)
    c: InternalAlignment(g179,g178)
    c: InternalAlignment(g180,g178)
    c: Block(g178)
    c: Vertical(g181)
    c: Coincident(g181,g89)
    c: Block(g5)
    c: Coincident(g182,g1)
    c: Coincident(g182,g5)
    c: Horizontal(g182)
    c: Coincident(g186,g117)
    c: Weight(g183) = 1
    c: Equal(g183,g184)
    c: Equal(g183,g185)
    c: Coincident(g186,g181)
    c: InternalAlignment(g183,g186)
    c: InternalAlignment(g184,g186)
    c: InternalAlignment(g185,g186)
    c: InternalAlignment(g187,g186)
    c: InternalAlignment(g188,g186)
    c: Block(g186)
    c: InternalAlignment(g190,g189)
    c: InternalAlignment(g191,g189)
    c: Block(g189)
    c: InternalAlignment(g193,g192)
    c: InternalAlignment(g194,g192)
    c: Block(g192)
    c: Horizontal(g195)
    c: Block(g195)
    c: Coincident(g196,g195)
    c: Vertical(g196)
    c: Block(g196)
    c: Distance(g195) = 3.71244
    c: Coincident(g197,g196)
    c: Horizontal(g197)
    c: Distance(g197) = 4.1
    c: Coincident(g198,g192)
    c: Coincident(g198,g197)
    c: Vertical(g198)
    c: Block(g198)
    c: Coincident(g199,g192)
    c: Coincident(g199,g195)
    c: Vertical(g199)
    c: Block(g199)
    c: Horizontal(g200)
    c: Block(g200)
    c: Coincident(g201,g200)
    c: Vertical(g201)
    c: Block(g201)
    c: Coincident(g202,g201)
    c: Horizontal(g202)
    c: Block(g202)
    c: Coincident(g203,g202)
    c: Vertical(g203)
    c: Block(g203)
    c: Coincident(g204,g200)
    c: Vertical(g204)
    c: Block(g204)
    c: Coincident(g215,g203)
    c: Weight(g206) = 1
    c: Equal(g206, g207-g214) x8
    c: Coincident(g215,g205)
    c: InternalAlignment(g206-g214 -> g215) x9
    c: InternalAlignment(g216-g222 -> g215) x7
    c: Coincident(g233,g204)
    c: Weight(g223) = 1
    c: Equal(g223, g224-g232) x9
    c: Coincident(g233,g205)
    c: InternalAlignment(g223-g232 -> g233) x10
    c: InternalAlignment(g234-g241 -> g233) x8
    c: Vertical(g205)
    c: Block(g205)
    c: Block(g215)
    c: Block(g233)
    c: Horizontal(g242)
    c: Horizontal(g243)
    c: Block(g242)
    c: Block(g243)
    c: Vertical(g244)
    c: Block(g244)
    c: Vertical(g245)
    c: Distance(g245) = 12.8
    c: Vertical(g246)
    c: Distance(g246) = 6.4
    c: Block(g245)
FEATURE [PartDesign::Body] Body
  Group = -> [Sketch083]
  Origin = -> Origin
FEATURE [Sketcher::SketchObject] Sketch084
  FullyConstrained = true
  MapMode = 5
  Support = -> [XY_Plane001]
FEATURE [PartDesign::Body] Body001
  Group = -> [Sketch084]
  Origin = -> Origin001
